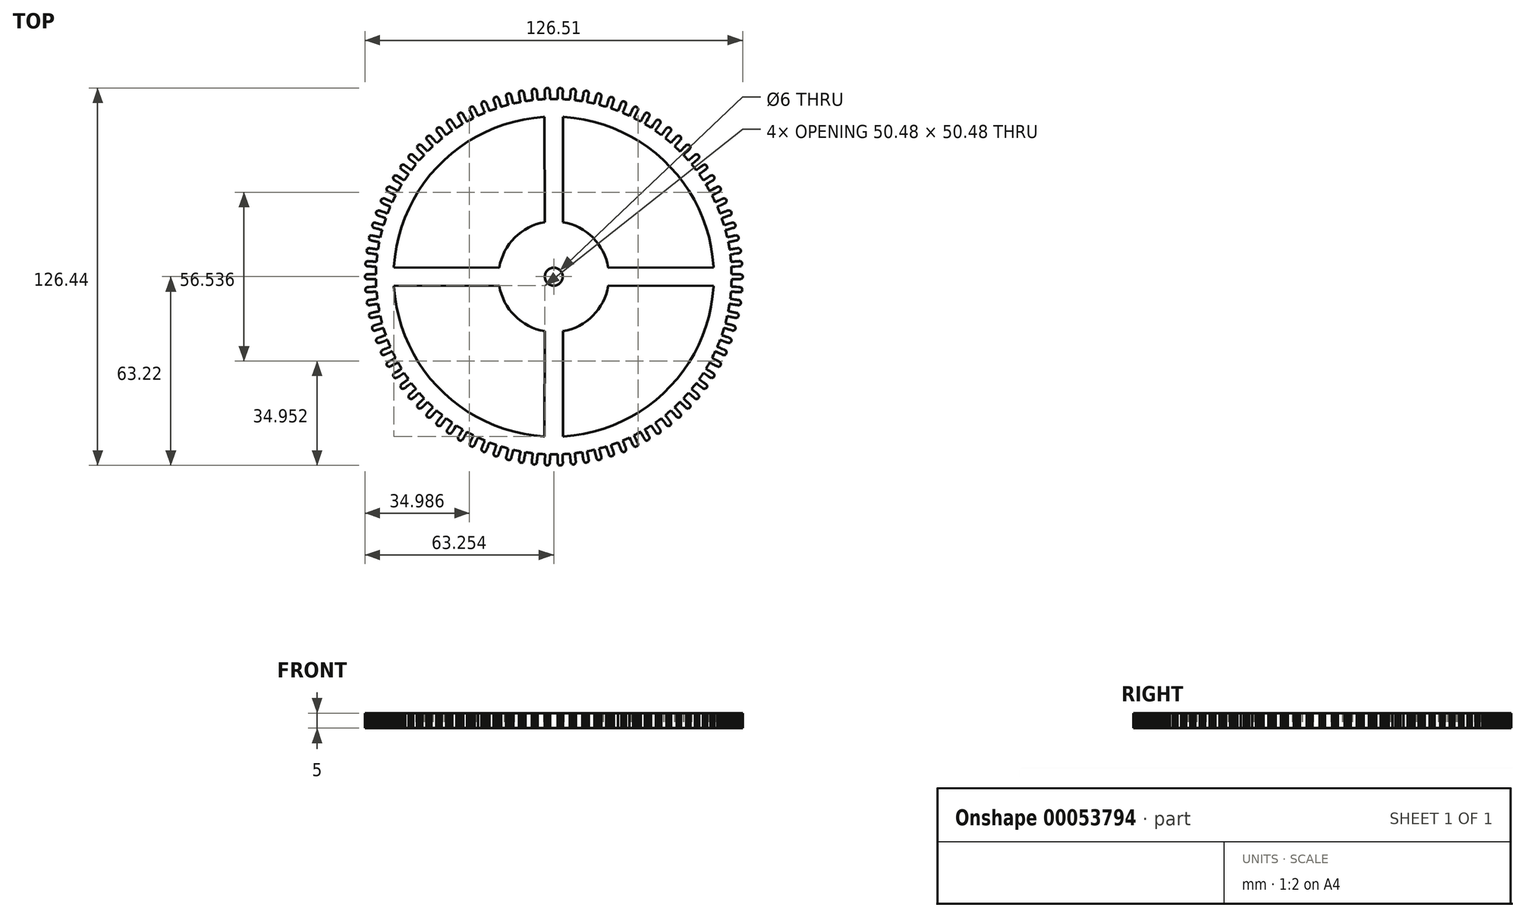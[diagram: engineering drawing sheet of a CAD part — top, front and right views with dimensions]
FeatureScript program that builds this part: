
annotation { "Feature Type Name" : "Feature", "Feature Type Description" : "" }
export const myFeature = defineFeature(function(context is Context, id is Id, definition is map)
    precondition{}
    {
        {
            var Q0;
            Q0=qCreatedBy(makeId("Top.planeOp"),FACE);
            var sketch = newSketch(context, id + "F0", { "sketchPlane" : qUnion([Q0])});
            skLineSegment(sketch, "E0", {"start": v(58.52, -0.83) * mm, "end": v(58.71, -0.83) * mm});
            skLineSegment(sketch, "E1", {"start": v(58.71, -0.83) * mm, "end": v(58.93, -0.83) * mm});
            skLineSegment(sketch, "E2", {"start": v(58.93, -0.83) * mm, "end": v(59.15, -0.84) * mm});
            skLineSegment(sketch, "E3", {"start": v(59.15, -0.84) * mm, "end": v(59.37, -0.84) * mm});
            skLineSegment(sketch, "E4", {"start": v(59.37, -0.84) * mm, "end": v(59.59, -0.84) * mm});
            skLineSegment(sketch, "E5", {"start": v(59.59, -0.84) * mm, "end": v(59.8, -0.85) * mm});
            skLineSegment(sketch, "E6", {"start": v(59.8, -0.85) * mm, "end": v(60.03, -0.85) * mm});
            skLineSegment(sketch, "E7", {"start": v(60.03, -0.85) * mm, "end": v(60.25, -0.85) * mm});
            skLineSegment(sketch, "E8", {"start": v(60.25, -0.85) * mm, "end": v(60.47, -0.85) * mm});
            skLineSegment(sketch, "E9", {"start": v(60.47, -0.85) * mm, "end": v(60.7, -0.86) * mm});
            skLineSegment(sketch, "E10", {"start": v(60.7, -0.86) * mm, "end": v(60.9, -0.86) * mm});
            skLineSegment(sketch, "E11", {"start": v(60.9, -0.86) * mm, "end": v(61.13, -0.86) * mm});
            skLineSegment(sketch, "E12", {"start": v(61.13, -0.86) * mm, "end": v(61.35, -0.87) * mm});
            skLineSegment(sketch, "E13", {"start": v(61.35, -0.87) * mm, "end": v(61.58, -0.84) * mm});
            skLineSegment(sketch, "E14", {"start": v(61.58, -0.84) * mm, "end": v(61.79, -0.75) * mm});
            skLineSegment(sketch, "E15", {"start": v(61.79, -0.75) * mm, "end": v(61.97, -0.62) * mm});
            skLineSegment(sketch, "E16", {"start": v(61.97, -0.62) * mm, "end": v(62.1, -0.44) * mm});
            skLineSegment(sketch, "E17", {"start": v(62.1, -0.44) * mm, "end": v(62.2, -0.23) * mm});
            skLineSegment(sketch, "E18", {"start": v(62.2, -0.23) * mm, "end": v(62.22, 0) * mm});
            skLineSegment(sketch, "E19", {"start": v(62.22, 0) * mm, "end": v(62.2, 0.23) * mm});
            skLineSegment(sketch, "E20", {"start": v(62.2, 0.23) * mm, "end": v(62.1, 0.44) * mm});
            skLineSegment(sketch, "E21", {"start": v(62.1, 0.44) * mm, "end": v(61.97, 0.62) * mm});
            skLineSegment(sketch, "E22", {"start": v(61.97, 0.62) * mm, "end": v(61.79, 0.75) * mm});
            skLineSegment(sketch, "E23", {"start": v(61.79, 0.75) * mm, "end": v(61.58, 0.84) * mm});
            skLineSegment(sketch, "E24", {"start": v(61.58, 0.84) * mm, "end": v(61.35, 0.87) * mm});
            skLineSegment(sketch, "E25", {"start": v(61.35, 0.87) * mm, "end": v(61.13, 0.86) * mm});
            skLineSegment(sketch, "E26", {"start": v(61.13, 0.86) * mm, "end": v(60.91, 0.86) * mm});
            skLineSegment(sketch, "E27", {"start": v(60.91, 0.86) * mm, "end": v(60.7, 0.86) * mm});
            skLineSegment(sketch, "E28", {"start": v(60.7, 0.86) * mm, "end": v(60.47, 0.85) * mm});
            skLineSegment(sketch, "E29", {"start": v(60.47, 0.85) * mm, "end": v(60.25, 0.85) * mm});
            skLineSegment(sketch, "E30", {"start": v(60.25, 0.85) * mm, "end": v(60.03, 0.85) * mm});
            skLineSegment(sketch, "E31", {"start": v(60.03, 0.85) * mm, "end": v(59.81, 0.85) * mm});
            skLineSegment(sketch, "E32", {"start": v(59.81, 0.85) * mm, "end": v(59.6, 0.84) * mm});
            skLineSegment(sketch, "E33", {"start": v(59.6, 0.84) * mm, "end": v(59.37, 0.84) * mm});
            skLineSegment(sketch, "E34", {"start": v(59.37, 0.84) * mm, "end": v(59.15, 0.84) * mm});
            skLineSegment(sketch, "E35", {"start": v(59.15, 0.84) * mm, "end": v(58.94, 0.83) * mm});
            skLineSegment(sketch, "E36", {"start": v(58.94, 0.83) * mm, "end": v(58.71, 0.83) * mm});
            skLineSegment(sketch, "E37", {"start": v(58.71, 0.83) * mm, "end": v(58.52, 0.83) * mm});
            skLineSegment(sketch, "E38", {"start": v(58.52, 0.83) * mm, "end": v(58.52, 1.05) * mm});
            skLineSegment(sketch, "E39", {"start": v(58.52, 1.05) * mm, "end": v(58.5, 1.26) * mm});
            skLineSegment(sketch, "E40", {"start": v(58.5, 1.26) * mm, "end": v(58.5, 1.48) * mm});
            skLineSegment(sketch, "E41", {"start": v(58.5, 1.48) * mm, "end": v(58.5, 1.7) * mm});
            skLineSegment(sketch, "E42", {"start": v(58.5, 1.7) * mm, "end": v(58.48, 1.92) * mm});
            skLineSegment(sketch, "E43", {"start": v(58.48, 1.92) * mm, "end": v(58.48, 2.13) * mm});
            skLineSegment(sketch, "E44", {"start": v(58.48, 2.13) * mm, "end": v(58.47, 2.35) * mm});
            skLineSegment(sketch, "E45", {"start": v(58.47, 2.35) * mm, "end": v(58.46, 2.57) * mm});
            skLineSegment(sketch, "E46", {"start": v(58.46, 2.57) * mm, "end": v(58.45, 2.79) * mm});
            skLineSegment(sketch, "E47", {"start": v(58.45, 2.79) * mm, "end": v(58.45, 3) * mm});
            skLineSegment(sketch, "E48", {"start": v(58.45, 3) * mm, "end": v(58.44, 3.22) * mm});
            skLineSegment(sketch, "E49", {"start": v(58.44, 3.22) * mm, "end": v(58.44, 3.33) * mm});
            skLineSegment(sketch, "E50", {"start": v(58.44, 3.33) * mm, "end": v(58.65, 3.34) * mm});
            skLineSegment(sketch, "E51", {"start": v(58.65, 3.34) * mm, "end": v(58.87, 3.35) * mm});
            skLineSegment(sketch, "E52", {"start": v(58.87, 3.35) * mm, "end": v(59.1, 3.37) * mm});
            skLineSegment(sketch, "E53", {"start": v(59.1, 3.37) * mm, "end": v(59.31, 3.38) * mm});
            skLineSegment(sketch, "E54", {"start": v(59.31, 3.38) * mm, "end": v(59.53, 3.4) * mm});
            skLineSegment(sketch, "E55", {"start": v(59.53, 3.4) * mm, "end": v(59.75, 3.4) * mm});
            skLineSegment(sketch, "E56", {"start": v(59.75, 3.4) * mm, "end": v(59.97, 3.41) * mm});
            skLineSegment(sketch, "E57", {"start": v(59.97, 3.41) * mm, "end": v(60.19, 3.43) * mm});
            skLineSegment(sketch, "E58", {"start": v(60.19, 3.43) * mm, "end": v(60.41, 3.44) * mm});
            skLineSegment(sketch, "E59", {"start": v(60.41, 3.44) * mm, "end": v(60.63, 3.45) * mm});
            skLineSegment(sketch, "E60", {"start": v(60.63, 3.45) * mm, "end": v(60.85, 3.46) * mm});
            skLineSegment(sketch, "E61", {"start": v(60.85, 3.46) * mm, "end": v(61.07, 3.48) * mm});
            skLineSegment(sketch, "E62", {"start": v(61.07, 3.48) * mm, "end": v(61.3, 3.5) * mm});
            skLineSegment(sketch, "E63", {"start": v(61.3, 3.5) * mm, "end": v(61.52, 3.55) * mm});
            skLineSegment(sketch, "E64", {"start": v(61.52, 3.55) * mm, "end": v(61.72, 3.66) * mm});
            skLineSegment(sketch, "E65", {"start": v(61.72, 3.66) * mm, "end": v(61.89, 3.82) * mm});
            skLineSegment(sketch, "E66", {"start": v(61.89, 3.82) * mm, "end": v(62, 4.01) * mm});
            skLineSegment(sketch, "E67", {"start": v(62, 4.01) * mm, "end": v(62.06, 4.23) * mm});
            skLineSegment(sketch, "E68", {"start": v(62.06, 4.23) * mm, "end": v(62.06, 4.46) * mm});
            skLineSegment(sketch, "E69", {"start": v(62.06, 4.46) * mm, "end": v(62, 4.68) * mm});
            skLineSegment(sketch, "E70", {"start": v(62, 4.68) * mm, "end": v(61.9, 4.88) * mm});
            skLineSegment(sketch, "E71", {"start": v(61.9, 4.88) * mm, "end": v(61.74, 5.04) * mm});
            skLineSegment(sketch, "E72", {"start": v(61.74, 5.04) * mm, "end": v(61.54, 5.15) * mm});
            skLineSegment(sketch, "E73", {"start": v(61.54, 5.15) * mm, "end": v(61.32, 5.21) * mm});
            skLineSegment(sketch, "E74", {"start": v(61.32, 5.21) * mm, "end": v(61.18, 5.22) * mm});
            skLineSegment(sketch, "E75", {"start": v(61.18, 5.22) * mm, "end": v(60.95, 5.2) * mm});
            skLineSegment(sketch, "E76", {"start": v(60.95, 5.2) * mm, "end": v(60.73, 5.18) * mm});
            skLineSegment(sketch, "E77", {"start": v(60.73, 5.18) * mm, "end": v(60.52, 5.16) * mm});
            skLineSegment(sketch, "E78", {"start": v(60.52, 5.16) * mm, "end": v(60.3, 5.15) * mm});
            skLineSegment(sketch, "E79", {"start": v(60.3, 5.15) * mm, "end": v(60.08, 5.13) * mm});
            skLineSegment(sketch, "E80", {"start": v(60.08, 5.13) * mm, "end": v(59.86, 5.1) * mm});
            skLineSegment(sketch, "E81", {"start": v(59.86, 5.1) * mm, "end": v(59.63, 5.1) * mm});
            skLineSegment(sketch, "E82", {"start": v(59.63, 5.1) * mm, "end": v(59.42, 5.07) * mm});
            skLineSegment(sketch, "E83", {"start": v(59.42, 5.07) * mm, "end": v(59.2, 5.05) * mm});
            skLineSegment(sketch, "E84", {"start": v(59.2, 5.05) * mm, "end": v(58.98, 5.04) * mm});
            skLineSegment(sketch, "E85", {"start": v(58.98, 5.04) * mm, "end": v(58.76, 5.02) * mm});
            skLineSegment(sketch, "E86", {"start": v(58.76, 5.02) * mm, "end": v(58.54, 5) * mm});
            skLineSegment(sketch, "E87", {"start": v(58.54, 5) * mm, "end": v(58.32, 4.98) * mm});
            skLineSegment(sketch, "E88", {"start": v(58.32, 4.98) * mm, "end": v(58.3, 5.2) * mm});
            skLineSegment(sketch, "E89", {"start": v(58.3, 5.2) * mm, "end": v(58.27, 5.41) * mm});
            skLineSegment(sketch, "E90", {"start": v(58.27, 5.41) * mm, "end": v(58.25, 5.63) * mm});
            skLineSegment(sketch, "E91", {"start": v(58.25, 5.63) * mm, "end": v(58.23, 5.85) * mm});
            skLineSegment(sketch, "E92", {"start": v(58.23, 5.85) * mm, "end": v(58.2, 6.06) * mm});
            skLineSegment(sketch, "E93", {"start": v(58.2, 6.06) * mm, "end": v(58.18, 6.28) * mm});
            skLineSegment(sketch, "E94", {"start": v(58.18, 6.28) * mm, "end": v(58.16, 6.5) * mm});
            skLineSegment(sketch, "E95", {"start": v(58.16, 6.5) * mm, "end": v(58.14, 6.71) * mm});
            skLineSegment(sketch, "E96", {"start": v(58.14, 6.71) * mm, "end": v(58.11, 6.93) * mm});
            skLineSegment(sketch, "E97", {"start": v(58.11, 6.93) * mm, "end": v(58.1, 7.15) * mm});
            skLineSegment(sketch, "E98", {"start": v(58.1, 7.15) * mm, "end": v(58.07, 7.36) * mm});
            skLineSegment(sketch, "E99", {"start": v(58.07, 7.36) * mm, "end": v(58.06, 7.47) * mm});
            skLineSegment(sketch, "E100", {"start": v(58.06, 7.47) * mm, "end": v(58.27, 7.5) * mm});
            skLineSegment(sketch, "E101", {"start": v(58.27, 7.5) * mm, "end": v(58.5, 7.52) * mm});
            skLineSegment(sketch, "E102", {"start": v(58.5, 7.52) * mm, "end": v(58.71, 7.55) * mm});
            skLineSegment(sketch, "E103", {"start": v(58.71, 7.55) * mm, "end": v(58.93, 7.58) * mm});
            skLineSegment(sketch, "E104", {"start": v(58.93, 7.58) * mm, "end": v(59.15, 7.6) * mm});
            skLineSegment(sketch, "E105", {"start": v(59.15, 7.6) * mm, "end": v(59.37, 7.63) * mm});
            skLineSegment(sketch, "E106", {"start": v(59.37, 7.63) * mm, "end": v(59.58, 7.66) * mm});
            skLineSegment(sketch, "E107", {"start": v(59.58, 7.66) * mm, "end": v(59.8, 7.69) * mm});
            skLineSegment(sketch, "E108", {"start": v(59.8, 7.69) * mm, "end": v(60.02, 7.72) * mm});
            skLineSegment(sketch, "E109", {"start": v(60.02, 7.72) * mm, "end": v(60.24, 7.74) * mm});
            skLineSegment(sketch, "E110", {"start": v(60.24, 7.74) * mm, "end": v(60.45, 7.77) * mm});
            skLineSegment(sketch, "E111", {"start": v(60.45, 7.77) * mm, "end": v(60.68, 7.8) * mm});
            skLineSegment(sketch, "E112", {"start": v(60.68, 7.8) * mm, "end": v(60.9, 7.83) * mm});
            skLineSegment(sketch, "E113", {"start": v(60.9, 7.83) * mm, "end": v(61.12, 7.9) * mm});
            skLineSegment(sketch, "E114", {"start": v(61.12, 7.9) * mm, "end": v(61.31, 8.03) * mm});
            skLineSegment(sketch, "E115", {"start": v(61.31, 8.03) * mm, "end": v(61.47, 8.2) * mm});
            skLineSegment(sketch, "E116", {"start": v(61.47, 8.2) * mm, "end": v(61.57, 8.4) * mm});
            skLineSegment(sketch, "E117", {"start": v(61.57, 8.4) * mm, "end": v(61.61, 8.62) * mm});
            skLineSegment(sketch, "E118", {"start": v(61.61, 8.62) * mm, "end": v(61.6, 8.85) * mm});
            skLineSegment(sketch, "E119", {"start": v(61.6, 8.85) * mm, "end": v(61.53, 9.06) * mm});
            skLineSegment(sketch, "E120", {"start": v(61.53, 9.06) * mm, "end": v(61.4, 9.25) * mm});
            skLineSegment(sketch, "E121", {"start": v(61.4, 9.25) * mm, "end": v(61.23, 9.4) * mm});
            skLineSegment(sketch, "E122", {"start": v(61.23, 9.4) * mm, "end": v(61.03, 9.5) * mm});
            skLineSegment(sketch, "E123", {"start": v(61.03, 9.5) * mm, "end": v(60.8, 9.55) * mm});
            skLineSegment(sketch, "E124", {"start": v(60.8, 9.55) * mm, "end": v(60.76, 9.55) * mm});
            skLineSegment(sketch, "E125", {"start": v(60.76, 9.55) * mm, "end": v(60.53, 9.53) * mm});
            skLineSegment(sketch, "E126", {"start": v(60.53, 9.53) * mm, "end": v(60.31, 9.5) * mm});
            skLineSegment(sketch, "E127", {"start": v(60.31, 9.5) * mm, "end": v(60.1, 9.46) * mm});
            skLineSegment(sketch, "E128", {"start": v(60.1, 9.46) * mm, "end": v(59.88, 9.43) * mm});
            skLineSegment(sketch, "E129", {"start": v(59.88, 9.43) * mm, "end": v(59.66, 9.4) * mm});
            skLineSegment(sketch, "E130", {"start": v(59.66, 9.4) * mm, "end": v(59.45, 9.36) * mm});
            skLineSegment(sketch, "E131", {"start": v(59.45, 9.36) * mm, "end": v(59.23, 9.32) * mm});
            skLineSegment(sketch, "E132", {"start": v(59.23, 9.32) * mm, "end": v(59, 9.3) * mm});
            skLineSegment(sketch, "E133", {"start": v(59, 9.3) * mm, "end": v(58.8, 9.26) * mm});
            skLineSegment(sketch, "E134", {"start": v(58.8, 9.26) * mm, "end": v(58.57, 9.22) * mm});
            skLineSegment(sketch, "E135", {"start": v(58.57, 9.22) * mm, "end": v(58.36, 9.2) * mm});
            skLineSegment(sketch, "E136", {"start": v(58.36, 9.2) * mm, "end": v(58.14, 9.16) * mm});
            skLineSegment(sketch, "E137", {"start": v(58.14, 9.16) * mm, "end": v(57.92, 9.12) * mm});
            skLineSegment(sketch, "E138", {"start": v(57.92, 9.12) * mm, "end": v(57.83, 9.1) * mm});
            skLineSegment(sketch, "E139", {"start": v(57.83, 9.1) * mm, "end": v(57.8, 9.32) * mm});
            skLineSegment(sketch, "E140", {"start": v(57.8, 9.32) * mm, "end": v(57.75, 9.54) * mm});
            skLineSegment(sketch, "E141", {"start": v(57.75, 9.54) * mm, "end": v(57.71, 9.75) * mm});
            skLineSegment(sketch, "E142", {"start": v(57.71, 9.75) * mm, "end": v(57.68, 9.97) * mm});
            skLineSegment(sketch, "E143", {"start": v(57.68, 9.97) * mm, "end": v(57.64, 10.18) * mm});
            skLineSegment(sketch, "E144", {"start": v(57.64, 10.18) * mm, "end": v(57.6, 10.4) * mm});
            skLineSegment(sketch, "E145", {"start": v(57.6, 10.4) * mm, "end": v(57.56, 10.61) * mm});
            skLineSegment(sketch, "E146", {"start": v(57.56, 10.61) * mm, "end": v(57.53, 10.82) * mm});
            skLineSegment(sketch, "E147", {"start": v(57.53, 10.82) * mm, "end": v(57.49, 11.04) * mm});
            skLineSegment(sketch, "E148", {"start": v(57.49, 11.04) * mm, "end": v(57.45, 11.25) * mm});
            skLineSegment(sketch, "E149", {"start": v(57.45, 11.25) * mm, "end": v(57.41, 11.47) * mm});
            skLineSegment(sketch, "E150", {"start": v(57.41, 11.47) * mm, "end": v(57.4, 11.57) * mm});
            skLineSegment(sketch, "E151", {"start": v(57.4, 11.57) * mm, "end": v(57.6, 11.62) * mm});
            skLineSegment(sketch, "E152", {"start": v(57.6, 11.62) * mm, "end": v(57.82, 11.66) * mm});
            skLineSegment(sketch, "E153", {"start": v(57.82, 11.66) * mm, "end": v(58.04, 11.7) * mm});
            skLineSegment(sketch, "E154", {"start": v(58.04, 11.7) * mm, "end": v(58.25, 11.74) * mm});
            skLineSegment(sketch, "E155", {"start": v(58.25, 11.74) * mm, "end": v(58.47, 11.79) * mm});
            skLineSegment(sketch, "E156", {"start": v(58.47, 11.79) * mm, "end": v(58.69, 11.83) * mm});
            skLineSegment(sketch, "E157", {"start": v(58.69, 11.83) * mm, "end": v(58.9, 11.87) * mm});
            skLineSegment(sketch, "E158", {"start": v(58.9, 11.87) * mm, "end": v(59.12, 11.91) * mm});
            skLineSegment(sketch, "E159", {"start": v(59.12, 11.91) * mm, "end": v(59.33, 11.96) * mm});
            skLineSegment(sketch, "E160", {"start": v(59.33, 11.96) * mm, "end": v(59.55, 12) * mm});
            skLineSegment(sketch, "E161", {"start": v(59.55, 12) * mm, "end": v(59.76, 12.04) * mm});
            skLineSegment(sketch, "E162", {"start": v(59.76, 12.04) * mm, "end": v(59.98, 12.09) * mm});
            skLineSegment(sketch, "E163", {"start": v(59.98, 12.09) * mm, "end": v(60.21, 12.13) * mm});
            skLineSegment(sketch, "E164", {"start": v(60.21, 12.13) * mm, "end": v(60.42, 12.22) * mm});
            skLineSegment(sketch, "E165", {"start": v(60.42, 12.22) * mm, "end": v(60.6, 12.36) * mm});
            skLineSegment(sketch, "E166", {"start": v(60.6, 12.36) * mm, "end": v(60.74, 12.54) * mm});
            skLineSegment(sketch, "E167", {"start": v(60.74, 12.54) * mm, "end": v(60.83, 12.75) * mm});
            skLineSegment(sketch, "E168", {"start": v(60.83, 12.75) * mm, "end": v(60.86, 12.97) * mm});
            skLineSegment(sketch, "E169", {"start": v(60.86, 12.97) * mm, "end": v(60.83, 13.2) * mm});
            skLineSegment(sketch, "E170", {"start": v(60.83, 13.2) * mm, "end": v(60.74, 13.4) * mm});
            skLineSegment(sketch, "E171", {"start": v(60.74, 13.4) * mm, "end": v(60.6, 13.59) * mm});
            skLineSegment(sketch, "E172", {"start": v(60.6, 13.59) * mm, "end": v(60.42, 13.72) * mm});
            skLineSegment(sketch, "E173", {"start": v(60.42, 13.72) * mm, "end": v(60.21, 13.81) * mm});
            skLineSegment(sketch, "E174", {"start": v(60.21, 13.81) * mm, "end": v(59.99, 13.84) * mm});
            skLineSegment(sketch, "E175", {"start": v(59.99, 13.84) * mm, "end": v(59.77, 13.8) * mm});
            skLineSegment(sketch, "E176", {"start": v(59.77, 13.8) * mm, "end": v(59.56, 13.76) * mm});
            skLineSegment(sketch, "E177", {"start": v(59.56, 13.76) * mm, "end": v(59.35, 13.71) * mm});
            skLineSegment(sketch, "E178", {"start": v(59.35, 13.71) * mm, "end": v(59.13, 13.67) * mm});
            skLineSegment(sketch, "E179", {"start": v(59.13, 13.67) * mm, "end": v(58.92, 13.62) * mm});
            skLineSegment(sketch, "E180", {"start": v(58.92, 13.62) * mm, "end": v(58.7, 13.57) * mm});
            skLineSegment(sketch, "E181", {"start": v(58.7, 13.57) * mm, "end": v(58.5, 13.52) * mm});
            skLineSegment(sketch, "E182", {"start": v(58.5, 13.52) * mm, "end": v(58.28, 13.47) * mm});
            skLineSegment(sketch, "E183", {"start": v(58.28, 13.47) * mm, "end": v(58.06, 13.42) * mm});
            skLineSegment(sketch, "E184", {"start": v(58.06, 13.42) * mm, "end": v(57.85, 13.37) * mm});
            skLineSegment(sketch, "E185", {"start": v(57.85, 13.37) * mm, "end": v(57.64, 13.33) * mm});
            skLineSegment(sketch, "E186", {"start": v(57.64, 13.33) * mm, "end": v(57.42, 13.28) * mm});
            skLineSegment(sketch, "E187", {"start": v(57.42, 13.28) * mm, "end": v(57.2, 13.23) * mm});
            skLineSegment(sketch, "E188", {"start": v(57.2, 13.23) * mm, "end": v(57.05, 13.2) * mm});
            skLineSegment(sketch, "E189", {"start": v(57.05, 13.2) * mm, "end": v(57, 13.4) * mm});
            skLineSegment(sketch, "E190", {"start": v(57, 13.4) * mm, "end": v(56.94, 13.62) * mm});
            skLineSegment(sketch, "E191", {"start": v(56.94, 13.62) * mm, "end": v(56.9, 13.83) * mm});
            skLineSegment(sketch, "E192", {"start": v(56.9, 13.83) * mm, "end": v(56.84, 14.04) * mm});
            skLineSegment(sketch, "E193", {"start": v(56.84, 14.04) * mm, "end": v(56.79, 14.25) * mm});
            skLineSegment(sketch, "E194", {"start": v(56.79, 14.25) * mm, "end": v(56.73, 14.46) * mm});
            skLineSegment(sketch, "E195", {"start": v(56.73, 14.46) * mm, "end": v(56.68, 14.67) * mm});
            skLineSegment(sketch, "E196", {"start": v(56.68, 14.67) * mm, "end": v(56.63, 14.88) * mm});
            skLineSegment(sketch, "E197", {"start": v(56.63, 14.88) * mm, "end": v(56.57, 15.1) * mm});
            skLineSegment(sketch, "E198", {"start": v(56.57, 15.1) * mm, "end": v(56.52, 15.3) * mm});
            skLineSegment(sketch, "E199", {"start": v(56.52, 15.3) * mm, "end": v(56.47, 15.52) * mm});
            skLineSegment(sketch, "E200", {"start": v(56.47, 15.52) * mm, "end": v(56.44, 15.62) * mm});
            skLineSegment(sketch, "E201", {"start": v(56.44, 15.62) * mm, "end": v(56.65, 15.68) * mm});
            skLineSegment(sketch, "E202", {"start": v(56.65, 15.68) * mm, "end": v(56.86, 15.74) * mm});
            skLineSegment(sketch, "E203", {"start": v(56.86, 15.74) * mm, "end": v(57.08, 15.8) * mm});
            skLineSegment(sketch, "E204", {"start": v(57.08, 15.8) * mm, "end": v(57.3, 15.85) * mm});
            skLineSegment(sketch, "E205", {"start": v(57.3, 15.85) * mm, "end": v(57.5, 15.9) * mm});
            skLineSegment(sketch, "E206", {"start": v(57.5, 15.9) * mm, "end": v(57.72, 15.97) * mm});
            skLineSegment(sketch, "E207", {"start": v(57.72, 15.97) * mm, "end": v(57.93, 16.02) * mm});
            skLineSegment(sketch, "E208", {"start": v(57.93, 16.02) * mm, "end": v(58.14, 16.08) * mm});
            skLineSegment(sketch, "E209", {"start": v(58.14, 16.08) * mm, "end": v(58.35, 16.14) * mm});
            skLineSegment(sketch, "E210", {"start": v(58.35, 16.14) * mm, "end": v(58.56, 16.2) * mm});
            skLineSegment(sketch, "E211", {"start": v(58.56, 16.2) * mm, "end": v(58.77, 16.25) * mm});
            skLineSegment(sketch, "E212", {"start": v(58.77, 16.25) * mm, "end": v(59, 16.31) * mm});
            skLineSegment(sketch, "E213", {"start": v(59, 16.31) * mm, "end": v(59.22, 16.38) * mm});
            skLineSegment(sketch, "E214", {"start": v(59.22, 16.38) * mm, "end": v(59.42, 16.48) * mm});
            skLineSegment(sketch, "E215", {"start": v(59.42, 16.48) * mm, "end": v(59.6, 16.63) * mm});
            skLineSegment(sketch, "E216", {"start": v(59.6, 16.63) * mm, "end": v(59.72, 16.81) * mm});
            skLineSegment(sketch, "E217", {"start": v(59.72, 16.81) * mm, "end": v(59.79, 17.03) * mm});
            skLineSegment(sketch, "E218", {"start": v(59.79, 17.03) * mm, "end": v(59.8, 17.26) * mm});
            skLineSegment(sketch, "E219", {"start": v(59.8, 17.26) * mm, "end": v(59.76, 17.48) * mm});
            skLineSegment(sketch, "E220", {"start": v(59.76, 17.48) * mm, "end": v(59.66, 17.68) * mm});
            skLineSegment(sketch, "E221", {"start": v(59.66, 17.68) * mm, "end": v(59.5, 17.85) * mm});
            skLineSegment(sketch, "E222", {"start": v(59.5, 17.85) * mm, "end": v(59.32, 17.98) * mm});
            skLineSegment(sketch, "E223", {"start": v(59.32, 17.98) * mm, "end": v(59.1, 18.05) * mm});
            skLineSegment(sketch, "E224", {"start": v(59.1, 18.05) * mm, "end": v(58.92, 18.06) * mm});
            skLineSegment(sketch, "E225", {"start": v(58.92, 18.06) * mm, "end": v(58.7, 18.03) * mm});
            skLineSegment(sketch, "E226", {"start": v(58.7, 18.03) * mm, "end": v(58.49, 17.97) * mm});
            skLineSegment(sketch, "E227", {"start": v(58.49, 17.97) * mm, "end": v(58.28, 17.9) * mm});
            skLineSegment(sketch, "E228", {"start": v(58.28, 17.9) * mm, "end": v(58.06, 17.84) * mm});
            skLineSegment(sketch, "E229", {"start": v(58.06, 17.84) * mm, "end": v(57.85, 17.78) * mm});
            skLineSegment(sketch, "E230", {"start": v(57.85, 17.78) * mm, "end": v(57.65, 17.71) * mm});
            skLineSegment(sketch, "E231", {"start": v(57.65, 17.71) * mm, "end": v(57.43, 17.65) * mm});
            skLineSegment(sketch, "E232", {"start": v(57.43, 17.65) * mm, "end": v(57.22, 17.58) * mm});
            skLineSegment(sketch, "E233", {"start": v(57.22, 17.58) * mm, "end": v(57.01, 17.52) * mm});
            skLineSegment(sketch, "E234", {"start": v(57.01, 17.52) * mm, "end": v(56.8, 17.46) * mm});
            skLineSegment(sketch, "E235", {"start": v(56.8, 17.46) * mm, "end": v(56.6, 17.4) * mm});
            skLineSegment(sketch, "E236", {"start": v(56.6, 17.4) * mm, "end": v(56.38, 17.33) * mm});
            skLineSegment(sketch, "E237", {"start": v(56.38, 17.33) * mm, "end": v(56.17, 17.27) * mm});
            skLineSegment(sketch, "E238", {"start": v(56.17, 17.27) * mm, "end": v(55.99, 17.21) * mm});
            skLineSegment(sketch, "E239", {"start": v(55.99, 17.21) * mm, "end": v(55.92, 17.42) * mm});
            skLineSegment(sketch, "E240", {"start": v(55.92, 17.42) * mm, "end": v(55.85, 17.63) * mm});
            skLineSegment(sketch, "E241", {"start": v(55.85, 17.63) * mm, "end": v(55.79, 17.83) * mm});
            skLineSegment(sketch, "E242", {"start": v(55.79, 17.83) * mm, "end": v(55.72, 18.04) * mm});
            skLineSegment(sketch, "E243", {"start": v(55.72, 18.04) * mm, "end": v(55.65, 18.25) * mm});
            skLineSegment(sketch, "E244", {"start": v(55.65, 18.25) * mm, "end": v(55.58, 18.46) * mm});
            skLineSegment(sketch, "E245", {"start": v(55.58, 18.46) * mm, "end": v(55.52, 18.66) * mm});
            skLineSegment(sketch, "E246", {"start": v(55.52, 18.66) * mm, "end": v(55.45, 18.87) * mm});
            skLineSegment(sketch, "E247", {"start": v(55.45, 18.87) * mm, "end": v(55.38, 19.08) * mm});
            skLineSegment(sketch, "E248", {"start": v(55.38, 19.08) * mm, "end": v(55.31, 19.28) * mm});
            skLineSegment(sketch, "E249", {"start": v(55.31, 19.28) * mm, "end": v(55.25, 19.5) * mm});
            skLineSegment(sketch, "E250", {"start": v(55.25, 19.5) * mm, "end": v(55.21, 19.6) * mm});
            skLineSegment(sketch, "E251", {"start": v(55.21, 19.6) * mm, "end": v(55.42, 19.66) * mm});
            skLineSegment(sketch, "E252", {"start": v(55.42, 19.66) * mm, "end": v(55.63, 19.74) * mm});
            skLineSegment(sketch, "E253", {"start": v(55.63, 19.74) * mm, "end": v(55.84, 19.8) * mm});
            skLineSegment(sketch, "E254", {"start": v(55.84, 19.8) * mm, "end": v(56.04, 19.88) * mm});
            skLineSegment(sketch, "E255", {"start": v(56.04, 19.88) * mm, "end": v(56.25, 19.95) * mm});
            skLineSegment(sketch, "E256", {"start": v(56.25, 19.95) * mm, "end": v(56.46, 20.03) * mm});
            skLineSegment(sketch, "E257", {"start": v(56.46, 20.03) * mm, "end": v(56.67, 20.1) * mm});
            skLineSegment(sketch, "E258", {"start": v(56.67, 20.1) * mm, "end": v(56.87, 20.17) * mm});
            skLineSegment(sketch, "E259", {"start": v(56.87, 20.17) * mm, "end": v(57.08, 20.24) * mm});
            skLineSegment(sketch, "E260", {"start": v(57.08, 20.24) * mm, "end": v(57.29, 20.32) * mm});
            skLineSegment(sketch, "E261", {"start": v(57.29, 20.32) * mm, "end": v(57.5, 20.39) * mm});
            skLineSegment(sketch, "E262", {"start": v(57.5, 20.39) * mm, "end": v(57.7, 20.46) * mm});
            skLineSegment(sketch, "E263", {"start": v(57.7, 20.46) * mm, "end": v(57.93, 20.54) * mm});
            skLineSegment(sketch, "E264", {"start": v(57.93, 20.54) * mm, "end": v(58.12, 20.65) * mm});
            skLineSegment(sketch, "E265", {"start": v(58.12, 20.65) * mm, "end": v(58.28, 20.81) * mm});
            skLineSegment(sketch, "E266", {"start": v(58.28, 20.81) * mm, "end": v(58.4, 21.01) * mm});
            skLineSegment(sketch, "E267", {"start": v(58.4, 21.01) * mm, "end": v(58.45, 21.23) * mm});
            skLineSegment(sketch, "E268", {"start": v(58.45, 21.23) * mm, "end": v(58.45, 21.46) * mm});
            skLineSegment(sketch, "E269", {"start": v(58.45, 21.46) * mm, "end": v(58.4, 21.68) * mm});
            skLineSegment(sketch, "E270", {"start": v(58.4, 21.68) * mm, "end": v(58.28, 21.87) * mm});
            skLineSegment(sketch, "E271", {"start": v(58.28, 21.87) * mm, "end": v(58.11, 22.03) * mm});
            skLineSegment(sketch, "E272", {"start": v(58.11, 22.03) * mm, "end": v(57.92, 22.14) * mm});
            skLineSegment(sketch, "E273", {"start": v(57.92, 22.14) * mm, "end": v(57.7, 22.2) * mm});
            skLineSegment(sketch, "E274", {"start": v(57.7, 22.2) * mm, "end": v(57.6, 22.2) * mm});
            skLineSegment(sketch, "E275", {"start": v(57.6, 22.2) * mm, "end": v(57.38, 22.18) * mm});
            skLineSegment(sketch, "E276", {"start": v(57.38, 22.18) * mm, "end": v(57.17, 22.1) * mm});
            skLineSegment(sketch, "E277", {"start": v(57.17, 22.1) * mm, "end": v(56.97, 22.03) * mm});
            skLineSegment(sketch, "E278", {"start": v(56.97, 22.03) * mm, "end": v(56.76, 21.95) * mm});
            skLineSegment(sketch, "E279", {"start": v(56.76, 21.95) * mm, "end": v(56.56, 21.87) * mm});
            skLineSegment(sketch, "E280", {"start": v(56.56, 21.87) * mm, "end": v(56.36, 21.8) * mm});
            skLineSegment(sketch, "E281", {"start": v(56.36, 21.8) * mm, "end": v(56.15, 21.72) * mm});
            skLineSegment(sketch, "E282", {"start": v(56.15, 21.72) * mm, "end": v(55.94, 21.64) * mm});
            skLineSegment(sketch, "E283", {"start": v(55.94, 21.64) * mm, "end": v(55.74, 21.56) * mm});
            skLineSegment(sketch, "E284", {"start": v(55.74, 21.56) * mm, "end": v(55.53, 21.48) * mm});
            skLineSegment(sketch, "E285", {"start": v(55.53, 21.48) * mm, "end": v(55.33, 21.4) * mm});
            skLineSegment(sketch, "E286", {"start": v(55.33, 21.4) * mm, "end": v(55.12, 21.33) * mm});
            skLineSegment(sketch, "E287", {"start": v(55.12, 21.33) * mm, "end": v(54.91, 21.25) * mm});
            skLineSegment(sketch, "E288", {"start": v(54.91, 21.25) * mm, "end": v(54.7, 21.17) * mm});
            skLineSegment(sketch, "E289", {"start": v(54.7, 21.17) * mm, "end": v(54.65, 21.15) * mm});
            skLineSegment(sketch, "E290", {"start": v(54.65, 21.15) * mm, "end": v(54.57, 21.35) * mm});
            skLineSegment(sketch, "E291", {"start": v(54.57, 21.35) * mm, "end": v(54.48, 21.55) * mm});
            skLineSegment(sketch, "E292", {"start": v(54.48, 21.55) * mm, "end": v(54.4, 21.75) * mm});
            skLineSegment(sketch, "E293", {"start": v(54.4, 21.75) * mm, "end": v(54.32, 21.96) * mm});
            skLineSegment(sketch, "E294", {"start": v(54.32, 21.96) * mm, "end": v(54.24, 22.16) * mm});
            skLineSegment(sketch, "E295", {"start": v(54.24, 22.16) * mm, "end": v(54.16, 22.36) * mm});
            skLineSegment(sketch, "E296", {"start": v(54.16, 22.36) * mm, "end": v(54.08, 22.56) * mm});
            skLineSegment(sketch, "E297", {"start": v(54.08, 22.56) * mm, "end": v(54, 22.76) * mm});
            skLineSegment(sketch, "E298", {"start": v(54, 22.76) * mm, "end": v(53.91, 22.97) * mm});
            skLineSegment(sketch, "E299", {"start": v(53.91, 22.97) * mm, "end": v(53.83, 23.17) * mm});
            skLineSegment(sketch, "E300", {"start": v(53.83, 23.17) * mm, "end": v(53.75, 23.37) * mm});
            skLineSegment(sketch, "E301", {"start": v(53.75, 23.37) * mm, "end": v(53.71, 23.47) * mm});
            skLineSegment(sketch, "E302", {"start": v(53.71, 23.47) * mm, "end": v(53.91, 23.55) * mm});
            skLineSegment(sketch, "E303", {"start": v(53.91, 23.55) * mm, "end": v(54.11, 23.64) * mm});
            skLineSegment(sketch, "E304", {"start": v(54.11, 23.64) * mm, "end": v(54.32, 23.73) * mm});
            skLineSegment(sketch, "E305", {"start": v(54.32, 23.73) * mm, "end": v(54.52, 23.81) * mm});
            skLineSegment(sketch, "E306", {"start": v(54.52, 23.81) * mm, "end": v(54.72, 23.9) * mm});
            skLineSegment(sketch, "E307", {"start": v(54.72, 23.9) * mm, "end": v(54.92, 23.99) * mm});
            skLineSegment(sketch, "E308", {"start": v(54.92, 23.99) * mm, "end": v(55.12, 24.07) * mm});
            skLineSegment(sketch, "E309", {"start": v(55.12, 24.07) * mm, "end": v(55.32, 24.16) * mm});
            skLineSegment(sketch, "E310", {"start": v(55.32, 24.16) * mm, "end": v(55.53, 24.25) * mm});
            skLineSegment(sketch, "E311", {"start": v(55.53, 24.25) * mm, "end": v(55.73, 24.33) * mm});
            skLineSegment(sketch, "E312", {"start": v(55.73, 24.33) * mm, "end": v(55.93, 24.42) * mm});
            skLineSegment(sketch, "E313", {"start": v(55.93, 24.42) * mm, "end": v(56.14, 24.5) * mm});
            skLineSegment(sketch, "E314", {"start": v(56.14, 24.5) * mm, "end": v(56.35, 24.6) * mm});
            skLineSegment(sketch, "E315", {"start": v(56.35, 24.6) * mm, "end": v(56.54, 24.73) * mm});
            skLineSegment(sketch, "E316", {"start": v(56.54, 24.73) * mm, "end": v(56.69, 24.9) * mm});
            skLineSegment(sketch, "E317", {"start": v(56.69, 24.9) * mm, "end": v(56.79, 25.1) * mm});
            skLineSegment(sketch, "E318", {"start": v(56.79, 25.1) * mm, "end": v(56.83, 25.33) * mm});
            skLineSegment(sketch, "E319", {"start": v(56.83, 25.33) * mm, "end": v(56.81, 25.56) * mm});
            skLineSegment(sketch, "E320", {"start": v(56.81, 25.56) * mm, "end": v(56.73, 25.77) * mm});
            skLineSegment(sketch, "E321", {"start": v(56.73, 25.77) * mm, "end": v(56.6, 25.96) * mm});
            skLineSegment(sketch, "E322", {"start": v(56.6, 25.96) * mm, "end": v(56.43, 26.1) * mm});
            skLineSegment(sketch, "E323", {"start": v(56.43, 26.1) * mm, "end": v(56.23, 26.2) * mm});
            skLineSegment(sketch, "E324", {"start": v(56.23, 26.2) * mm, "end": v(56, 26.24) * mm});
            skLineSegment(sketch, "E325", {"start": v(56, 26.24) * mm, "end": v(55.96, 26.24) * mm});
            skLineSegment(sketch, "E326", {"start": v(55.96, 26.24) * mm, "end": v(55.73, 26.21) * mm});
            skLineSegment(sketch, "E327", {"start": v(55.73, 26.21) * mm, "end": v(55.52, 26.13) * mm});
            skLineSegment(sketch, "E328", {"start": v(55.52, 26.13) * mm, "end": v(55.32, 26.04) * mm});
            skLineSegment(sketch, "E329", {"start": v(55.32, 26.04) * mm, "end": v(55.12, 25.94) * mm});
            skLineSegment(sketch, "E330", {"start": v(55.12, 25.94) * mm, "end": v(54.92, 25.85) * mm});
            skLineSegment(sketch, "E331", {"start": v(54.92, 25.85) * mm, "end": v(54.72, 25.76) * mm});
            skLineSegment(sketch, "E332", {"start": v(54.72, 25.76) * mm, "end": v(54.52, 25.67) * mm});
            skLineSegment(sketch, "E333", {"start": v(54.52, 25.67) * mm, "end": v(54.32, 25.57) * mm});
            skLineSegment(sketch, "E334", {"start": v(54.32, 25.57) * mm, "end": v(54.12, 25.48) * mm});
            skLineSegment(sketch, "E335", {"start": v(54.12, 25.48) * mm, "end": v(53.92, 25.4) * mm});
            skLineSegment(sketch, "E336", {"start": v(53.92, 25.4) * mm, "end": v(53.72, 25.3) * mm});
            skLineSegment(sketch, "E337", {"start": v(53.72, 25.3) * mm, "end": v(53.52, 25.2) * mm});
            skLineSegment(sketch, "E338", {"start": v(53.52, 25.2) * mm, "end": v(53.33, 25.11) * mm});
            skLineSegment(sketch, "E339", {"start": v(53.33, 25.11) * mm, "end": v(53.12, 25.02) * mm});
            skLineSegment(sketch, "E340", {"start": v(53.12, 25.02) * mm, "end": v(53.04, 24.98) * mm});
            skLineSegment(sketch, "E341", {"start": v(53.04, 24.98) * mm, "end": v(52.94, 25.18) * mm});
            skLineSegment(sketch, "E342", {"start": v(52.94, 25.18) * mm, "end": v(52.85, 25.37) * mm});
            skLineSegment(sketch, "E343", {"start": v(52.85, 25.37) * mm, "end": v(52.75, 25.57) * mm});
            skLineSegment(sketch, "E344", {"start": v(52.75, 25.57) * mm, "end": v(52.65, 25.76) * mm});
            skLineSegment(sketch, "E345", {"start": v(52.65, 25.76) * mm, "end": v(52.56, 25.96) * mm});
            skLineSegment(sketch, "E346", {"start": v(52.56, 25.96) * mm, "end": v(52.46, 26.16) * mm});
            skLineSegment(sketch, "E347", {"start": v(52.46, 26.16) * mm, "end": v(52.37, 26.35) * mm});
            skLineSegment(sketch, "E348", {"start": v(52.37, 26.35) * mm, "end": v(52.27, 26.55) * mm});
            skLineSegment(sketch, "E349", {"start": v(52.27, 26.55) * mm, "end": v(52.18, 26.74) * mm});
            skLineSegment(sketch, "E350", {"start": v(52.18, 26.74) * mm, "end": v(52.08, 26.94) * mm});
            skLineSegment(sketch, "E351", {"start": v(52.08, 26.94) * mm, "end": v(51.99, 27.13) * mm});
            skLineSegment(sketch, "E352", {"start": v(51.99, 27.13) * mm, "end": v(51.94, 27.23) * mm});
            skLineSegment(sketch, "E353", {"start": v(51.94, 27.23) * mm, "end": v(52.13, 27.33) * mm});
            skLineSegment(sketch, "E354", {"start": v(52.13, 27.33) * mm, "end": v(52.33, 27.43) * mm});
            skLineSegment(sketch, "E355", {"start": v(52.33, 27.43) * mm, "end": v(52.53, 27.53) * mm});
            skLineSegment(sketch, "E356", {"start": v(52.53, 27.53) * mm, "end": v(52.72, 27.63) * mm});
            skLineSegment(sketch, "E357", {"start": v(52.72, 27.63) * mm, "end": v(52.91, 27.73) * mm});
            skLineSegment(sketch, "E358", {"start": v(52.91, 27.73) * mm, "end": v(53.11, 27.83) * mm});
            skLineSegment(sketch, "E359", {"start": v(53.11, 27.83) * mm, "end": v(53.3, 27.93) * mm});
            skLineSegment(sketch, "E360", {"start": v(53.3, 27.93) * mm, "end": v(53.5, 28.03) * mm});
            skLineSegment(sketch, "E361", {"start": v(53.5, 28.03) * mm, "end": v(53.7, 28.14) * mm});
            skLineSegment(sketch, "E362", {"start": v(53.7, 28.14) * mm, "end": v(53.9, 28.23) * mm});
            skLineSegment(sketch, "E363", {"start": v(53.9, 28.23) * mm, "end": v(54.09, 28.33) * mm});
            skLineSegment(sketch, "E364", {"start": v(54.09, 28.33) * mm, "end": v(54.29, 28.44) * mm});
            skLineSegment(sketch, "E365", {"start": v(54.29, 28.44) * mm, "end": v(54.5, 28.55) * mm});
            skLineSegment(sketch, "E366", {"start": v(54.5, 28.55) * mm, "end": v(54.67, 28.69) * mm});
            skLineSegment(sketch, "E367", {"start": v(54.67, 28.69) * mm, "end": v(54.8, 28.87) * mm});
            skLineSegment(sketch, "E368", {"start": v(54.8, 28.87) * mm, "end": v(54.9, 29.08) * mm});
            skLineSegment(sketch, "E369", {"start": v(54.9, 29.08) * mm, "end": v(54.92, 29.3) * mm});
            skLineSegment(sketch, "E370", {"start": v(54.92, 29.3) * mm, "end": v(54.89, 29.53) * mm});
            skLineSegment(sketch, "E371", {"start": v(54.89, 29.53) * mm, "end": v(54.8, 29.74) * mm});
            skLineSegment(sketch, "E372", {"start": v(54.8, 29.74) * mm, "end": v(54.65, 29.92) * mm});
            skLineSegment(sketch, "E373", {"start": v(54.65, 29.92) * mm, "end": v(54.47, 30.05) * mm});
            skLineSegment(sketch, "E374", {"start": v(54.47, 30.05) * mm, "end": v(54.26, 30.13) * mm});
            skLineSegment(sketch, "E375", {"start": v(54.26, 30.13) * mm, "end": v(54.03, 30.16) * mm});
            skLineSegment(sketch, "E376", {"start": v(54.03, 30.16) * mm, "end": v(53.8, 30.12) * mm});
            skLineSegment(sketch, "E377", {"start": v(53.8, 30.12) * mm, "end": v(53.61, 30.03) * mm});
            skLineSegment(sketch, "E378", {"start": v(53.61, 30.03) * mm, "end": v(53.42, 29.93) * mm});
            skLineSegment(sketch, "E379", {"start": v(53.42, 29.93) * mm, "end": v(53.23, 29.83) * mm});
            skLineSegment(sketch, "E380", {"start": v(53.23, 29.83) * mm, "end": v(53.04, 29.72) * mm});
            skLineSegment(sketch, "E381", {"start": v(53.04, 29.72) * mm, "end": v(52.85, 29.62) * mm});
            skLineSegment(sketch, "E382", {"start": v(52.85, 29.62) * mm, "end": v(52.65, 29.5) * mm});
            skLineSegment(sketch, "E383", {"start": v(52.65, 29.5) * mm, "end": v(52.46, 29.4) * mm});
            skLineSegment(sketch, "E384", {"start": v(52.46, 29.4) * mm, "end": v(52.27, 29.3) * mm});
            skLineSegment(sketch, "E385", {"start": v(52.27, 29.3) * mm, "end": v(52.07, 29.2) * mm});
            skLineSegment(sketch, "E386", {"start": v(52.07, 29.2) * mm, "end": v(51.88, 29.09) * mm});
            skLineSegment(sketch, "E387", {"start": v(51.88, 29.09) * mm, "end": v(51.69, 28.98) * mm});
            skLineSegment(sketch, "E388", {"start": v(51.69, 28.98) * mm, "end": v(51.5, 28.87) * mm});
            skLineSegment(sketch, "E389", {"start": v(51.5, 28.87) * mm, "end": v(51.3, 28.77) * mm});
            skLineSegment(sketch, "E390", {"start": v(51.3, 28.77) * mm, "end": v(51.16, 28.7) * mm});
            skLineSegment(sketch, "E391", {"start": v(51.16, 28.7) * mm, "end": v(51.05, 28.88) * mm});
            skLineSegment(sketch, "E392", {"start": v(51.05, 28.88) * mm, "end": v(50.94, 29.07) * mm});
            skLineSegment(sketch, "E393", {"start": v(50.94, 29.07) * mm, "end": v(50.84, 29.26) * mm});
            skLineSegment(sketch, "E394", {"start": v(50.84, 29.26) * mm, "end": v(50.73, 29.45) * mm});
            skLineSegment(sketch, "E395", {"start": v(50.73, 29.45) * mm, "end": v(50.62, 29.64) * mm});
            skLineSegment(sketch, "E396", {"start": v(50.62, 29.64) * mm, "end": v(50.5, 29.82) * mm});
            skLineSegment(sketch, "E397", {"start": v(50.5, 29.82) * mm, "end": v(50.4, 30.01) * mm});
            skLineSegment(sketch, "E398", {"start": v(50.4, 30.01) * mm, "end": v(50.3, 30.2) * mm});
            skLineSegment(sketch, "E399", {"start": v(50.3, 30.2) * mm, "end": v(50.18, 30.39) * mm});
            skLineSegment(sketch, "E400", {"start": v(50.18, 30.39) * mm, "end": v(50.07, 30.58) * mm});
            skLineSegment(sketch, "E401", {"start": v(50.07, 30.58) * mm, "end": v(49.96, 30.77) * mm});
            skLineSegment(sketch, "E402", {"start": v(49.96, 30.77) * mm, "end": v(49.91, 30.86) * mm});
            skLineSegment(sketch, "E403", {"start": v(49.91, 30.86) * mm, "end": v(50.1, 30.97) * mm});
            skLineSegment(sketch, "E404", {"start": v(50.1, 30.97) * mm, "end": v(50.28, 31.08) * mm});
            skLineSegment(sketch, "E405", {"start": v(50.28, 31.08) * mm, "end": v(50.48, 31.2) * mm});
            skLineSegment(sketch, "E406", {"start": v(50.48, 31.2) * mm, "end": v(50.66, 31.31) * mm});
            skLineSegment(sketch, "E407", {"start": v(50.66, 31.31) * mm, "end": v(50.85, 31.43) * mm});
            skLineSegment(sketch, "E408", {"start": v(50.85, 31.43) * mm, "end": v(51.04, 31.54) * mm});
            skLineSegment(sketch, "E409", {"start": v(51.04, 31.54) * mm, "end": v(51.23, 31.66) * mm});
            skLineSegment(sketch, "E410", {"start": v(51.23, 31.66) * mm, "end": v(51.41, 31.77) * mm});
            skLineSegment(sketch, "E411", {"start": v(51.41, 31.77) * mm, "end": v(51.6, 31.88) * mm});
            skLineSegment(sketch, "E412", {"start": v(51.6, 31.88) * mm, "end": v(51.8, 32) * mm});
            skLineSegment(sketch, "E413", {"start": v(51.8, 32) * mm, "end": v(51.98, 32.11) * mm});
            skLineSegment(sketch, "E414", {"start": v(51.98, 32.11) * mm, "end": v(52.17, 32.23) * mm});
            skLineSegment(sketch, "E415", {"start": v(52.17, 32.23) * mm, "end": v(52.37, 32.35) * mm});
            skLineSegment(sketch, "E416", {"start": v(52.37, 32.35) * mm, "end": v(52.54, 32.5) * mm});
            skLineSegment(sketch, "E417", {"start": v(52.54, 32.5) * mm, "end": v(52.66, 32.7) * mm});
            skLineSegment(sketch, "E418", {"start": v(52.66, 32.7) * mm, "end": v(52.73, 32.9) * mm});
            skLineSegment(sketch, "E419", {"start": v(52.73, 32.9) * mm, "end": v(52.74, 33.14) * mm});
            skLineSegment(sketch, "E420", {"start": v(52.74, 33.14) * mm, "end": v(52.7, 33.36) * mm});
            skLineSegment(sketch, "E421", {"start": v(52.7, 33.36) * mm, "end": v(52.59, 33.56) * mm});
            skLineSegment(sketch, "E422", {"start": v(52.59, 33.56) * mm, "end": v(52.43, 33.73) * mm});
            skLineSegment(sketch, "E423", {"start": v(52.43, 33.73) * mm, "end": v(52.24, 33.85) * mm});
            skLineSegment(sketch, "E424", {"start": v(52.24, 33.85) * mm, "end": v(52.02, 33.92) * mm});
            skLineSegment(sketch, "E425", {"start": v(52.02, 33.92) * mm, "end": v(51.89, 33.93) * mm});
            skLineSegment(sketch, "E426", {"start": v(51.89, 33.93) * mm, "end": v(51.66, 33.9) * mm});
            skLineSegment(sketch, "E427", {"start": v(51.66, 33.9) * mm, "end": v(51.45, 33.82) * mm});
            skLineSegment(sketch, "E428", {"start": v(51.45, 33.82) * mm, "end": v(51.25, 33.7) * mm});
            skLineSegment(sketch, "E429", {"start": v(51.25, 33.7) * mm, "end": v(51.07, 33.57) * mm});
            skLineSegment(sketch, "E430", {"start": v(51.07, 33.57) * mm, "end": v(50.89, 33.46) * mm});
            skLineSegment(sketch, "E431", {"start": v(50.89, 33.46) * mm, "end": v(50.7, 33.34) * mm});
            skLineSegment(sketch, "E432", {"start": v(50.7, 33.34) * mm, "end": v(50.51, 33.22) * mm});
            skLineSegment(sketch, "E433", {"start": v(50.51, 33.22) * mm, "end": v(50.33, 33.1) * mm});
            skLineSegment(sketch, "E434", {"start": v(50.33, 33.1) * mm, "end": v(50.14, 32.98) * mm});
            skLineSegment(sketch, "E435", {"start": v(50.14, 32.98) * mm, "end": v(49.96, 32.86) * mm});
            skLineSegment(sketch, "E436", {"start": v(49.96, 32.86) * mm, "end": v(49.78, 32.74) * mm});
            skLineSegment(sketch, "E437", {"start": v(49.78, 32.74) * mm, "end": v(49.59, 32.62) * mm});
            skLineSegment(sketch, "E438", {"start": v(49.59, 32.62) * mm, "end": v(49.4, 32.5) * mm});
            skLineSegment(sketch, "E439", {"start": v(49.4, 32.5) * mm, "end": v(49.22, 32.38) * mm});
            skLineSegment(sketch, "E440", {"start": v(49.22, 32.38) * mm, "end": v(49.03, 32.26) * mm});
            skLineSegment(sketch, "E441", {"start": v(49.03, 32.26) * mm, "end": v(48.91, 32.44) * mm});
            skLineSegment(sketch, "E442", {"start": v(48.91, 32.44) * mm, "end": v(48.8, 32.62) * mm});
            skLineSegment(sketch, "E443", {"start": v(48.8, 32.62) * mm, "end": v(48.67, 32.8) * mm});
            skLineSegment(sketch, "E444", {"start": v(48.67, 32.8) * mm, "end": v(48.55, 32.99) * mm});
            skLineSegment(sketch, "E445", {"start": v(48.55, 32.99) * mm, "end": v(48.43, 33.17) * mm});
            skLineSegment(sketch, "E446", {"start": v(48.43, 33.17) * mm, "end": v(48.3, 33.35) * mm});
            skLineSegment(sketch, "E447", {"start": v(48.3, 33.35) * mm, "end": v(48.18, 33.53) * mm});
            skLineSegment(sketch, "E448", {"start": v(48.18, 33.53) * mm, "end": v(48.06, 33.7) * mm});
            skLineSegment(sketch, "E449", {"start": v(48.06, 33.7) * mm, "end": v(47.94, 33.89) * mm});
            skLineSegment(sketch, "E450", {"start": v(47.94, 33.89) * mm, "end": v(47.82, 34.07) * mm});
            skLineSegment(sketch, "E451", {"start": v(47.82, 34.07) * mm, "end": v(47.7, 34.25) * mm});
            skLineSegment(sketch, "E452", {"start": v(47.7, 34.25) * mm, "end": v(47.63, 34.34) * mm});
            skLineSegment(sketch, "E453", {"start": v(47.63, 34.34) * mm, "end": v(47.81, 34.46) * mm});
            skLineSegment(sketch, "E454", {"start": v(47.81, 34.46) * mm, "end": v(48, 34.59) * mm});
            skLineSegment(sketch, "E455", {"start": v(48, 34.59) * mm, "end": v(48.17, 34.72) * mm});
            skLineSegment(sketch, "E456", {"start": v(48.17, 34.72) * mm, "end": v(48.35, 34.84) * mm});
            skLineSegment(sketch, "E457", {"start": v(48.35, 34.84) * mm, "end": v(48.53, 34.97) * mm});
            skLineSegment(sketch, "E458", {"start": v(48.53, 34.97) * mm, "end": v(48.71, 35.1) * mm});
            skLineSegment(sketch, "E459", {"start": v(48.71, 35.1) * mm, "end": v(48.9, 35.22) * mm});
            skLineSegment(sketch, "E460", {"start": v(48.9, 35.22) * mm, "end": v(49.07, 35.35) * mm});
            skLineSegment(sketch, "E461", {"start": v(49.07, 35.35) * mm, "end": v(49.25, 35.48) * mm});
            skLineSegment(sketch, "E462", {"start": v(49.25, 35.48) * mm, "end": v(49.43, 35.6) * mm});
            skLineSegment(sketch, "E463", {"start": v(49.43, 35.6) * mm, "end": v(49.6, 35.73) * mm});
            skLineSegment(sketch, "E464", {"start": v(49.6, 35.73) * mm, "end": v(49.8, 35.86) * mm});
            skLineSegment(sketch, "E465", {"start": v(49.8, 35.86) * mm, "end": v(49.98, 36) * mm});
            skLineSegment(sketch, "E466", {"start": v(49.98, 36) * mm, "end": v(50.14, 36.16) * mm});
            skLineSegment(sketch, "E467", {"start": v(50.14, 36.16) * mm, "end": v(50.25, 36.36) * mm});
            skLineSegment(sketch, "E468", {"start": v(50.25, 36.36) * mm, "end": v(50.3, 36.58) * mm});
            skLineSegment(sketch, "E469", {"start": v(50.3, 36.58) * mm, "end": v(50.3, 36.8) * mm});
            skLineSegment(sketch, "E470", {"start": v(50.3, 36.8) * mm, "end": v(50.23, 37.02) * mm});
            skLineSegment(sketch, "E471", {"start": v(50.23, 37.02) * mm, "end": v(50.11, 37.22) * mm});
            skLineSegment(sketch, "E472", {"start": v(50.11, 37.22) * mm, "end": v(49.95, 37.37) * mm});
            skLineSegment(sketch, "E473", {"start": v(49.95, 37.37) * mm, "end": v(49.75, 37.48) * mm});
            skLineSegment(sketch, "E474", {"start": v(49.75, 37.48) * mm, "end": v(49.53, 37.54) * mm});
            skLineSegment(sketch, "E475", {"start": v(49.53, 37.54) * mm, "end": v(49.44, 37.54) * mm});
            skLineSegment(sketch, "E476", {"start": v(49.44, 37.54) * mm, "end": v(49.21, 37.5) * mm});
            skLineSegment(sketch, "E477", {"start": v(49.21, 37.5) * mm, "end": v(49, 37.42) * mm});
            skLineSegment(sketch, "E478", {"start": v(49, 37.42) * mm, "end": v(48.83, 37.3) * mm});
            skLineSegment(sketch, "E479", {"start": v(48.83, 37.3) * mm, "end": v(48.65, 37.16) * mm});
            skLineSegment(sketch, "E480", {"start": v(48.65, 37.16) * mm, "end": v(48.47, 37.03) * mm});
            skLineSegment(sketch, "E481", {"start": v(48.47, 37.03) * mm, "end": v(48.3, 36.9) * mm});
            skLineSegment(sketch, "E482", {"start": v(48.3, 36.9) * mm, "end": v(48.12, 36.77) * mm});
            skLineSegment(sketch, "E483", {"start": v(48.12, 36.77) * mm, "end": v(47.94, 36.64) * mm});
            skLineSegment(sketch, "E484", {"start": v(47.94, 36.64) * mm, "end": v(47.77, 36.5) * mm});
            skLineSegment(sketch, "E485", {"start": v(47.77, 36.5) * mm, "end": v(47.6, 36.38) * mm});
            skLineSegment(sketch, "E486", {"start": v(47.6, 36.38) * mm, "end": v(47.42, 36.24) * mm});
            skLineSegment(sketch, "E487", {"start": v(47.42, 36.24) * mm, "end": v(47.24, 36.11) * mm});
            skLineSegment(sketch, "E488", {"start": v(47.24, 36.11) * mm, "end": v(47.07, 35.98) * mm});
            skLineSegment(sketch, "E489", {"start": v(47.07, 35.98) * mm, "end": v(46.89, 35.85) * mm});
            skLineSegment(sketch, "E490", {"start": v(46.89, 35.85) * mm, "end": v(46.71, 35.72) * mm});
            skLineSegment(sketch, "E491", {"start": v(46.71, 35.72) * mm, "end": v(46.66, 35.68) * mm});
            skLineSegment(sketch, "E492", {"start": v(46.66, 35.68) * mm, "end": v(46.53, 35.85) * mm});
            skLineSegment(sketch, "E493", {"start": v(46.53, 35.85) * mm, "end": v(46.4, 36.02) * mm});
            skLineSegment(sketch, "E494", {"start": v(46.4, 36.02) * mm, "end": v(46.26, 36.2) * mm});
            skLineSegment(sketch, "E495", {"start": v(46.26, 36.2) * mm, "end": v(46.13, 36.36) * mm});
            skLineSegment(sketch, "E496", {"start": v(46.13, 36.36) * mm, "end": v(46, 36.54) * mm});
            skLineSegment(sketch, "E497", {"start": v(46, 36.54) * mm, "end": v(45.86, 36.7) * mm});
            skLineSegment(sketch, "E498", {"start": v(45.86, 36.7) * mm, "end": v(45.72, 36.88) * mm});
            skLineSegment(sketch, "E499", {"start": v(45.72, 36.88) * mm, "end": v(45.59, 37.05) * mm});
            skLineSegment(sketch, "E500", {"start": v(45.59, 37.05) * mm, "end": v(45.45, 37.22) * mm});
            skLineSegment(sketch, "E501", {"start": v(45.45, 37.22) * mm, "end": v(45.32, 37.4) * mm});
            skLineSegment(sketch, "E502", {"start": v(45.32, 37.4) * mm, "end": v(45.19, 37.57) * mm});
            skLineSegment(sketch, "E503", {"start": v(45.19, 37.57) * mm, "end": v(45.12, 37.65) * mm});
            skLineSegment(sketch, "E504", {"start": v(45.12, 37.65) * mm, "end": v(45.29, 37.79) * mm});
            skLineSegment(sketch, "E505", {"start": v(45.29, 37.79) * mm, "end": v(45.46, 37.92) * mm});
            skLineSegment(sketch, "E506", {"start": v(45.46, 37.92) * mm, "end": v(45.63, 38.07) * mm});
            skLineSegment(sketch, "E507", {"start": v(45.63, 38.07) * mm, "end": v(45.8, 38.2) * mm});
            skLineSegment(sketch, "E508", {"start": v(45.8, 38.2) * mm, "end": v(45.97, 38.34) * mm});
            skLineSegment(sketch, "E509", {"start": v(45.97, 38.34) * mm, "end": v(46.14, 38.48) * mm});
            skLineSegment(sketch, "E510", {"start": v(46.14, 38.48) * mm, "end": v(46.31, 38.62) * mm});
            skLineSegment(sketch, "E511", {"start": v(46.31, 38.62) * mm, "end": v(46.48, 38.76) * mm});
            skLineSegment(sketch, "E512", {"start": v(46.48, 38.76) * mm, "end": v(46.65, 38.9) * mm});
            skLineSegment(sketch, "E513", {"start": v(46.65, 38.9) * mm, "end": v(46.82, 39.04) * mm});
            skLineSegment(sketch, "E514", {"start": v(46.82, 39.04) * mm, "end": v(47, 39.18) * mm});
            skLineSegment(sketch, "E515", {"start": v(47, 39.18) * mm, "end": v(47.17, 39.32) * mm});
            skLineSegment(sketch, "E516", {"start": v(47.17, 39.32) * mm, "end": v(47.35, 39.47) * mm});
            skLineSegment(sketch, "E517", {"start": v(47.35, 39.47) * mm, "end": v(47.5, 39.64) * mm});
            skLineSegment(sketch, "E518", {"start": v(47.5, 39.64) * mm, "end": v(47.59, 39.85) * mm});
            skLineSegment(sketch, "E519", {"start": v(47.59, 39.85) * mm, "end": v(47.63, 40.07) * mm});
            skLineSegment(sketch, "E520", {"start": v(47.63, 40.07) * mm, "end": v(47.6, 40.3) * mm});
            skLineSegment(sketch, "E521", {"start": v(47.6, 40.3) * mm, "end": v(47.52, 40.51) * mm});
            skLineSegment(sketch, "E522", {"start": v(47.52, 40.51) * mm, "end": v(47.4, 40.7) * mm});
            skLineSegment(sketch, "E523", {"start": v(47.4, 40.7) * mm, "end": v(47.22, 40.84) * mm});
            skLineSegment(sketch, "E524", {"start": v(47.22, 40.84) * mm, "end": v(47.01, 40.93) * mm});
            skLineSegment(sketch, "E525", {"start": v(47.01, 40.93) * mm, "end": v(46.79, 40.97) * mm});
            skLineSegment(sketch, "E526", {"start": v(46.79, 40.97) * mm, "end": v(46.74, 40.97) * mm});
            skLineSegment(sketch, "E527", {"start": v(46.74, 40.97) * mm, "end": v(46.52, 40.94) * mm});
            skLineSegment(sketch, "E528", {"start": v(46.52, 40.94) * mm, "end": v(46.3, 40.84) * mm});
            skLineSegment(sketch, "E529", {"start": v(46.3, 40.84) * mm, "end": v(46.13, 40.7) * mm});
            skLineSegment(sketch, "E530", {"start": v(46.13, 40.7) * mm, "end": v(45.96, 40.56) * mm});
            skLineSegment(sketch, "E531", {"start": v(45.96, 40.56) * mm, "end": v(45.8, 40.42) * mm});
            skLineSegment(sketch, "E532", {"start": v(45.8, 40.42) * mm, "end": v(45.63, 40.27) * mm});
            skLineSegment(sketch, "E533", {"start": v(45.63, 40.27) * mm, "end": v(45.46, 40.13) * mm});
            skLineSegment(sketch, "E534", {"start": v(45.46, 40.13) * mm, "end": v(45.3, 39.99) * mm});
            skLineSegment(sketch, "E535", {"start": v(45.3, 39.99) * mm, "end": v(45.13, 39.84) * mm});
            skLineSegment(sketch, "E536", {"start": v(45.13, 39.84) * mm, "end": v(44.96, 39.7) * mm});
            skLineSegment(sketch, "E537", {"start": v(44.96, 39.7) * mm, "end": v(44.8, 39.56) * mm});
            skLineSegment(sketch, "E538", {"start": v(44.8, 39.56) * mm, "end": v(44.63, 39.41) * mm});
            skLineSegment(sketch, "E539", {"start": v(44.63, 39.41) * mm, "end": v(44.46, 39.27) * mm});
            skLineSegment(sketch, "E540", {"start": v(44.46, 39.27) * mm, "end": v(44.3, 39.13) * mm});
            skLineSegment(sketch, "E541", {"start": v(44.3, 39.13) * mm, "end": v(44.13, 38.98) * mm});
            skLineSegment(sketch, "E542", {"start": v(44.13, 38.98) * mm, "end": v(44.06, 38.92) * mm});
            skLineSegment(sketch, "E543", {"start": v(44.06, 38.92) * mm, "end": v(43.91, 39.08) * mm});
            skLineSegment(sketch, "E544", {"start": v(43.91, 39.08) * mm, "end": v(43.77, 39.24) * mm});
            skLineSegment(sketch, "E545", {"start": v(43.77, 39.24) * mm, "end": v(43.62, 39.4) * mm});
            skLineSegment(sketch, "E546", {"start": v(43.62, 39.4) * mm, "end": v(43.47, 39.57) * mm});
            skLineSegment(sketch, "E547", {"start": v(43.47, 39.57) * mm, "end": v(43.33, 39.73) * mm});
            skLineSegment(sketch, "E548", {"start": v(43.33, 39.73) * mm, "end": v(43.18, 39.89) * mm});
            skLineSegment(sketch, "E549", {"start": v(43.18, 39.89) * mm, "end": v(43.04, 40.05) * mm});
            skLineSegment(sketch, "E550", {"start": v(43.04, 40.05) * mm, "end": v(42.9, 40.21) * mm});
            skLineSegment(sketch, "E551", {"start": v(42.9, 40.21) * mm, "end": v(42.74, 40.37) * mm});
            skLineSegment(sketch, "E552", {"start": v(42.74, 40.37) * mm, "end": v(42.6, 40.54) * mm});
            skLineSegment(sketch, "E553", {"start": v(42.6, 40.54) * mm, "end": v(42.45, 40.7) * mm});
            skLineSegment(sketch, "E554", {"start": v(42.45, 40.7) * mm, "end": v(42.38, 40.78) * mm});
            skLineSegment(sketch, "E555", {"start": v(42.38, 40.78) * mm, "end": v(42.54, 40.93) * mm});
            skLineSegment(sketch, "E556", {"start": v(42.54, 40.93) * mm, "end": v(42.7, 41.08) * mm});
            skLineSegment(sketch, "E557", {"start": v(42.7, 41.08) * mm, "end": v(42.86, 41.23) * mm});
            skLineSegment(sketch, "E558", {"start": v(42.86, 41.23) * mm, "end": v(43.02, 41.38) * mm});
            skLineSegment(sketch, "E559", {"start": v(43.02, 41.38) * mm, "end": v(43.18, 41.53) * mm});
            skLineSegment(sketch, "E560", {"start": v(43.18, 41.53) * mm, "end": v(43.34, 41.68) * mm});
            skLineSegment(sketch, "E561", {"start": v(43.34, 41.68) * mm, "end": v(43.5, 41.83) * mm});
            skLineSegment(sketch, "E562", {"start": v(43.5, 41.83) * mm, "end": v(43.66, 41.98) * mm});
            skLineSegment(sketch, "E563", {"start": v(43.66, 41.98) * mm, "end": v(43.82, 42.13) * mm});
            skLineSegment(sketch, "E564", {"start": v(43.82, 42.13) * mm, "end": v(43.98, 42.28) * mm});
            skLineSegment(sketch, "E565", {"start": v(43.98, 42.28) * mm, "end": v(44.14, 42.43) * mm});
            skLineSegment(sketch, "E566", {"start": v(44.14, 42.43) * mm, "end": v(44.3, 42.58) * mm});
            skLineSegment(sketch, "E567", {"start": v(44.3, 42.58) * mm, "end": v(44.48, 42.75) * mm});
            skLineSegment(sketch, "E568", {"start": v(44.48, 42.75) * mm, "end": v(44.6, 42.93) * mm});
            skLineSegment(sketch, "E569", {"start": v(44.6, 42.93) * mm, "end": v(44.69, 43.14) * mm});
            skLineSegment(sketch, "E570", {"start": v(44.69, 43.14) * mm, "end": v(44.71, 43.37) * mm});
            skLineSegment(sketch, "E571", {"start": v(44.71, 43.37) * mm, "end": v(44.67, 43.6) * mm});
            skLineSegment(sketch, "E572", {"start": v(44.67, 43.6) * mm, "end": v(44.58, 43.8) * mm});
            skLineSegment(sketch, "E573", {"start": v(44.58, 43.8) * mm, "end": v(44.44, 43.97) * mm});
            skLineSegment(sketch, "E574", {"start": v(44.44, 43.97) * mm, "end": v(44.25, 44.1) * mm});
            skLineSegment(sketch, "E575", {"start": v(44.25, 44.1) * mm, "end": v(44.04, 44.19) * mm});
            skLineSegment(sketch, "E576", {"start": v(44.04, 44.19) * mm, "end": v(43.86, 44.2) * mm});
            skLineSegment(sketch, "E577", {"start": v(43.86, 44.2) * mm, "end": v(43.63, 44.18) * mm});
            skLineSegment(sketch, "E578", {"start": v(43.63, 44.18) * mm, "end": v(43.42, 44.1) * mm});
            skLineSegment(sketch, "E579", {"start": v(43.42, 44.1) * mm, "end": v(43.24, 43.96) * mm});
            skLineSegment(sketch, "E580", {"start": v(43.24, 43.96) * mm, "end": v(43.08, 43.8) * mm});
            skLineSegment(sketch, "E581", {"start": v(43.08, 43.8) * mm, "end": v(42.93, 43.65) * mm});
            skLineSegment(sketch, "E582", {"start": v(42.93, 43.65) * mm, "end": v(42.77, 43.5) * mm});
            skLineSegment(sketch, "E583", {"start": v(42.77, 43.5) * mm, "end": v(42.62, 43.34) * mm});
            skLineSegment(sketch, "E584", {"start": v(42.62, 43.34) * mm, "end": v(42.46, 43.19) * mm});
            skLineSegment(sketch, "E585", {"start": v(42.46, 43.19) * mm, "end": v(42.3, 43.03) * mm});
            skLineSegment(sketch, "E586", {"start": v(42.3, 43.03) * mm, "end": v(42.15, 42.88) * mm});
            skLineSegment(sketch, "E587", {"start": v(42.15, 42.88) * mm, "end": v(42, 42.72) * mm});
            skLineSegment(sketch, "E588", {"start": v(42, 42.72) * mm, "end": v(41.83, 42.57) * mm});
            skLineSegment(sketch, "E589", {"start": v(41.83, 42.57) * mm, "end": v(41.68, 42.41) * mm});
            skLineSegment(sketch, "E590", {"start": v(41.68, 42.41) * mm, "end": v(41.52, 42.26) * mm});
            skLineSegment(sketch, "E591", {"start": v(41.52, 42.26) * mm, "end": v(41.37, 42.1) * mm});
            skLineSegment(sketch, "E592", {"start": v(41.37, 42.1) * mm, "end": v(41.23, 41.97) * mm});
            skLineSegment(sketch, "E593", {"start": v(41.23, 41.97) * mm, "end": v(41.08, 42.12) * mm});
            skLineSegment(sketch, "E594", {"start": v(41.08, 42.12) * mm, "end": v(40.92, 42.27) * mm});
            skLineSegment(sketch, "E595", {"start": v(40.92, 42.27) * mm, "end": v(40.76, 42.42) * mm});
            skLineSegment(sketch, "E596", {"start": v(40.76, 42.42) * mm, "end": v(40.6, 42.57) * mm});
            skLineSegment(sketch, "E597", {"start": v(40.6, 42.57) * mm, "end": v(40.45, 42.72) * mm});
            skLineSegment(sketch, "E598", {"start": v(40.45, 42.72) * mm, "end": v(40.3, 42.88) * mm});
            skLineSegment(sketch, "E599", {"start": v(40.3, 42.88) * mm, "end": v(40.14, 43.03) * mm});
            skLineSegment(sketch, "E600", {"start": v(40.14, 43.03) * mm, "end": v(39.98, 43.18) * mm});
            skLineSegment(sketch, "E601", {"start": v(39.98, 43.18) * mm, "end": v(39.82, 43.33) * mm});
            skLineSegment(sketch, "E602", {"start": v(39.82, 43.33) * mm, "end": v(39.66, 43.48) * mm});
            skLineSegment(sketch, "E603", {"start": v(39.66, 43.48) * mm, "end": v(39.5, 43.63) * mm});
            skLineSegment(sketch, "E604", {"start": v(39.5, 43.63) * mm, "end": v(39.43, 43.7) * mm});
            skLineSegment(sketch, "E605", {"start": v(39.43, 43.7) * mm, "end": v(39.58, 43.87) * mm});
            skLineSegment(sketch, "E606", {"start": v(39.58, 43.87) * mm, "end": v(39.73, 44.03) * mm});
            skLineSegment(sketch, "E607", {"start": v(39.73, 44.03) * mm, "end": v(39.88, 44.2) * mm});
            skLineSegment(sketch, "E608", {"start": v(39.88, 44.2) * mm, "end": v(40.03, 44.35) * mm});
            skLineSegment(sketch, "E609", {"start": v(40.03, 44.35) * mm, "end": v(40.18, 44.51) * mm});
            skLineSegment(sketch, "E610", {"start": v(40.18, 44.51) * mm, "end": v(40.33, 44.67) * mm});
            skLineSegment(sketch, "E611", {"start": v(40.33, 44.67) * mm, "end": v(40.48, 44.83) * mm});
            skLineSegment(sketch, "E612", {"start": v(40.48, 44.83) * mm, "end": v(40.62, 45) * mm});
            skLineSegment(sketch, "E613", {"start": v(40.62, 45) * mm, "end": v(40.78, 45.16) * mm});
            skLineSegment(sketch, "E614", {"start": v(40.78, 45.16) * mm, "end": v(40.92, 45.32) * mm});
            skLineSegment(sketch, "E615", {"start": v(40.92, 45.32) * mm, "end": v(41.07, 45.48) * mm});
            skLineSegment(sketch, "E616", {"start": v(41.07, 45.48) * mm, "end": v(41.22, 45.64) * mm});
            skLineSegment(sketch, "E617", {"start": v(41.22, 45.64) * mm, "end": v(41.38, 45.82) * mm});
            skLineSegment(sketch, "E618", {"start": v(41.38, 45.82) * mm, "end": v(41.5, 46) * mm});
            skLineSegment(sketch, "E619", {"start": v(41.5, 46) * mm, "end": v(41.57, 46.23) * mm});
            skLineSegment(sketch, "E620", {"start": v(41.57, 46.23) * mm, "end": v(41.58, 46.45) * mm});
            skLineSegment(sketch, "E621", {"start": v(41.58, 46.45) * mm, "end": v(41.52, 46.67) * mm});
            skLineSegment(sketch, "E622", {"start": v(41.52, 46.67) * mm, "end": v(41.41, 46.87) * mm});
            skLineSegment(sketch, "E623", {"start": v(41.41, 46.87) * mm, "end": v(41.26, 47.04) * mm});
            skLineSegment(sketch, "E624", {"start": v(41.26, 47.04) * mm, "end": v(41.06, 47.16) * mm});
            skLineSegment(sketch, "E625", {"start": v(41.06, 47.16) * mm, "end": v(40.85, 47.22) * mm});
            skLineSegment(sketch, "E626", {"start": v(40.85, 47.22) * mm, "end": v(40.7, 47.23) * mm});
            skLineSegment(sketch, "E627", {"start": v(40.7, 47.23) * mm, "end": v(40.48, 47.2) * mm});
            skLineSegment(sketch, "E628", {"start": v(40.48, 47.2) * mm, "end": v(40.27, 47.11) * mm});
            skLineSegment(sketch, "E629", {"start": v(40.27, 47.11) * mm, "end": v(40.1, 46.98) * mm});
            skLineSegment(sketch, "E630", {"start": v(40.1, 46.98) * mm, "end": v(39.94, 46.8) * mm});
            skLineSegment(sketch, "E631", {"start": v(39.94, 46.8) * mm, "end": v(39.8, 46.64) * mm});
            skLineSegment(sketch, "E632", {"start": v(39.8, 46.64) * mm, "end": v(39.65, 46.47) * mm});
            skLineSegment(sketch, "E633", {"start": v(39.65, 46.47) * mm, "end": v(39.5, 46.3) * mm});
            skLineSegment(sketch, "E634", {"start": v(39.5, 46.3) * mm, "end": v(39.36, 46.14) * mm});
            skLineSegment(sketch, "E635", {"start": v(39.36, 46.14) * mm, "end": v(39.22, 45.98) * mm});
            skLineSegment(sketch, "E636", {"start": v(39.22, 45.98) * mm, "end": v(39.07, 45.8) * mm});
            skLineSegment(sketch, "E637", {"start": v(39.07, 45.8) * mm, "end": v(38.93, 45.64) * mm});
            skLineSegment(sketch, "E638", {"start": v(38.93, 45.64) * mm, "end": v(38.78, 45.48) * mm});
            skLineSegment(sketch, "E639", {"start": v(38.78, 45.48) * mm, "end": v(38.64, 45.31) * mm});
            skLineSegment(sketch, "E640", {"start": v(38.64, 45.31) * mm, "end": v(38.5, 45.15) * mm});
            skLineSegment(sketch, "E641", {"start": v(38.5, 45.15) * mm, "end": v(38.35, 44.98) * mm});
            skLineSegment(sketch, "E642", {"start": v(38.35, 44.98) * mm, "end": v(38.2, 44.81) * mm});
            skLineSegment(sketch, "E643", {"start": v(38.2, 44.81) * mm, "end": v(38.03, 44.95) * mm});
            skLineSegment(sketch, "E644", {"start": v(38.03, 44.95) * mm, "end": v(37.87, 45.1) * mm});
            skLineSegment(sketch, "E645", {"start": v(37.87, 45.1) * mm, "end": v(37.7, 45.23) * mm});
            skLineSegment(sketch, "E646", {"start": v(37.7, 45.23) * mm, "end": v(37.53, 45.37) * mm});
            skLineSegment(sketch, "E647", {"start": v(37.53, 45.37) * mm, "end": v(37.37, 45.51) * mm});
            skLineSegment(sketch, "E648", {"start": v(37.37, 45.51) * mm, "end": v(37.2, 45.65) * mm});
            skLineSegment(sketch, "E649", {"start": v(37.2, 45.65) * mm, "end": v(37.03, 45.8) * mm});
            skLineSegment(sketch, "E650", {"start": v(37.03, 45.8) * mm, "end": v(36.87, 45.93) * mm});
            skLineSegment(sketch, "E651", {"start": v(36.87, 45.93) * mm, "end": v(36.7, 46.07) * mm});
            skLineSegment(sketch, "E652", {"start": v(36.7, 46.07) * mm, "end": v(36.53, 46.21) * mm});
            skLineSegment(sketch, "E653", {"start": v(36.53, 46.21) * mm, "end": v(36.37, 46.35) * mm});
            skLineSegment(sketch, "E654", {"start": v(36.37, 46.35) * mm, "end": v(36.28, 46.42) * mm});
            skLineSegment(sketch, "E655", {"start": v(36.28, 46.42) * mm, "end": v(36.42, 46.6) * mm});
            skLineSegment(sketch, "E656", {"start": v(36.42, 46.6) * mm, "end": v(36.56, 46.76) * mm});
            skLineSegment(sketch, "E657", {"start": v(36.56, 46.76) * mm, "end": v(36.7, 46.94) * mm});
            skLineSegment(sketch, "E658", {"start": v(36.7, 46.94) * mm, "end": v(36.83, 47.1) * mm});
            skLineSegment(sketch, "E659", {"start": v(36.83, 47.1) * mm, "end": v(36.97, 47.28) * mm});
            skLineSegment(sketch, "E660", {"start": v(36.97, 47.28) * mm, "end": v(37.11, 47.45) * mm});
            skLineSegment(sketch, "E661", {"start": v(37.11, 47.45) * mm, "end": v(37.25, 47.62) * mm});
            skLineSegment(sketch, "E662", {"start": v(37.25, 47.62) * mm, "end": v(37.38, 47.8) * mm});
            skLineSegment(sketch, "E663", {"start": v(37.38, 47.8) * mm, "end": v(37.52, 47.97) * mm});
            skLineSegment(sketch, "E664", {"start": v(37.52, 47.97) * mm, "end": v(37.66, 48.14) * mm});
            skLineSegment(sketch, "E665", {"start": v(37.66, 48.14) * mm, "end": v(37.8, 48.3) * mm});
            skLineSegment(sketch, "E666", {"start": v(37.8, 48.3) * mm, "end": v(37.94, 48.48) * mm});
            skLineSegment(sketch, "E667", {"start": v(37.94, 48.48) * mm, "end": v(38.08, 48.66) * mm});
            skLineSegment(sketch, "E668", {"start": v(38.08, 48.66) * mm, "end": v(38.19, 48.86) * mm});
            skLineSegment(sketch, "E669", {"start": v(38.19, 48.86) * mm, "end": v(38.24, 49.09) * mm});
            skLineSegment(sketch, "E670", {"start": v(38.24, 49.09) * mm, "end": v(38.23, 49.31) * mm});
            skLineSegment(sketch, "E671", {"start": v(38.23, 49.31) * mm, "end": v(38.16, 49.53) * mm});
            skLineSegment(sketch, "E672", {"start": v(38.16, 49.53) * mm, "end": v(38.04, 49.72) * mm});
            skLineSegment(sketch, "E673", {"start": v(38.04, 49.72) * mm, "end": v(37.87, 49.88) * mm});
            skLineSegment(sketch, "E674", {"start": v(37.87, 49.88) * mm, "end": v(37.67, 49.98) * mm});
            skLineSegment(sketch, "E675", {"start": v(37.67, 49.98) * mm, "end": v(37.45, 50.03) * mm});
            skLineSegment(sketch, "E676", {"start": v(37.45, 50.03) * mm, "end": v(37.36, 50.03) * mm});
            skLineSegment(sketch, "E677", {"start": v(37.36, 50.03) * mm, "end": v(37.13, 50) * mm});
            skLineSegment(sketch, "E678", {"start": v(37.13, 50) * mm, "end": v(36.93, 49.9) * mm});
            skLineSegment(sketch, "E679", {"start": v(36.93, 49.9) * mm, "end": v(36.75, 49.76) * mm});
            skLineSegment(sketch, "E680", {"start": v(36.75, 49.76) * mm, "end": v(36.61, 49.6) * mm});
            skLineSegment(sketch, "E681", {"start": v(36.61, 49.6) * mm, "end": v(36.48, 49.42) * mm});
            skLineSegment(sketch, "E682", {"start": v(36.48, 49.42) * mm, "end": v(36.35, 49.24) * mm});
            skLineSegment(sketch, "E683", {"start": v(36.35, 49.24) * mm, "end": v(36.22, 49.07) * mm});
            skLineSegment(sketch, "E684", {"start": v(36.22, 49.07) * mm, "end": v(36.08, 48.9) * mm});
            skLineSegment(sketch, "E685", {"start": v(36.08, 48.9) * mm, "end": v(35.95, 48.72) * mm});
            skLineSegment(sketch, "E686", {"start": v(35.95, 48.72) * mm, "end": v(35.82, 48.54) * mm});
            skLineSegment(sketch, "E687", {"start": v(35.82, 48.54) * mm, "end": v(35.69, 48.37) * mm});
            skLineSegment(sketch, "E688", {"start": v(35.69, 48.37) * mm, "end": v(35.55, 48.2) * mm});
            skLineSegment(sketch, "E689", {"start": v(35.55, 48.2) * mm, "end": v(35.42, 48.02) * mm});
            skLineSegment(sketch, "E690", {"start": v(35.42, 48.02) * mm, "end": v(35.29, 47.85) * mm});
            skLineSegment(sketch, "E691", {"start": v(35.29, 47.85) * mm, "end": v(35.15, 47.67) * mm});
            skLineSegment(sketch, "E692", {"start": v(35.15, 47.67) * mm, "end": v(35.02, 47.5) * mm});
            skLineSegment(sketch, "E693", {"start": v(35.02, 47.5) * mm, "end": v(34.98, 47.44) * mm});
            skLineSegment(sketch, "E694", {"start": v(34.98, 47.44) * mm, "end": v(34.8, 47.57) * mm});
            skLineSegment(sketch, "E695", {"start": v(34.8, 47.57) * mm, "end": v(34.63, 47.7) * mm});
            skLineSegment(sketch, "E696", {"start": v(34.63, 47.7) * mm, "end": v(34.45, 47.83) * mm});
            skLineSegment(sketch, "E697", {"start": v(34.45, 47.83) * mm, "end": v(34.27, 47.95) * mm});
            skLineSegment(sketch, "E698", {"start": v(34.27, 47.95) * mm, "end": v(34.1, 48.08) * mm});
            skLineSegment(sketch, "E699", {"start": v(34.1, 48.08) * mm, "end": v(33.92, 48.21) * mm});
            skLineSegment(sketch, "E700", {"start": v(33.92, 48.21) * mm, "end": v(33.75, 48.34) * mm});
            skLineSegment(sketch, "E701", {"start": v(33.75, 48.34) * mm, "end": v(33.57, 48.47) * mm});
            skLineSegment(sketch, "E702", {"start": v(33.57, 48.47) * mm, "end": v(33.4, 48.6) * mm});
            skLineSegment(sketch, "E703", {"start": v(33.4, 48.6) * mm, "end": v(33.22, 48.72) * mm});
            skLineSegment(sketch, "E704", {"start": v(33.22, 48.72) * mm, "end": v(33.04, 48.85) * mm});
            skLineSegment(sketch, "E705", {"start": v(33.04, 48.85) * mm, "end": v(32.96, 48.91) * mm});
            skLineSegment(sketch, "E706", {"start": v(32.96, 48.91) * mm, "end": v(33.08, 49.1) * mm});
            skLineSegment(sketch, "E707", {"start": v(33.08, 49.1) * mm, "end": v(33.2, 49.27) * mm});
            skLineSegment(sketch, "E708", {"start": v(33.2, 49.27) * mm, "end": v(33.33, 49.46) * mm});
            skLineSegment(sketch, "E709", {"start": v(33.33, 49.46) * mm, "end": v(33.46, 49.63) * mm});
            skLineSegment(sketch, "E710", {"start": v(33.46, 49.63) * mm, "end": v(33.58, 49.81) * mm});
            skLineSegment(sketch, "E711", {"start": v(33.58, 49.81) * mm, "end": v(33.7, 50) * mm});
            skLineSegment(sketch, "E712", {"start": v(33.7, 50) * mm, "end": v(33.83, 50.18) * mm});
            skLineSegment(sketch, "E713", {"start": v(33.83, 50.18) * mm, "end": v(33.96, 50.35) * mm});
            skLineSegment(sketch, "E714", {"start": v(33.96, 50.35) * mm, "end": v(34.08, 50.54) * mm});
            skLineSegment(sketch, "E715", {"start": v(34.08, 50.54) * mm, "end": v(34.2, 50.72) * mm});
            skLineSegment(sketch, "E716", {"start": v(34.2, 50.72) * mm, "end": v(34.33, 50.9) * mm});
            skLineSegment(sketch, "E717", {"start": v(34.33, 50.9) * mm, "end": v(34.46, 51.08) * mm});
            skLineSegment(sketch, "E718", {"start": v(34.46, 51.08) * mm, "end": v(34.6, 51.27) * mm});
            skLineSegment(sketch, "E719", {"start": v(34.6, 51.27) * mm, "end": v(34.69, 51.48) * mm});
            skLineSegment(sketch, "E720", {"start": v(34.69, 51.48) * mm, "end": v(34.72, 51.7) * mm});
            skLineSegment(sketch, "E721", {"start": v(34.72, 51.7) * mm, "end": v(34.7, 51.93) * mm});
            skLineSegment(sketch, "E722", {"start": v(34.7, 51.93) * mm, "end": v(34.61, 52.14) * mm});
            skLineSegment(sketch, "E723", {"start": v(34.61, 52.14) * mm, "end": v(34.48, 52.33) * mm});
            skLineSegment(sketch, "E724", {"start": v(34.48, 52.33) * mm, "end": v(34.3, 52.47) * mm});
            skLineSegment(sketch, "E725", {"start": v(34.3, 52.47) * mm, "end": v(34.1, 52.56) * mm});
            skLineSegment(sketch, "E726", {"start": v(34.1, 52.56) * mm, "end": v(33.87, 52.6) * mm});
            skLineSegment(sketch, "E727", {"start": v(33.87, 52.6) * mm, "end": v(33.64, 52.57) * mm});
            skLineSegment(sketch, "E728", {"start": v(33.64, 52.57) * mm, "end": v(33.43, 52.48) * mm});
            skLineSegment(sketch, "E729", {"start": v(33.43, 52.48) * mm, "end": v(33.25, 52.35) * mm});
            skLineSegment(sketch, "E730", {"start": v(33.25, 52.35) * mm, "end": v(33.11, 52.17) * mm});
            skLineSegment(sketch, "E731", {"start": v(33.11, 52.17) * mm, "end": v(33, 52) * mm});
            skLineSegment(sketch, "E732", {"start": v(33, 52) * mm, "end": v(32.87, 51.81) * mm});
            skLineSegment(sketch, "E733", {"start": v(32.87, 51.81) * mm, "end": v(32.75, 51.63) * mm});
            skLineSegment(sketch, "E734", {"start": v(32.75, 51.63) * mm, "end": v(32.63, 51.45) * mm});
            skLineSegment(sketch, "E735", {"start": v(32.63, 51.45) * mm, "end": v(32.51, 51.26) * mm});
            skLineSegment(sketch, "E736", {"start": v(32.51, 51.26) * mm, "end": v(32.4, 51.08) * mm});
            skLineSegment(sketch, "E737", {"start": v(32.4, 51.08) * mm, "end": v(32.27, 50.9) * mm});
            skLineSegment(sketch, "E738", {"start": v(32.27, 50.9) * mm, "end": v(32.15, 50.7) * mm});
            skLineSegment(sketch, "E739", {"start": v(32.15, 50.7) * mm, "end": v(32.03, 50.52) * mm});
            skLineSegment(sketch, "E740", {"start": v(32.03, 50.52) * mm, "end": v(31.91, 50.34) * mm});
            skLineSegment(sketch, "E741", {"start": v(31.91, 50.34) * mm, "end": v(31.79, 50.15) * mm});
            skLineSegment(sketch, "E742", {"start": v(31.79, 50.15) * mm, "end": v(31.67, 49.97) * mm});
            skLineSegment(sketch, "E743", {"start": v(31.67, 49.97) * mm, "end": v(31.58, 49.84) * mm});
            skLineSegment(sketch, "E744", {"start": v(31.58, 49.84) * mm, "end": v(31.4, 49.95) * mm});
            skLineSegment(sketch, "E745", {"start": v(31.4, 49.95) * mm, "end": v(31.21, 50.07) * mm});
            skLineSegment(sketch, "E746", {"start": v(31.21, 50.07) * mm, "end": v(31.03, 50.19) * mm});
            skLineSegment(sketch, "E747", {"start": v(31.03, 50.19) * mm, "end": v(30.84, 50.3) * mm});
            skLineSegment(sketch, "E748", {"start": v(30.84, 50.3) * mm, "end": v(30.66, 50.42) * mm});
            skLineSegment(sketch, "E749", {"start": v(30.66, 50.42) * mm, "end": v(30.47, 50.53) * mm});
            skLineSegment(sketch, "E750", {"start": v(30.47, 50.53) * mm, "end": v(30.29, 50.65) * mm});
            skLineSegment(sketch, "E751", {"start": v(30.29, 50.65) * mm, "end": v(30.1, 50.76) * mm});
            skLineSegment(sketch, "E752", {"start": v(30.1, 50.76) * mm, "end": v(29.92, 50.88) * mm});
            skLineSegment(sketch, "E753", {"start": v(29.92, 50.88) * mm, "end": v(29.74, 51) * mm});
            skLineSegment(sketch, "E754", {"start": v(29.74, 51) * mm, "end": v(29.55, 51.1) * mm});
            skLineSegment(sketch, "E755", {"start": v(29.55, 51.1) * mm, "end": v(29.46, 51.17) * mm});
            skLineSegment(sketch, "E756", {"start": v(29.46, 51.17) * mm, "end": v(29.57, 51.35) * mm});
            skLineSegment(sketch, "E757", {"start": v(29.57, 51.35) * mm, "end": v(29.68, 51.54) * mm});
            skLineSegment(sketch, "E758", {"start": v(29.68, 51.54) * mm, "end": v(29.8, 51.73) * mm});
            skLineSegment(sketch, "E759", {"start": v(29.8, 51.73) * mm, "end": v(29.9, 51.92) * mm});
            skLineSegment(sketch, "E760", {"start": v(29.9, 51.92) * mm, "end": v(30.02, 52.1) * mm});
            skLineSegment(sketch, "E761", {"start": v(30.02, 52.1) * mm, "end": v(30.14, 52.3) * mm});
            skLineSegment(sketch, "E762", {"start": v(30.14, 52.3) * mm, "end": v(30.25, 52.49) * mm});
            skLineSegment(sketch, "E763", {"start": v(30.25, 52.49) * mm, "end": v(30.36, 52.67) * mm});
            skLineSegment(sketch, "E764", {"start": v(30.36, 52.67) * mm, "end": v(30.47, 52.87) * mm});
            skLineSegment(sketch, "E765", {"start": v(30.47, 52.87) * mm, "end": v(30.59, 53.05) * mm});
            skLineSegment(sketch, "E766", {"start": v(30.59, 53.05) * mm, "end": v(30.7, 53.24) * mm});
            skLineSegment(sketch, "E767", {"start": v(30.7, 53.24) * mm, "end": v(30.81, 53.43) * mm});
            skLineSegment(sketch, "E768", {"start": v(30.81, 53.43) * mm, "end": v(30.93, 53.63) * mm});
            skLineSegment(sketch, "E769", {"start": v(30.93, 53.63) * mm, "end": v(31, 53.85) * mm});
            skLineSegment(sketch, "E770", {"start": v(31, 53.85) * mm, "end": v(31.03, 54.07) * mm});
            skLineSegment(sketch, "E771", {"start": v(31.03, 54.07) * mm, "end": v(30.99, 54.3) * mm});
            skLineSegment(sketch, "E772", {"start": v(30.99, 54.3) * mm, "end": v(30.89, 54.5) * mm});
            skLineSegment(sketch, "E773", {"start": v(30.89, 54.5) * mm, "end": v(30.74, 54.68) * mm});
            skLineSegment(sketch, "E774", {"start": v(30.74, 54.68) * mm, "end": v(30.55, 54.8) * mm});
            skLineSegment(sketch, "E775", {"start": v(30.55, 54.8) * mm, "end": v(30.34, 54.88) * mm});
            skLineSegment(sketch, "E776", {"start": v(30.34, 54.88) * mm, "end": v(30.16, 54.9) * mm});
            skLineSegment(sketch, "E777", {"start": v(30.16, 54.9) * mm, "end": v(29.93, 54.87) * mm});
            skLineSegment(sketch, "E778", {"start": v(29.93, 54.87) * mm, "end": v(29.72, 54.78) * mm});
            skLineSegment(sketch, "E779", {"start": v(29.72, 54.78) * mm, "end": v(29.54, 54.64) * mm});
            skLineSegment(sketch, "E780", {"start": v(29.54, 54.64) * mm, "end": v(29.4, 54.46) * mm});
            skLineSegment(sketch, "E781", {"start": v(29.4, 54.46) * mm, "end": v(29.3, 54.27) * mm});
            skLineSegment(sketch, "E782", {"start": v(29.3, 54.27) * mm, "end": v(29.2, 54.08) * mm});
            skLineSegment(sketch, "E783", {"start": v(29.2, 54.08) * mm, "end": v(29.08, 53.89) * mm});
            skLineSegment(sketch, "E784", {"start": v(29.08, 53.89) * mm, "end": v(28.98, 53.7) * mm});
            skLineSegment(sketch, "E785", {"start": v(28.98, 53.7) * mm, "end": v(28.87, 53.5) * mm});
            skLineSegment(sketch, "E786", {"start": v(28.87, 53.5) * mm, "end": v(28.76, 53.3) * mm});
            skLineSegment(sketch, "E787", {"start": v(28.76, 53.3) * mm, "end": v(28.66, 53.12) * mm});
            skLineSegment(sketch, "E788", {"start": v(28.66, 53.12) * mm, "end": v(28.55, 52.93) * mm});
            skLineSegment(sketch, "E789", {"start": v(28.55, 52.93) * mm, "end": v(28.44, 52.73) * mm});
            skLineSegment(sketch, "E790", {"start": v(28.44, 52.73) * mm, "end": v(28.33, 52.54) * mm});
            skLineSegment(sketch, "E791", {"start": v(28.33, 52.54) * mm, "end": v(28.23, 52.35) * mm});
            skLineSegment(sketch, "E792", {"start": v(28.23, 52.35) * mm, "end": v(28.12, 52.16) * mm});
            skLineSegment(sketch, "E793", {"start": v(28.12, 52.16) * mm, "end": v(28.03, 52) * mm});
            skLineSegment(sketch, "E794", {"start": v(28.03, 52) * mm, "end": v(27.83, 52.1) * mm});
            skLineSegment(sketch, "E795", {"start": v(27.83, 52.1) * mm, "end": v(27.64, 52.2) * mm});
            skLineSegment(sketch, "E796", {"start": v(27.64, 52.2) * mm, "end": v(27.45, 52.3) * mm});
            skLineSegment(sketch, "E797", {"start": v(27.45, 52.3) * mm, "end": v(27.26, 52.4) * mm});
            skLineSegment(sketch, "E798", {"start": v(27.26, 52.4) * mm, "end": v(27.06, 52.5) * mm});
            skLineSegment(sketch, "E799", {"start": v(27.06, 52.5) * mm, "end": v(26.87, 52.6) * mm});
            skLineSegment(sketch, "E800", {"start": v(26.87, 52.6) * mm, "end": v(26.68, 52.7) * mm});
            skLineSegment(sketch, "E801", {"start": v(26.68, 52.7) * mm, "end": v(26.49, 52.81) * mm});
            skLineSegment(sketch, "E802", {"start": v(26.49, 52.81) * mm, "end": v(26.3, 52.91) * mm});
            skLineSegment(sketch, "E803", {"start": v(26.3, 52.91) * mm, "end": v(26.1, 53.02) * mm});
            skLineSegment(sketch, "E804", {"start": v(26.1, 53.02) * mm, "end": v(25.91, 53.12) * mm});
            skLineSegment(sketch, "E805", {"start": v(25.91, 53.12) * mm, "end": v(25.82, 53.17) * mm});
            skLineSegment(sketch, "E806", {"start": v(25.82, 53.17) * mm, "end": v(25.92, 53.36) * mm});
            skLineSegment(sketch, "E807", {"start": v(25.92, 53.36) * mm, "end": v(26.01, 53.56) * mm});
            skLineSegment(sketch, "E808", {"start": v(26.01, 53.56) * mm, "end": v(26.11, 53.76) * mm});
            skLineSegment(sketch, "E809", {"start": v(26.11, 53.76) * mm, "end": v(26.21, 53.95) * mm});
            skLineSegment(sketch, "E810", {"start": v(26.21, 53.95) * mm, "end": v(26.31, 54.15) * mm});
            skLineSegment(sketch, "E811", {"start": v(26.31, 54.15) * mm, "end": v(26.41, 54.35) * mm});
            skLineSegment(sketch, "E812", {"start": v(26.41, 54.35) * mm, "end": v(26.51, 54.54) * mm});
            skLineSegment(sketch, "E813", {"start": v(26.51, 54.54) * mm, "end": v(26.6, 54.73) * mm});
            skLineSegment(sketch, "E814", {"start": v(26.6, 54.73) * mm, "end": v(26.7, 54.93) * mm});
            skLineSegment(sketch, "E815", {"start": v(26.7, 54.93) * mm, "end": v(26.8, 55.13) * mm});
            skLineSegment(sketch, "E816", {"start": v(26.8, 55.13) * mm, "end": v(26.9, 55.32) * mm});
            skLineSegment(sketch, "E817", {"start": v(26.9, 55.32) * mm, "end": v(27, 55.52) * mm});
            skLineSegment(sketch, "E818", {"start": v(27, 55.52) * mm, "end": v(27.11, 55.73) * mm});
            skLineSegment(sketch, "E819", {"start": v(27.11, 55.73) * mm, "end": v(27.17, 55.95) * mm});
            skLineSegment(sketch, "E820", {"start": v(27.17, 55.95) * mm, "end": v(27.18, 56.18) * mm});
            skLineSegment(sketch, "E821", {"start": v(27.18, 56.18) * mm, "end": v(27.12, 56.4) * mm});
            skLineSegment(sketch, "E822", {"start": v(27.12, 56.4) * mm, "end": v(27, 56.6) * mm});
            skLineSegment(sketch, "E823", {"start": v(27, 56.6) * mm, "end": v(26.85, 56.76) * mm});
            skLineSegment(sketch, "E824", {"start": v(26.85, 56.76) * mm, "end": v(26.65, 56.88) * mm});
            skLineSegment(sketch, "E825", {"start": v(26.65, 56.88) * mm, "end": v(26.43, 56.94) * mm});
            skLineSegment(sketch, "E826", {"start": v(26.43, 56.94) * mm, "end": v(26.3, 56.94) * mm});
            skLineSegment(sketch, "E827", {"start": v(26.3, 56.94) * mm, "end": v(26.07, 56.9) * mm});
            skLineSegment(sketch, "E828", {"start": v(26.07, 56.9) * mm, "end": v(25.87, 56.82) * mm});
            skLineSegment(sketch, "E829", {"start": v(25.87, 56.82) * mm, "end": v(25.69, 56.68) * mm});
            skLineSegment(sketch, "E830", {"start": v(25.69, 56.68) * mm, "end": v(25.55, 56.5) * mm});
            skLineSegment(sketch, "E831", {"start": v(25.55, 56.5) * mm, "end": v(25.45, 56.28) * mm});
            skLineSegment(sketch, "E832", {"start": v(25.45, 56.28) * mm, "end": v(25.36, 56.08) * mm});
            skLineSegment(sketch, "E833", {"start": v(25.36, 56.08) * mm, "end": v(25.27, 55.89) * mm});
            skLineSegment(sketch, "E834", {"start": v(25.27, 55.89) * mm, "end": v(25.17, 55.68) * mm});
            skLineSegment(sketch, "E835", {"start": v(25.17, 55.68) * mm, "end": v(25.08, 55.49) * mm});
            skLineSegment(sketch, "E836", {"start": v(25.08, 55.49) * mm, "end": v(24.99, 55.3) * mm});
            skLineSegment(sketch, "E837", {"start": v(24.99, 55.3) * mm, "end": v(24.9, 55.09) * mm});
            skLineSegment(sketch, "E838", {"start": v(24.9, 55.09) * mm, "end": v(24.8, 54.9) * mm});
            skLineSegment(sketch, "E839", {"start": v(24.8, 54.9) * mm, "end": v(24.7, 54.7) * mm});
            skLineSegment(sketch, "E840", {"start": v(24.7, 54.7) * mm, "end": v(24.61, 54.5) * mm});
            skLineSegment(sketch, "E841", {"start": v(24.61, 54.5) * mm, "end": v(24.52, 54.3) * mm});
            skLineSegment(sketch, "E842", {"start": v(24.52, 54.3) * mm, "end": v(24.42, 54.1) * mm});
            skLineSegment(sketch, "E843", {"start": v(24.42, 54.1) * mm, "end": v(24.33, 53.9) * mm});
            skLineSegment(sketch, "E844", {"start": v(24.33, 53.9) * mm, "end": v(24.13, 53.98) * mm});
            skLineSegment(sketch, "E845", {"start": v(24.13, 53.98) * mm, "end": v(23.93, 54.07) * mm});
            skLineSegment(sketch, "E846", {"start": v(23.93, 54.07) * mm, "end": v(23.73, 54.16) * mm});
            skLineSegment(sketch, "E847", {"start": v(23.73, 54.16) * mm, "end": v(23.53, 54.25) * mm});
            skLineSegment(sketch, "E848", {"start": v(23.53, 54.25) * mm, "end": v(23.33, 54.34) * mm});
            skLineSegment(sketch, "E849", {"start": v(23.33, 54.34) * mm, "end": v(23.13, 54.43) * mm});
            skLineSegment(sketch, "E850", {"start": v(23.13, 54.43) * mm, "end": v(22.94, 54.51) * mm});
            skLineSegment(sketch, "E851", {"start": v(22.94, 54.51) * mm, "end": v(22.74, 54.6) * mm});
            skLineSegment(sketch, "E852", {"start": v(22.74, 54.6) * mm, "end": v(22.54, 54.7) * mm});
            skLineSegment(sketch, "E853", {"start": v(22.54, 54.7) * mm, "end": v(22.34, 54.78) * mm});
            skLineSegment(sketch, "E854", {"start": v(22.34, 54.78) * mm, "end": v(22.14, 54.87) * mm});
            skLineSegment(sketch, "E855", {"start": v(22.14, 54.87) * mm, "end": v(22.04, 54.91) * mm});
            skLineSegment(sketch, "E856", {"start": v(22.04, 54.91) * mm, "end": v(22.13, 55.11) * mm});
            skLineSegment(sketch, "E857", {"start": v(22.13, 55.11) * mm, "end": v(22.21, 55.31) * mm});
            skLineSegment(sketch, "E858", {"start": v(22.21, 55.31) * mm, "end": v(22.3, 55.52) * mm});
            skLineSegment(sketch, "E859", {"start": v(22.3, 55.52) * mm, "end": v(22.38, 55.72) * mm});
            skLineSegment(sketch, "E860", {"start": v(22.38, 55.72) * mm, "end": v(22.47, 55.92) * mm});
            skLineSegment(sketch, "E861", {"start": v(22.47, 55.92) * mm, "end": v(22.55, 56.13) * mm});
            skLineSegment(sketch, "E862", {"start": v(22.55, 56.13) * mm, "end": v(22.64, 56.33) * mm});
            skLineSegment(sketch, "E863", {"start": v(22.64, 56.33) * mm, "end": v(22.72, 56.53) * mm});
            skLineSegment(sketch, "E864", {"start": v(22.72, 56.53) * mm, "end": v(22.8, 56.74) * mm});
            skLineSegment(sketch, "E865", {"start": v(22.8, 56.74) * mm, "end": v(22.9, 56.94) * mm});
            skLineSegment(sketch, "E866", {"start": v(22.9, 56.94) * mm, "end": v(22.98, 57.14) * mm});
            skLineSegment(sketch, "E867", {"start": v(22.98, 57.14) * mm, "end": v(23.07, 57.34) * mm});
            skLineSegment(sketch, "E868", {"start": v(23.07, 57.34) * mm, "end": v(23.15, 57.56) * mm});
            skLineSegment(sketch, "E869", {"start": v(23.15, 57.56) * mm, "end": v(23.2, 57.78) * mm});
            skLineSegment(sketch, "E870", {"start": v(23.2, 57.78) * mm, "end": v(23.19, 58.01) * mm});
            skLineSegment(sketch, "E871", {"start": v(23.19, 58.01) * mm, "end": v(23.12, 58.23) * mm});
            skLineSegment(sketch, "E872", {"start": v(23.12, 58.23) * mm, "end": v(23, 58.42) * mm});
            skLineSegment(sketch, "E873", {"start": v(23, 58.42) * mm, "end": v(22.82, 58.57) * mm});
            skLineSegment(sketch, "E874", {"start": v(22.82, 58.57) * mm, "end": v(22.62, 58.67) * mm});
            skLineSegment(sketch, "E875", {"start": v(22.62, 58.67) * mm, "end": v(22.4, 58.71) * mm});
            skLineSegment(sketch, "E876", {"start": v(22.4, 58.71) * mm, "end": v(22.35, 58.72) * mm});
            skLineSegment(sketch, "E877", {"start": v(22.35, 58.72) * mm, "end": v(22.12, 58.69) * mm});
            skLineSegment(sketch, "E878", {"start": v(22.12, 58.69) * mm, "end": v(21.91, 58.6) * mm});
            skLineSegment(sketch, "E879", {"start": v(21.91, 58.6) * mm, "end": v(21.73, 58.47) * mm});
            skLineSegment(sketch, "E880", {"start": v(21.73, 58.47) * mm, "end": v(21.6, 58.3) * mm});
            skLineSegment(sketch, "E881", {"start": v(21.6, 58.3) * mm, "end": v(21.5, 58.08) * mm});
            skLineSegment(sketch, "E882", {"start": v(21.5, 58.08) * mm, "end": v(21.42, 57.88) * mm});
            skLineSegment(sketch, "E883", {"start": v(21.42, 57.88) * mm, "end": v(21.34, 57.67) * mm});
            skLineSegment(sketch, "E884", {"start": v(21.34, 57.67) * mm, "end": v(21.26, 57.46) * mm});
            skLineSegment(sketch, "E885", {"start": v(21.26, 57.46) * mm, "end": v(21.18, 57.26) * mm});
            skLineSegment(sketch, "E886", {"start": v(21.18, 57.26) * mm, "end": v(21.1, 57.06) * mm});
            skLineSegment(sketch, "E887", {"start": v(21.1, 57.06) * mm, "end": v(21.02, 56.85) * mm});
            skLineSegment(sketch, "E888", {"start": v(21.02, 56.85) * mm, "end": v(20.94, 56.65) * mm});
            skLineSegment(sketch, "E889", {"start": v(20.94, 56.65) * mm, "end": v(20.86, 56.44) * mm});
            skLineSegment(sketch, "E890", {"start": v(20.86, 56.44) * mm, "end": v(20.78, 56.23) * mm});
            skLineSegment(sketch, "E891", {"start": v(20.78, 56.23) * mm, "end": v(20.7, 56.03) * mm});
            skLineSegment(sketch, "E892", {"start": v(20.7, 56.03) * mm, "end": v(20.62, 55.83) * mm});
            skLineSegment(sketch, "E893", {"start": v(20.62, 55.83) * mm, "end": v(20.54, 55.62) * mm});
            skLineSegment(sketch, "E894", {"start": v(20.54, 55.62) * mm, "end": v(20.5, 55.53) * mm});
            skLineSegment(sketch, "E895", {"start": v(20.5, 55.53) * mm, "end": v(20.3, 55.6) * mm});
            skLineSegment(sketch, "E896", {"start": v(20.3, 55.6) * mm, "end": v(20.1, 55.68) * mm});
            skLineSegment(sketch, "E897", {"start": v(20.1, 55.68) * mm, "end": v(19.9, 55.76) * mm});
            skLineSegment(sketch, "E898", {"start": v(19.9, 55.76) * mm, "end": v(19.69, 55.83) * mm});
            skLineSegment(sketch, "E899", {"start": v(19.69, 55.83) * mm, "end": v(19.48, 55.9) * mm});
            skLineSegment(sketch, "E900", {"start": v(19.48, 55.9) * mm, "end": v(19.28, 55.98) * mm});
            skLineSegment(sketch, "E901", {"start": v(19.28, 55.98) * mm, "end": v(19.07, 56.05) * mm});
            skLineSegment(sketch, "E902", {"start": v(19.07, 56.05) * mm, "end": v(18.87, 56.13) * mm});
            skLineSegment(sketch, "E903", {"start": v(18.87, 56.13) * mm, "end": v(18.67, 56.2) * mm});
            skLineSegment(sketch, "E904", {"start": v(18.67, 56.2) * mm, "end": v(18.46, 56.28) * mm});
            skLineSegment(sketch, "E905", {"start": v(18.46, 56.28) * mm, "end": v(18.26, 56.35) * mm});
            skLineSegment(sketch, "E906", {"start": v(18.26, 56.35) * mm, "end": v(18.16, 56.39) * mm});
            skLineSegment(sketch, "E907", {"start": v(18.16, 56.39) * mm, "end": v(18.23, 56.6) * mm});
            skLineSegment(sketch, "E908", {"start": v(18.23, 56.6) * mm, "end": v(18.3, 56.8) * mm});
            skLineSegment(sketch, "E909", {"start": v(18.3, 56.8) * mm, "end": v(18.37, 57.01) * mm});
            skLineSegment(sketch, "E910", {"start": v(18.37, 57.01) * mm, "end": v(18.44, 57.22) * mm});
            skLineSegment(sketch, "E911", {"start": v(18.44, 57.22) * mm, "end": v(18.5, 57.42) * mm});
            skLineSegment(sketch, "E912", {"start": v(18.5, 57.42) * mm, "end": v(18.58, 57.64) * mm});
            skLineSegment(sketch, "E913", {"start": v(18.58, 57.64) * mm, "end": v(18.65, 57.84) * mm});
            skLineSegment(sketch, "E914", {"start": v(18.65, 57.84) * mm, "end": v(18.72, 58.05) * mm});
            skLineSegment(sketch, "E915", {"start": v(18.72, 58.05) * mm, "end": v(18.8, 58.26) * mm});
            skLineSegment(sketch, "E916", {"start": v(18.8, 58.26) * mm, "end": v(18.86, 58.47) * mm});
            skLineSegment(sketch, "E917", {"start": v(18.86, 58.47) * mm, "end": v(18.93, 58.67) * mm});
            skLineSegment(sketch, "E918", {"start": v(18.93, 58.67) * mm, "end": v(19, 58.89) * mm});
            skLineSegment(sketch, "E919", {"start": v(19, 58.89) * mm, "end": v(19.08, 59.1) * mm});
            skLineSegment(sketch, "E920", {"start": v(19.08, 59.1) * mm, "end": v(19.11, 59.33) * mm});
            skLineSegment(sketch, "E921", {"start": v(19.11, 59.33) * mm, "end": v(19.08, 59.56) * mm});
            skLineSegment(sketch, "E922", {"start": v(19.08, 59.56) * mm, "end": v(19, 59.77) * mm});
            skLineSegment(sketch, "E923", {"start": v(19, 59.77) * mm, "end": v(18.86, 59.95) * mm});
            skLineSegment(sketch, "E924", {"start": v(18.86, 59.95) * mm, "end": v(18.68, 60.09) * mm});
            skLineSegment(sketch, "E925", {"start": v(18.68, 60.09) * mm, "end": v(18.47, 60.18) * mm});
            skLineSegment(sketch, "E926", {"start": v(18.47, 60.18) * mm, "end": v(18.24, 60.2) * mm});
            skLineSegment(sketch, "E927", {"start": v(18.24, 60.2) * mm, "end": v(18.02, 60.17) * mm});
            skLineSegment(sketch, "E928", {"start": v(18.02, 60.17) * mm, "end": v(17.8, 60.09) * mm});
            skLineSegment(sketch, "E929", {"start": v(17.8, 60.09) * mm, "end": v(17.63, 59.95) * mm});
            skLineSegment(sketch, "E930", {"start": v(17.63, 59.95) * mm, "end": v(17.5, 59.77) * mm});
            skLineSegment(sketch, "E931", {"start": v(17.5, 59.77) * mm, "end": v(17.41, 59.56) * mm});
            skLineSegment(sketch, "E932", {"start": v(17.41, 59.56) * mm, "end": v(17.34, 59.36) * mm});
            skLineSegment(sketch, "E933", {"start": v(17.34, 59.36) * mm, "end": v(17.28, 59.15) * mm});
            skLineSegment(sketch, "E934", {"start": v(17.28, 59.15) * mm, "end": v(17.21, 58.94) * mm});
            skLineSegment(sketch, "E935", {"start": v(17.21, 58.94) * mm, "end": v(17.15, 58.73) * mm});
            skLineSegment(sketch, "E936", {"start": v(17.15, 58.73) * mm, "end": v(17.08, 58.52) * mm});
            skLineSegment(sketch, "E937", {"start": v(17.08, 58.52) * mm, "end": v(17.02, 58.31) * mm});
            skLineSegment(sketch, "E938", {"start": v(17.02, 58.31) * mm, "end": v(16.95, 58.1) * mm});
            skLineSegment(sketch, "E939", {"start": v(16.95, 58.1) * mm, "end": v(16.89, 57.89) * mm});
            skLineSegment(sketch, "E940", {"start": v(16.89, 57.89) * mm, "end": v(16.82, 57.68) * mm});
            skLineSegment(sketch, "E941", {"start": v(16.82, 57.68) * mm, "end": v(16.76, 57.47) * mm});
            skLineSegment(sketch, "E942", {"start": v(16.76, 57.47) * mm, "end": v(16.7, 57.26) * mm});
            skLineSegment(sketch, "E943", {"start": v(16.7, 57.26) * mm, "end": v(16.63, 57.05) * mm});
            skLineSegment(sketch, "E944", {"start": v(16.63, 57.05) * mm, "end": v(16.58, 56.9) * mm});
            skLineSegment(sketch, "E945", {"start": v(16.58, 56.9) * mm, "end": v(16.37, 56.96) * mm});
            skLineSegment(sketch, "E946", {"start": v(16.37, 56.96) * mm, "end": v(16.16, 57.02) * mm});
            skLineSegment(sketch, "E947", {"start": v(16.16, 57.02) * mm, "end": v(15.95, 57.08) * mm});
            skLineSegment(sketch, "E948", {"start": v(15.95, 57.08) * mm, "end": v(15.74, 57.14) * mm});
            skLineSegment(sketch, "E949", {"start": v(15.74, 57.14) * mm, "end": v(15.53, 57.2) * mm});
            skLineSegment(sketch, "E950", {"start": v(15.53, 57.2) * mm, "end": v(15.33, 57.26) * mm});
            skLineSegment(sketch, "E951", {"start": v(15.33, 57.26) * mm, "end": v(15.12, 57.32) * mm});
            skLineSegment(sketch, "E952", {"start": v(15.12, 57.32) * mm, "end": v(14.9, 57.38) * mm});
            skLineSegment(sketch, "E953", {"start": v(14.9, 57.38) * mm, "end": v(14.7, 57.44) * mm});
            skLineSegment(sketch, "E954", {"start": v(14.7, 57.44) * mm, "end": v(14.49, 57.5) * mm});
            skLineSegment(sketch, "E955", {"start": v(14.49, 57.5) * mm, "end": v(14.28, 57.56) * mm});
            skLineSegment(sketch, "E956", {"start": v(14.28, 57.56) * mm, "end": v(14.18, 57.59) * mm});
            skLineSegment(sketch, "E957", {"start": v(14.18, 57.59) * mm, "end": v(14.23, 57.8) * mm});
            skLineSegment(sketch, "E958", {"start": v(14.23, 57.8) * mm, "end": v(14.29, 58.01) * mm});
            skLineSegment(sketch, "E959", {"start": v(14.29, 58.01) * mm, "end": v(14.34, 58.23) * mm});
            skLineSegment(sketch, "E960", {"start": v(14.34, 58.23) * mm, "end": v(14.4, 58.44) * mm});
            skLineSegment(sketch, "E961", {"start": v(14.4, 58.44) * mm, "end": v(14.46, 58.65) * mm});
            skLineSegment(sketch, "E962", {"start": v(14.46, 58.65) * mm, "end": v(14.51, 58.86) * mm});
            skLineSegment(sketch, "E963", {"start": v(14.51, 58.86) * mm, "end": v(14.57, 59.08) * mm});
            skLineSegment(sketch, "E964", {"start": v(14.57, 59.08) * mm, "end": v(14.62, 59.29) * mm});
            skLineSegment(sketch, "E965", {"start": v(14.62, 59.29) * mm, "end": v(14.68, 59.5) * mm});
            skLineSegment(sketch, "E966", {"start": v(14.68, 59.5) * mm, "end": v(14.74, 59.71) * mm});
            skLineSegment(sketch, "E967", {"start": v(14.74, 59.71) * mm, "end": v(14.8, 59.92) * mm});
            skLineSegment(sketch, "E968", {"start": v(14.8, 59.92) * mm, "end": v(14.85, 60.14) * mm});
            skLineSegment(sketch, "E969", {"start": v(14.85, 60.14) * mm, "end": v(14.9, 60.37) * mm});
            skLineSegment(sketch, "E970", {"start": v(14.9, 60.37) * mm, "end": v(14.92, 60.6) * mm});
            skLineSegment(sketch, "E971", {"start": v(14.92, 60.6) * mm, "end": v(14.88, 60.82) * mm});
            skLineSegment(sketch, "E972", {"start": v(14.88, 60.82) * mm, "end": v(14.78, 61.02) * mm});
            skLineSegment(sketch, "E973", {"start": v(14.78, 61.02) * mm, "end": v(14.63, 61.2) * mm});
            skLineSegment(sketch, "E974", {"start": v(14.63, 61.2) * mm, "end": v(14.44, 61.32) * mm});
            skLineSegment(sketch, "E975", {"start": v(14.44, 61.32) * mm, "end": v(14.22, 61.39) * mm});
            skLineSegment(sketch, "E976", {"start": v(14.22, 61.39) * mm, "end": v(14.04, 61.4) * mm});
            skLineSegment(sketch, "E977", {"start": v(14.04, 61.4) * mm, "end": v(13.82, 61.37) * mm});
            skLineSegment(sketch, "E978", {"start": v(13.82, 61.37) * mm, "end": v(13.6, 61.28) * mm});
            skLineSegment(sketch, "E979", {"start": v(13.6, 61.28) * mm, "end": v(13.43, 61.14) * mm});
            skLineSegment(sketch, "E980", {"start": v(13.43, 61.14) * mm, "end": v(13.3, 60.95) * mm});
            skLineSegment(sketch, "E981", {"start": v(13.3, 60.95) * mm, "end": v(13.22, 60.74) * mm});
            skLineSegment(sketch, "E982", {"start": v(13.22, 60.74) * mm, "end": v(13.17, 60.53) * mm});
            skLineSegment(sketch, "E983", {"start": v(13.17, 60.53) * mm, "end": v(13.12, 60.32) * mm});
            skLineSegment(sketch, "E984", {"start": v(13.12, 60.32) * mm, "end": v(13.06, 60.1) * mm});
            skLineSegment(sketch, "E985", {"start": v(13.06, 60.1) * mm, "end": v(13.02, 59.89) * mm});
            skLineSegment(sketch, "E986", {"start": v(13.02, 59.89) * mm, "end": v(12.97, 59.68) * mm});
            skLineSegment(sketch, "E987", {"start": v(12.97, 59.68) * mm, "end": v(12.91, 59.46) * mm});
            skLineSegment(sketch, "E988", {"start": v(12.91, 59.46) * mm, "end": v(12.86, 59.25) * mm});
            skLineSegment(sketch, "E989", {"start": v(12.86, 59.25) * mm, "end": v(12.81, 59.03) * mm});
            skLineSegment(sketch, "E990", {"start": v(12.81, 59.03) * mm, "end": v(12.76, 58.82) * mm});
            skLineSegment(sketch, "E991", {"start": v(12.76, 58.82) * mm, "end": v(12.71, 58.6) * mm});
            skLineSegment(sketch, "E992", {"start": v(12.71, 58.6) * mm, "end": v(12.66, 58.4) * mm});
            skLineSegment(sketch, "E993", {"start": v(12.66, 58.4) * mm, "end": v(12.61, 58.17) * mm});
            skLineSegment(sketch, "E994", {"start": v(12.61, 58.17) * mm, "end": v(12.57, 57.99) * mm});
            skLineSegment(sketch, "E995", {"start": v(12.57, 57.99) * mm, "end": v(12.36, 58.03) * mm});
            skLineSegment(sketch, "E996", {"start": v(12.36, 58.03) * mm, "end": v(12.14, 58.08) * mm});
            skLineSegment(sketch, "E997", {"start": v(12.14, 58.08) * mm, "end": v(11.93, 58.13) * mm});
            skLineSegment(sketch, "E998", {"start": v(11.93, 58.13) * mm, "end": v(11.72, 58.17) * mm});
            skLineSegment(sketch, "E999", {"start": v(11.72, 58.17) * mm, "end": v(11.5, 58.22) * mm});
            skLineSegment(sketch, "E1000", {"start": v(11.5, 58.22) * mm, "end": v(11.3, 58.26) * mm});
            skLineSegment(sketch, "E1001", {"start": v(11.3, 58.26) * mm, "end": v(11.08, 58.3) * mm});
            skLineSegment(sketch, "E1002", {"start": v(11.08, 58.3) * mm, "end": v(10.86, 58.35) * mm});
            skLineSegment(sketch, "E1003", {"start": v(10.86, 58.35) * mm, "end": v(10.65, 58.4) * mm});
            skLineSegment(sketch, "E1004", {"start": v(10.65, 58.4) * mm, "end": v(10.44, 58.44) * mm});
            skLineSegment(sketch, "E1005", {"start": v(10.44, 58.44) * mm, "end": v(10.23, 58.49) * mm});
            skLineSegment(sketch, "E1006", {"start": v(10.23, 58.49) * mm, "end": v(10.12, 58.5) * mm});
            skLineSegment(sketch, "E1007", {"start": v(10.12, 58.5) * mm, "end": v(10.16, 58.72) * mm});
            skLineSegment(sketch, "E1008", {"start": v(10.16, 58.72) * mm, "end": v(10.2, 58.94) * mm});
            skLineSegment(sketch, "E1009", {"start": v(10.2, 58.94) * mm, "end": v(10.25, 59.16) * mm});
            skLineSegment(sketch, "E1010", {"start": v(10.25, 59.16) * mm, "end": v(10.29, 59.37) * mm});
            skLineSegment(sketch, "E1011", {"start": v(10.29, 59.37) * mm, "end": v(10.33, 59.59) * mm});
            skLineSegment(sketch, "E1012", {"start": v(10.33, 59.59) * mm, "end": v(10.37, 59.8) * mm});
            skLineSegment(sketch, "E1013", {"start": v(10.37, 59.8) * mm, "end": v(10.4, 60.02) * mm});
            skLineSegment(sketch, "E1014", {"start": v(10.4, 60.02) * mm, "end": v(10.45, 60.23) * mm});
            skLineSegment(sketch, "E1015", {"start": v(10.45, 60.23) * mm, "end": v(10.5, 60.45) * mm});
            skLineSegment(sketch, "E1016", {"start": v(10.5, 60.45) * mm, "end": v(10.53, 60.67) * mm});
            skLineSegment(sketch, "E1017", {"start": v(10.53, 60.67) * mm, "end": v(10.57, 60.88) * mm});
            skLineSegment(sketch, "E1018", {"start": v(10.57, 60.88) * mm, "end": v(10.62, 61.1) * mm});
            skLineSegment(sketch, "E1019", {"start": v(10.62, 61.1) * mm, "end": v(10.66, 61.33) * mm});
            skLineSegment(sketch, "E1020", {"start": v(10.66, 61.33) * mm, "end": v(10.66, 61.56) * mm});
            skLineSegment(sketch, "E1021", {"start": v(10.66, 61.56) * mm, "end": v(10.6, 61.78) * mm});
            skLineSegment(sketch, "E1022", {"start": v(10.6, 61.78) * mm, "end": v(10.48, 61.98) * mm});
            skLineSegment(sketch, "E1023", {"start": v(10.48, 61.98) * mm, "end": v(10.32, 62.13) * mm});
            skLineSegment(sketch, "E1024", {"start": v(10.32, 62.13) * mm, "end": v(10.12, 62.25) * mm});
            skLineSegment(sketch, "E1025", {"start": v(10.12, 62.25) * mm, "end": v(9.9, 62.3) * mm});
            skLineSegment(sketch, "E1026", {"start": v(9.9, 62.3) * mm, "end": v(9.81, 62.31) * mm});
            skLineSegment(sketch, "E1027", {"start": v(9.81, 62.31) * mm, "end": v(9.59, 62.28) * mm});
            skLineSegment(sketch, "E1028", {"start": v(9.59, 62.28) * mm, "end": v(9.38, 62.2) * mm});
            skLineSegment(sketch, "E1029", {"start": v(9.38, 62.2) * mm, "end": v(9.2, 62.06) * mm});
            skLineSegment(sketch, "E1030", {"start": v(9.2, 62.06) * mm, "end": v(9.05, 61.89) * mm});
            skLineSegment(sketch, "E1031", {"start": v(9.05, 61.89) * mm, "end": v(8.96, 61.68) * mm});
            skLineSegment(sketch, "E1032", {"start": v(8.96, 61.68) * mm, "end": v(8.92, 61.46) * mm});
            skLineSegment(sketch, "E1033", {"start": v(8.92, 61.46) * mm, "end": v(8.89, 61.25) * mm});
            skLineSegment(sketch, "E1034", {"start": v(8.89, 61.25) * mm, "end": v(8.85, 61.03) * mm});
            skLineSegment(sketch, "E1035", {"start": v(8.85, 61.03) * mm, "end": v(8.82, 60.82) * mm});
            skLineSegment(sketch, "E1036", {"start": v(8.82, 60.82) * mm, "end": v(8.78, 60.6) * mm});
            skLineSegment(sketch, "E1037", {"start": v(8.78, 60.6) * mm, "end": v(8.75, 60.38) * mm});
            skLineSegment(sketch, "E1038", {"start": v(8.75, 60.38) * mm, "end": v(8.71, 60.16) * mm});
            skLineSegment(sketch, "E1039", {"start": v(8.71, 60.16) * mm, "end": v(8.68, 59.95) * mm});
            skLineSegment(sketch, "E1040", {"start": v(8.68, 59.95) * mm, "end": v(8.64, 59.73) * mm});
            skLineSegment(sketch, "E1041", {"start": v(8.64, 59.73) * mm, "end": v(8.6, 59.51) * mm});
            skLineSegment(sketch, "E1042", {"start": v(8.6, 59.51) * mm, "end": v(8.57, 59.3) * mm});
            skLineSegment(sketch, "E1043", {"start": v(8.57, 59.3) * mm, "end": v(8.54, 59.08) * mm});
            skLineSegment(sketch, "E1044", {"start": v(8.54, 59.08) * mm, "end": v(8.5, 58.86) * mm});
            skLineSegment(sketch, "E1045", {"start": v(8.5, 58.86) * mm, "end": v(8.5, 58.8) * mm});
            skLineSegment(sketch, "E1046", {"start": v(8.5, 58.8) * mm, "end": v(8.28, 58.83) * mm});
            skLineSegment(sketch, "E1047", {"start": v(8.28, 58.83) * mm, "end": v(8.06, 58.86) * mm});
            skLineSegment(sketch, "E1048", {"start": v(8.06, 58.86) * mm, "end": v(7.84, 58.89) * mm});
            skLineSegment(sketch, "E1049", {"start": v(7.84, 58.89) * mm, "end": v(7.63, 58.92) * mm});
            skLineSegment(sketch, "E1050", {"start": v(7.63, 58.92) * mm, "end": v(7.41, 58.95) * mm});
            skLineSegment(sketch, "E1051", {"start": v(7.41, 58.95) * mm, "end": v(7.2, 58.98) * mm});
            skLineSegment(sketch, "E1052", {"start": v(7.2, 58.98) * mm, "end": v(6.98, 59) * mm});
            skLineSegment(sketch, "E1053", {"start": v(6.98, 59) * mm, "end": v(6.77, 59.04) * mm});
            skLineSegment(sketch, "E1054", {"start": v(6.77, 59.04) * mm, "end": v(6.55, 59.07) * mm});
            skLineSegment(sketch, "E1055", {"start": v(6.55, 59.07) * mm, "end": v(6.33, 59.1) * mm});
            skLineSegment(sketch, "E1056", {"start": v(6.33, 59.1) * mm, "end": v(6.12, 59.13) * mm});
            skLineSegment(sketch, "E1057", {"start": v(6.12, 59.13) * mm, "end": v(6.01, 59.15) * mm});
            skLineSegment(sketch, "E1058", {"start": v(6.01, 59.15) * mm, "end": v(6.04, 59.36) * mm});
            skLineSegment(sketch, "E1059", {"start": v(6.04, 59.36) * mm, "end": v(6.06, 59.58) * mm});
            skLineSegment(sketch, "E1060", {"start": v(6.06, 59.58) * mm, "end": v(6.1, 59.8) * mm});
            skLineSegment(sketch, "E1061", {"start": v(6.1, 59.8) * mm, "end": v(6.12, 60.02) * mm});
            skLineSegment(sketch, "E1062", {"start": v(6.12, 60.02) * mm, "end": v(6.14, 60.23) * mm});
            skLineSegment(sketch, "E1063", {"start": v(6.14, 60.23) * mm, "end": v(6.17, 60.46) * mm});
            skLineSegment(sketch, "E1064", {"start": v(6.17, 60.46) * mm, "end": v(6.2, 60.67) * mm});
            skLineSegment(sketch, "E1065", {"start": v(6.2, 60.67) * mm, "end": v(6.22, 60.89) * mm});
            skLineSegment(sketch, "E1066", {"start": v(6.22, 60.89) * mm, "end": v(6.25, 61.11) * mm});
            skLineSegment(sketch, "E1067", {"start": v(6.25, 61.11) * mm, "end": v(6.27, 61.33) * mm});
            skLineSegment(sketch, "E1068", {"start": v(6.27, 61.33) * mm, "end": v(6.3, 61.54) * mm});
            skLineSegment(sketch, "E1069", {"start": v(6.3, 61.54) * mm, "end": v(6.33, 61.77) * mm});
            skLineSegment(sketch, "E1070", {"start": v(6.33, 61.77) * mm, "end": v(6.35, 62) * mm});
            skLineSegment(sketch, "E1071", {"start": v(6.35, 62) * mm, "end": v(6.34, 62.23) * mm});
            skLineSegment(sketch, "E1072", {"start": v(6.34, 62.23) * mm, "end": v(6.26, 62.44) * mm});
            skLineSegment(sketch, "E1073", {"start": v(6.26, 62.44) * mm, "end": v(6.13, 62.63) * mm});
            skLineSegment(sketch, "E1074", {"start": v(6.13, 62.63) * mm, "end": v(5.96, 62.78) * mm});
            skLineSegment(sketch, "E1075", {"start": v(5.96, 62.78) * mm, "end": v(5.75, 62.87) * mm});
            skLineSegment(sketch, "E1076", {"start": v(5.75, 62.87) * mm, "end": v(5.53, 62.92) * mm});
            skLineSegment(sketch, "E1077", {"start": v(5.53, 62.92) * mm, "end": v(5.49, 62.92) * mm});
            skLineSegment(sketch, "E1078", {"start": v(5.49, 62.92) * mm, "end": v(5.26, 62.89) * mm});
            skLineSegment(sketch, "E1079", {"start": v(5.26, 62.89) * mm, "end": v(5.05, 62.8) * mm});
            skLineSegment(sketch, "E1080", {"start": v(5.05, 62.8) * mm, "end": v(4.87, 62.66) * mm});
            skLineSegment(sketch, "E1081", {"start": v(4.87, 62.66) * mm, "end": v(4.73, 62.48) * mm});
            skLineSegment(sketch, "E1082", {"start": v(4.73, 62.48) * mm, "end": v(4.65, 62.27) * mm});
            skLineSegment(sketch, "E1083", {"start": v(4.65, 62.27) * mm, "end": v(4.61, 62.04) * mm});
            skLineSegment(sketch, "E1084", {"start": v(4.61, 62.04) * mm, "end": v(4.6, 61.82) * mm});
            skLineSegment(sketch, "E1085", {"start": v(4.6, 61.82) * mm, "end": v(4.58, 61.6) * mm});
            skLineSegment(sketch, "E1086", {"start": v(4.58, 61.6) * mm, "end": v(4.55, 61.38) * mm});
            skLineSegment(sketch, "E1087", {"start": v(4.55, 61.38) * mm, "end": v(4.54, 61.17) * mm});
            skLineSegment(sketch, "E1088", {"start": v(4.54, 61.17) * mm, "end": v(4.52, 60.95) * mm});
            skLineSegment(sketch, "E1089", {"start": v(4.52, 60.95) * mm, "end": v(4.5, 60.73) * mm});
            skLineSegment(sketch, "E1090", {"start": v(4.5, 60.73) * mm, "end": v(4.48, 60.5) * mm});
            skLineSegment(sketch, "E1091", {"start": v(4.48, 60.5) * mm, "end": v(4.46, 60.3) * mm});
            skLineSegment(sketch, "E1092", {"start": v(4.46, 60.3) * mm, "end": v(4.44, 60.07) * mm});
            skLineSegment(sketch, "E1093", {"start": v(4.44, 60.07) * mm, "end": v(4.42, 59.85) * mm});
            skLineSegment(sketch, "E1094", {"start": v(4.42, 59.85) * mm, "end": v(4.4, 59.64) * mm});
            skLineSegment(sketch, "E1095", {"start": v(4.4, 59.64) * mm, "end": v(4.38, 59.41) * mm});
            skLineSegment(sketch, "E1096", {"start": v(4.38, 59.41) * mm, "end": v(4.37, 59.32) * mm});
            skLineSegment(sketch, "E1097", {"start": v(4.37, 59.32) * mm, "end": v(4.15, 59.33) * mm});
            skLineSegment(sketch, "E1098", {"start": v(4.15, 59.33) * mm, "end": v(3.93, 59.35) * mm});
            skLineSegment(sketch, "E1099", {"start": v(3.93, 59.35) * mm, "end": v(3.71, 59.36) * mm});
            skLineSegment(sketch, "E1100", {"start": v(3.71, 59.36) * mm, "end": v(3.5, 59.38) * mm});
            skLineSegment(sketch, "E1101", {"start": v(3.5, 59.38) * mm, "end": v(3.28, 59.4) * mm});
            skLineSegment(sketch, "E1102", {"start": v(3.28, 59.4) * mm, "end": v(3.06, 59.4) * mm});
            skLineSegment(sketch, "E1103", {"start": v(3.06, 59.4) * mm, "end": v(2.85, 59.42) * mm});
            skLineSegment(sketch, "E1104", {"start": v(2.85, 59.42) * mm, "end": v(2.63, 59.44) * mm});
            skLineSegment(sketch, "E1105", {"start": v(2.63, 59.44) * mm, "end": v(2.41, 59.46) * mm});
            skLineSegment(sketch, "E1106", {"start": v(2.41, 59.46) * mm, "end": v(2.2, 59.47) * mm});
            skLineSegment(sketch, "E1107", {"start": v(2.2, 59.47) * mm, "end": v(1.98, 59.49) * mm});
            skLineSegment(sketch, "E1108", {"start": v(1.98, 59.49) * mm, "end": v(1.87, 59.5) * mm});
            skLineSegment(sketch, "E1109", {"start": v(1.87, 59.5) * mm, "end": v(1.88, 59.71) * mm});
            skLineSegment(sketch, "E1110", {"start": v(1.88, 59.71) * mm, "end": v(1.9, 59.93) * mm});
            skLineSegment(sketch, "E1111", {"start": v(1.9, 59.93) * mm, "end": v(1.9, 60.15) * mm});
            skLineSegment(sketch, "E1112", {"start": v(1.9, 60.15) * mm, "end": v(1.91, 60.37) * mm});
            skLineSegment(sketch, "E1113", {"start": v(1.91, 60.37) * mm, "end": v(1.92, 60.59) * mm});
            skLineSegment(sketch, "E1114", {"start": v(1.92, 60.59) * mm, "end": v(1.93, 60.81) * mm});
            skLineSegment(sketch, "E1115", {"start": v(1.93, 60.81) * mm, "end": v(1.95, 61.03) * mm});
            skLineSegment(sketch, "E1116", {"start": v(1.95, 61.03) * mm, "end": v(1.96, 61.25) * mm});
            skLineSegment(sketch, "E1117", {"start": v(1.96, 61.25) * mm, "end": v(1.97, 61.47) * mm});
            skLineSegment(sketch, "E1118", {"start": v(1.97, 61.47) * mm, "end": v(1.98, 61.69) * mm});
            skLineSegment(sketch, "E1119", {"start": v(1.98, 61.69) * mm, "end": v(1.99, 61.9) * mm});
            skLineSegment(sketch, "E1120", {"start": v(1.99, 61.9) * mm, "end": v(2, 62.13) * mm});
            skLineSegment(sketch, "E1121", {"start": v(2, 62.13) * mm, "end": v(2, 62.36) * mm});
            skLineSegment(sketch, "E1122", {"start": v(2, 62.36) * mm, "end": v(1.98, 62.59) * mm});
            skLineSegment(sketch, "E1123", {"start": v(1.98, 62.59) * mm, "end": v(1.89, 62.8) * mm});
            skLineSegment(sketch, "E1124", {"start": v(1.89, 62.8) * mm, "end": v(1.75, 62.98) * mm});
            skLineSegment(sketch, "E1125", {"start": v(1.75, 62.98) * mm, "end": v(1.56, 63.11) * mm});
            skLineSegment(sketch, "E1126", {"start": v(1.56, 63.11) * mm, "end": v(1.35, 63.2) * mm});
            skLineSegment(sketch, "E1127", {"start": v(1.35, 63.2) * mm, "end": v(1.13, 63.22) * mm});
            skLineSegment(sketch, "E1128", {"start": v(1.13, 63.22) * mm, "end": v(0.9, 63.19) * mm});
            skLineSegment(sketch, "E1129", {"start": v(0.9, 63.19) * mm, "end": v(0.7, 63.1) * mm});
            skLineSegment(sketch, "E1130", {"start": v(0.7, 63.1) * mm, "end": v(0.52, 62.95) * mm});
            skLineSegment(sketch, "E1131", {"start": v(0.52, 62.95) * mm, "end": v(0.38, 62.77) * mm});
            skLineSegment(sketch, "E1132", {"start": v(0.38, 62.77) * mm, "end": v(0.3, 62.56) * mm});
            skLineSegment(sketch, "E1133", {"start": v(0.3, 62.56) * mm, "end": v(0.28, 62.34) * mm});
            skLineSegment(sketch, "E1134", {"start": v(0.28, 62.34) * mm, "end": v(0.27, 62.12) * mm});
            skLineSegment(sketch, "E1135", {"start": v(0.27, 62.12) * mm, "end": v(0.27, 61.9) * mm});
            skLineSegment(sketch, "E1136", {"start": v(0.27, 61.9) * mm, "end": v(0.26, 61.69) * mm});
            skLineSegment(sketch, "E1137", {"start": v(0.26, 61.69) * mm, "end": v(0.26, 61.47) * mm});
            skLineSegment(sketch, "E1138", {"start": v(0.26, 61.47) * mm, "end": v(0.25, 61.25) * mm});
            skLineSegment(sketch, "E1139", {"start": v(0.25, 61.25) * mm, "end": v(0.25, 61.03) * mm});
            skLineSegment(sketch, "E1140", {"start": v(0.25, 61.03) * mm, "end": v(0.24, 60.81) * mm});
            skLineSegment(sketch, "E1141", {"start": v(0.24, 60.81) * mm, "end": v(0.24, 60.59) * mm});
            skLineSegment(sketch, "E1142", {"start": v(0.24, 60.59) * mm, "end": v(0.23, 60.37) * mm});
            skLineSegment(sketch, "E1143", {"start": v(0.23, 60.37) * mm, "end": v(0.23, 60.15) * mm});
            skLineSegment(sketch, "E1144", {"start": v(0.23, 60.15) * mm, "end": v(0.22, 59.93) * mm});
            skLineSegment(sketch, "E1145", {"start": v(0.22, 59.93) * mm, "end": v(0.22, 59.71) * mm});
            skLineSegment(sketch, "E1146", {"start": v(0.22, 59.71) * mm, "end": v(0.22, 59.55) * mm});
            skLineSegment(sketch, "E1147", {"start": v(0.22, 59.55) * mm, "end": v(0, 59.55) * mm});
            skLineSegment(sketch, "E1148", {"start": v(0, 59.55) * mm, "end": v(-0.22, 59.55) * mm});
            skLineSegment(sketch, "E1149", {"start": v(-0.22, 59.55) * mm, "end": v(-0.44, 59.55) * mm});
            skLineSegment(sketch, "E1150", {"start": v(-0.44, 59.55) * mm, "end": v(-0.66, 59.55) * mm});
            skLineSegment(sketch, "E1151", {"start": v(-0.66, 59.55) * mm, "end": v(-0.87, 59.55) * mm});
            skLineSegment(sketch, "E1152", {"start": v(-0.87, 59.55) * mm, "end": v(-1.1, 59.55) * mm});
            skLineSegment(sketch, "E1153", {"start": v(-1.1, 59.55) * mm, "end": v(-1.3, 59.55) * mm});
            skLineSegment(sketch, "E1154", {"start": v(-1.3, 59.55) * mm, "end": v(-1.53, 59.55) * mm});
            skLineSegment(sketch, "E1155", {"start": v(-1.53, 59.55) * mm, "end": v(-1.74, 59.55) * mm});
            skLineSegment(sketch, "E1156", {"start": v(-1.74, 59.55) * mm, "end": v(-1.96, 59.55) * mm});
            skLineSegment(sketch, "E1157", {"start": v(-1.96, 59.55) * mm, "end": v(-2.18, 59.55) * mm});
            skLineSegment(sketch, "E1158", {"start": v(-2.18, 59.55) * mm, "end": v(-2.29, 59.55) * mm});
            skLineSegment(sketch, "E1159", {"start": v(-2.29, 59.55) * mm, "end": v(-2.3, 59.77) * mm});
            skLineSegment(sketch, "E1160", {"start": v(-2.3, 59.77) * mm, "end": v(-2.3, 59.99) * mm});
            skLineSegment(sketch, "E1161", {"start": v(-2.3, 59.99) * mm, "end": v(-2.3, 60.21) * mm});
            skLineSegment(sketch, "E1162", {"start": v(-2.3, 60.21) * mm, "end": v(-2.3, 60.43) * mm});
            skLineSegment(sketch, "E1163", {"start": v(-2.3, 60.43) * mm, "end": v(-2.31, 60.65) * mm});
            skLineSegment(sketch, "E1164", {"start": v(-2.31, 60.65) * mm, "end": v(-2.31, 60.87) * mm});
            skLineSegment(sketch, "E1165", {"start": v(-2.31, 60.87) * mm, "end": v(-2.32, 61.09) * mm});
            skLineSegment(sketch, "E1166", {"start": v(-2.32, 61.09) * mm, "end": v(-2.32, 61.3) * mm});
            skLineSegment(sketch, "E1167", {"start": v(-2.32, 61.3) * mm, "end": v(-2.33, 61.53) * mm});
            skLineSegment(sketch, "E1168", {"start": v(-2.33, 61.53) * mm, "end": v(-2.33, 61.75) * mm});
            skLineSegment(sketch, "E1169", {"start": v(-2.33, 61.75) * mm, "end": v(-2.34, 61.97) * mm});
            skLineSegment(sketch, "E1170", {"start": v(-2.34, 61.97) * mm, "end": v(-2.34, 62.19) * mm});
            skLineSegment(sketch, "E1171", {"start": v(-2.34, 62.19) * mm, "end": v(-2.35, 62.42) * mm});
            skLineSegment(sketch, "E1172", {"start": v(-2.35, 62.42) * mm, "end": v(-2.4, 62.65) * mm});
            skLineSegment(sketch, "E1173", {"start": v(-2.4, 62.65) * mm, "end": v(-2.5, 62.85) * mm});
            skLineSegment(sketch, "E1174", {"start": v(-2.5, 62.85) * mm, "end": v(-2.65, 63.02) * mm});
            skLineSegment(sketch, "E1175", {"start": v(-2.65, 63.02) * mm, "end": v(-2.85, 63.14) * mm});
            skLineSegment(sketch, "E1176", {"start": v(-2.85, 63.14) * mm, "end": v(-3.06, 63.2) * mm});
            skLineSegment(sketch, "E1177", {"start": v(-3.06, 63.2) * mm, "end": v(-3.2, 63.22) * mm});
            skLineSegment(sketch, "E1178", {"start": v(-3.2, 63.22) * mm, "end": v(-3.42, 63.2) * mm});
            skLineSegment(sketch, "E1179", {"start": v(-3.42, 63.2) * mm, "end": v(-3.63, 63.11) * mm});
            skLineSegment(sketch, "E1180", {"start": v(-3.63, 63.11) * mm, "end": v(-3.82, 62.98) * mm});
            skLineSegment(sketch, "E1181", {"start": v(-3.82, 62.98) * mm, "end": v(-3.96, 62.8) * mm});
            skLineSegment(sketch, "E1182", {"start": v(-3.96, 62.8) * mm, "end": v(-4.05, 62.59) * mm});
            skLineSegment(sketch, "E1183", {"start": v(-4.05, 62.59) * mm, "end": v(-4.08, 62.36) * mm});
            skLineSegment(sketch, "E1184", {"start": v(-4.08, 62.36) * mm, "end": v(-4.07, 62.13) * mm});
            skLineSegment(sketch, "E1185", {"start": v(-4.07, 62.13) * mm, "end": v(-4.06, 61.91) * mm});
            skLineSegment(sketch, "E1186", {"start": v(-4.06, 61.91) * mm, "end": v(-4.05, 61.7) * mm});
            skLineSegment(sketch, "E1187", {"start": v(-4.05, 61.7) * mm, "end": v(-4.04, 61.47) * mm});
            skLineSegment(sketch, "E1188", {"start": v(-4.04, 61.47) * mm, "end": v(-4.03, 61.25) * mm});
            skLineSegment(sketch, "E1189", {"start": v(-4.03, 61.25) * mm, "end": v(-4.02, 61.03) * mm});
            skLineSegment(sketch, "E1190", {"start": v(-4.02, 61.03) * mm, "end": v(-4, 60.81) * mm});
            skLineSegment(sketch, "E1191", {"start": v(-4, 60.81) * mm, "end": v(-4, 60.6) * mm});
            skLineSegment(sketch, "E1192", {"start": v(-4, 60.6) * mm, "end": v(-3.98, 60.38) * mm});
            skLineSegment(sketch, "E1193", {"start": v(-3.98, 60.38) * mm, "end": v(-3.97, 60.15) * mm});
            skLineSegment(sketch, "E1194", {"start": v(-3.97, 60.15) * mm, "end": v(-3.96, 59.93) * mm});
            skLineSegment(sketch, "E1195", {"start": v(-3.96, 59.93) * mm, "end": v(-3.95, 59.72) * mm});
            skLineSegment(sketch, "E1196", {"start": v(-3.95, 59.72) * mm, "end": v(-3.94, 59.5) * mm});
            skLineSegment(sketch, "E1197", {"start": v(-3.94, 59.5) * mm, "end": v(-4.16, 59.48) * mm});
            skLineSegment(sketch, "E1198", {"start": v(-4.16, 59.48) * mm, "end": v(-4.38, 59.46) * mm});
            skLineSegment(sketch, "E1199", {"start": v(-4.38, 59.46) * mm, "end": v(-4.6, 59.45) * mm});
            skLineSegment(sketch, "E1200", {"start": v(-4.6, 59.45) * mm, "end": v(-4.81, 59.43) * mm});
            skLineSegment(sketch, "E1201", {"start": v(-4.81, 59.43) * mm, "end": v(-5.03, 59.42) * mm});
            skLineSegment(sketch, "E1202", {"start": v(-5.03, 59.42) * mm, "end": v(-5.25, 59.4) * mm});
            skLineSegment(sketch, "E1203", {"start": v(-5.25, 59.4) * mm, "end": v(-5.46, 59.39) * mm});
            skLineSegment(sketch, "E1204", {"start": v(-5.46, 59.39) * mm, "end": v(-5.68, 59.37) * mm});
            skLineSegment(sketch, "E1205", {"start": v(-5.68, 59.37) * mm, "end": v(-5.9, 59.36) * mm});
            skLineSegment(sketch, "E1206", {"start": v(-5.9, 59.36) * mm, "end": v(-6.11, 59.34) * mm});
            skLineSegment(sketch, "E1207", {"start": v(-6.11, 59.34) * mm, "end": v(-6.33, 59.33) * mm});
            skLineSegment(sketch, "E1208", {"start": v(-6.33, 59.33) * mm, "end": v(-6.44, 59.32) * mm});
            skLineSegment(sketch, "E1209", {"start": v(-6.44, 59.32) * mm, "end": v(-6.46, 59.54) * mm});
            skLineSegment(sketch, "E1210", {"start": v(-6.46, 59.54) * mm, "end": v(-6.48, 59.75) * mm});
            skLineSegment(sketch, "E1211", {"start": v(-6.48, 59.75) * mm, "end": v(-6.5, 59.98) * mm});
            skLineSegment(sketch, "E1212", {"start": v(-6.5, 59.98) * mm, "end": v(-6.52, 60.2) * mm});
            skLineSegment(sketch, "E1213", {"start": v(-6.52, 60.2) * mm, "end": v(-6.54, 60.4) * mm});
            skLineSegment(sketch, "E1214", {"start": v(-6.54, 60.4) * mm, "end": v(-6.56, 60.63) * mm});
            skLineSegment(sketch, "E1215", {"start": v(-6.56, 60.63) * mm, "end": v(-6.58, 60.85) * mm});
            skLineSegment(sketch, "E1216", {"start": v(-6.58, 60.85) * mm, "end": v(-6.6, 61.07) * mm});
            skLineSegment(sketch, "E1217", {"start": v(-6.6, 61.07) * mm, "end": v(-6.62, 61.29) * mm});
            skLineSegment(sketch, "E1218", {"start": v(-6.62, 61.29) * mm, "end": v(-6.64, 61.5) * mm});
            skLineSegment(sketch, "E1219", {"start": v(-6.64, 61.5) * mm, "end": v(-6.66, 61.72) * mm});
            skLineSegment(sketch, "E1220", {"start": v(-6.66, 61.72) * mm, "end": v(-6.68, 61.95) * mm});
            skLineSegment(sketch, "E1221", {"start": v(-6.68, 61.95) * mm, "end": v(-6.7, 62.18) * mm});
            skLineSegment(sketch, "E1222", {"start": v(-6.7, 62.18) * mm, "end": v(-6.76, 62.4) * mm});
            skLineSegment(sketch, "E1223", {"start": v(-6.76, 62.4) * mm, "end": v(-6.88, 62.6) * mm});
            skLineSegment(sketch, "E1224", {"start": v(-6.88, 62.6) * mm, "end": v(-7.05, 62.75) * mm});
            skLineSegment(sketch, "E1225", {"start": v(-7.05, 62.75) * mm, "end": v(-7.24, 62.86) * mm});
            skLineSegment(sketch, "E1226", {"start": v(-7.24, 62.86) * mm, "end": v(-7.47, 62.91) * mm});
            skLineSegment(sketch, "E1227", {"start": v(-7.47, 62.91) * mm, "end": v(-7.56, 62.92) * mm});
            skLineSegment(sketch, "E1228", {"start": v(-7.56, 62.92) * mm, "end": v(-7.78, 62.89) * mm});
            skLineSegment(sketch, "E1229", {"start": v(-7.78, 62.89) * mm, "end": v(-8, 62.8) * mm});
            skLineSegment(sketch, "E1230", {"start": v(-8, 62.8) * mm, "end": v(-8.17, 62.66) * mm});
            skLineSegment(sketch, "E1231", {"start": v(-8.17, 62.66) * mm, "end": v(-8.3, 62.48) * mm});
            skLineSegment(sketch, "E1232", {"start": v(-8.3, 62.48) * mm, "end": v(-8.4, 62.27) * mm});
            skLineSegment(sketch, "E1233", {"start": v(-8.4, 62.27) * mm, "end": v(-8.42, 62.04) * mm});
            skLineSegment(sketch, "E1234", {"start": v(-8.42, 62.04) * mm, "end": v(-8.4, 61.83) * mm});
            skLineSegment(sketch, "E1235", {"start": v(-8.4, 61.83) * mm, "end": v(-8.38, 61.61) * mm});
            skLineSegment(sketch, "E1236", {"start": v(-8.38, 61.61) * mm, "end": v(-8.35, 61.4) * mm});
            skLineSegment(sketch, "E1237", {"start": v(-8.35, 61.4) * mm, "end": v(-8.33, 61.18) * mm});
            skLineSegment(sketch, "E1238", {"start": v(-8.33, 61.18) * mm, "end": v(-8.3, 60.96) * mm});
            skLineSegment(sketch, "E1239", {"start": v(-8.3, 60.96) * mm, "end": v(-8.27, 60.74) * mm});
            skLineSegment(sketch, "E1240", {"start": v(-8.27, 60.74) * mm, "end": v(-8.25, 60.52) * mm});
            skLineSegment(sketch, "E1241", {"start": v(-8.25, 60.52) * mm, "end": v(-8.22, 60.3) * mm});
            skLineSegment(sketch, "E1242", {"start": v(-8.22, 60.3) * mm, "end": v(-8.2, 60.08) * mm});
            skLineSegment(sketch, "E1243", {"start": v(-8.2, 60.08) * mm, "end": v(-8.17, 59.87) * mm});
            skLineSegment(sketch, "E1244", {"start": v(-8.17, 59.87) * mm, "end": v(-8.14, 59.65) * mm});
            skLineSegment(sketch, "E1245", {"start": v(-8.14, 59.65) * mm, "end": v(-8.12, 59.43) * mm});
            skLineSegment(sketch, "E1246", {"start": v(-8.12, 59.43) * mm, "end": v(-8.1, 59.21) * mm});
            skLineSegment(sketch, "E1247", {"start": v(-8.1, 59.21) * mm, "end": v(-8.08, 59.15) * mm});
            skLineSegment(sketch, "E1248", {"start": v(-8.08, 59.15) * mm, "end": v(-8.3, 59.12) * mm});
            skLineSegment(sketch, "E1249", {"start": v(-8.3, 59.12) * mm, "end": v(-8.52, 59.08) * mm});
            skLineSegment(sketch, "E1250", {"start": v(-8.52, 59.08) * mm, "end": v(-8.73, 59.05) * mm});
            skLineSegment(sketch, "E1251", {"start": v(-8.73, 59.05) * mm, "end": v(-8.95, 59.02) * mm});
            skLineSegment(sketch, "E1252", {"start": v(-8.95, 59.02) * mm, "end": v(-9.16, 59) * mm});
            skLineSegment(sketch, "E1253", {"start": v(-9.16, 59) * mm, "end": v(-9.38, 58.96) * mm});
            skLineSegment(sketch, "E1254", {"start": v(-9.38, 58.96) * mm, "end": v(-9.6, 58.93) * mm});
            skLineSegment(sketch, "E1255", {"start": v(-9.6, 58.93) * mm, "end": v(-9.81, 58.9) * mm});
            skLineSegment(sketch, "E1256", {"start": v(-9.81, 58.9) * mm, "end": v(-10.03, 58.87) * mm});
            skLineSegment(sketch, "E1257", {"start": v(-10.03, 58.87) * mm, "end": v(-10.24, 58.84) * mm});
            skLineSegment(sketch, "E1258", {"start": v(-10.24, 58.84) * mm, "end": v(-10.46, 58.81) * mm});
            skLineSegment(sketch, "E1259", {"start": v(-10.46, 58.81) * mm, "end": v(-10.56, 58.8) * mm});
            skLineSegment(sketch, "E1260", {"start": v(-10.56, 58.8) * mm, "end": v(-10.6, 59.01) * mm});
            skLineSegment(sketch, "E1261", {"start": v(-10.6, 59.01) * mm, "end": v(-10.63, 59.23) * mm});
            skLineSegment(sketch, "E1262", {"start": v(-10.63, 59.23) * mm, "end": v(-10.67, 59.45) * mm});
            skLineSegment(sketch, "E1263", {"start": v(-10.67, 59.45) * mm, "end": v(-10.7, 59.66) * mm});
            skLineSegment(sketch, "E1264", {"start": v(-10.7, 59.66) * mm, "end": v(-10.74, 59.88) * mm});
            skLineSegment(sketch, "E1265", {"start": v(-10.74, 59.88) * mm, "end": v(-10.77, 60.1) * mm});
            skLineSegment(sketch, "E1266", {"start": v(-10.77, 60.1) * mm, "end": v(-10.8, 60.31) * mm});
            skLineSegment(sketch, "E1267", {"start": v(-10.8, 60.31) * mm, "end": v(-10.84, 60.53) * mm});
            skLineSegment(sketch, "E1268", {"start": v(-10.84, 60.53) * mm, "end": v(-10.88, 60.75) * mm});
            skLineSegment(sketch, "E1269", {"start": v(-10.88, 60.75) * mm, "end": v(-10.91, 60.97) * mm});
            skLineSegment(sketch, "E1270", {"start": v(-10.91, 60.97) * mm, "end": v(-10.95, 61.18) * mm});
            skLineSegment(sketch, "E1271", {"start": v(-10.95, 61.18) * mm, "end": v(-10.98, 61.4) * mm});
            skLineSegment(sketch, "E1272", {"start": v(-10.98, 61.4) * mm, "end": v(-11.02, 61.63) * mm});
            skLineSegment(sketch, "E1273", {"start": v(-11.02, 61.63) * mm, "end": v(-11.1, 61.85) * mm});
            skLineSegment(sketch, "E1274", {"start": v(-11.1, 61.85) * mm, "end": v(-11.23, 62.03) * mm});
            skLineSegment(sketch, "E1275", {"start": v(-11.23, 62.03) * mm, "end": v(-11.4, 62.18) * mm});
            skLineSegment(sketch, "E1276", {"start": v(-11.4, 62.18) * mm, "end": v(-11.61, 62.27) * mm});
            skLineSegment(sketch, "E1277", {"start": v(-11.61, 62.27) * mm, "end": v(-11.84, 62.3) * mm});
            skLineSegment(sketch, "E1278", {"start": v(-11.84, 62.3) * mm, "end": v(-11.88, 62.31) * mm});
            skLineSegment(sketch, "E1279", {"start": v(-11.88, 62.31) * mm, "end": v(-12.1, 62.28) * mm});
            skLineSegment(sketch, "E1280", {"start": v(-12.1, 62.28) * mm, "end": v(-12.32, 62.19) * mm});
            skLineSegment(sketch, "E1281", {"start": v(-12.32, 62.19) * mm, "end": v(-12.5, 62.04) * mm});
            skLineSegment(sketch, "E1282", {"start": v(-12.5, 62.04) * mm, "end": v(-12.63, 61.86) * mm});
            skLineSegment(sketch, "E1283", {"start": v(-12.63, 61.86) * mm, "end": v(-12.71, 61.65) * mm});
            skLineSegment(sketch, "E1284", {"start": v(-12.71, 61.65) * mm, "end": v(-12.74, 61.42) * mm});
            skLineSegment(sketch, "E1285", {"start": v(-12.74, 61.42) * mm, "end": v(-12.7, 61.2) * mm});
            skLineSegment(sketch, "E1286", {"start": v(-12.7, 61.2) * mm, "end": v(-12.66, 60.98) * mm});
            skLineSegment(sketch, "E1287", {"start": v(-12.66, 60.98) * mm, "end": v(-12.62, 60.77) * mm});
            skLineSegment(sketch, "E1288", {"start": v(-12.62, 60.77) * mm, "end": v(-12.58, 60.55) * mm});
            skLineSegment(sketch, "E1289", {"start": v(-12.58, 60.55) * mm, "end": v(-12.54, 60.33) * mm});
            skLineSegment(sketch, "E1290", {"start": v(-12.54, 60.33) * mm, "end": v(-12.5, 60.12) * mm});
            skLineSegment(sketch, "E1291", {"start": v(-12.5, 60.12) * mm, "end": v(-12.46, 59.9) * mm});
            skLineSegment(sketch, "E1292", {"start": v(-12.46, 59.9) * mm, "end": v(-12.42, 59.68) * mm});
            skLineSegment(sketch, "E1293", {"start": v(-12.42, 59.68) * mm, "end": v(-12.38, 59.47) * mm});
            skLineSegment(sketch, "E1294", {"start": v(-12.38, 59.47) * mm, "end": v(-12.33, 59.25) * mm});
            skLineSegment(sketch, "E1295", {"start": v(-12.33, 59.25) * mm, "end": v(-12.3, 59.04) * mm});
            skLineSegment(sketch, "E1296", {"start": v(-12.3, 59.04) * mm, "end": v(-12.25, 58.82) * mm});
            skLineSegment(sketch, "E1297", {"start": v(-12.25, 58.82) * mm, "end": v(-12.21, 58.6) * mm});
            skLineSegment(sketch, "E1298", {"start": v(-12.21, 58.6) * mm, "end": v(-12.2, 58.5) * mm});
            skLineSegment(sketch, "E1299", {"start": v(-12.2, 58.5) * mm, "end": v(-12.4, 58.46) * mm});
            skLineSegment(sketch, "E1300", {"start": v(-12.4, 58.46) * mm, "end": v(-12.62, 58.42) * mm});
            skLineSegment(sketch, "E1301", {"start": v(-12.62, 58.42) * mm, "end": v(-12.83, 58.37) * mm});
            skLineSegment(sketch, "E1302", {"start": v(-12.83, 58.37) * mm, "end": v(-13.05, 58.33) * mm});
            skLineSegment(sketch, "E1303", {"start": v(-13.05, 58.33) * mm, "end": v(-13.26, 58.28) * mm});
            skLineSegment(sketch, "E1304", {"start": v(-13.26, 58.28) * mm, "end": v(-13.47, 58.24) * mm});
            skLineSegment(sketch, "E1305", {"start": v(-13.47, 58.24) * mm, "end": v(-13.68, 58.2) * mm});
            skLineSegment(sketch, "E1306", {"start": v(-13.68, 58.2) * mm, "end": v(-13.9, 58.15) * mm});
            skLineSegment(sketch, "E1307", {"start": v(-13.9, 58.15) * mm, "end": v(-14.11, 58.1) * mm});
            skLineSegment(sketch, "E1308", {"start": v(-14.11, 58.1) * mm, "end": v(-14.32, 58.06) * mm});
            skLineSegment(sketch, "E1309", {"start": v(-14.32, 58.06) * mm, "end": v(-14.54, 58.01) * mm});
            skLineSegment(sketch, "E1310", {"start": v(-14.54, 58.01) * mm, "end": v(-14.64, 57.99) * mm});
            skLineSegment(sketch, "E1311", {"start": v(-14.64, 57.99) * mm, "end": v(-14.7, 58.2) * mm});
            skLineSegment(sketch, "E1312", {"start": v(-14.7, 58.2) * mm, "end": v(-14.74, 58.41) * mm});
            skLineSegment(sketch, "E1313", {"start": v(-14.74, 58.41) * mm, "end": v(-14.8, 58.63) * mm});
            skLineSegment(sketch, "E1314", {"start": v(-14.8, 58.63) * mm, "end": v(-14.84, 58.84) * mm});
            skLineSegment(sketch, "E1315", {"start": v(-14.84, 58.84) * mm, "end": v(-14.9, 59.06) * mm});
            skLineSegment(sketch, "E1316", {"start": v(-14.9, 59.06) * mm, "end": v(-14.94, 59.27) * mm});
            skLineSegment(sketch, "E1317", {"start": v(-14.94, 59.27) * mm, "end": v(-15, 59.49) * mm});
            skLineSegment(sketch, "E1318", {"start": v(-15, 59.49) * mm, "end": v(-15.04, 59.7) * mm});
            skLineSegment(sketch, "E1319", {"start": v(-15.04, 59.7) * mm, "end": v(-15.1, 59.92) * mm});
            skLineSegment(sketch, "E1320", {"start": v(-15.1, 59.92) * mm, "end": v(-15.14, 60.13) * mm});
            skLineSegment(sketch, "E1321", {"start": v(-15.14, 60.13) * mm, "end": v(-15.2, 60.34) * mm});
            skLineSegment(sketch, "E1322", {"start": v(-15.2, 60.34) * mm, "end": v(-15.24, 60.56) * mm});
            skLineSegment(sketch, "E1323", {"start": v(-15.24, 60.56) * mm, "end": v(-15.3, 60.79) * mm});
            skLineSegment(sketch, "E1324", {"start": v(-15.3, 60.79) * mm, "end": v(-15.4, 61) * mm});
            skLineSegment(sketch, "E1325", {"start": v(-15.4, 61) * mm, "end": v(-15.54, 61.17) * mm});
            skLineSegment(sketch, "E1326", {"start": v(-15.54, 61.17) * mm, "end": v(-15.72, 61.3) * mm});
            skLineSegment(sketch, "E1327", {"start": v(-15.72, 61.3) * mm, "end": v(-15.93, 61.38) * mm});
            skLineSegment(sketch, "E1328", {"start": v(-15.93, 61.38) * mm, "end": v(-16.11, 61.4) * mm});
            skLineSegment(sketch, "E1329", {"start": v(-16.11, 61.4) * mm, "end": v(-16.34, 61.38) * mm});
            skLineSegment(sketch, "E1330", {"start": v(-16.34, 61.38) * mm, "end": v(-16.55, 61.3) * mm});
            skLineSegment(sketch, "E1331", {"start": v(-16.55, 61.3) * mm, "end": v(-16.73, 61.16) * mm});
            skLineSegment(sketch, "E1332", {"start": v(-16.73, 61.16) * mm, "end": v(-16.87, 60.98) * mm});
            skLineSegment(sketch, "E1333", {"start": v(-16.87, 60.98) * mm, "end": v(-16.96, 60.77) * mm});
            skLineSegment(sketch, "E1334", {"start": v(-16.96, 60.77) * mm, "end": v(-17, 60.55) * mm});
            skLineSegment(sketch, "E1335", {"start": v(-17, 60.55) * mm, "end": v(-16.97, 60.32) * mm});
            skLineSegment(sketch, "E1336", {"start": v(-16.97, 60.32) * mm, "end": v(-16.91, 60.11) * mm});
            skLineSegment(sketch, "E1337", {"start": v(-16.91, 60.11) * mm, "end": v(-16.86, 59.9) * mm});
            skLineSegment(sketch, "E1338", {"start": v(-16.86, 59.9) * mm, "end": v(-16.8, 59.68) * mm});
            skLineSegment(sketch, "E1339", {"start": v(-16.8, 59.68) * mm, "end": v(-16.75, 59.47) * mm});
            skLineSegment(sketch, "E1340", {"start": v(-16.75, 59.47) * mm, "end": v(-16.69, 59.26) * mm});
            skLineSegment(sketch, "E1341", {"start": v(-16.69, 59.26) * mm, "end": v(-16.63, 59.05) * mm});
            skLineSegment(sketch, "E1342", {"start": v(-16.63, 59.05) * mm, "end": v(-16.58, 58.84) * mm});
            skLineSegment(sketch, "E1343", {"start": v(-16.58, 58.84) * mm, "end": v(-16.52, 58.63) * mm});
            skLineSegment(sketch, "E1344", {"start": v(-16.52, 58.63) * mm, "end": v(-16.46, 58.4) * mm});
            skLineSegment(sketch, "E1345", {"start": v(-16.46, 58.4) * mm, "end": v(-16.4, 58.2) * mm});
            skLineSegment(sketch, "E1346", {"start": v(-16.4, 58.2) * mm, "end": v(-16.35, 57.99) * mm});
            skLineSegment(sketch, "E1347", {"start": v(-16.35, 57.99) * mm, "end": v(-16.3, 57.77) * mm});
            skLineSegment(sketch, "E1348", {"start": v(-16.3, 57.77) * mm, "end": v(-16.25, 57.59) * mm});
            skLineSegment(sketch, "E1349", {"start": v(-16.25, 57.59) * mm, "end": v(-16.46, 57.53) * mm});
            skLineSegment(sketch, "E1350", {"start": v(-16.46, 57.53) * mm, "end": v(-16.67, 57.47) * mm});
            skLineSegment(sketch, "E1351", {"start": v(-16.67, 57.47) * mm, "end": v(-16.88, 57.4) * mm});
            skLineSegment(sketch, "E1352", {"start": v(-16.88, 57.4) * mm, "end": v(-17.08, 57.35) * mm});
            skLineSegment(sketch, "E1353", {"start": v(-17.08, 57.35) * mm, "end": v(-17.3, 57.29) * mm});
            skLineSegment(sketch, "E1354", {"start": v(-17.3, 57.29) * mm, "end": v(-17.5, 57.23) * mm});
            skLineSegment(sketch, "E1355", {"start": v(-17.5, 57.23) * mm, "end": v(-17.71, 57.17) * mm});
            skLineSegment(sketch, "E1356", {"start": v(-17.71, 57.17) * mm, "end": v(-17.92, 57.1) * mm});
            skLineSegment(sketch, "E1357", {"start": v(-17.92, 57.1) * mm, "end": v(-18.13, 57.05) * mm});
            skLineSegment(sketch, "E1358", {"start": v(-18.13, 57.05) * mm, "end": v(-18.34, 56.99) * mm});
            skLineSegment(sketch, "E1359", {"start": v(-18.34, 56.99) * mm, "end": v(-18.55, 56.93) * mm});
            skLineSegment(sketch, "E1360", {"start": v(-18.55, 56.93) * mm, "end": v(-18.65, 56.9) * mm});
            skLineSegment(sketch, "E1361", {"start": v(-18.65, 56.9) * mm, "end": v(-18.72, 57.1) * mm});
            skLineSegment(sketch, "E1362", {"start": v(-18.72, 57.1) * mm, "end": v(-18.78, 57.32) * mm});
            skLineSegment(sketch, "E1363", {"start": v(-18.78, 57.32) * mm, "end": v(-18.85, 57.53) * mm});
            skLineSegment(sketch, "E1364", {"start": v(-18.85, 57.53) * mm, "end": v(-18.91, 57.74) * mm});
            skLineSegment(sketch, "E1365", {"start": v(-18.91, 57.74) * mm, "end": v(-18.98, 57.95) * mm});
            skLineSegment(sketch, "E1366", {"start": v(-18.98, 57.95) * mm, "end": v(-19.04, 58.16) * mm});
            skLineSegment(sketch, "E1367", {"start": v(-19.04, 58.16) * mm, "end": v(-19.1, 58.37) * mm});
            skLineSegment(sketch, "E1368", {"start": v(-19.1, 58.37) * mm, "end": v(-19.17, 58.58) * mm});
            skLineSegment(sketch, "E1369", {"start": v(-19.17, 58.58) * mm, "end": v(-19.24, 58.79) * mm});
            skLineSegment(sketch, "E1370", {"start": v(-19.24, 58.79) * mm, "end": v(-19.3, 59) * mm});
            skLineSegment(sketch, "E1371", {"start": v(-19.3, 59) * mm, "end": v(-19.37, 59.2) * mm});
            skLineSegment(sketch, "E1372", {"start": v(-19.37, 59.2) * mm, "end": v(-19.43, 59.42) * mm});
            skLineSegment(sketch, "E1373", {"start": v(-19.43, 59.42) * mm, "end": v(-19.5, 59.64) * mm});
            skLineSegment(sketch, "E1374", {"start": v(-19.5, 59.64) * mm, "end": v(-19.61, 59.84) * mm});
            skLineSegment(sketch, "E1375", {"start": v(-19.61, 59.84) * mm, "end": v(-19.77, 60) * mm});
            skLineSegment(sketch, "E1376", {"start": v(-19.77, 60) * mm, "end": v(-19.96, 60.13) * mm});
            skLineSegment(sketch, "E1377", {"start": v(-19.96, 60.13) * mm, "end": v(-20.18, 60.2) * mm});
            skLineSegment(sketch, "E1378", {"start": v(-20.18, 60.2) * mm, "end": v(-20.31, 60.2) * mm});
            skLineSegment(sketch, "E1379", {"start": v(-20.31, 60.2) * mm, "end": v(-20.54, 60.18) * mm});
            skLineSegment(sketch, "E1380", {"start": v(-20.54, 60.18) * mm, "end": v(-20.75, 60.09) * mm});
            skLineSegment(sketch, "E1381", {"start": v(-20.75, 60.09) * mm, "end": v(-20.93, 59.95) * mm});
            skLineSegment(sketch, "E1382", {"start": v(-20.93, 59.95) * mm, "end": v(-21.07, 59.77) * mm});
            skLineSegment(sketch, "E1383", {"start": v(-21.07, 59.77) * mm, "end": v(-21.15, 59.56) * mm});
            skLineSegment(sketch, "E1384", {"start": v(-21.15, 59.56) * mm, "end": v(-21.18, 59.33) * mm});
            skLineSegment(sketch, "E1385", {"start": v(-21.18, 59.33) * mm, "end": v(-21.15, 59.1) * mm});
            skLineSegment(sketch, "E1386", {"start": v(-21.15, 59.1) * mm, "end": v(-21.08, 58.89) * mm});
            skLineSegment(sketch, "E1387", {"start": v(-21.08, 58.89) * mm, "end": v(-21, 58.68) * mm});
            skLineSegment(sketch, "E1388", {"start": v(-21, 58.68) * mm, "end": v(-20.94, 58.47) * mm});
            skLineSegment(sketch, "E1389", {"start": v(-20.94, 58.47) * mm, "end": v(-20.87, 58.26) * mm});
            skLineSegment(sketch, "E1390", {"start": v(-20.87, 58.26) * mm, "end": v(-20.8, 58.06) * mm});
            skLineSegment(sketch, "E1391", {"start": v(-20.8, 58.06) * mm, "end": v(-20.72, 57.85) * mm});
            skLineSegment(sketch, "E1392", {"start": v(-20.72, 57.85) * mm, "end": v(-20.65, 57.64) * mm});
            skLineSegment(sketch, "E1393", {"start": v(-20.65, 57.64) * mm, "end": v(-20.58, 57.43) * mm});
            skLineSegment(sketch, "E1394", {"start": v(-20.58, 57.43) * mm, "end": v(-20.51, 57.22) * mm});
            skLineSegment(sketch, "E1395", {"start": v(-20.51, 57.22) * mm, "end": v(-20.44, 57.01) * mm});
            skLineSegment(sketch, "E1396", {"start": v(-20.44, 57.01) * mm, "end": v(-20.37, 56.8) * mm});
            skLineSegment(sketch, "E1397", {"start": v(-20.37, 56.8) * mm, "end": v(-20.3, 56.6) * mm});
            skLineSegment(sketch, "E1398", {"start": v(-20.3, 56.6) * mm, "end": v(-20.23, 56.39) * mm});
            skLineSegment(sketch, "E1399", {"start": v(-20.23, 56.39) * mm, "end": v(-20.43, 56.31) * mm});
            skLineSegment(sketch, "E1400", {"start": v(-20.43, 56.31) * mm, "end": v(-20.64, 56.24) * mm});
            skLineSegment(sketch, "E1401", {"start": v(-20.64, 56.24) * mm, "end": v(-20.84, 56.16) * mm});
            skLineSegment(sketch, "E1402", {"start": v(-20.84, 56.16) * mm, "end": v(-21.05, 56.09) * mm});
            skLineSegment(sketch, "E1403", {"start": v(-21.05, 56.09) * mm, "end": v(-21.25, 56.02) * mm});
            skLineSegment(sketch, "E1404", {"start": v(-21.25, 56.02) * mm, "end": v(-21.46, 55.94) * mm});
            skLineSegment(sketch, "E1405", {"start": v(-21.46, 55.94) * mm, "end": v(-21.66, 55.87) * mm});
            skLineSegment(sketch, "E1406", {"start": v(-21.66, 55.87) * mm, "end": v(-21.87, 55.8) * mm});
            skLineSegment(sketch, "E1407", {"start": v(-21.87, 55.8) * mm, "end": v(-22.07, 55.72) * mm});
            skLineSegment(sketch, "E1408", {"start": v(-22.07, 55.72) * mm, "end": v(-22.27, 55.64) * mm});
            skLineSegment(sketch, "E1409", {"start": v(-22.27, 55.64) * mm, "end": v(-22.48, 55.57) * mm});
            skLineSegment(sketch, "E1410", {"start": v(-22.48, 55.57) * mm, "end": v(-22.58, 55.53) * mm});
            skLineSegment(sketch, "E1411", {"start": v(-22.58, 55.53) * mm, "end": v(-22.66, 55.73) * mm});
            skLineSegment(sketch, "E1412", {"start": v(-22.66, 55.73) * mm, "end": v(-22.74, 55.94) * mm});
            skLineSegment(sketch, "E1413", {"start": v(-22.74, 55.94) * mm, "end": v(-22.82, 56.15) * mm});
            skLineSegment(sketch, "E1414", {"start": v(-22.82, 56.15) * mm, "end": v(-22.9, 56.35) * mm});
            skLineSegment(sketch, "E1415", {"start": v(-22.9, 56.35) * mm, "end": v(-22.98, 56.55) * mm});
            skLineSegment(sketch, "E1416", {"start": v(-22.98, 56.55) * mm, "end": v(-23.06, 56.76) * mm});
            skLineSegment(sketch, "E1417", {"start": v(-23.06, 56.76) * mm, "end": v(-23.14, 56.96) * mm});
            skLineSegment(sketch, "E1418", {"start": v(-23.14, 56.96) * mm, "end": v(-23.21, 57.17) * mm});
            skLineSegment(sketch, "E1419", {"start": v(-23.21, 57.17) * mm, "end": v(-23.3, 57.38) * mm});
            skLineSegment(sketch, "E1420", {"start": v(-23.3, 57.38) * mm, "end": v(-23.37, 57.58) * mm});
            skLineSegment(sketch, "E1421", {"start": v(-23.37, 57.58) * mm, "end": v(-23.45, 57.78) * mm});
            skLineSegment(sketch, "E1422", {"start": v(-23.45, 57.78) * mm, "end": v(-23.53, 58) * mm});
            skLineSegment(sketch, "E1423", {"start": v(-23.53, 58) * mm, "end": v(-23.62, 58.2) * mm});
            skLineSegment(sketch, "E1424", {"start": v(-23.62, 58.2) * mm, "end": v(-23.74, 58.4) * mm});
            skLineSegment(sketch, "E1425", {"start": v(-23.74, 58.4) * mm, "end": v(-23.9, 58.56) * mm});
            skLineSegment(sketch, "E1426", {"start": v(-23.9, 58.56) * mm, "end": v(-24.1, 58.66) * mm});
            skLineSegment(sketch, "E1427", {"start": v(-24.1, 58.66) * mm, "end": v(-24.33, 58.71) * mm});
            skLineSegment(sketch, "E1428", {"start": v(-24.33, 58.71) * mm, "end": v(-24.42, 58.72) * mm});
            skLineSegment(sketch, "E1429", {"start": v(-24.42, 58.72) * mm, "end": v(-24.65, 58.68) * mm});
            skLineSegment(sketch, "E1430", {"start": v(-24.65, 58.68) * mm, "end": v(-24.85, 58.6) * mm});
            skLineSegment(sketch, "E1431", {"start": v(-24.85, 58.6) * mm, "end": v(-25.03, 58.45) * mm});
            skLineSegment(sketch, "E1432", {"start": v(-25.03, 58.45) * mm, "end": v(-25.17, 58.27) * mm});
            skLineSegment(sketch, "E1433", {"start": v(-25.17, 58.27) * mm, "end": v(-25.25, 58.05) * mm});
            skLineSegment(sketch, "E1434", {"start": v(-25.25, 58.05) * mm, "end": v(-25.27, 57.83) * mm});
            skLineSegment(sketch, "E1435", {"start": v(-25.27, 57.83) * mm, "end": v(-25.24, 57.6) * mm});
            skLineSegment(sketch, "E1436", {"start": v(-25.24, 57.6) * mm, "end": v(-25.16, 57.4) * mm});
            skLineSegment(sketch, "E1437", {"start": v(-25.16, 57.4) * mm, "end": v(-25.08, 57.2) * mm});
            skLineSegment(sketch, "E1438", {"start": v(-25.08, 57.2) * mm, "end": v(-25, 57) * mm});
            skLineSegment(sketch, "E1439", {"start": v(-25, 57) * mm, "end": v(-24.9, 56.8) * mm});
            skLineSegment(sketch, "E1440", {"start": v(-24.9, 56.8) * mm, "end": v(-24.82, 56.6) * mm});
            skLineSegment(sketch, "E1441", {"start": v(-24.82, 56.6) * mm, "end": v(-24.73, 56.39) * mm});
            skLineSegment(sketch, "E1442", {"start": v(-24.73, 56.39) * mm, "end": v(-24.65, 56.19) * mm});
            skLineSegment(sketch, "E1443", {"start": v(-24.65, 56.19) * mm, "end": v(-24.57, 55.99) * mm});
            skLineSegment(sketch, "E1444", {"start": v(-24.57, 55.99) * mm, "end": v(-24.48, 55.78) * mm});
            skLineSegment(sketch, "E1445", {"start": v(-24.48, 55.78) * mm, "end": v(-24.4, 55.58) * mm});
            skLineSegment(sketch, "E1446", {"start": v(-24.4, 55.58) * mm, "end": v(-24.31, 55.38) * mm});
            skLineSegment(sketch, "E1447", {"start": v(-24.31, 55.38) * mm, "end": v(-24.22, 55.17) * mm});
            skLineSegment(sketch, "E1448", {"start": v(-24.22, 55.17) * mm, "end": v(-24.14, 54.97) * mm});
            skLineSegment(sketch, "E1449", {"start": v(-24.14, 54.97) * mm, "end": v(-24.11, 54.91) * mm});
            skLineSegment(sketch, "E1450", {"start": v(-24.11, 54.91) * mm, "end": v(-24.31, 54.82) * mm});
            skLineSegment(sketch, "E1451", {"start": v(-24.31, 54.82) * mm, "end": v(-24.51, 54.73) * mm});
            skLineSegment(sketch, "E1452", {"start": v(-24.51, 54.73) * mm, "end": v(-24.71, 54.65) * mm});
            skLineSegment(sketch, "E1453", {"start": v(-24.71, 54.65) * mm, "end": v(-24.91, 54.56) * mm});
            skLineSegment(sketch, "E1454", {"start": v(-24.91, 54.56) * mm, "end": v(-25.1, 54.47) * mm});
            skLineSegment(sketch, "E1455", {"start": v(-25.1, 54.47) * mm, "end": v(-25.3, 54.38) * mm});
            skLineSegment(sketch, "E1456", {"start": v(-25.3, 54.38) * mm, "end": v(-25.5, 54.3) * mm});
            skLineSegment(sketch, "E1457", {"start": v(-25.5, 54.3) * mm, "end": v(-25.7, 54.2) * mm});
            skLineSegment(sketch, "E1458", {"start": v(-25.7, 54.2) * mm, "end": v(-25.9, 54.11) * mm});
            skLineSegment(sketch, "E1459", {"start": v(-25.9, 54.11) * mm, "end": v(-26.1, 54.03) * mm});
            skLineSegment(sketch, "E1460", {"start": v(-26.1, 54.03) * mm, "end": v(-26.3, 53.94) * mm});
            skLineSegment(sketch, "E1461", {"start": v(-26.3, 53.94) * mm, "end": v(-26.4, 53.9) * mm});
            skLineSegment(sketch, "E1462", {"start": v(-26.4, 53.9) * mm, "end": v(-26.5, 54.1) * mm});
            skLineSegment(sketch, "E1463", {"start": v(-26.5, 54.1) * mm, "end": v(-26.59, 54.29) * mm});
            skLineSegment(sketch, "E1464", {"start": v(-26.59, 54.29) * mm, "end": v(-26.68, 54.5) * mm});
            skLineSegment(sketch, "E1465", {"start": v(-26.68, 54.5) * mm, "end": v(-26.77, 54.69) * mm});
            skLineSegment(sketch, "E1466", {"start": v(-26.77, 54.69) * mm, "end": v(-26.87, 54.88) * mm});
            skLineSegment(sketch, "E1467", {"start": v(-26.87, 54.88) * mm, "end": v(-26.96, 55.09) * mm});
            skLineSegment(sketch, "E1468", {"start": v(-26.96, 55.09) * mm, "end": v(-27.06, 55.28) * mm});
            skLineSegment(sketch, "E1469", {"start": v(-27.06, 55.28) * mm, "end": v(-27.15, 55.48) * mm});
            skLineSegment(sketch, "E1470", {"start": v(-27.15, 55.48) * mm, "end": v(-27.24, 55.68) * mm});
            skLineSegment(sketch, "E1471", {"start": v(-27.24, 55.68) * mm, "end": v(-27.34, 55.88) * mm});
            skLineSegment(sketch, "E1472", {"start": v(-27.34, 55.88) * mm, "end": v(-27.43, 56.08) * mm});
            skLineSegment(sketch, "E1473", {"start": v(-27.43, 56.08) * mm, "end": v(-27.52, 56.28) * mm});
            skLineSegment(sketch, "E1474", {"start": v(-27.52, 56.28) * mm, "end": v(-27.63, 56.5) * mm});
            skLineSegment(sketch, "E1475", {"start": v(-27.63, 56.5) * mm, "end": v(-27.76, 56.68) * mm});
            skLineSegment(sketch, "E1476", {"start": v(-27.76, 56.68) * mm, "end": v(-27.94, 56.82) * mm});
            skLineSegment(sketch, "E1477", {"start": v(-27.94, 56.82) * mm, "end": v(-28.14, 56.9) * mm});
            skLineSegment(sketch, "E1478", {"start": v(-28.14, 56.9) * mm, "end": v(-28.37, 56.94) * mm});
            skLineSegment(sketch, "E1479", {"start": v(-28.37, 56.94) * mm, "end": v(-28.6, 56.92) * mm});
            skLineSegment(sketch, "E1480", {"start": v(-28.6, 56.92) * mm, "end": v(-28.8, 56.84) * mm});
            skLineSegment(sketch, "E1481", {"start": v(-28.8, 56.84) * mm, "end": v(-28.99, 56.7) * mm});
            skLineSegment(sketch, "E1482", {"start": v(-28.99, 56.7) * mm, "end": v(-29.13, 56.52) * mm});
            skLineSegment(sketch, "E1483", {"start": v(-29.13, 56.52) * mm, "end": v(-29.22, 56.31) * mm});
            skLineSegment(sketch, "E1484", {"start": v(-29.22, 56.31) * mm, "end": v(-29.25, 56.09) * mm});
            skLineSegment(sketch, "E1485", {"start": v(-29.25, 56.09) * mm, "end": v(-29.23, 55.86) * mm});
            skLineSegment(sketch, "E1486", {"start": v(-29.23, 55.86) * mm, "end": v(-29.14, 55.66) * mm});
            skLineSegment(sketch, "E1487", {"start": v(-29.14, 55.66) * mm, "end": v(-29.05, 55.47) * mm});
            skLineSegment(sketch, "E1488", {"start": v(-29.05, 55.47) * mm, "end": v(-28.95, 55.27) * mm});
            skLineSegment(sketch, "E1489", {"start": v(-28.95, 55.27) * mm, "end": v(-28.85, 55.08) * mm});
            skLineSegment(sketch, "E1490", {"start": v(-28.85, 55.08) * mm, "end": v(-28.75, 54.88) * mm});
            skLineSegment(sketch, "E1491", {"start": v(-28.75, 54.88) * mm, "end": v(-28.65, 54.68) * mm});
            skLineSegment(sketch, "E1492", {"start": v(-28.65, 54.68) * mm, "end": v(-28.55, 54.49) * mm});
            skLineSegment(sketch, "E1493", {"start": v(-28.55, 54.49) * mm, "end": v(-28.46, 54.3) * mm});
            skLineSegment(sketch, "E1494", {"start": v(-28.46, 54.3) * mm, "end": v(-28.36, 54.1) * mm});
            skLineSegment(sketch, "E1495", {"start": v(-28.36, 54.1) * mm, "end": v(-28.26, 53.9) * mm});
            skLineSegment(sketch, "E1496", {"start": v(-28.26, 53.9) * mm, "end": v(-28.16, 53.7) * mm});
            skLineSegment(sketch, "E1497", {"start": v(-28.16, 53.7) * mm, "end": v(-28.06, 53.5) * mm});
            skLineSegment(sketch, "E1498", {"start": v(-28.06, 53.5) * mm, "end": v(-27.96, 53.3) * mm});
            skLineSegment(sketch, "E1499", {"start": v(-27.96, 53.3) * mm, "end": v(-27.89, 53.17) * mm});
            skLineSegment(sketch, "E1500", {"start": v(-27.89, 53.17) * mm, "end": v(-28.08, 53.07) * mm});
            skLineSegment(sketch, "E1501", {"start": v(-28.08, 53.07) * mm, "end": v(-28.27, 52.96) * mm});
            skLineSegment(sketch, "E1502", {"start": v(-28.27, 52.96) * mm, "end": v(-28.47, 52.86) * mm});
            skLineSegment(sketch, "E1503", {"start": v(-28.47, 52.86) * mm, "end": v(-28.66, 52.76) * mm});
            skLineSegment(sketch, "E1504", {"start": v(-28.66, 52.76) * mm, "end": v(-28.85, 52.66) * mm});
            skLineSegment(sketch, "E1505", {"start": v(-28.85, 52.66) * mm, "end": v(-29.04, 52.55) * mm});
            skLineSegment(sketch, "E1506", {"start": v(-29.04, 52.55) * mm, "end": v(-29.23, 52.45) * mm});
            skLineSegment(sketch, "E1507", {"start": v(-29.23, 52.45) * mm, "end": v(-29.43, 52.35) * mm});
            skLineSegment(sketch, "E1508", {"start": v(-29.43, 52.35) * mm, "end": v(-29.62, 52.25) * mm});
            skLineSegment(sketch, "E1509", {"start": v(-29.62, 52.25) * mm, "end": v(-29.81, 52.15) * mm});
            skLineSegment(sketch, "E1510", {"start": v(-29.81, 52.15) * mm, "end": v(-30, 52.04) * mm});
            skLineSegment(sketch, "E1511", {"start": v(-30, 52.04) * mm, "end": v(-30.1, 52) * mm});
            skLineSegment(sketch, "E1512", {"start": v(-30.1, 52) * mm, "end": v(-30.2, 52.18) * mm});
            skLineSegment(sketch, "E1513", {"start": v(-30.2, 52.18) * mm, "end": v(-30.31, 52.37) * mm});
            skLineSegment(sketch, "E1514", {"start": v(-30.31, 52.37) * mm, "end": v(-30.42, 52.57) * mm});
            skLineSegment(sketch, "E1515", {"start": v(-30.42, 52.57) * mm, "end": v(-30.53, 52.76) * mm});
            skLineSegment(sketch, "E1516", {"start": v(-30.53, 52.76) * mm, "end": v(-30.63, 52.95) * mm});
            skLineSegment(sketch, "E1517", {"start": v(-30.63, 52.95) * mm, "end": v(-30.74, 53.14) * mm});
            skLineSegment(sketch, "E1518", {"start": v(-30.74, 53.14) * mm, "end": v(-30.85, 53.33) * mm});
            skLineSegment(sketch, "E1519", {"start": v(-30.85, 53.33) * mm, "end": v(-30.95, 53.53) * mm});
            skLineSegment(sketch, "E1520", {"start": v(-30.95, 53.53) * mm, "end": v(-31.06, 53.72) * mm});
            skLineSegment(sketch, "E1521", {"start": v(-31.06, 53.72) * mm, "end": v(-31.17, 53.91) * mm});
            skLineSegment(sketch, "E1522", {"start": v(-31.17, 53.91) * mm, "end": v(-31.28, 54.1) * mm});
            skLineSegment(sketch, "E1523", {"start": v(-31.28, 54.1) * mm, "end": v(-31.39, 54.3) * mm});
            skLineSegment(sketch, "E1524", {"start": v(-31.39, 54.3) * mm, "end": v(-31.5, 54.5) * mm});
            skLineSegment(sketch, "E1525", {"start": v(-31.5, 54.5) * mm, "end": v(-31.65, 54.67) * mm});
            skLineSegment(sketch, "E1526", {"start": v(-31.65, 54.67) * mm, "end": v(-31.83, 54.8) * mm});
            skLineSegment(sketch, "E1527", {"start": v(-31.83, 54.8) * mm, "end": v(-32.05, 54.88) * mm});
            skLineSegment(sketch, "E1528", {"start": v(-32.05, 54.88) * mm, "end": v(-32.23, 54.9) * mm});
            skLineSegment(sketch, "E1529", {"start": v(-32.23, 54.9) * mm, "end": v(-32.45, 54.87) * mm});
            skLineSegment(sketch, "E1530", {"start": v(-32.45, 54.87) * mm, "end": v(-32.66, 54.78) * mm});
            skLineSegment(sketch, "E1531", {"start": v(-32.66, 54.78) * mm, "end": v(-32.85, 54.64) * mm});
            skLineSegment(sketch, "E1532", {"start": v(-32.85, 54.64) * mm, "end": v(-32.98, 54.46) * mm});
            skLineSegment(sketch, "E1533", {"start": v(-32.98, 54.46) * mm, "end": v(-33.07, 54.25) * mm});
            skLineSegment(sketch, "E1534", {"start": v(-33.07, 54.25) * mm, "end": v(-33.1, 54.03) * mm});
            skLineSegment(sketch, "E1535", {"start": v(-33.1, 54.03) * mm, "end": v(-33.07, 53.8) * mm});
            skLineSegment(sketch, "E1536", {"start": v(-33.07, 53.8) * mm, "end": v(-32.98, 53.6) * mm});
            skLineSegment(sketch, "E1537", {"start": v(-32.98, 53.6) * mm, "end": v(-32.87, 53.4) * mm});
            skLineSegment(sketch, "E1538", {"start": v(-32.87, 53.4) * mm, "end": v(-32.76, 53.22) * mm});
            skLineSegment(sketch, "E1539", {"start": v(-32.76, 53.22) * mm, "end": v(-32.64, 53.03) * mm});
            skLineSegment(sketch, "E1540", {"start": v(-32.64, 53.03) * mm, "end": v(-32.53, 52.84) * mm});
            skLineSegment(sketch, "E1541", {"start": v(-32.53, 52.84) * mm, "end": v(-32.42, 52.65) * mm});
            skLineSegment(sketch, "E1542", {"start": v(-32.42, 52.65) * mm, "end": v(-32.3, 52.46) * mm});
            skLineSegment(sketch, "E1543", {"start": v(-32.3, 52.46) * mm, "end": v(-32.2, 52.27) * mm});
            skLineSegment(sketch, "E1544", {"start": v(-32.2, 52.27) * mm, "end": v(-32.08, 52.09) * mm});
            skLineSegment(sketch, "E1545", {"start": v(-32.08, 52.09) * mm, "end": v(-31.97, 51.9) * mm});
            skLineSegment(sketch, "E1546", {"start": v(-31.97, 51.9) * mm, "end": v(-31.85, 51.7) * mm});
            skLineSegment(sketch, "E1547", {"start": v(-31.85, 51.7) * mm, "end": v(-31.74, 51.52) * mm});
            skLineSegment(sketch, "E1548", {"start": v(-31.74, 51.52) * mm, "end": v(-31.63, 51.33) * mm});
            skLineSegment(sketch, "E1549", {"start": v(-31.63, 51.33) * mm, "end": v(-31.53, 51.17) * mm});
            skLineSegment(sketch, "E1550", {"start": v(-31.53, 51.17) * mm, "end": v(-31.72, 51.05) * mm});
            skLineSegment(sketch, "E1551", {"start": v(-31.72, 51.05) * mm, "end": v(-31.9, 50.93) * mm});
            skLineSegment(sketch, "E1552", {"start": v(-31.9, 50.93) * mm, "end": v(-32.09, 50.82) * mm});
            skLineSegment(sketch, "E1553", {"start": v(-32.09, 50.82) * mm, "end": v(-32.27, 50.7) * mm});
            skLineSegment(sketch, "E1554", {"start": v(-32.27, 50.7) * mm, "end": v(-32.46, 50.59) * mm});
            skLineSegment(sketch, "E1555", {"start": v(-32.46, 50.59) * mm, "end": v(-32.64, 50.47) * mm});
            skLineSegment(sketch, "E1556", {"start": v(-32.64, 50.47) * mm, "end": v(-32.82, 50.36) * mm});
            skLineSegment(sketch, "E1557", {"start": v(-32.82, 50.36) * mm, "end": v(-33, 50.24) * mm});
            skLineSegment(sketch, "E1558", {"start": v(-33, 50.24) * mm, "end": v(-33.2, 50.13) * mm});
            skLineSegment(sketch, "E1559", {"start": v(-33.2, 50.13) * mm, "end": v(-33.38, 50.01) * mm});
            skLineSegment(sketch, "E1560", {"start": v(-33.38, 50.01) * mm, "end": v(-33.56, 49.9) * mm});
            skLineSegment(sketch, "E1561", {"start": v(-33.56, 49.9) * mm, "end": v(-33.65, 49.84) * mm});
            skLineSegment(sketch, "E1562", {"start": v(-33.65, 49.84) * mm, "end": v(-33.77, 50.02) * mm});
            skLineSegment(sketch, "E1563", {"start": v(-33.77, 50.02) * mm, "end": v(-33.9, 50.2) * mm});
            skLineSegment(sketch, "E1564", {"start": v(-33.9, 50.2) * mm, "end": v(-34.02, 50.4) * mm});
            skLineSegment(sketch, "E1565", {"start": v(-34.02, 50.4) * mm, "end": v(-34.13, 50.57) * mm});
            skLineSegment(sketch, "E1566", {"start": v(-34.13, 50.57) * mm, "end": v(-34.25, 50.76) * mm});
            skLineSegment(sketch, "E1567", {"start": v(-34.25, 50.76) * mm, "end": v(-34.38, 50.94) * mm});
            skLineSegment(sketch, "E1568", {"start": v(-34.38, 50.94) * mm, "end": v(-34.5, 51.13) * mm});
            skLineSegment(sketch, "E1569", {"start": v(-34.5, 51.13) * mm, "end": v(-34.62, 51.3) * mm});
            skLineSegment(sketch, "E1570", {"start": v(-34.62, 51.3) * mm, "end": v(-34.74, 51.5) * mm});
            skLineSegment(sketch, "E1571", {"start": v(-34.74, 51.5) * mm, "end": v(-34.86, 51.68) * mm});
            skLineSegment(sketch, "E1572", {"start": v(-34.86, 51.68) * mm, "end": v(-34.98, 51.86) * mm});
            skLineSegment(sketch, "E1573", {"start": v(-34.98, 51.86) * mm, "end": v(-35.1, 52.05) * mm});
            skLineSegment(sketch, "E1574", {"start": v(-35.1, 52.05) * mm, "end": v(-35.23, 52.24) * mm});
            skLineSegment(sketch, "E1575", {"start": v(-35.23, 52.24) * mm, "end": v(-35.39, 52.4) * mm});
            skLineSegment(sketch, "E1576", {"start": v(-35.39, 52.4) * mm, "end": v(-35.58, 52.52) * mm});
            skLineSegment(sketch, "E1577", {"start": v(-35.58, 52.52) * mm, "end": v(-35.8, 52.58) * mm});
            skLineSegment(sketch, "E1578", {"start": v(-35.8, 52.58) * mm, "end": v(-35.94, 52.6) * mm});
            skLineSegment(sketch, "E1579", {"start": v(-35.94, 52.6) * mm, "end": v(-36.16, 52.56) * mm});
            skLineSegment(sketch, "E1580", {"start": v(-36.16, 52.56) * mm, "end": v(-36.37, 52.47) * mm});
            skLineSegment(sketch, "E1581", {"start": v(-36.37, 52.47) * mm, "end": v(-36.55, 52.33) * mm});
            skLineSegment(sketch, "E1582", {"start": v(-36.55, 52.33) * mm, "end": v(-36.68, 52.14) * mm});
            skLineSegment(sketch, "E1583", {"start": v(-36.68, 52.14) * mm, "end": v(-36.77, 51.93) * mm});
            skLineSegment(sketch, "E1584", {"start": v(-36.77, 51.93) * mm, "end": v(-36.8, 51.7) * mm});
            skLineSegment(sketch, "E1585", {"start": v(-36.8, 51.7) * mm, "end": v(-36.76, 51.48) * mm});
            skLineSegment(sketch, "E1586", {"start": v(-36.76, 51.48) * mm, "end": v(-36.66, 51.27) * mm});
            skLineSegment(sketch, "E1587", {"start": v(-36.66, 51.27) * mm, "end": v(-36.53, 51.08) * mm});
            skLineSegment(sketch, "E1588", {"start": v(-36.53, 51.08) * mm, "end": v(-36.4, 50.9) * mm});
            skLineSegment(sketch, "E1589", {"start": v(-36.4, 50.9) * mm, "end": v(-36.28, 50.72) * mm});
            skLineSegment(sketch, "E1590", {"start": v(-36.28, 50.72) * mm, "end": v(-36.16, 50.54) * mm});
            skLineSegment(sketch, "E1591", {"start": v(-36.16, 50.54) * mm, "end": v(-36.03, 50.36) * mm});
            skLineSegment(sketch, "E1592", {"start": v(-36.03, 50.36) * mm, "end": v(-35.9, 50.18) * mm});
            skLineSegment(sketch, "E1593", {"start": v(-35.9, 50.18) * mm, "end": v(-35.78, 50) * mm});
            skLineSegment(sketch, "E1594", {"start": v(-35.78, 50) * mm, "end": v(-35.66, 49.82) * mm});
            skLineSegment(sketch, "E1595", {"start": v(-35.66, 49.82) * mm, "end": v(-35.53, 49.64) * mm});
            skLineSegment(sketch, "E1596", {"start": v(-35.53, 49.64) * mm, "end": v(-35.4, 49.46) * mm});
            skLineSegment(sketch, "E1597", {"start": v(-35.4, 49.46) * mm, "end": v(-35.28, 49.28) * mm});
            skLineSegment(sketch, "E1598", {"start": v(-35.28, 49.28) * mm, "end": v(-35.15, 49.1) * mm});
            skLineSegment(sketch, "E1599", {"start": v(-35.15, 49.1) * mm, "end": v(-35.03, 48.91) * mm});
            skLineSegment(sketch, "E1600", {"start": v(-35.03, 48.91) * mm, "end": v(-35.2, 48.79) * mm});
            skLineSegment(sketch, "E1601", {"start": v(-35.2, 48.79) * mm, "end": v(-35.38, 48.66) * mm});
            skLineSegment(sketch, "E1602", {"start": v(-35.38, 48.66) * mm, "end": v(-35.56, 48.53) * mm});
            skLineSegment(sketch, "E1603", {"start": v(-35.56, 48.53) * mm, "end": v(-35.73, 48.4) * mm});
            skLineSegment(sketch, "E1604", {"start": v(-35.73, 48.4) * mm, "end": v(-35.9, 48.27) * mm});
            skLineSegment(sketch, "E1605", {"start": v(-35.9, 48.27) * mm, "end": v(-36.08, 48.14) * mm});
            skLineSegment(sketch, "E1606", {"start": v(-36.08, 48.14) * mm, "end": v(-36.26, 48.02) * mm});
            skLineSegment(sketch, "E1607", {"start": v(-36.26, 48.02) * mm, "end": v(-36.44, 47.89) * mm});
            skLineSegment(sketch, "E1608", {"start": v(-36.44, 47.89) * mm, "end": v(-36.61, 47.76) * mm});
            skLineSegment(sketch, "E1609", {"start": v(-36.61, 47.76) * mm, "end": v(-36.79, 47.63) * mm});
            skLineSegment(sketch, "E1610", {"start": v(-36.79, 47.63) * mm, "end": v(-36.97, 47.5) * mm});
            skLineSegment(sketch, "E1611", {"start": v(-36.97, 47.5) * mm, "end": v(-37.05, 47.44) * mm});
            skLineSegment(sketch, "E1612", {"start": v(-37.05, 47.44) * mm, "end": v(-37.18, 47.62) * mm});
            skLineSegment(sketch, "E1613", {"start": v(-37.18, 47.62) * mm, "end": v(-37.31, 47.79) * mm});
            skLineSegment(sketch, "E1614", {"start": v(-37.31, 47.79) * mm, "end": v(-37.45, 47.97) * mm});
            skLineSegment(sketch, "E1615", {"start": v(-37.45, 47.97) * mm, "end": v(-37.58, 48.14) * mm});
            skLineSegment(sketch, "E1616", {"start": v(-37.58, 48.14) * mm, "end": v(-37.71, 48.31) * mm});
            skLineSegment(sketch, "E1617", {"start": v(-37.71, 48.31) * mm, "end": v(-37.85, 48.5) * mm});
            skLineSegment(sketch, "E1618", {"start": v(-37.85, 48.5) * mm, "end": v(-37.98, 48.67) * mm});
            skLineSegment(sketch, "E1619", {"start": v(-37.98, 48.67) * mm, "end": v(-38.11, 48.84) * mm});
            skLineSegment(sketch, "E1620", {"start": v(-38.11, 48.84) * mm, "end": v(-38.25, 49.02) * mm});
            skLineSegment(sketch, "E1621", {"start": v(-38.25, 49.02) * mm, "end": v(-38.38, 49.2) * mm});
            skLineSegment(sketch, "E1622", {"start": v(-38.38, 49.2) * mm, "end": v(-38.51, 49.37) * mm});
            skLineSegment(sketch, "E1623", {"start": v(-38.51, 49.37) * mm, "end": v(-38.65, 49.54) * mm});
            skLineSegment(sketch, "E1624", {"start": v(-38.65, 49.54) * mm, "end": v(-38.79, 49.73) * mm});
            skLineSegment(sketch, "E1625", {"start": v(-38.79, 49.73) * mm, "end": v(-38.96, 49.88) * mm});
            skLineSegment(sketch, "E1626", {"start": v(-38.96, 49.88) * mm, "end": v(-39.16, 49.98) * mm});
            skLineSegment(sketch, "E1627", {"start": v(-39.16, 49.98) * mm, "end": v(-39.38, 50.03) * mm});
            skLineSegment(sketch, "E1628", {"start": v(-39.38, 50.03) * mm, "end": v(-39.43, 50.03) * mm});
            skLineSegment(sketch, "E1629", {"start": v(-39.43, 50.03) * mm, "end": v(-39.66, 50) * mm});
            skLineSegment(sketch, "E1630", {"start": v(-39.66, 50) * mm, "end": v(-39.87, 49.92) * mm});
            skLineSegment(sketch, "E1631", {"start": v(-39.87, 49.92) * mm, "end": v(-40.05, 49.79) * mm});
            skLineSegment(sketch, "E1632", {"start": v(-40.05, 49.79) * mm, "end": v(-40.2, 49.61) * mm});
            skLineSegment(sketch, "E1633", {"start": v(-40.2, 49.61) * mm, "end": v(-40.28, 49.4) * mm});
            skLineSegment(sketch, "E1634", {"start": v(-40.28, 49.4) * mm, "end": v(-40.31, 49.18) * mm});
            skLineSegment(sketch, "E1635", {"start": v(-40.31, 49.18) * mm, "end": v(-40.29, 48.95) * mm});
            skLineSegment(sketch, "E1636", {"start": v(-40.29, 48.95) * mm, "end": v(-40.2, 48.74) * mm});
            skLineSegment(sketch, "E1637", {"start": v(-40.2, 48.74) * mm, "end": v(-40.07, 48.55) * mm});
            skLineSegment(sketch, "E1638", {"start": v(-40.07, 48.55) * mm, "end": v(-39.93, 48.38) * mm});
            skLineSegment(sketch, "E1639", {"start": v(-39.93, 48.38) * mm, "end": v(-39.8, 48.21) * mm});
            skLineSegment(sketch, "E1640", {"start": v(-39.8, 48.21) * mm, "end": v(-39.65, 48.04) * mm});
            skLineSegment(sketch, "E1641", {"start": v(-39.65, 48.04) * mm, "end": v(-39.52, 47.87) * mm});
            skLineSegment(sketch, "E1642", {"start": v(-39.52, 47.87) * mm, "end": v(-39.38, 47.7) * mm});
            skLineSegment(sketch, "E1643", {"start": v(-39.38, 47.7) * mm, "end": v(-39.24, 47.52) * mm});
            skLineSegment(sketch, "E1644", {"start": v(-39.24, 47.52) * mm, "end": v(-39.1, 47.36) * mm});
            skLineSegment(sketch, "E1645", {"start": v(-39.1, 47.36) * mm, "end": v(-38.97, 47.19) * mm});
            skLineSegment(sketch, "E1646", {"start": v(-38.97, 47.19) * mm, "end": v(-38.83, 47.01) * mm});
            skLineSegment(sketch, "E1647", {"start": v(-38.83, 47.01) * mm, "end": v(-38.7, 46.84) * mm});
            skLineSegment(sketch, "E1648", {"start": v(-38.7, 46.84) * mm, "end": v(-38.56, 46.67) * mm});
            skLineSegment(sketch, "E1649", {"start": v(-38.56, 46.67) * mm, "end": v(-38.41, 46.5) * mm});
            skLineSegment(sketch, "E1650", {"start": v(-38.41, 46.5) * mm, "end": v(-38.36, 46.42) * mm});
            skLineSegment(sketch, "E1651", {"start": v(-38.36, 46.42) * mm, "end": v(-38.52, 46.28) * mm});
            skLineSegment(sketch, "E1652", {"start": v(-38.52, 46.28) * mm, "end": v(-38.69, 46.14) * mm});
            skLineSegment(sketch, "E1653", {"start": v(-38.69, 46.14) * mm, "end": v(-38.86, 46) * mm});
            skLineSegment(sketch, "E1654", {"start": v(-38.86, 46) * mm, "end": v(-39.02, 45.86) * mm});
            skLineSegment(sketch, "E1655", {"start": v(-39.02, 45.86) * mm, "end": v(-39.2, 45.72) * mm});
            skLineSegment(sketch, "E1656", {"start": v(-39.2, 45.72) * mm, "end": v(-39.36, 45.58) * mm});
            skLineSegment(sketch, "E1657", {"start": v(-39.36, 45.58) * mm, "end": v(-39.52, 45.44) * mm});
            skLineSegment(sketch, "E1658", {"start": v(-39.52, 45.44) * mm, "end": v(-39.7, 45.3) * mm});
            skLineSegment(sketch, "E1659", {"start": v(-39.7, 45.3) * mm, "end": v(-39.86, 45.16) * mm});
            skLineSegment(sketch, "E1660", {"start": v(-39.86, 45.16) * mm, "end": v(-40.02, 45.02) * mm});
            skLineSegment(sketch, "E1661", {"start": v(-40.02, 45.02) * mm, "end": v(-40.2, 44.88) * mm});
            skLineSegment(sketch, "E1662", {"start": v(-40.2, 44.88) * mm, "end": v(-40.27, 44.81) * mm});
            skLineSegment(sketch, "E1663", {"start": v(-40.27, 44.81) * mm, "end": v(-40.42, 44.98) * mm});
            skLineSegment(sketch, "E1664", {"start": v(-40.42, 44.98) * mm, "end": v(-40.56, 45.14) * mm});
            skLineSegment(sketch, "E1665", {"start": v(-40.56, 45.14) * mm, "end": v(-40.7, 45.31) * mm});
            skLineSegment(sketch, "E1666", {"start": v(-40.7, 45.31) * mm, "end": v(-40.85, 45.47) * mm});
            skLineSegment(sketch, "E1667", {"start": v(-40.85, 45.47) * mm, "end": v(-41, 45.64) * mm});
            skLineSegment(sketch, "E1668", {"start": v(-41, 45.64) * mm, "end": v(-41.14, 45.8) * mm});
            skLineSegment(sketch, "E1669", {"start": v(-41.14, 45.8) * mm, "end": v(-41.29, 45.97) * mm});
            skLineSegment(sketch, "E1670", {"start": v(-41.29, 45.97) * mm, "end": v(-41.43, 46.13) * mm});
            skLineSegment(sketch, "E1671", {"start": v(-41.43, 46.13) * mm, "end": v(-41.58, 46.3) * mm});
            skLineSegment(sketch, "E1672", {"start": v(-41.58, 46.3) * mm, "end": v(-41.72, 46.47) * mm});
            skLineSegment(sketch, "E1673", {"start": v(-41.72, 46.47) * mm, "end": v(-41.86, 46.63) * mm});
            skLineSegment(sketch, "E1674", {"start": v(-41.86, 46.63) * mm, "end": v(-42.01, 46.8) * mm});
            skLineSegment(sketch, "E1675", {"start": v(-42.01, 46.8) * mm, "end": v(-42.17, 46.98) * mm});
            skLineSegment(sketch, "E1676", {"start": v(-42.17, 46.98) * mm, "end": v(-42.35, 47.11) * mm});
            skLineSegment(sketch, "E1677", {"start": v(-42.35, 47.11) * mm, "end": v(-42.56, 47.2) * mm});
            skLineSegment(sketch, "E1678", {"start": v(-42.56, 47.2) * mm, "end": v(-42.78, 47.23) * mm});
            skLineSegment(sketch, "E1679", {"start": v(-42.78, 47.23) * mm, "end": v(-43, 47.2) * mm});
            skLineSegment(sketch, "E1680", {"start": v(-43, 47.2) * mm, "end": v(-43.22, 47.12) * mm});
            skLineSegment(sketch, "E1681", {"start": v(-43.22, 47.12) * mm, "end": v(-43.4, 46.98) * mm});
            skLineSegment(sketch, "E1682", {"start": v(-43.4, 46.98) * mm, "end": v(-43.54, 46.8) * mm});
            skLineSegment(sketch, "E1683", {"start": v(-43.54, 46.8) * mm, "end": v(-43.62, 46.59) * mm});
            skLineSegment(sketch, "E1684", {"start": v(-43.62, 46.59) * mm, "end": v(-43.65, 46.36) * mm});
            skLineSegment(sketch, "E1685", {"start": v(-43.65, 46.36) * mm, "end": v(-43.62, 46.14) * mm});
            skLineSegment(sketch, "E1686", {"start": v(-43.62, 46.14) * mm, "end": v(-43.53, 45.93) * mm});
            skLineSegment(sketch, "E1687", {"start": v(-43.53, 45.93) * mm, "end": v(-43.4, 45.76) * mm});
            skLineSegment(sketch, "E1688", {"start": v(-43.4, 45.76) * mm, "end": v(-43.25, 45.6) * mm});
            skLineSegment(sketch, "E1689", {"start": v(-43.25, 45.6) * mm, "end": v(-43.1, 45.44) * mm});
            skLineSegment(sketch, "E1690", {"start": v(-43.1, 45.44) * mm, "end": v(-42.96, 45.28) * mm});
            skLineSegment(sketch, "E1691", {"start": v(-42.96, 45.28) * mm, "end": v(-42.8, 45.12) * mm});
            skLineSegment(sketch, "E1692", {"start": v(-42.8, 45.12) * mm, "end": v(-42.66, 44.95) * mm});
            skLineSegment(sketch, "E1693", {"start": v(-42.66, 44.95) * mm, "end": v(-42.5, 44.8) * mm});
            skLineSegment(sketch, "E1694", {"start": v(-42.5, 44.8) * mm, "end": v(-42.36, 44.63) * mm});
            skLineSegment(sketch, "E1695", {"start": v(-42.36, 44.63) * mm, "end": v(-42.2, 44.47) * mm});
            skLineSegment(sketch, "E1696", {"start": v(-42.2, 44.47) * mm, "end": v(-42.06, 44.3) * mm});
            skLineSegment(sketch, "E1697", {"start": v(-42.06, 44.3) * mm, "end": v(-41.91, 44.15) * mm});
            skLineSegment(sketch, "E1698", {"start": v(-41.91, 44.15) * mm, "end": v(-41.76, 43.98) * mm});
            skLineSegment(sketch, "E1699", {"start": v(-41.76, 43.98) * mm, "end": v(-41.61, 43.82) * mm});
            skLineSegment(sketch, "E1700", {"start": v(-41.61, 43.82) * mm, "end": v(-41.5, 43.7) * mm});
            skLineSegment(sketch, "E1701", {"start": v(-41.5, 43.7) * mm, "end": v(-41.66, 43.56) * mm});
            skLineSegment(sketch, "E1702", {"start": v(-41.66, 43.56) * mm, "end": v(-41.82, 43.4) * mm});
            skLineSegment(sketch, "E1703", {"start": v(-41.82, 43.4) * mm, "end": v(-41.97, 43.25) * mm});
            skLineSegment(sketch, "E1704", {"start": v(-41.97, 43.25) * mm, "end": v(-42.13, 43.1) * mm});
            skLineSegment(sketch, "E1705", {"start": v(-42.13, 43.1) * mm, "end": v(-42.29, 42.95) * mm});
            skLineSegment(sketch, "E1706", {"start": v(-42.29, 42.95) * mm, "end": v(-42.44, 42.8) * mm});
            skLineSegment(sketch, "E1707", {"start": v(-42.44, 42.8) * mm, "end": v(-42.6, 42.65) * mm});
            skLineSegment(sketch, "E1708", {"start": v(-42.6, 42.65) * mm, "end": v(-42.76, 42.5) * mm});
            skLineSegment(sketch, "E1709", {"start": v(-42.76, 42.5) * mm, "end": v(-42.91, 42.34) * mm});
            skLineSegment(sketch, "E1710", {"start": v(-42.91, 42.34) * mm, "end": v(-43.07, 42.2) * mm});
            skLineSegment(sketch, "E1711", {"start": v(-43.07, 42.2) * mm, "end": v(-43.23, 42.04) * mm});
            skLineSegment(sketch, "E1712", {"start": v(-43.23, 42.04) * mm, "end": v(-43.3, 41.97) * mm});
            skLineSegment(sketch, "E1713", {"start": v(-43.3, 41.97) * mm, "end": v(-43.46, 42.12) * mm});
            skLineSegment(sketch, "E1714", {"start": v(-43.46, 42.12) * mm, "end": v(-43.61, 42.28) * mm});
            skLineSegment(sketch, "E1715", {"start": v(-43.61, 42.28) * mm, "end": v(-43.77, 42.43) * mm});
            skLineSegment(sketch, "E1716", {"start": v(-43.77, 42.43) * mm, "end": v(-43.93, 42.59) * mm});
            skLineSegment(sketch, "E1717", {"start": v(-43.93, 42.59) * mm, "end": v(-44.08, 42.74) * mm});
            skLineSegment(sketch, "E1718", {"start": v(-44.08, 42.74) * mm, "end": v(-44.24, 42.9) * mm});
            skLineSegment(sketch, "E1719", {"start": v(-44.24, 42.9) * mm, "end": v(-44.4, 43.05) * mm});
            skLineSegment(sketch, "E1720", {"start": v(-44.4, 43.05) * mm, "end": v(-44.55, 43.2) * mm});
            skLineSegment(sketch, "E1721", {"start": v(-44.55, 43.2) * mm, "end": v(-44.7, 43.36) * mm});
            skLineSegment(sketch, "E1722", {"start": v(-44.7, 43.36) * mm, "end": v(-44.86, 43.52) * mm});
            skLineSegment(sketch, "E1723", {"start": v(-44.86, 43.52) * mm, "end": v(-45.02, 43.67) * mm});
            skLineSegment(sketch, "E1724", {"start": v(-45.02, 43.67) * mm, "end": v(-45.18, 43.83) * mm});
            skLineSegment(sketch, "E1725", {"start": v(-45.18, 43.83) * mm, "end": v(-45.34, 44) * mm});
            skLineSegment(sketch, "E1726", {"start": v(-45.34, 44) * mm, "end": v(-45.53, 44.12) * mm});
            skLineSegment(sketch, "E1727", {"start": v(-45.53, 44.12) * mm, "end": v(-45.75, 44.2) * mm});
            skLineSegment(sketch, "E1728", {"start": v(-45.75, 44.2) * mm, "end": v(-45.93, 44.2) * mm});
            skLineSegment(sketch, "E1729", {"start": v(-45.93, 44.2) * mm, "end": v(-46.15, 44.17) * mm});
            skLineSegment(sketch, "E1730", {"start": v(-46.15, 44.17) * mm, "end": v(-46.36, 44.08) * mm});
            skLineSegment(sketch, "E1731", {"start": v(-46.36, 44.08) * mm, "end": v(-46.54, 43.94) * mm});
            skLineSegment(sketch, "E1732", {"start": v(-46.54, 43.94) * mm, "end": v(-46.67, 43.76) * mm});
            skLineSegment(sketch, "E1733", {"start": v(-46.67, 43.76) * mm, "end": v(-46.76, 43.55) * mm});
            skLineSegment(sketch, "E1734", {"start": v(-46.76, 43.55) * mm, "end": v(-46.78, 43.32) * mm});
            skLineSegment(sketch, "E1735", {"start": v(-46.78, 43.32) * mm, "end": v(-46.75, 43.1) * mm});
            skLineSegment(sketch, "E1736", {"start": v(-46.75, 43.1) * mm, "end": v(-46.66, 42.9) * mm});
            skLineSegment(sketch, "E1737", {"start": v(-46.66, 42.9) * mm, "end": v(-46.51, 42.71) * mm});
            skLineSegment(sketch, "E1738", {"start": v(-46.51, 42.71) * mm, "end": v(-46.36, 42.56) * mm});
            skLineSegment(sketch, "E1739", {"start": v(-46.36, 42.56) * mm, "end": v(-46.2, 42.41) * mm});
            skLineSegment(sketch, "E1740", {"start": v(-46.2, 42.41) * mm, "end": v(-46.03, 42.26) * mm});
            skLineSegment(sketch, "E1741", {"start": v(-46.03, 42.26) * mm, "end": v(-45.87, 42.11) * mm});
            skLineSegment(sketch, "E1742", {"start": v(-45.87, 42.11) * mm, "end": v(-45.72, 41.96) * mm});
            skLineSegment(sketch, "E1743", {"start": v(-45.72, 41.96) * mm, "end": v(-45.55, 41.8) * mm});
            skLineSegment(sketch, "E1744", {"start": v(-45.55, 41.8) * mm, "end": v(-45.4, 41.66) * mm});
            skLineSegment(sketch, "E1745", {"start": v(-45.4, 41.66) * mm, "end": v(-45.23, 41.51) * mm});
            skLineSegment(sketch, "E1746", {"start": v(-45.23, 41.51) * mm, "end": v(-45.07, 41.36) * mm});
            skLineSegment(sketch, "E1747", {"start": v(-45.07, 41.36) * mm, "end": v(-44.91, 41.2) * mm});
            skLineSegment(sketch, "E1748", {"start": v(-44.91, 41.2) * mm, "end": v(-44.75, 41.06) * mm});
            skLineSegment(sketch, "E1749", {"start": v(-44.75, 41.06) * mm, "end": v(-44.6, 40.9) * mm});
            skLineSegment(sketch, "E1750", {"start": v(-44.6, 40.9) * mm, "end": v(-44.45, 40.78) * mm});
            skLineSegment(sketch, "E1751", {"start": v(-44.45, 40.78) * mm, "end": v(-44.6, 40.62) * mm});
            skLineSegment(sketch, "E1752", {"start": v(-44.6, 40.62) * mm, "end": v(-44.74, 40.45) * mm});
            skLineSegment(sketch, "E1753", {"start": v(-44.74, 40.45) * mm, "end": v(-44.9, 40.3) * mm});
            skLineSegment(sketch, "E1754", {"start": v(-44.9, 40.3) * mm, "end": v(-45.04, 40.13) * mm});
            skLineSegment(sketch, "E1755", {"start": v(-45.04, 40.13) * mm, "end": v(-45.18, 39.97) * mm});
            skLineSegment(sketch, "E1756", {"start": v(-45.18, 39.97) * mm, "end": v(-45.33, 39.8) * mm});
            skLineSegment(sketch, "E1757", {"start": v(-45.33, 39.8) * mm, "end": v(-45.47, 39.64) * mm});
            skLineSegment(sketch, "E1758", {"start": v(-45.47, 39.64) * mm, "end": v(-45.62, 39.48) * mm});
            skLineSegment(sketch, "E1759", {"start": v(-45.62, 39.48) * mm, "end": v(-45.77, 39.32) * mm});
            skLineSegment(sketch, "E1760", {"start": v(-45.77, 39.32) * mm, "end": v(-45.91, 39.16) * mm});
            skLineSegment(sketch, "E1761", {"start": v(-45.91, 39.16) * mm, "end": v(-46.06, 39) * mm});
            skLineSegment(sketch, "E1762", {"start": v(-46.06, 39) * mm, "end": v(-46.13, 38.92) * mm});
            skLineSegment(sketch, "E1763", {"start": v(-46.13, 38.92) * mm, "end": v(-46.3, 39.06) * mm});
            skLineSegment(sketch, "E1764", {"start": v(-46.3, 39.06) * mm, "end": v(-46.46, 39.2) * mm});
            skLineSegment(sketch, "E1765", {"start": v(-46.46, 39.2) * mm, "end": v(-46.63, 39.35) * mm});
            skLineSegment(sketch, "E1766", {"start": v(-46.63, 39.35) * mm, "end": v(-46.8, 39.5) * mm});
            skLineSegment(sketch, "E1767", {"start": v(-46.8, 39.5) * mm, "end": v(-46.96, 39.63) * mm});
            skLineSegment(sketch, "E1768", {"start": v(-46.96, 39.63) * mm, "end": v(-47.13, 39.78) * mm});
            skLineSegment(sketch, "E1769", {"start": v(-47.13, 39.78) * mm, "end": v(-47.3, 39.92) * mm});
            skLineSegment(sketch, "E1770", {"start": v(-47.3, 39.92) * mm, "end": v(-47.46, 40.06) * mm});
            skLineSegment(sketch, "E1771", {"start": v(-47.46, 40.06) * mm, "end": v(-47.63, 40.21) * mm});
            skLineSegment(sketch, "E1772", {"start": v(-47.63, 40.21) * mm, "end": v(-47.8, 40.35) * mm});
            skLineSegment(sketch, "E1773", {"start": v(-47.8, 40.35) * mm, "end": v(-47.96, 40.5) * mm});
            skLineSegment(sketch, "E1774", {"start": v(-47.96, 40.5) * mm, "end": v(-48.13, 40.64) * mm});
            skLineSegment(sketch, "E1775", {"start": v(-48.13, 40.64) * mm, "end": v(-48.3, 40.8) * mm});
            skLineSegment(sketch, "E1776", {"start": v(-48.3, 40.8) * mm, "end": v(-48.5, 40.9) * mm});
            skLineSegment(sketch, "E1777", {"start": v(-48.5, 40.9) * mm, "end": v(-48.72, 40.96) * mm});
            skLineSegment(sketch, "E1778", {"start": v(-48.72, 40.96) * mm, "end": v(-48.81, 40.97) * mm});
            skLineSegment(sketch, "E1779", {"start": v(-48.81, 40.97) * mm, "end": v(-49.04, 40.95) * mm});
            skLineSegment(sketch, "E1780", {"start": v(-49.04, 40.95) * mm, "end": v(-49.25, 40.86) * mm});
            skLineSegment(sketch, "E1781", {"start": v(-49.25, 40.86) * mm, "end": v(-49.43, 40.73) * mm});
            skLineSegment(sketch, "E1782", {"start": v(-49.43, 40.73) * mm, "end": v(-49.57, 40.55) * mm});
            skLineSegment(sketch, "E1783", {"start": v(-49.57, 40.55) * mm, "end": v(-49.66, 40.34) * mm});
            skLineSegment(sketch, "E1784", {"start": v(-49.66, 40.34) * mm, "end": v(-49.7, 40.12) * mm});
            skLineSegment(sketch, "E1785", {"start": v(-49.7, 40.12) * mm, "end": v(-49.67, 39.9) * mm});
            skLineSegment(sketch, "E1786", {"start": v(-49.67, 39.9) * mm, "end": v(-49.59, 39.68) * mm});
            skLineSegment(sketch, "E1787", {"start": v(-49.59, 39.68) * mm, "end": v(-49.45, 39.5) * mm});
            skLineSegment(sketch, "E1788", {"start": v(-49.45, 39.5) * mm, "end": v(-49.28, 39.36) * mm});
            skLineSegment(sketch, "E1789", {"start": v(-49.28, 39.36) * mm, "end": v(-49.12, 39.22) * mm});
            skLineSegment(sketch, "E1790", {"start": v(-49.12, 39.22) * mm, "end": v(-48.94, 39.08) * mm});
            skLineSegment(sketch, "E1791", {"start": v(-48.94, 39.08) * mm, "end": v(-48.78, 38.94) * mm});
            skLineSegment(sketch, "E1792", {"start": v(-48.78, 38.94) * mm, "end": v(-48.6, 38.8) * mm});
            skLineSegment(sketch, "E1793", {"start": v(-48.6, 38.8) * mm, "end": v(-48.43, 38.66) * mm});
            skLineSegment(sketch, "E1794", {"start": v(-48.43, 38.66) * mm, "end": v(-48.26, 38.52) * mm});
            skLineSegment(sketch, "E1795", {"start": v(-48.26, 38.52) * mm, "end": v(-48.1, 38.39) * mm});
            skLineSegment(sketch, "E1796", {"start": v(-48.1, 38.39) * mm, "end": v(-47.92, 38.25) * mm});
            skLineSegment(sketch, "E1797", {"start": v(-47.92, 38.25) * mm, "end": v(-47.75, 38.1) * mm});
            skLineSegment(sketch, "E1798", {"start": v(-47.75, 38.1) * mm, "end": v(-47.58, 37.97) * mm});
            skLineSegment(sketch, "E1799", {"start": v(-47.58, 37.97) * mm, "end": v(-47.41, 37.83) * mm});
            skLineSegment(sketch, "E1800", {"start": v(-47.41, 37.83) * mm, "end": v(-47.24, 37.7) * mm});
            skLineSegment(sketch, "E1801", {"start": v(-47.24, 37.7) * mm, "end": v(-47.2, 37.65) * mm});
            skLineSegment(sketch, "E1802", {"start": v(-47.2, 37.65) * mm, "end": v(-47.33, 37.48) * mm});
            skLineSegment(sketch, "E1803", {"start": v(-47.33, 37.48) * mm, "end": v(-47.46, 37.3) * mm});
            skLineSegment(sketch, "E1804", {"start": v(-47.46, 37.3) * mm, "end": v(-47.6, 37.13) * mm});
            skLineSegment(sketch, "E1805", {"start": v(-47.6, 37.13) * mm, "end": v(-47.73, 36.96) * mm});
            skLineSegment(sketch, "E1806", {"start": v(-47.73, 36.96) * mm, "end": v(-47.86, 36.8) * mm});
            skLineSegment(sketch, "E1807", {"start": v(-47.86, 36.8) * mm, "end": v(-48, 36.62) * mm});
            skLineSegment(sketch, "E1808", {"start": v(-48, 36.62) * mm, "end": v(-48.13, 36.45) * mm});
            skLineSegment(sketch, "E1809", {"start": v(-48.13, 36.45) * mm, "end": v(-48.26, 36.28) * mm});
            skLineSegment(sketch, "E1810", {"start": v(-48.26, 36.28) * mm, "end": v(-48.4, 36.1) * mm});
            skLineSegment(sketch, "E1811", {"start": v(-48.4, 36.1) * mm, "end": v(-48.53, 35.93) * mm});
            skLineSegment(sketch, "E1812", {"start": v(-48.53, 35.93) * mm, "end": v(-48.67, 35.76) * mm});
            skLineSegment(sketch, "E1813", {"start": v(-48.67, 35.76) * mm, "end": v(-48.73, 35.68) * mm});
            skLineSegment(sketch, "E1814", {"start": v(-48.73, 35.68) * mm, "end": v(-48.9, 35.8) * mm});
            skLineSegment(sketch, "E1815", {"start": v(-48.9, 35.8) * mm, "end": v(-49.08, 35.94) * mm});
            skLineSegment(sketch, "E1816", {"start": v(-49.08, 35.94) * mm, "end": v(-49.26, 36.07) * mm});
            skLineSegment(sketch, "E1817", {"start": v(-49.26, 36.07) * mm, "end": v(-49.44, 36.2) * mm});
            skLineSegment(sketch, "E1818", {"start": v(-49.44, 36.2) * mm, "end": v(-49.61, 36.33) * mm});
            skLineSegment(sketch, "E1819", {"start": v(-49.61, 36.33) * mm, "end": v(-49.79, 36.47) * mm});
            skLineSegment(sketch, "E1820", {"start": v(-49.79, 36.47) * mm, "end": v(-49.96, 36.6) * mm});
            skLineSegment(sketch, "E1821", {"start": v(-49.96, 36.6) * mm, "end": v(-50.14, 36.73) * mm});
            skLineSegment(sketch, "E1822", {"start": v(-50.14, 36.73) * mm, "end": v(-50.32, 36.86) * mm});
            skLineSegment(sketch, "E1823", {"start": v(-50.32, 36.86) * mm, "end": v(-50.5, 37) * mm});
            skLineSegment(sketch, "E1824", {"start": v(-50.5, 37) * mm, "end": v(-50.67, 37.12) * mm});
            skLineSegment(sketch, "E1825", {"start": v(-50.67, 37.12) * mm, "end": v(-50.85, 37.26) * mm});
            skLineSegment(sketch, "E1826", {"start": v(-50.85, 37.26) * mm, "end": v(-51.03, 37.4) * mm});
            skLineSegment(sketch, "E1827", {"start": v(-51.03, 37.4) * mm, "end": v(-51.24, 37.5) * mm});
            skLineSegment(sketch, "E1828", {"start": v(-51.24, 37.5) * mm, "end": v(-51.46, 37.54) * mm});
            skLineSegment(sketch, "E1829", {"start": v(-51.46, 37.54) * mm, "end": v(-51.5, 37.54) * mm});
            skLineSegment(sketch, "E1830", {"start": v(-51.5, 37.54) * mm, "end": v(-51.73, 37.51) * mm});
            skLineSegment(sketch, "E1831", {"start": v(-51.73, 37.51) * mm, "end": v(-51.94, 37.42) * mm});
            skLineSegment(sketch, "E1832", {"start": v(-51.94, 37.42) * mm, "end": v(-52.12, 37.29) * mm});
            skLineSegment(sketch, "E1833", {"start": v(-52.12, 37.29) * mm, "end": v(-52.26, 37.1) * mm});
            skLineSegment(sketch, "E1834", {"start": v(-52.26, 37.1) * mm, "end": v(-52.35, 36.9) * mm});
            skLineSegment(sketch, "E1835", {"start": v(-52.35, 36.9) * mm, "end": v(-52.38, 36.67) * mm});
            skLineSegment(sketch, "E1836", {"start": v(-52.38, 36.67) * mm, "end": v(-52.35, 36.45) * mm});
            skLineSegment(sketch, "E1837", {"start": v(-52.35, 36.45) * mm, "end": v(-52.26, 36.24) * mm});
            skLineSegment(sketch, "E1838", {"start": v(-52.26, 36.24) * mm, "end": v(-52.12, 36.06) * mm});
            skLineSegment(sketch, "E1839", {"start": v(-52.12, 36.06) * mm, "end": v(-51.94, 35.91) * mm});
            skLineSegment(sketch, "E1840", {"start": v(-51.94, 35.91) * mm, "end": v(-51.76, 35.79) * mm});
            skLineSegment(sketch, "E1841", {"start": v(-51.76, 35.79) * mm, "end": v(-51.58, 35.66) * mm});
            skLineSegment(sketch, "E1842", {"start": v(-51.58, 35.66) * mm, "end": v(-51.4, 35.53) * mm});
            skLineSegment(sketch, "E1843", {"start": v(-51.4, 35.53) * mm, "end": v(-51.22, 35.4) * mm});
            skLineSegment(sketch, "E1844", {"start": v(-51.22, 35.4) * mm, "end": v(-51.04, 35.28) * mm});
            skLineSegment(sketch, "E1845", {"start": v(-51.04, 35.28) * mm, "end": v(-50.86, 35.15) * mm});
            skLineSegment(sketch, "E1846", {"start": v(-50.86, 35.15) * mm, "end": v(-50.68, 35.03) * mm});
            skLineSegment(sketch, "E1847", {"start": v(-50.68, 35.03) * mm, "end": v(-50.5, 34.9) * mm});
            skLineSegment(sketch, "E1848", {"start": v(-50.5, 34.9) * mm, "end": v(-50.32, 34.77) * mm});
            skLineSegment(sketch, "E1849", {"start": v(-50.32, 34.77) * mm, "end": v(-50.14, 34.65) * mm});
            skLineSegment(sketch, "E1850", {"start": v(-50.14, 34.65) * mm, "end": v(-49.97, 34.52) * mm});
            skLineSegment(sketch, "E1851", {"start": v(-49.97, 34.52) * mm, "end": v(-49.78, 34.4) * mm});
            skLineSegment(sketch, "E1852", {"start": v(-49.78, 34.4) * mm, "end": v(-49.7, 34.34) * mm});
            skLineSegment(sketch, "E1853", {"start": v(-49.7, 34.34) * mm, "end": v(-49.83, 34.16) * mm});
            skLineSegment(sketch, "E1854", {"start": v(-49.83, 34.16) * mm, "end": v(-49.95, 33.98) * mm});
            skLineSegment(sketch, "E1855", {"start": v(-49.95, 33.98) * mm, "end": v(-50.07, 33.8) * mm});
            skLineSegment(sketch, "E1856", {"start": v(-50.07, 33.8) * mm, "end": v(-50.2, 33.62) * mm});
            skLineSegment(sketch, "E1857", {"start": v(-50.2, 33.62) * mm, "end": v(-50.31, 33.43) * mm});
            skLineSegment(sketch, "E1858", {"start": v(-50.31, 33.43) * mm, "end": v(-50.44, 33.25) * mm});
            skLineSegment(sketch, "E1859", {"start": v(-50.44, 33.25) * mm, "end": v(-50.56, 33.07) * mm});
            skLineSegment(sketch, "E1860", {"start": v(-50.56, 33.07) * mm, "end": v(-50.68, 32.9) * mm});
            skLineSegment(sketch, "E1861", {"start": v(-50.68, 32.9) * mm, "end": v(-50.8, 32.71) * mm});
            skLineSegment(sketch, "E1862", {"start": v(-50.8, 32.71) * mm, "end": v(-50.92, 32.53) * mm});
            skLineSegment(sketch, "E1863", {"start": v(-50.92, 32.53) * mm, "end": v(-51.05, 32.35) * mm});
            skLineSegment(sketch, "E1864", {"start": v(-51.05, 32.35) * mm, "end": v(-51.1, 32.26) * mm});
            skLineSegment(sketch, "E1865", {"start": v(-51.1, 32.26) * mm, "end": v(-51.29, 32.38) * mm});
            skLineSegment(sketch, "E1866", {"start": v(-51.29, 32.38) * mm, "end": v(-51.47, 32.5) * mm});
            skLineSegment(sketch, "E1867", {"start": v(-51.47, 32.5) * mm, "end": v(-51.66, 32.62) * mm});
            skLineSegment(sketch, "E1868", {"start": v(-51.66, 32.62) * mm, "end": v(-51.84, 32.74) * mm});
            skLineSegment(sketch, "E1869", {"start": v(-51.84, 32.74) * mm, "end": v(-52.03, 32.86) * mm});
            skLineSegment(sketch, "E1870", {"start": v(-52.03, 32.86) * mm, "end": v(-52.21, 32.98) * mm});
            skLineSegment(sketch, "E1871", {"start": v(-52.21, 32.98) * mm, "end": v(-52.4, 33.1) * mm});
            skLineSegment(sketch, "E1872", {"start": v(-52.4, 33.1) * mm, "end": v(-52.58, 33.21) * mm});
            skLineSegment(sketch, "E1873", {"start": v(-52.58, 33.21) * mm, "end": v(-52.77, 33.34) * mm});
            skLineSegment(sketch, "E1874", {"start": v(-52.77, 33.34) * mm, "end": v(-52.95, 33.45) * mm});
            skLineSegment(sketch, "E1875", {"start": v(-52.95, 33.45) * mm, "end": v(-53.14, 33.57) * mm});
            skLineSegment(sketch, "E1876", {"start": v(-53.14, 33.57) * mm, "end": v(-53.32, 33.7) * mm});
            skLineSegment(sketch, "E1877", {"start": v(-53.32, 33.7) * mm, "end": v(-53.52, 33.82) * mm});
            skLineSegment(sketch, "E1878", {"start": v(-53.52, 33.82) * mm, "end": v(-53.73, 33.9) * mm});
            skLineSegment(sketch, "E1879", {"start": v(-53.73, 33.9) * mm, "end": v(-53.96, 33.93) * mm});
            skLineSegment(sketch, "E1880", {"start": v(-53.96, 33.93) * mm, "end": v(-54.18, 33.9) * mm});
            skLineSegment(sketch, "E1881", {"start": v(-54.18, 33.9) * mm, "end": v(-54.4, 33.8) * mm});
            skLineSegment(sketch, "E1882", {"start": v(-54.4, 33.8) * mm, "end": v(-54.57, 33.67) * mm});
            skLineSegment(sketch, "E1883", {"start": v(-54.57, 33.67) * mm, "end": v(-54.7, 33.48) * mm});
            skLineSegment(sketch, "E1884", {"start": v(-54.7, 33.48) * mm, "end": v(-54.79, 33.27) * mm});
            skLineSegment(sketch, "E1885", {"start": v(-54.79, 33.27) * mm, "end": v(-54.81, 33.05) * mm});
            skLineSegment(sketch, "E1886", {"start": v(-54.81, 33.05) * mm, "end": v(-54.78, 32.82) * mm});
            skLineSegment(sketch, "E1887", {"start": v(-54.78, 32.82) * mm, "end": v(-54.69, 32.61) * mm});
            skLineSegment(sketch, "E1888", {"start": v(-54.69, 32.61) * mm, "end": v(-54.55, 32.44) * mm});
            skLineSegment(sketch, "E1889", {"start": v(-54.55, 32.44) * mm, "end": v(-54.37, 32.3) * mm});
            skLineSegment(sketch, "E1890", {"start": v(-54.37, 32.3) * mm, "end": v(-54.18, 32.2) * mm});
            skLineSegment(sketch, "E1891", {"start": v(-54.18, 32.2) * mm, "end": v(-54, 32.08) * mm});
            skLineSegment(sketch, "E1892", {"start": v(-54, 32.08) * mm, "end": v(-53.81, 31.97) * mm});
            skLineSegment(sketch, "E1893", {"start": v(-53.81, 31.97) * mm, "end": v(-53.63, 31.85) * mm});
            skLineSegment(sketch, "E1894", {"start": v(-53.63, 31.85) * mm, "end": v(-53.43, 31.74) * mm});
            skLineSegment(sketch, "E1895", {"start": v(-53.43, 31.74) * mm, "end": v(-53.25, 31.63) * mm});
            skLineSegment(sketch, "E1896", {"start": v(-53.25, 31.63) * mm, "end": v(-53.06, 31.51) * mm});
            skLineSegment(sketch, "E1897", {"start": v(-53.06, 31.51) * mm, "end": v(-52.87, 31.4) * mm});
            skLineSegment(sketch, "E1898", {"start": v(-52.87, 31.4) * mm, "end": v(-52.68, 31.28) * mm});
            skLineSegment(sketch, "E1899", {"start": v(-52.68, 31.28) * mm, "end": v(-52.5, 31.17) * mm});
            skLineSegment(sketch, "E1900", {"start": v(-52.5, 31.17) * mm, "end": v(-52.3, 31.05) * mm});
            skLineSegment(sketch, "E1901", {"start": v(-52.3, 31.05) * mm, "end": v(-52.12, 30.94) * mm});
            skLineSegment(sketch, "E1902", {"start": v(-52.12, 30.94) * mm, "end": v(-51.98, 30.86) * mm});
            skLineSegment(sketch, "E1903", {"start": v(-51.98, 30.86) * mm, "end": v(-52.1, 30.67) * mm});
            skLineSegment(sketch, "E1904", {"start": v(-52.1, 30.67) * mm, "end": v(-52.2, 30.48) * mm});
            skLineSegment(sketch, "E1905", {"start": v(-52.2, 30.48) * mm, "end": v(-52.3, 30.3) * mm});
            skLineSegment(sketch, "E1906", {"start": v(-52.3, 30.3) * mm, "end": v(-52.42, 30.1) * mm});
            skLineSegment(sketch, "E1907", {"start": v(-52.42, 30.1) * mm, "end": v(-52.53, 29.92) * mm});
            skLineSegment(sketch, "E1908", {"start": v(-52.53, 29.92) * mm, "end": v(-52.64, 29.73) * mm});
            skLineSegment(sketch, "E1909", {"start": v(-52.64, 29.73) * mm, "end": v(-52.75, 29.54) * mm});
            skLineSegment(sketch, "E1910", {"start": v(-52.75, 29.54) * mm, "end": v(-52.85, 29.35) * mm});
            skLineSegment(sketch, "E1911", {"start": v(-52.85, 29.35) * mm, "end": v(-52.96, 29.16) * mm});
            skLineSegment(sketch, "E1912", {"start": v(-52.96, 29.16) * mm, "end": v(-53.07, 28.97) * mm});
            skLineSegment(sketch, "E1913", {"start": v(-53.07, 28.97) * mm, "end": v(-53.18, 28.78) * mm});
            skLineSegment(sketch, "E1914", {"start": v(-53.18, 28.78) * mm, "end": v(-53.23, 28.7) * mm});
            skLineSegment(sketch, "E1915", {"start": v(-53.23, 28.7) * mm, "end": v(-53.42, 28.8) * mm});
            skLineSegment(sketch, "E1916", {"start": v(-53.42, 28.8) * mm, "end": v(-53.62, 28.9) * mm});
            skLineSegment(sketch, "E1917", {"start": v(-53.62, 28.9) * mm, "end": v(-53.81, 29) * mm});
            skLineSegment(sketch, "E1918", {"start": v(-53.81, 29) * mm, "end": v(-54, 29.11) * mm});
            skLineSegment(sketch, "E1919", {"start": v(-54, 29.11) * mm, "end": v(-54.2, 29.22) * mm});
            skLineSegment(sketch, "E1920", {"start": v(-54.2, 29.22) * mm, "end": v(-54.4, 29.33) * mm});
            skLineSegment(sketch, "E1921", {"start": v(-54.4, 29.33) * mm, "end": v(-54.58, 29.43) * mm});
            skLineSegment(sketch, "E1922", {"start": v(-54.58, 29.43) * mm, "end": v(-54.77, 29.54) * mm});
            skLineSegment(sketch, "E1923", {"start": v(-54.77, 29.54) * mm, "end": v(-54.97, 29.65) * mm});
            skLineSegment(sketch, "E1924", {"start": v(-54.97, 29.65) * mm, "end": v(-55.16, 29.75) * mm});
            skLineSegment(sketch, "E1925", {"start": v(-55.16, 29.75) * mm, "end": v(-55.35, 29.86) * mm});
            skLineSegment(sketch, "E1926", {"start": v(-55.35, 29.86) * mm, "end": v(-55.55, 29.96) * mm});
            skLineSegment(sketch, "E1927", {"start": v(-55.55, 29.96) * mm, "end": v(-55.75, 30.07) * mm});
            skLineSegment(sketch, "E1928", {"start": v(-55.75, 30.07) * mm, "end": v(-55.97, 30.14) * mm});
            skLineSegment(sketch, "E1929", {"start": v(-55.97, 30.14) * mm, "end": v(-56.1, 30.16) * mm});
            skLineSegment(sketch, "E1930", {"start": v(-56.1, 30.16) * mm, "end": v(-56.33, 30.13) * mm});
            skLineSegment(sketch, "E1931", {"start": v(-56.33, 30.13) * mm, "end": v(-56.54, 30.05) * mm});
            skLineSegment(sketch, "E1932", {"start": v(-56.54, 30.05) * mm, "end": v(-56.73, 29.92) * mm});
            skLineSegment(sketch, "E1933", {"start": v(-56.73, 29.92) * mm, "end": v(-56.87, 29.74) * mm});
            skLineSegment(sketch, "E1934", {"start": v(-56.87, 29.74) * mm, "end": v(-56.96, 29.53) * mm});
            skLineSegment(sketch, "E1935", {"start": v(-56.96, 29.53) * mm, "end": v(-57, 29.3) * mm});
            skLineSegment(sketch, "E1936", {"start": v(-57, 29.3) * mm, "end": v(-56.96, 29.08) * mm});
            skLineSegment(sketch, "E1937", {"start": v(-56.96, 29.08) * mm, "end": v(-56.88, 28.87) * mm});
            skLineSegment(sketch, "E1938", {"start": v(-56.88, 28.87) * mm, "end": v(-56.74, 28.69) * mm});
            skLineSegment(sketch, "E1939", {"start": v(-56.74, 28.69) * mm, "end": v(-56.57, 28.55) * mm});
            skLineSegment(sketch, "E1940", {"start": v(-56.57, 28.55) * mm, "end": v(-56.36, 28.44) * mm});
            skLineSegment(sketch, "E1941", {"start": v(-56.36, 28.44) * mm, "end": v(-56.16, 28.34) * mm});
            skLineSegment(sketch, "E1942", {"start": v(-56.16, 28.34) * mm, "end": v(-55.97, 28.24) * mm});
            skLineSegment(sketch, "E1943", {"start": v(-55.97, 28.24) * mm, "end": v(-55.77, 28.14) * mm});
            skLineSegment(sketch, "E1944", {"start": v(-55.77, 28.14) * mm, "end": v(-55.58, 28.04) * mm});
            skLineSegment(sketch, "E1945", {"start": v(-55.58, 28.04) * mm, "end": v(-55.38, 27.94) * mm});
            skLineSegment(sketch, "E1946", {"start": v(-55.38, 27.94) * mm, "end": v(-55.18, 27.83) * mm});
            skLineSegment(sketch, "E1947", {"start": v(-55.18, 27.83) * mm, "end": v(-55, 27.73) * mm});
            skLineSegment(sketch, "E1948", {"start": v(-55, 27.73) * mm, "end": v(-54.8, 27.63) * mm});
            skLineSegment(sketch, "E1949", {"start": v(-54.8, 27.63) * mm, "end": v(-54.6, 27.53) * mm});
            skLineSegment(sketch, "E1950", {"start": v(-54.6, 27.53) * mm, "end": v(-54.4, 27.43) * mm});
            skLineSegment(sketch, "E1951", {"start": v(-54.4, 27.43) * mm, "end": v(-54.21, 27.33) * mm});
            skLineSegment(sketch, "E1952", {"start": v(-54.21, 27.33) * mm, "end": v(-54.01, 27.23) * mm});
            skLineSegment(sketch, "E1953", {"start": v(-54.01, 27.23) * mm, "end": v(-54.1, 27.03) * mm});
            skLineSegment(sketch, "E1954", {"start": v(-54.1, 27.03) * mm, "end": v(-54.2, 26.84) * mm});
            skLineSegment(sketch, "E1955", {"start": v(-54.2, 26.84) * mm, "end": v(-54.3, 26.64) * mm});
            skLineSegment(sketch, "E1956", {"start": v(-54.3, 26.64) * mm, "end": v(-54.4, 26.45) * mm});
            skLineSegment(sketch, "E1957", {"start": v(-54.4, 26.45) * mm, "end": v(-54.49, 26.25) * mm});
            skLineSegment(sketch, "E1958", {"start": v(-54.49, 26.25) * mm, "end": v(-54.58, 26.06) * mm});
            skLineSegment(sketch, "E1959", {"start": v(-54.58, 26.06) * mm, "end": v(-54.68, 25.86) * mm});
            skLineSegment(sketch, "E1960", {"start": v(-54.68, 25.86) * mm, "end": v(-54.78, 25.66) * mm});
            skLineSegment(sketch, "E1961", {"start": v(-54.78, 25.66) * mm, "end": v(-54.87, 25.47) * mm});
            skLineSegment(sketch, "E1962", {"start": v(-54.87, 25.47) * mm, "end": v(-54.97, 25.27) * mm});
            skLineSegment(sketch, "E1963", {"start": v(-54.97, 25.27) * mm, "end": v(-55.06, 25.08) * mm});
            skLineSegment(sketch, "E1964", {"start": v(-55.06, 25.08) * mm, "end": v(-55.1, 24.98) * mm});
            skLineSegment(sketch, "E1965", {"start": v(-55.1, 24.98) * mm, "end": v(-55.3, 25.07) * mm});
            skLineSegment(sketch, "E1966", {"start": v(-55.3, 25.07) * mm, "end": v(-55.5, 25.16) * mm});
            skLineSegment(sketch, "E1967", {"start": v(-55.5, 25.16) * mm, "end": v(-55.7, 25.26) * mm});
            skLineSegment(sketch, "E1968", {"start": v(-55.7, 25.26) * mm, "end": v(-55.9, 25.35) * mm});
            skLineSegment(sketch, "E1969", {"start": v(-55.9, 25.35) * mm, "end": v(-56.1, 25.44) * mm});
            skLineSegment(sketch, "E1970", {"start": v(-56.1, 25.44) * mm, "end": v(-56.3, 25.53) * mm});
            skLineSegment(sketch, "E1971", {"start": v(-56.3, 25.53) * mm, "end": v(-56.5, 25.63) * mm});
            skLineSegment(sketch, "E1972", {"start": v(-56.5, 25.63) * mm, "end": v(-56.7, 25.72) * mm});
            skLineSegment(sketch, "E1973", {"start": v(-56.7, 25.72) * mm, "end": v(-56.9, 25.81) * mm});
            skLineSegment(sketch, "E1974", {"start": v(-56.9, 25.81) * mm, "end": v(-57.1, 25.9) * mm});
            skLineSegment(sketch, "E1975", {"start": v(-57.1, 25.9) * mm, "end": v(-57.3, 26) * mm});
            skLineSegment(sketch, "E1976", {"start": v(-57.3, 26) * mm, "end": v(-57.5, 26.09) * mm});
            skLineSegment(sketch, "E1977", {"start": v(-57.5, 26.09) * mm, "end": v(-57.72, 26.18) * mm});
            skLineSegment(sketch, "E1978", {"start": v(-57.72, 26.18) * mm, "end": v(-57.94, 26.24) * mm});
            skLineSegment(sketch, "E1979", {"start": v(-57.94, 26.24) * mm, "end": v(-58.03, 26.24) * mm});
            skLineSegment(sketch, "E1980", {"start": v(-58.03, 26.24) * mm, "end": v(-58.25, 26.22) * mm});
            skLineSegment(sketch, "E1981", {"start": v(-58.25, 26.22) * mm, "end": v(-58.46, 26.13) * mm});
            skLineSegment(sketch, "E1982", {"start": v(-58.46, 26.13) * mm, "end": v(-58.65, 26) * mm});
            skLineSegment(sketch, "E1983", {"start": v(-58.65, 26) * mm, "end": v(-58.78, 25.81) * mm});
            skLineSegment(sketch, "E1984", {"start": v(-58.78, 25.81) * mm, "end": v(-58.87, 25.6) * mm});
            skLineSegment(sketch, "E1985", {"start": v(-58.87, 25.6) * mm, "end": v(-58.9, 25.38) * mm});
            skLineSegment(sketch, "E1986", {"start": v(-58.9, 25.38) * mm, "end": v(-58.87, 25.15) * mm});
            skLineSegment(sketch, "E1987", {"start": v(-58.87, 25.15) * mm, "end": v(-58.78, 24.94) * mm});
            skLineSegment(sketch, "E1988", {"start": v(-58.78, 24.94) * mm, "end": v(-58.64, 24.76) * mm});
            skLineSegment(sketch, "E1989", {"start": v(-58.64, 24.76) * mm, "end": v(-58.46, 24.62) * mm});
            skLineSegment(sketch, "E1990", {"start": v(-58.46, 24.62) * mm, "end": v(-58.26, 24.53) * mm});
            skLineSegment(sketch, "E1991", {"start": v(-58.26, 24.53) * mm, "end": v(-58.06, 24.45) * mm});
            skLineSegment(sketch, "E1992", {"start": v(-58.06, 24.45) * mm, "end": v(-57.86, 24.36) * mm});
            skLineSegment(sketch, "E1993", {"start": v(-57.86, 24.36) * mm, "end": v(-57.66, 24.27) * mm});
            skLineSegment(sketch, "E1994", {"start": v(-57.66, 24.27) * mm, "end": v(-57.46, 24.19) * mm});
            skLineSegment(sketch, "E1995", {"start": v(-57.46, 24.19) * mm, "end": v(-57.25, 24.1) * mm});
            skLineSegment(sketch, "E1996", {"start": v(-57.25, 24.1) * mm, "end": v(-57.05, 24.01) * mm});
            skLineSegment(sketch, "E1997", {"start": v(-57.05, 24.01) * mm, "end": v(-56.85, 23.93) * mm});
            skLineSegment(sketch, "E1998", {"start": v(-56.85, 23.93) * mm, "end": v(-56.65, 23.84) * mm});
            skLineSegment(sketch, "E1999", {"start": v(-56.65, 23.84) * mm, "end": v(-56.45, 23.75) * mm});
            skLineSegment(sketch, "E2000", {"start": v(-56.45, 23.75) * mm, "end": v(-56.25, 23.67) * mm});
            skLineSegment(sketch, "E2001", {"start": v(-56.25, 23.67) * mm, "end": v(-56.04, 23.58) * mm});
            skLineSegment(sketch, "E2002", {"start": v(-56.04, 23.58) * mm, "end": v(-55.84, 23.5) * mm});
            skLineSegment(sketch, "E2003", {"start": v(-55.84, 23.5) * mm, "end": v(-55.78, 23.47) * mm});
            skLineSegment(sketch, "E2004", {"start": v(-55.78, 23.47) * mm, "end": v(-55.86, 23.27) * mm});
            skLineSegment(sketch, "E2005", {"start": v(-55.86, 23.27) * mm, "end": v(-55.94, 23.06) * mm});
            skLineSegment(sketch, "E2006", {"start": v(-55.94, 23.06) * mm, "end": v(-56.03, 22.86) * mm});
            skLineSegment(sketch, "E2007", {"start": v(-56.03, 22.86) * mm, "end": v(-56.1, 22.66) * mm});
            skLineSegment(sketch, "E2008", {"start": v(-56.1, 22.66) * mm, "end": v(-56.19, 22.46) * mm});
            skLineSegment(sketch, "E2009", {"start": v(-56.19, 22.46) * mm, "end": v(-56.27, 22.26) * mm});
            skLineSegment(sketch, "E2010", {"start": v(-56.27, 22.26) * mm, "end": v(-56.35, 22.05) * mm});
            skLineSegment(sketch, "E2011", {"start": v(-56.35, 22.05) * mm, "end": v(-56.43, 21.85) * mm});
            skLineSegment(sketch, "E2012", {"start": v(-56.43, 21.85) * mm, "end": v(-56.52, 21.65) * mm});
            skLineSegment(sketch, "E2013", {"start": v(-56.52, 21.65) * mm, "end": v(-56.6, 21.45) * mm});
            skLineSegment(sketch, "E2014", {"start": v(-56.6, 21.45) * mm, "end": v(-56.68, 21.25) * mm});
            skLineSegment(sketch, "E2015", {"start": v(-56.68, 21.25) * mm, "end": v(-56.72, 21.15) * mm});
            skLineSegment(sketch, "E2016", {"start": v(-56.72, 21.15) * mm, "end": v(-56.92, 21.23) * mm});
            skLineSegment(sketch, "E2017", {"start": v(-56.92, 21.23) * mm, "end": v(-57.13, 21.3) * mm});
            skLineSegment(sketch, "E2018", {"start": v(-57.13, 21.3) * mm, "end": v(-57.34, 21.38) * mm});
            skLineSegment(sketch, "E2019", {"start": v(-57.34, 21.38) * mm, "end": v(-57.54, 21.46) * mm});
            skLineSegment(sketch, "E2020", {"start": v(-57.54, 21.46) * mm, "end": v(-57.74, 21.54) * mm});
            skLineSegment(sketch, "E2021", {"start": v(-57.74, 21.54) * mm, "end": v(-57.95, 21.62) * mm});
            skLineSegment(sketch, "E2022", {"start": v(-57.95, 21.62) * mm, "end": v(-58.16, 21.7) * mm});
            skLineSegment(sketch, "E2023", {"start": v(-58.16, 21.7) * mm, "end": v(-58.36, 21.77) * mm});
            skLineSegment(sketch, "E2024", {"start": v(-58.36, 21.77) * mm, "end": v(-58.57, 21.85) * mm});
            skLineSegment(sketch, "E2025", {"start": v(-58.57, 21.85) * mm, "end": v(-58.77, 21.93) * mm});
            skLineSegment(sketch, "E2026", {"start": v(-58.77, 21.93) * mm, "end": v(-58.98, 22) * mm});
            skLineSegment(sketch, "E2027", {"start": v(-58.98, 22) * mm, "end": v(-59.19, 22.08) * mm});
            skLineSegment(sketch, "E2028", {"start": v(-59.19, 22.08) * mm, "end": v(-59.4, 22.17) * mm});
            skLineSegment(sketch, "E2029", {"start": v(-59.4, 22.17) * mm, "end": v(-59.63, 22.2) * mm});
            skLineSegment(sketch, "E2030", {"start": v(-59.63, 22.2) * mm, "end": v(-59.68, 22.2) * mm});
            skLineSegment(sketch, "E2031", {"start": v(-59.68, 22.2) * mm, "end": v(-59.9, 22.17) * mm});
            skLineSegment(sketch, "E2032", {"start": v(-59.9, 22.17) * mm, "end": v(-60.1, 22.08) * mm});
            skLineSegment(sketch, "E2033", {"start": v(-60.1, 22.08) * mm, "end": v(-60.29, 21.94) * mm});
            skLineSegment(sketch, "E2034", {"start": v(-60.29, 21.94) * mm, "end": v(-60.42, 21.76) * mm});
            skLineSegment(sketch, "E2035", {"start": v(-60.42, 21.76) * mm, "end": v(-60.5, 21.55) * mm});
            skLineSegment(sketch, "E2036", {"start": v(-60.5, 21.55) * mm, "end": v(-60.53, 21.32) * mm});
            skLineSegment(sketch, "E2037", {"start": v(-60.53, 21.32) * mm, "end": v(-60.5, 21.1) * mm});
            skLineSegment(sketch, "E2038", {"start": v(-60.5, 21.1) * mm, "end": v(-60.4, 20.89) * mm});
            skLineSegment(sketch, "E2039", {"start": v(-60.4, 20.89) * mm, "end": v(-60.26, 20.71) * mm});
            skLineSegment(sketch, "E2040", {"start": v(-60.26, 20.71) * mm, "end": v(-60.08, 20.58) * mm});
            skLineSegment(sketch, "E2041", {"start": v(-60.08, 20.58) * mm, "end": v(-59.87, 20.5) * mm});
            skLineSegment(sketch, "E2042", {"start": v(-59.87, 20.5) * mm, "end": v(-59.66, 20.42) * mm});
            skLineSegment(sketch, "E2043", {"start": v(-59.66, 20.42) * mm, "end": v(-59.46, 20.35) * mm});
            skLineSegment(sketch, "E2044", {"start": v(-59.46, 20.35) * mm, "end": v(-59.24, 20.27) * mm});
            skLineSegment(sketch, "E2045", {"start": v(-59.24, 20.27) * mm, "end": v(-59.04, 20.2) * mm});
            skLineSegment(sketch, "E2046", {"start": v(-59.04, 20.2) * mm, "end": v(-58.83, 20.13) * mm});
            skLineSegment(sketch, "E2047", {"start": v(-58.83, 20.13) * mm, "end": v(-58.62, 20.06) * mm});
            skLineSegment(sketch, "E2048", {"start": v(-58.62, 20.06) * mm, "end": v(-58.41, 19.99) * mm});
            skLineSegment(sketch, "E2049", {"start": v(-58.41, 19.99) * mm, "end": v(-58.2, 19.91) * mm});
            skLineSegment(sketch, "E2050", {"start": v(-58.2, 19.91) * mm, "end": v(-58, 19.84) * mm});
            skLineSegment(sketch, "E2051", {"start": v(-58, 19.84) * mm, "end": v(-57.8, 19.77) * mm});
            skLineSegment(sketch, "E2052", {"start": v(-57.8, 19.77) * mm, "end": v(-57.59, 19.7) * mm});
            skLineSegment(sketch, "E2053", {"start": v(-57.59, 19.7) * mm, "end": v(-57.37, 19.62) * mm});
            skLineSegment(sketch, "E2054", {"start": v(-57.37, 19.62) * mm, "end": v(-57.29, 19.6) * mm});
            skLineSegment(sketch, "E2055", {"start": v(-57.29, 19.6) * mm, "end": v(-57.35, 19.39) * mm});
            skLineSegment(sketch, "E2056", {"start": v(-57.35, 19.39) * mm, "end": v(-57.42, 19.18) * mm});
            skLineSegment(sketch, "E2057", {"start": v(-57.42, 19.18) * mm, "end": v(-57.49, 18.97) * mm});
            skLineSegment(sketch, "E2058", {"start": v(-57.49, 18.97) * mm, "end": v(-57.55, 18.76) * mm});
            skLineSegment(sketch, "E2059", {"start": v(-57.55, 18.76) * mm, "end": v(-57.62, 18.56) * mm});
            skLineSegment(sketch, "E2060", {"start": v(-57.62, 18.56) * mm, "end": v(-57.69, 18.35) * mm});
            skLineSegment(sketch, "E2061", {"start": v(-57.69, 18.35) * mm, "end": v(-57.76, 18.14) * mm});
            skLineSegment(sketch, "E2062", {"start": v(-57.76, 18.14) * mm, "end": v(-57.82, 17.93) * mm});
            skLineSegment(sketch, "E2063", {"start": v(-57.82, 17.93) * mm, "end": v(-57.9, 17.73) * mm});
            skLineSegment(sketch, "E2064", {"start": v(-57.9, 17.73) * mm, "end": v(-57.96, 17.52) * mm});
            skLineSegment(sketch, "E2065", {"start": v(-57.96, 17.52) * mm, "end": v(-58.03, 17.31) * mm});
            skLineSegment(sketch, "E2066", {"start": v(-58.03, 17.31) * mm, "end": v(-58.06, 17.21) * mm});
            skLineSegment(sketch, "E2067", {"start": v(-58.06, 17.21) * mm, "end": v(-58.27, 17.28) * mm});
            skLineSegment(sketch, "E2068", {"start": v(-58.27, 17.28) * mm, "end": v(-58.48, 17.34) * mm});
            skLineSegment(sketch, "E2069", {"start": v(-58.48, 17.34) * mm, "end": v(-58.7, 17.4) * mm});
            skLineSegment(sketch, "E2070", {"start": v(-58.7, 17.4) * mm, "end": v(-58.9, 17.47) * mm});
            skLineSegment(sketch, "E2071", {"start": v(-58.9, 17.47) * mm, "end": v(-59.1, 17.53) * mm});
            skLineSegment(sketch, "E2072", {"start": v(-59.1, 17.53) * mm, "end": v(-59.32, 17.6) * mm});
            skLineSegment(sketch, "E2073", {"start": v(-59.32, 17.6) * mm, "end": v(-59.53, 17.66) * mm});
            skLineSegment(sketch, "E2074", {"start": v(-59.53, 17.66) * mm, "end": v(-59.74, 17.72) * mm});
            skLineSegment(sketch, "E2075", {"start": v(-59.74, 17.72) * mm, "end": v(-59.95, 17.78) * mm});
            skLineSegment(sketch, "E2076", {"start": v(-59.95, 17.78) * mm, "end": v(-60.16, 17.85) * mm});
            skLineSegment(sketch, "E2077", {"start": v(-60.16, 17.85) * mm, "end": v(-60.37, 17.91) * mm});
            skLineSegment(sketch, "E2078", {"start": v(-60.37, 17.91) * mm, "end": v(-60.59, 17.97) * mm});
            skLineSegment(sketch, "E2079", {"start": v(-60.59, 17.97) * mm, "end": v(-60.8, 18.04) * mm});
            skLineSegment(sketch, "E2080", {"start": v(-60.8, 18.04) * mm, "end": v(-61, 18.06) * mm});
            skLineSegment(sketch, "E2081", {"start": v(-61, 18.06) * mm, "end": v(-61.22, 18.04) * mm});
            skLineSegment(sketch, "E2082", {"start": v(-61.22, 18.04) * mm, "end": v(-61.43, 17.96) * mm});
            skLineSegment(sketch, "E2083", {"start": v(-61.43, 17.96) * mm, "end": v(-61.61, 17.82) * mm});
            skLineSegment(sketch, "E2084", {"start": v(-61.61, 17.82) * mm, "end": v(-61.75, 17.64) * mm});
            skLineSegment(sketch, "E2085", {"start": v(-61.75, 17.64) * mm, "end": v(-61.84, 17.44) * mm});
            skLineSegment(sketch, "E2086", {"start": v(-61.84, 17.44) * mm, "end": v(-61.88, 17.21) * mm});
            skLineSegment(sketch, "E2087", {"start": v(-61.88, 17.21) * mm, "end": v(-61.85, 16.99) * mm});
            skLineSegment(sketch, "E2088", {"start": v(-61.85, 16.99) * mm, "end": v(-61.77, 16.77) * mm});
            skLineSegment(sketch, "E2089", {"start": v(-61.77, 16.77) * mm, "end": v(-61.63, 16.6) * mm});
            skLineSegment(sketch, "E2090", {"start": v(-61.63, 16.6) * mm, "end": v(-61.45, 16.45) * mm});
            skLineSegment(sketch, "E2091", {"start": v(-61.45, 16.45) * mm, "end": v(-61.24, 16.36) * mm});
            skLineSegment(sketch, "E2092", {"start": v(-61.24, 16.36) * mm, "end": v(-61.03, 16.3) * mm});
            skLineSegment(sketch, "E2093", {"start": v(-61.03, 16.3) * mm, "end": v(-60.82, 16.25) * mm});
            skLineSegment(sketch, "E2094", {"start": v(-60.82, 16.25) * mm, "end": v(-60.6, 16.19) * mm});
            skLineSegment(sketch, "E2095", {"start": v(-60.6, 16.19) * mm, "end": v(-60.4, 16.13) * mm});
            skLineSegment(sketch, "E2096", {"start": v(-60.4, 16.13) * mm, "end": v(-60.19, 16.08) * mm});
            skLineSegment(sketch, "E2097", {"start": v(-60.19, 16.08) * mm, "end": v(-59.97, 16.02) * mm});
            skLineSegment(sketch, "E2098", {"start": v(-59.97, 16.02) * mm, "end": v(-59.76, 15.96) * mm});
            skLineSegment(sketch, "E2099", {"start": v(-59.76, 15.96) * mm, "end": v(-59.55, 15.9) * mm});
            skLineSegment(sketch, "E2100", {"start": v(-59.55, 15.9) * mm, "end": v(-59.33, 15.84) * mm});
            skLineSegment(sketch, "E2101", {"start": v(-59.33, 15.84) * mm, "end": v(-59.12, 15.79) * mm});
            skLineSegment(sketch, "E2102", {"start": v(-59.12, 15.79) * mm, "end": v(-58.91, 15.73) * mm});
            skLineSegment(sketch, "E2103", {"start": v(-58.91, 15.73) * mm, "end": v(-58.7, 15.67) * mm});
            skLineSegment(sketch, "E2104", {"start": v(-58.7, 15.67) * mm, "end": v(-58.51, 15.62) * mm});
            skLineSegment(sketch, "E2105", {"start": v(-58.51, 15.62) * mm, "end": v(-58.57, 15.4) * mm});
            skLineSegment(sketch, "E2106", {"start": v(-58.57, 15.4) * mm, "end": v(-58.62, 15.2) * mm});
            skLineSegment(sketch, "E2107", {"start": v(-58.62, 15.2) * mm, "end": v(-58.67, 14.99) * mm});
            skLineSegment(sketch, "E2108", {"start": v(-58.67, 14.99) * mm, "end": v(-58.73, 14.78) * mm});
            skLineSegment(sketch, "E2109", {"start": v(-58.73, 14.78) * mm, "end": v(-58.78, 14.56) * mm});
            skLineSegment(sketch, "E2110", {"start": v(-58.78, 14.56) * mm, "end": v(-58.83, 14.35) * mm});
            skLineSegment(sketch, "E2111", {"start": v(-58.83, 14.35) * mm, "end": v(-58.88, 14.14) * mm});
            skLineSegment(sketch, "E2112", {"start": v(-58.88, 14.14) * mm, "end": v(-58.94, 13.93) * mm});
            skLineSegment(sketch, "E2113", {"start": v(-58.94, 13.93) * mm, "end": v(-58.99, 13.72) * mm});
            skLineSegment(sketch, "E2114", {"start": v(-58.99, 13.72) * mm, "end": v(-59.04, 13.5) * mm});
            skLineSegment(sketch, "E2115", {"start": v(-59.04, 13.5) * mm, "end": v(-59.1, 13.3) * mm});
            skLineSegment(sketch, "E2116", {"start": v(-59.1, 13.3) * mm, "end": v(-59.12, 13.2) * mm});
            skLineSegment(sketch, "E2117", {"start": v(-59.12, 13.2) * mm, "end": v(-59.33, 13.24) * mm});
            skLineSegment(sketch, "E2118", {"start": v(-59.33, 13.24) * mm, "end": v(-59.55, 13.29) * mm});
            skLineSegment(sketch, "E2119", {"start": v(-59.55, 13.29) * mm, "end": v(-59.76, 13.34) * mm});
            skLineSegment(sketch, "E2120", {"start": v(-59.76, 13.34) * mm, "end": v(-59.98, 13.39) * mm});
            skLineSegment(sketch, "E2121", {"start": v(-59.98, 13.39) * mm, "end": v(-60.19, 13.44) * mm});
            skLineSegment(sketch, "E2122", {"start": v(-60.19, 13.44) * mm, "end": v(-60.4, 13.48) * mm});
            skLineSegment(sketch, "E2123", {"start": v(-60.4, 13.48) * mm, "end": v(-60.62, 13.53) * mm});
            skLineSegment(sketch, "E2124", {"start": v(-60.62, 13.53) * mm, "end": v(-60.83, 13.58) * mm});
            skLineSegment(sketch, "E2125", {"start": v(-60.83, 13.58) * mm, "end": v(-61.05, 13.63) * mm});
            skLineSegment(sketch, "E2126", {"start": v(-61.05, 13.63) * mm, "end": v(-61.26, 13.68) * mm});
            skLineSegment(sketch, "E2127", {"start": v(-61.26, 13.68) * mm, "end": v(-61.48, 13.73) * mm});
            skLineSegment(sketch, "E2128", {"start": v(-61.48, 13.73) * mm, "end": v(-61.7, 13.78) * mm});
            skLineSegment(sketch, "E2129", {"start": v(-61.7, 13.78) * mm, "end": v(-61.92, 13.83) * mm});
            skLineSegment(sketch, "E2130", {"start": v(-61.92, 13.83) * mm, "end": v(-62.06, 13.84) * mm});
            skLineSegment(sketch, "E2131", {"start": v(-62.06, 13.84) * mm, "end": v(-62.28, 13.81) * mm});
            skLineSegment(sketch, "E2132", {"start": v(-62.28, 13.81) * mm, "end": v(-62.5, 13.72) * mm});
            skLineSegment(sketch, "E2133", {"start": v(-62.5, 13.72) * mm, "end": v(-62.68, 13.59) * mm});
            skLineSegment(sketch, "E2134", {"start": v(-62.68, 13.59) * mm, "end": v(-62.81, 13.4) * mm});
            skLineSegment(sketch, "E2135", {"start": v(-62.81, 13.4) * mm, "end": v(-62.9, 13.2) * mm});
            skLineSegment(sketch, "E2136", {"start": v(-62.9, 13.2) * mm, "end": v(-62.93, 12.97) * mm});
            skLineSegment(sketch, "E2137", {"start": v(-62.93, 12.97) * mm, "end": v(-62.9, 12.75) * mm});
            skLineSegment(sketch, "E2138", {"start": v(-62.9, 12.75) * mm, "end": v(-62.81, 12.54) * mm});
            skLineSegment(sketch, "E2139", {"start": v(-62.81, 12.54) * mm, "end": v(-62.67, 12.36) * mm});
            skLineSegment(sketch, "E2140", {"start": v(-62.67, 12.36) * mm, "end": v(-62.5, 12.22) * mm});
            skLineSegment(sketch, "E2141", {"start": v(-62.5, 12.22) * mm, "end": v(-62.28, 12.13) * mm});
            skLineSegment(sketch, "E2142", {"start": v(-62.28, 12.13) * mm, "end": v(-62.05, 12.09) * mm});
            skLineSegment(sketch, "E2143", {"start": v(-62.05, 12.09) * mm, "end": v(-61.84, 12.04) * mm});
            skLineSegment(sketch, "E2144", {"start": v(-61.84, 12.04) * mm, "end": v(-61.63, 12) * mm});
            skLineSegment(sketch, "E2145", {"start": v(-61.63, 12) * mm, "end": v(-61.4, 11.96) * mm});
            skLineSegment(sketch, "E2146", {"start": v(-61.4, 11.96) * mm, "end": v(-61.2, 11.92) * mm});
            skLineSegment(sketch, "E2147", {"start": v(-61.2, 11.92) * mm, "end": v(-60.98, 11.87) * mm});
            skLineSegment(sketch, "E2148", {"start": v(-60.98, 11.87) * mm, "end": v(-60.76, 11.83) * mm});
            skLineSegment(sketch, "E2149", {"start": v(-60.76, 11.83) * mm, "end": v(-60.55, 11.79) * mm});
            skLineSegment(sketch, "E2150", {"start": v(-60.55, 11.79) * mm, "end": v(-60.33, 11.75) * mm});
            skLineSegment(sketch, "E2151", {"start": v(-60.33, 11.75) * mm, "end": v(-60.11, 11.7) * mm});
            skLineSegment(sketch, "E2152", {"start": v(-60.11, 11.7) * mm, "end": v(-59.9, 11.66) * mm});
            skLineSegment(sketch, "E2153", {"start": v(-59.9, 11.66) * mm, "end": v(-59.68, 11.62) * mm});
            skLineSegment(sketch, "E2154", {"start": v(-59.68, 11.62) * mm, "end": v(-59.46, 11.57) * mm});
            skLineSegment(sketch, "E2155", {"start": v(-59.46, 11.57) * mm, "end": v(-59.5, 11.36) * mm});
            skLineSegment(sketch, "E2156", {"start": v(-59.5, 11.36) * mm, "end": v(-59.54, 11.14) * mm});
            skLineSegment(sketch, "E2157", {"start": v(-59.54, 11.14) * mm, "end": v(-59.58, 10.93) * mm});
            skLineSegment(sketch, "E2158", {"start": v(-59.58, 10.93) * mm, "end": v(-59.62, 10.72) * mm});
            skLineSegment(sketch, "E2159", {"start": v(-59.62, 10.72) * mm, "end": v(-59.65, 10.5) * mm});
            skLineSegment(sketch, "E2160", {"start": v(-59.65, 10.5) * mm, "end": v(-59.7, 10.29) * mm});
            skLineSegment(sketch, "E2161", {"start": v(-59.7, 10.29) * mm, "end": v(-59.73, 10.07) * mm});
            skLineSegment(sketch, "E2162", {"start": v(-59.73, 10.07) * mm, "end": v(-59.77, 9.86) * mm});
            skLineSegment(sketch, "E2163", {"start": v(-59.77, 9.86) * mm, "end": v(-59.8, 9.64) * mm});
            skLineSegment(sketch, "E2164", {"start": v(-59.8, 9.64) * mm, "end": v(-59.84, 9.43) * mm});
            skLineSegment(sketch, "E2165", {"start": v(-59.84, 9.43) * mm, "end": v(-59.88, 9.21) * mm});
            skLineSegment(sketch, "E2166", {"start": v(-59.88, 9.21) * mm, "end": v(-59.9, 9.1) * mm});
            skLineSegment(sketch, "E2167", {"start": v(-59.9, 9.1) * mm, "end": v(-60.11, 9.14) * mm});
            skLineSegment(sketch, "E2168", {"start": v(-60.11, 9.14) * mm, "end": v(-60.33, 9.18) * mm});
            skLineSegment(sketch, "E2169", {"start": v(-60.33, 9.18) * mm, "end": v(-60.55, 9.2) * mm});
            skLineSegment(sketch, "E2170", {"start": v(-60.55, 9.2) * mm, "end": v(-60.77, 9.24) * mm});
            skLineSegment(sketch, "E2171", {"start": v(-60.77, 9.24) * mm, "end": v(-60.98, 9.28) * mm});
            skLineSegment(sketch, "E2172", {"start": v(-60.98, 9.28) * mm, "end": v(-61.2, 9.31) * mm});
            skLineSegment(sketch, "E2173", {"start": v(-61.2, 9.31) * mm, "end": v(-61.42, 9.34) * mm});
            skLineSegment(sketch, "E2174", {"start": v(-61.42, 9.34) * mm, "end": v(-61.63, 9.38) * mm});
            skLineSegment(sketch, "E2175", {"start": v(-61.63, 9.38) * mm, "end": v(-61.86, 9.41) * mm});
            skLineSegment(sketch, "E2176", {"start": v(-61.86, 9.41) * mm, "end": v(-62.07, 9.44) * mm});
            skLineSegment(sketch, "E2177", {"start": v(-62.07, 9.44) * mm, "end": v(-62.29, 9.48) * mm});
            skLineSegment(sketch, "E2178", {"start": v(-62.29, 9.48) * mm, "end": v(-62.5, 9.51) * mm});
            skLineSegment(sketch, "E2179", {"start": v(-62.5, 9.51) * mm, "end": v(-62.74, 9.55) * mm});
            skLineSegment(sketch, "E2180", {"start": v(-62.74, 9.55) * mm, "end": v(-62.83, 9.55) * mm});
            skLineSegment(sketch, "E2181", {"start": v(-62.83, 9.55) * mm, "end": v(-63.05, 9.52) * mm});
            skLineSegment(sketch, "E2182", {"start": v(-63.05, 9.52) * mm, "end": v(-63.26, 9.43) * mm});
            skLineSegment(sketch, "E2183", {"start": v(-63.26, 9.43) * mm, "end": v(-63.44, 9.29) * mm});
            skLineSegment(sketch, "E2184", {"start": v(-63.44, 9.29) * mm, "end": v(-63.58, 9.1) * mm});
            skLineSegment(sketch, "E2185", {"start": v(-63.58, 9.1) * mm, "end": v(-63.66, 8.9) * mm});
            skLineSegment(sketch, "E2186", {"start": v(-63.66, 8.9) * mm, "end": v(-63.69, 8.67) * mm});
            skLineSegment(sketch, "E2187", {"start": v(-63.69, 8.67) * mm, "end": v(-63.65, 8.44) * mm});
            skLineSegment(sketch, "E2188", {"start": v(-63.65, 8.44) * mm, "end": v(-63.56, 8.23) * mm});
            skLineSegment(sketch, "E2189", {"start": v(-63.56, 8.23) * mm, "end": v(-63.42, 8.06) * mm});
            skLineSegment(sketch, "E2190", {"start": v(-63.42, 8.06) * mm, "end": v(-63.24, 7.92) * mm});
            skLineSegment(sketch, "E2191", {"start": v(-63.24, 7.92) * mm, "end": v(-63.02, 7.84) * mm});
            skLineSegment(sketch, "E2192", {"start": v(-63.02, 7.84) * mm, "end": v(-62.8, 7.8) * mm});
            skLineSegment(sketch, "E2193", {"start": v(-62.8, 7.8) * mm, "end": v(-62.6, 7.78) * mm});
            skLineSegment(sketch, "E2194", {"start": v(-62.6, 7.78) * mm, "end": v(-62.37, 7.75) * mm});
            skLineSegment(sketch, "E2195", {"start": v(-62.37, 7.75) * mm, "end": v(-62.16, 7.73) * mm});
            skLineSegment(sketch, "E2196", {"start": v(-62.16, 7.73) * mm, "end": v(-61.94, 7.7) * mm});
            skLineSegment(sketch, "E2197", {"start": v(-61.94, 7.7) * mm, "end": v(-61.72, 7.67) * mm});
            skLineSegment(sketch, "E2198", {"start": v(-61.72, 7.67) * mm, "end": v(-61.5, 7.64) * mm});
            skLineSegment(sketch, "E2199", {"start": v(-61.5, 7.64) * mm, "end": v(-61.29, 7.62) * mm});
            skLineSegment(sketch, "E2200", {"start": v(-61.29, 7.62) * mm, "end": v(-61.06, 7.59) * mm});
            skLineSegment(sketch, "E2201", {"start": v(-61.06, 7.59) * mm, "end": v(-60.85, 7.56) * mm});
            skLineSegment(sketch, "E2202", {"start": v(-60.85, 7.56) * mm, "end": v(-60.63, 7.53) * mm});
            skLineSegment(sketch, "E2203", {"start": v(-60.63, 7.53) * mm, "end": v(-60.41, 7.5) * mm});
            skLineSegment(sketch, "E2204", {"start": v(-60.41, 7.5) * mm, "end": v(-60.2, 7.48) * mm});
            skLineSegment(sketch, "E2205", {"start": v(-60.2, 7.48) * mm, "end": v(-60.13, 7.47) * mm});
            skLineSegment(sketch, "E2206", {"start": v(-60.13, 7.47) * mm, "end": v(-60.15, 7.25) * mm});
            skLineSegment(sketch, "E2207", {"start": v(-60.15, 7.25) * mm, "end": v(-60.18, 7.04) * mm});
            skLineSegment(sketch, "E2208", {"start": v(-60.18, 7.04) * mm, "end": v(-60.2, 6.82) * mm});
            skLineSegment(sketch, "E2209", {"start": v(-60.2, 6.82) * mm, "end": v(-60.22, 6.6) * mm});
            skLineSegment(sketch, "E2210", {"start": v(-60.22, 6.6) * mm, "end": v(-60.24, 6.39) * mm});
            skLineSegment(sketch, "E2211", {"start": v(-60.24, 6.39) * mm, "end": v(-60.27, 6.17) * mm});
            skLineSegment(sketch, "E2212", {"start": v(-60.27, 6.17) * mm, "end": v(-60.29, 5.95) * mm});
            skLineSegment(sketch, "E2213", {"start": v(-60.29, 5.95) * mm, "end": v(-60.31, 5.74) * mm});
            skLineSegment(sketch, "E2214", {"start": v(-60.31, 5.74) * mm, "end": v(-60.33, 5.52) * mm});
            skLineSegment(sketch, "E2215", {"start": v(-60.33, 5.52) * mm, "end": v(-60.36, 5.3) * mm});
            skLineSegment(sketch, "E2216", {"start": v(-60.36, 5.3) * mm, "end": v(-60.38, 5.09) * mm});
            skLineSegment(sketch, "E2217", {"start": v(-60.38, 5.09) * mm, "end": v(-60.4, 4.98) * mm});
            skLineSegment(sketch, "E2218", {"start": v(-60.4, 4.98) * mm, "end": v(-60.6, 5) * mm});
            skLineSegment(sketch, "E2219", {"start": v(-60.6, 5) * mm, "end": v(-60.83, 5.02) * mm});
            skLineSegment(sketch, "E2220", {"start": v(-60.83, 5.02) * mm, "end": v(-61.05, 5.04) * mm});
            skLineSegment(sketch, "E2221", {"start": v(-61.05, 5.04) * mm, "end": v(-61.27, 5.05) * mm});
            skLineSegment(sketch, "E2222", {"start": v(-61.27, 5.05) * mm, "end": v(-61.48, 5.07) * mm});
            skLineSegment(sketch, "E2223", {"start": v(-61.48, 5.07) * mm, "end": v(-61.7, 5.1) * mm});
            skLineSegment(sketch, "E2224", {"start": v(-61.7, 5.1) * mm, "end": v(-61.92, 5.1) * mm});
            skLineSegment(sketch, "E2225", {"start": v(-61.92, 5.1) * mm, "end": v(-62.14, 5.13) * mm});
            skLineSegment(sketch, "E2226", {"start": v(-62.14, 5.13) * mm, "end": v(-62.36, 5.15) * mm});
            skLineSegment(sketch, "E2227", {"start": v(-62.36, 5.15) * mm, "end": v(-62.58, 5.16) * mm});
            skLineSegment(sketch, "E2228", {"start": v(-62.58, 5.16) * mm, "end": v(-62.8, 5.18) * mm});
            skLineSegment(sketch, "E2229", {"start": v(-62.8, 5.18) * mm, "end": v(-63.02, 5.2) * mm});
            skLineSegment(sketch, "E2230", {"start": v(-63.02, 5.2) * mm, "end": v(-63.25, 5.22) * mm});
            skLineSegment(sketch, "E2231", {"start": v(-63.25, 5.22) * mm, "end": v(-63.48, 5.2) * mm});
            skLineSegment(sketch, "E2232", {"start": v(-63.48, 5.2) * mm, "end": v(-63.7, 5.11) * mm});
            skLineSegment(sketch, "E2233", {"start": v(-63.7, 5.11) * mm, "end": v(-63.88, 4.98) * mm});
            skLineSegment(sketch, "E2234", {"start": v(-63.88, 4.98) * mm, "end": v(-64.02, 4.8) * mm});
            skLineSegment(sketch, "E2235", {"start": v(-64.02, 4.8) * mm, "end": v(-64.1, 4.6) * mm});
            skLineSegment(sketch, "E2236", {"start": v(-64.1, 4.6) * mm, "end": v(-64.14, 4.37) * mm});
            skLineSegment(sketch, "E2237", {"start": v(-64.14, 4.37) * mm, "end": v(-64.12, 4.14) * mm});
            skLineSegment(sketch, "E2238", {"start": v(-64.12, 4.14) * mm, "end": v(-64.03, 3.93) * mm});
            skLineSegment(sketch, "E2239", {"start": v(-64.03, 3.93) * mm, "end": v(-63.9, 3.75) * mm});
            skLineSegment(sketch, "E2240", {"start": v(-63.9, 3.75) * mm, "end": v(-63.72, 3.6) * mm});
            skLineSegment(sketch, "E2241", {"start": v(-63.72, 3.6) * mm, "end": v(-63.5, 3.52) * mm});
            skLineSegment(sketch, "E2242", {"start": v(-63.5, 3.52) * mm, "end": v(-63.3, 3.49) * mm});
            skLineSegment(sketch, "E2243", {"start": v(-63.3, 3.49) * mm, "end": v(-63.08, 3.47) * mm});
            skLineSegment(sketch, "E2244", {"start": v(-63.08, 3.47) * mm, "end": v(-62.86, 3.46) * mm});
            skLineSegment(sketch, "E2245", {"start": v(-62.86, 3.46) * mm, "end": v(-62.64, 3.45) * mm});
            skLineSegment(sketch, "E2246", {"start": v(-62.64, 3.45) * mm, "end": v(-62.42, 3.44) * mm});
            skLineSegment(sketch, "E2247", {"start": v(-62.42, 3.44) * mm, "end": v(-62.2, 3.42) * mm});
            skLineSegment(sketch, "E2248", {"start": v(-62.2, 3.42) * mm, "end": v(-61.98, 3.41) * mm});
            skLineSegment(sketch, "E2249", {"start": v(-61.98, 3.41) * mm, "end": v(-61.77, 3.4) * mm});
            skLineSegment(sketch, "E2250", {"start": v(-61.77, 3.4) * mm, "end": v(-61.54, 3.39) * mm});
            skLineSegment(sketch, "E2251", {"start": v(-61.54, 3.39) * mm, "end": v(-61.32, 3.37) * mm});
            skLineSegment(sketch, "E2252", {"start": v(-61.32, 3.37) * mm, "end": v(-61.1, 3.36) * mm});
            skLineSegment(sketch, "E2253", {"start": v(-61.1, 3.36) * mm, "end": v(-60.88, 3.35) * mm});
            skLineSegment(sketch, "E2254", {"start": v(-60.88, 3.35) * mm, "end": v(-60.67, 3.34) * mm});
            skLineSegment(sketch, "E2255", {"start": v(-60.67, 3.34) * mm, "end": v(-60.5, 3.33) * mm});
            skLineSegment(sketch, "E2256", {"start": v(-60.5, 3.33) * mm, "end": v(-60.51, 3.11) * mm});
            skLineSegment(sketch, "E2257", {"start": v(-60.51, 3.11) * mm, "end": v(-60.52, 2.9) * mm});
            skLineSegment(sketch, "E2258", {"start": v(-60.52, 2.9) * mm, "end": v(-60.53, 2.68) * mm});
            skLineSegment(sketch, "E2259", {"start": v(-60.53, 2.68) * mm, "end": v(-60.54, 2.46) * mm});
            skLineSegment(sketch, "E2260", {"start": v(-60.54, 2.46) * mm, "end": v(-60.54, 2.24) * mm});
            skLineSegment(sketch, "E2261", {"start": v(-60.54, 2.24) * mm, "end": v(-60.55, 2.02) * mm});
            skLineSegment(sketch, "E2262", {"start": v(-60.55, 2.02) * mm, "end": v(-60.56, 1.8) * mm});
            skLineSegment(sketch, "E2263", {"start": v(-60.56, 1.8) * mm, "end": v(-60.57, 1.59) * mm});
            skLineSegment(sketch, "E2264", {"start": v(-60.57, 1.59) * mm, "end": v(-60.58, 1.37) * mm});
            skLineSegment(sketch, "E2265", {"start": v(-60.58, 1.37) * mm, "end": v(-60.58, 1.15) * mm});
            skLineSegment(sketch, "E2266", {"start": v(-60.58, 1.15) * mm, "end": v(-60.6, 0.93) * mm});
            skLineSegment(sketch, "E2267", {"start": v(-60.6, 0.93) * mm, "end": v(-60.6, 0.83) * mm});
            skLineSegment(sketch, "E2268", {"start": v(-60.6, 0.83) * mm, "end": v(-60.81, 0.83) * mm});
            skLineSegment(sketch, "E2269", {"start": v(-60.81, 0.83) * mm, "end": v(-61.03, 0.83) * mm});
            skLineSegment(sketch, "E2270", {"start": v(-61.03, 0.83) * mm, "end": v(-61.25, 0.84) * mm});
            skLineSegment(sketch, "E2271", {"start": v(-61.25, 0.84) * mm, "end": v(-61.47, 0.84) * mm});
            skLineSegment(sketch, "E2272", {"start": v(-61.47, 0.84) * mm, "end": v(-61.69, 0.84) * mm});
            skLineSegment(sketch, "E2273", {"start": v(-61.69, 0.84) * mm, "end": v(-61.91, 0.85) * mm});
            skLineSegment(sketch, "E2274", {"start": v(-61.91, 0.85) * mm, "end": v(-62.13, 0.85) * mm});
            skLineSegment(sketch, "E2275", {"start": v(-62.13, 0.85) * mm, "end": v(-62.35, 0.85) * mm});
            skLineSegment(sketch, "E2276", {"start": v(-62.35, 0.85) * mm, "end": v(-62.57, 0.86) * mm});
            skLineSegment(sketch, "E2277", {"start": v(-62.57, 0.86) * mm, "end": v(-62.8, 0.86) * mm});
            skLineSegment(sketch, "E2278", {"start": v(-62.8, 0.86) * mm, "end": v(-63, 0.86) * mm});
            skLineSegment(sketch, "E2279", {"start": v(-63, 0.86) * mm, "end": v(-63.23, 0.86) * mm});
            skLineSegment(sketch, "E2280", {"start": v(-63.23, 0.86) * mm, "end": v(-63.42, 0.87) * mm});
            skLineSegment(sketch, "E2281", {"start": v(-63.42, 0.87) * mm, "end": v(-63.65, 0.84) * mm});
            skLineSegment(sketch, "E2282", {"start": v(-63.65, 0.84) * mm, "end": v(-63.86, 0.75) * mm});
            skLineSegment(sketch, "E2283", {"start": v(-63.86, 0.75) * mm, "end": v(-64.04, 0.62) * mm});
            skLineSegment(sketch, "E2284", {"start": v(-64.04, 0.62) * mm, "end": v(-64.18, 0.44) * mm});
            skLineSegment(sketch, "E2285", {"start": v(-64.18, 0.44) * mm, "end": v(-64.26, 0.23) * mm});
            skLineSegment(sketch, "E2286", {"start": v(-64.26, 0.23) * mm, "end": v(-64.3, 0) * mm});
            skLineSegment(sketch, "E2287", {"start": v(-64.3, 0) * mm, "end": v(-64.26, -0.23) * mm});
            skLineSegment(sketch, "E2288", {"start": v(-64.26, -0.23) * mm, "end": v(-64.18, -0.44) * mm});
            skLineSegment(sketch, "E2289", {"start": v(-64.18, -0.44) * mm, "end": v(-64.04, -0.62) * mm});
            skLineSegment(sketch, "E2290", {"start": v(-64.04, -0.62) * mm, "end": v(-63.86, -0.75) * mm});
            skLineSegment(sketch, "E2291", {"start": v(-63.86, -0.75) * mm, "end": v(-63.65, -0.84) * mm});
            skLineSegment(sketch, "E2292", {"start": v(-63.65, -0.84) * mm, "end": v(-63.42, -0.87) * mm});
            skLineSegment(sketch, "E2293", {"start": v(-63.42, -0.87) * mm, "end": v(-63.2, -0.86) * mm});
            skLineSegment(sketch, "E2294", {"start": v(-63.2, -0.86) * mm, "end": v(-62.99, -0.86) * mm});
            skLineSegment(sketch, "E2295", {"start": v(-62.99, -0.86) * mm, "end": v(-62.76, -0.86) * mm});
            skLineSegment(sketch, "E2296", {"start": v(-62.76, -0.86) * mm, "end": v(-62.54, -0.85) * mm});
            skLineSegment(sketch, "E2297", {"start": v(-62.54, -0.85) * mm, "end": v(-62.33, -0.85) * mm});
            skLineSegment(sketch, "E2298", {"start": v(-62.33, -0.85) * mm, "end": v(-62.1, -0.85) * mm});
            skLineSegment(sketch, "E2299", {"start": v(-62.1, -0.85) * mm, "end": v(-61.88, -0.85) * mm});
            skLineSegment(sketch, "E2300", {"start": v(-61.88, -0.85) * mm, "end": v(-61.67, -0.84) * mm});
            skLineSegment(sketch, "E2301", {"start": v(-61.67, -0.84) * mm, "end": v(-61.44, -0.84) * mm});
            skLineSegment(sketch, "E2302", {"start": v(-61.44, -0.84) * mm, "end": v(-61.22, -0.84) * mm});
            skLineSegment(sketch, "E2303", {"start": v(-61.22, -0.84) * mm, "end": v(-61, -0.83) * mm});
            skLineSegment(sketch, "E2304", {"start": v(-61, -0.83) * mm, "end": v(-60.78, -0.83) * mm});
            skLineSegment(sketch, "E2305", {"start": v(-60.78, -0.83) * mm, "end": v(-60.6, -0.83) * mm});
            skLineSegment(sketch, "E2306", {"start": v(-60.6, -0.83) * mm, "end": v(-60.59, -1.05) * mm});
            skLineSegment(sketch, "E2307", {"start": v(-60.59, -1.05) * mm, "end": v(-60.58, -1.26) * mm});
            skLineSegment(sketch, "E2308", {"start": v(-60.58, -1.26) * mm, "end": v(-60.57, -1.48) * mm});
            skLineSegment(sketch, "E2309", {"start": v(-60.57, -1.48) * mm, "end": v(-60.56, -1.7) * mm});
            skLineSegment(sketch, "E2310", {"start": v(-60.56, -1.7) * mm, "end": v(-60.56, -1.92) * mm});
            skLineSegment(sketch, "E2311", {"start": v(-60.56, -1.92) * mm, "end": v(-60.55, -2.13) * mm});
            skLineSegment(sketch, "E2312", {"start": v(-60.55, -2.13) * mm, "end": v(-60.54, -2.35) * mm});
            skLineSegment(sketch, "E2313", {"start": v(-60.54, -2.35) * mm, "end": v(-60.53, -2.57) * mm});
            skLineSegment(sketch, "E2314", {"start": v(-60.53, -2.57) * mm, "end": v(-60.53, -2.79) * mm});
            skLineSegment(sketch, "E2315", {"start": v(-60.53, -2.79) * mm, "end": v(-60.52, -3) * mm});
            skLineSegment(sketch, "E2316", {"start": v(-60.52, -3) * mm, "end": v(-60.51, -3.22) * mm});
            skLineSegment(sketch, "E2317", {"start": v(-60.51, -3.22) * mm, "end": v(-60.5, -3.33) * mm});
            skLineSegment(sketch, "E2318", {"start": v(-60.5, -3.33) * mm, "end": v(-60.72, -3.34) * mm});
            skLineSegment(sketch, "E2319", {"start": v(-60.72, -3.34) * mm, "end": v(-60.94, -3.35) * mm});
            skLineSegment(sketch, "E2320", {"start": v(-60.94, -3.35) * mm, "end": v(-61.17, -3.37) * mm});
            skLineSegment(sketch, "E2321", {"start": v(-61.17, -3.37) * mm, "end": v(-61.38, -3.38) * mm});
            skLineSegment(sketch, "E2322", {"start": v(-61.38, -3.38) * mm, "end": v(-61.6, -3.4) * mm});
            skLineSegment(sketch, "E2323", {"start": v(-61.6, -3.4) * mm, "end": v(-61.82, -3.4) * mm});
            skLineSegment(sketch, "E2324", {"start": v(-61.82, -3.4) * mm, "end": v(-62.04, -3.41) * mm});
            skLineSegment(sketch, "E2325", {"start": v(-62.04, -3.41) * mm, "end": v(-62.26, -3.43) * mm});
            skLineSegment(sketch, "E2326", {"start": v(-62.26, -3.43) * mm, "end": v(-62.48, -3.44) * mm});
            skLineSegment(sketch, "E2327", {"start": v(-62.48, -3.44) * mm, "end": v(-62.7, -3.45) * mm});
            skLineSegment(sketch, "E2328", {"start": v(-62.7, -3.45) * mm, "end": v(-62.92, -3.46) * mm});
            skLineSegment(sketch, "E2329", {"start": v(-62.92, -3.46) * mm, "end": v(-63.14, -3.48) * mm});
            skLineSegment(sketch, "E2330", {"start": v(-63.14, -3.48) * mm, "end": v(-63.38, -3.5) * mm});
            skLineSegment(sketch, "E2331", {"start": v(-63.38, -3.5) * mm, "end": v(-63.6, -3.55) * mm});
            skLineSegment(sketch, "E2332", {"start": v(-63.6, -3.55) * mm, "end": v(-63.8, -3.66) * mm});
            skLineSegment(sketch, "E2333", {"start": v(-63.8, -3.66) * mm, "end": v(-63.96, -3.82) * mm});
            skLineSegment(sketch, "E2334", {"start": v(-63.96, -3.82) * mm, "end": v(-64.07, -4.01) * mm});
            skLineSegment(sketch, "E2335", {"start": v(-64.07, -4.01) * mm, "end": v(-64.13, -4.23) * mm});
            skLineSegment(sketch, "E2336", {"start": v(-64.13, -4.23) * mm, "end": v(-64.14, -4.46) * mm});
            skLineSegment(sketch, "E2337", {"start": v(-64.14, -4.46) * mm, "end": v(-64.08, -4.68) * mm});
            skLineSegment(sketch, "E2338", {"start": v(-64.08, -4.68) * mm, "end": v(-63.97, -4.88) * mm});
            skLineSegment(sketch, "E2339", {"start": v(-63.97, -4.88) * mm, "end": v(-63.8, -5.04) * mm});
            skLineSegment(sketch, "E2340", {"start": v(-63.8, -5.04) * mm, "end": v(-63.61, -5.15) * mm});
            skLineSegment(sketch, "E2341", {"start": v(-63.61, -5.15) * mm, "end": v(-63.4, -5.21) * mm});
            skLineSegment(sketch, "E2342", {"start": v(-63.4, -5.21) * mm, "end": v(-63.17, -5.2) * mm});
            skLineSegment(sketch, "E2343", {"start": v(-63.17, -5.2) * mm, "end": v(-62.96, -5.2) * mm});
            skLineSegment(sketch, "E2344", {"start": v(-62.96, -5.2) * mm, "end": v(-62.74, -5.18) * mm});
            skLineSegment(sketch, "E2345", {"start": v(-62.74, -5.18) * mm, "end": v(-62.52, -5.16) * mm});
            skLineSegment(sketch, "E2346", {"start": v(-62.52, -5.16) * mm, "end": v(-62.3, -5.14) * mm});
            skLineSegment(sketch, "E2347", {"start": v(-62.3, -5.14) * mm, "end": v(-62.08, -5.12) * mm});
            skLineSegment(sketch, "E2348", {"start": v(-62.08, -5.12) * mm, "end": v(-61.86, -5.1) * mm});
            skLineSegment(sketch, "E2349", {"start": v(-61.86, -5.1) * mm, "end": v(-61.65, -5.09) * mm});
            skLineSegment(sketch, "E2350", {"start": v(-61.65, -5.09) * mm, "end": v(-61.42, -5.07) * mm});
            skLineSegment(sketch, "E2351", {"start": v(-61.42, -5.07) * mm, "end": v(-61.2, -5.05) * mm});
            skLineSegment(sketch, "E2352", {"start": v(-61.2, -5.05) * mm, "end": v(-61, -5.03) * mm});
            skLineSegment(sketch, "E2353", {"start": v(-61, -5.03) * mm, "end": v(-60.77, -5.01) * mm});
            skLineSegment(sketch, "E2354", {"start": v(-60.77, -5.01) * mm, "end": v(-60.55, -5) * mm});
            skLineSegment(sketch, "E2355", {"start": v(-60.55, -5) * mm, "end": v(-60.4, -4.98) * mm});
            skLineSegment(sketch, "E2356", {"start": v(-60.4, -4.98) * mm, "end": v(-60.37, -5.2) * mm});
            skLineSegment(sketch, "E2357", {"start": v(-60.37, -5.2) * mm, "end": v(-60.35, -5.41) * mm});
            skLineSegment(sketch, "E2358", {"start": v(-60.35, -5.41) * mm, "end": v(-60.32, -5.63) * mm});
            skLineSegment(sketch, "E2359", {"start": v(-60.32, -5.63) * mm, "end": v(-60.3, -5.85) * mm});
            skLineSegment(sketch, "E2360", {"start": v(-60.3, -5.85) * mm, "end": v(-60.28, -6.06) * mm});
            skLineSegment(sketch, "E2361", {"start": v(-60.28, -6.06) * mm, "end": v(-60.25, -6.28) * mm});
            skLineSegment(sketch, "E2362", {"start": v(-60.25, -6.28) * mm, "end": v(-60.23, -6.5) * mm});
            skLineSegment(sketch, "E2363", {"start": v(-60.23, -6.5) * mm, "end": v(-60.2, -6.71) * mm});
            skLineSegment(sketch, "E2364", {"start": v(-60.2, -6.71) * mm, "end": v(-60.19, -6.93) * mm});
            skLineSegment(sketch, "E2365", {"start": v(-60.19, -6.93) * mm, "end": v(-60.16, -7.15) * mm});
            skLineSegment(sketch, "E2366", {"start": v(-60.16, -7.15) * mm, "end": v(-60.14, -7.36) * mm});
            skLineSegment(sketch, "E2367", {"start": v(-60.14, -7.36) * mm, "end": v(-60.13, -7.47) * mm});
            skLineSegment(sketch, "E2368", {"start": v(-60.13, -7.47) * mm, "end": v(-60.35, -7.5) * mm});
            skLineSegment(sketch, "E2369", {"start": v(-60.35, -7.5) * mm, "end": v(-60.56, -7.52) * mm});
            skLineSegment(sketch, "E2370", {"start": v(-60.56, -7.52) * mm, "end": v(-60.78, -7.55) * mm});
            skLineSegment(sketch, "E2371", {"start": v(-60.78, -7.55) * mm, "end": v(-61, -7.58) * mm});
            skLineSegment(sketch, "E2372", {"start": v(-61, -7.58) * mm, "end": v(-61.22, -7.6) * mm});
            skLineSegment(sketch, "E2373", {"start": v(-61.22, -7.6) * mm, "end": v(-61.44, -7.63) * mm});
            skLineSegment(sketch, "E2374", {"start": v(-61.44, -7.63) * mm, "end": v(-61.65, -7.66) * mm});
            skLineSegment(sketch, "E2375", {"start": v(-61.65, -7.66) * mm, "end": v(-61.87, -7.69) * mm});
            skLineSegment(sketch, "E2376", {"start": v(-61.87, -7.69) * mm, "end": v(-62.1, -7.72) * mm});
            skLineSegment(sketch, "E2377", {"start": v(-62.1, -7.72) * mm, "end": v(-62.3, -7.74) * mm});
            skLineSegment(sketch, "E2378", {"start": v(-62.3, -7.74) * mm, "end": v(-62.53, -7.77) * mm});
            skLineSegment(sketch, "E2379", {"start": v(-62.53, -7.77) * mm, "end": v(-62.75, -7.8) * mm});
            skLineSegment(sketch, "E2380", {"start": v(-62.75, -7.8) * mm, "end": v(-62.98, -7.83) * mm});
            skLineSegment(sketch, "E2381", {"start": v(-62.98, -7.83) * mm, "end": v(-63.2, -7.9) * mm});
            skLineSegment(sketch, "E2382", {"start": v(-63.2, -7.9) * mm, "end": v(-63.39, -8.03) * mm});
            skLineSegment(sketch, "E2383", {"start": v(-63.39, -8.03) * mm, "end": v(-63.54, -8.2) * mm});
            skLineSegment(sketch, "E2384", {"start": v(-63.54, -8.2) * mm, "end": v(-63.64, -8.4) * mm});
            skLineSegment(sketch, "E2385", {"start": v(-63.64, -8.4) * mm, "end": v(-63.68, -8.62) * mm});
            skLineSegment(sketch, "E2386", {"start": v(-63.68, -8.62) * mm, "end": v(-63.67, -8.85) * mm});
            skLineSegment(sketch, "E2387", {"start": v(-63.67, -8.85) * mm, "end": v(-63.6, -9.06) * mm});
            skLineSegment(sketch, "E2388", {"start": v(-63.6, -9.06) * mm, "end": v(-63.47, -9.25) * mm});
            skLineSegment(sketch, "E2389", {"start": v(-63.47, -9.25) * mm, "end": v(-63.3, -9.4) * mm});
            skLineSegment(sketch, "E2390", {"start": v(-63.3, -9.4) * mm, "end": v(-63.1, -9.5) * mm});
            skLineSegment(sketch, "E2391", {"start": v(-63.1, -9.5) * mm, "end": v(-62.88, -9.55) * mm});
            skLineSegment(sketch, "E2392", {"start": v(-62.88, -9.55) * mm, "end": v(-62.66, -9.53) * mm});
            skLineSegment(sketch, "E2393", {"start": v(-62.66, -9.53) * mm, "end": v(-62.44, -9.5) * mm});
            skLineSegment(sketch, "E2394", {"start": v(-62.44, -9.5) * mm, "end": v(-62.23, -9.47) * mm});
            skLineSegment(sketch, "E2395", {"start": v(-62.23, -9.47) * mm, "end": v(-62.01, -9.44) * mm});
            skLineSegment(sketch, "E2396", {"start": v(-62.01, -9.44) * mm, "end": v(-61.8, -9.4) * mm});
            skLineSegment(sketch, "E2397", {"start": v(-61.8, -9.4) * mm, "end": v(-61.58, -9.37) * mm});
            skLineSegment(sketch, "E2398", {"start": v(-61.58, -9.37) * mm, "end": v(-61.36, -9.33) * mm});
            skLineSegment(sketch, "E2399", {"start": v(-61.36, -9.33) * mm, "end": v(-61.15, -9.3) * mm});
            skLineSegment(sketch, "E2400", {"start": v(-61.15, -9.3) * mm, "end": v(-60.92, -9.27) * mm});
            skLineSegment(sketch, "E2401", {"start": v(-60.92, -9.27) * mm, "end": v(-60.7, -9.23) * mm});
            skLineSegment(sketch, "E2402", {"start": v(-60.7, -9.23) * mm, "end": v(-60.5, -9.2) * mm});
            skLineSegment(sketch, "E2403", {"start": v(-60.5, -9.2) * mm, "end": v(-60.27, -9.17) * mm});
            skLineSegment(sketch, "E2404", {"start": v(-60.27, -9.17) * mm, "end": v(-60.06, -9.13) * mm});
            skLineSegment(sketch, "E2405", {"start": v(-60.06, -9.13) * mm, "end": v(-59.9, -9.1) * mm});
            skLineSegment(sketch, "E2406", {"start": v(-59.9, -9.1) * mm, "end": v(-59.86, -9.32) * mm});
            skLineSegment(sketch, "E2407", {"start": v(-59.86, -9.32) * mm, "end": v(-59.82, -9.54) * mm});
            skLineSegment(sketch, "E2408", {"start": v(-59.82, -9.54) * mm, "end": v(-59.79, -9.75) * mm});
            skLineSegment(sketch, "E2409", {"start": v(-59.79, -9.75) * mm, "end": v(-59.75, -9.97) * mm});
            skLineSegment(sketch, "E2410", {"start": v(-59.75, -9.97) * mm, "end": v(-59.7, -10.18) * mm});
            skLineSegment(sketch, "E2411", {"start": v(-59.7, -10.18) * mm, "end": v(-59.67, -10.4) * mm});
            skLineSegment(sketch, "E2412", {"start": v(-59.67, -10.4) * mm, "end": v(-59.63, -10.61) * mm});
            skLineSegment(sketch, "E2413", {"start": v(-59.63, -10.61) * mm, "end": v(-59.6, -10.82) * mm});
            skLineSegment(sketch, "E2414", {"start": v(-59.6, -10.82) * mm, "end": v(-59.56, -11.04) * mm});
            skLineSegment(sketch, "E2415", {"start": v(-59.56, -11.04) * mm, "end": v(-59.52, -11.25) * mm});
            skLineSegment(sketch, "E2416", {"start": v(-59.52, -11.25) * mm, "end": v(-59.48, -11.47) * mm});
            skLineSegment(sketch, "E2417", {"start": v(-59.48, -11.47) * mm, "end": v(-59.46, -11.57) * mm});
            skLineSegment(sketch, "E2418", {"start": v(-59.46, -11.57) * mm, "end": v(-59.68, -11.62) * mm});
            skLineSegment(sketch, "E2419", {"start": v(-59.68, -11.62) * mm, "end": v(-59.9, -11.66) * mm});
            skLineSegment(sketch, "E2420", {"start": v(-59.9, -11.66) * mm, "end": v(-60.11, -11.7) * mm});
            skLineSegment(sketch, "E2421", {"start": v(-60.11, -11.7) * mm, "end": v(-60.33, -11.74) * mm});
            skLineSegment(sketch, "E2422", {"start": v(-60.33, -11.74) * mm, "end": v(-60.54, -11.79) * mm});
            skLineSegment(sketch, "E2423", {"start": v(-60.54, -11.79) * mm, "end": v(-60.76, -11.83) * mm});
            skLineSegment(sketch, "E2424", {"start": v(-60.76, -11.83) * mm, "end": v(-60.97, -11.87) * mm});
            skLineSegment(sketch, "E2425", {"start": v(-60.97, -11.87) * mm, "end": v(-61.19, -11.91) * mm});
            skLineSegment(sketch, "E2426", {"start": v(-61.19, -11.91) * mm, "end": v(-61.4, -11.96) * mm});
            skLineSegment(sketch, "E2427", {"start": v(-61.4, -11.96) * mm, "end": v(-61.62, -12) * mm});
            skLineSegment(sketch, "E2428", {"start": v(-61.62, -12) * mm, "end": v(-61.83, -12.04) * mm});
            skLineSegment(sketch, "E2429", {"start": v(-61.83, -12.04) * mm, "end": v(-62.05, -12.09) * mm});
            skLineSegment(sketch, "E2430", {"start": v(-62.05, -12.09) * mm, "end": v(-62.28, -12.13) * mm});
            skLineSegment(sketch, "E2431", {"start": v(-62.28, -12.13) * mm, "end": v(-62.5, -12.22) * mm});
            skLineSegment(sketch, "E2432", {"start": v(-62.5, -12.22) * mm, "end": v(-62.67, -12.36) * mm});
            skLineSegment(sketch, "E2433", {"start": v(-62.67, -12.36) * mm, "end": v(-62.81, -12.54) * mm});
            skLineSegment(sketch, "E2434", {"start": v(-62.81, -12.54) * mm, "end": v(-62.9, -12.75) * mm});
            skLineSegment(sketch, "E2435", {"start": v(-62.9, -12.75) * mm, "end": v(-62.93, -12.97) * mm});
            skLineSegment(sketch, "E2436", {"start": v(-62.93, -12.97) * mm, "end": v(-62.9, -13.2) * mm});
            skLineSegment(sketch, "E2437", {"start": v(-62.9, -13.2) * mm, "end": v(-62.81, -13.4) * mm});
            skLineSegment(sketch, "E2438", {"start": v(-62.81, -13.4) * mm, "end": v(-62.68, -13.59) * mm});
            skLineSegment(sketch, "E2439", {"start": v(-62.68, -13.59) * mm, "end": v(-62.5, -13.72) * mm});
            skLineSegment(sketch, "E2440", {"start": v(-62.5, -13.72) * mm, "end": v(-62.28, -13.81) * mm});
            skLineSegment(sketch, "E2441", {"start": v(-62.28, -13.81) * mm, "end": v(-62.06, -13.84) * mm});
            skLineSegment(sketch, "E2442", {"start": v(-62.06, -13.84) * mm, "end": v(-61.84, -13.8) * mm});
            skLineSegment(sketch, "E2443", {"start": v(-61.84, -13.8) * mm, "end": v(-61.63, -13.76) * mm});
            skLineSegment(sketch, "E2444", {"start": v(-61.63, -13.76) * mm, "end": v(-61.42, -13.71) * mm});
            skLineSegment(sketch, "E2445", {"start": v(-61.42, -13.71) * mm, "end": v(-61.2, -13.67) * mm});
            skLineSegment(sketch, "E2446", {"start": v(-61.2, -13.67) * mm, "end": v(-61, -13.62) * mm});
            skLineSegment(sketch, "E2447", {"start": v(-61, -13.62) * mm, "end": v(-60.77, -13.57) * mm});
            skLineSegment(sketch, "E2448", {"start": v(-60.77, -13.57) * mm, "end": v(-60.56, -13.52) * mm});
            skLineSegment(sketch, "E2449", {"start": v(-60.56, -13.52) * mm, "end": v(-60.35, -13.47) * mm});
            skLineSegment(sketch, "E2450", {"start": v(-60.35, -13.47) * mm, "end": v(-60.13, -13.42) * mm});
            skLineSegment(sketch, "E2451", {"start": v(-60.13, -13.42) * mm, "end": v(-59.92, -13.37) * mm});
            skLineSegment(sketch, "E2452", {"start": v(-59.92, -13.37) * mm, "end": v(-59.7, -13.33) * mm});
            skLineSegment(sketch, "E2453", {"start": v(-59.7, -13.33) * mm, "end": v(-59.49, -13.28) * mm});
            skLineSegment(sketch, "E2454", {"start": v(-59.49, -13.28) * mm, "end": v(-59.28, -13.23) * mm});
            skLineSegment(sketch, "E2455", {"start": v(-59.28, -13.23) * mm, "end": v(-59.12, -13.2) * mm});
            skLineSegment(sketch, "E2456", {"start": v(-59.12, -13.2) * mm, "end": v(-59.07, -13.4) * mm});
            skLineSegment(sketch, "E2457", {"start": v(-59.07, -13.4) * mm, "end": v(-59.01, -13.62) * mm});
            skLineSegment(sketch, "E2458", {"start": v(-59.01, -13.62) * mm, "end": v(-58.96, -13.83) * mm});
            skLineSegment(sketch, "E2459", {"start": v(-58.96, -13.83) * mm, "end": v(-58.9, -14.04) * mm});
            skLineSegment(sketch, "E2460", {"start": v(-58.9, -14.04) * mm, "end": v(-58.86, -14.25) * mm});
            skLineSegment(sketch, "E2461", {"start": v(-58.86, -14.25) * mm, "end": v(-58.8, -14.46) * mm});
            skLineSegment(sketch, "E2462", {"start": v(-58.8, -14.46) * mm, "end": v(-58.75, -14.67) * mm});
            skLineSegment(sketch, "E2463", {"start": v(-58.75, -14.67) * mm, "end": v(-58.7, -14.88) * mm});
            skLineSegment(sketch, "E2464", {"start": v(-58.7, -14.88) * mm, "end": v(-58.65, -15.1) * mm});
            skLineSegment(sketch, "E2465", {"start": v(-58.65, -15.1) * mm, "end": v(-58.6, -15.3) * mm});
            skLineSegment(sketch, "E2466", {"start": v(-58.6, -15.3) * mm, "end": v(-58.54, -15.52) * mm});
            skLineSegment(sketch, "E2467", {"start": v(-58.54, -15.52) * mm, "end": v(-58.51, -15.62) * mm});
            skLineSegment(sketch, "E2468", {"start": v(-58.51, -15.62) * mm, "end": v(-58.73, -15.68) * mm});
            skLineSegment(sketch, "E2469", {"start": v(-58.73, -15.68) * mm, "end": v(-58.94, -15.74) * mm});
            skLineSegment(sketch, "E2470", {"start": v(-58.94, -15.74) * mm, "end": v(-59.15, -15.8) * mm});
            skLineSegment(sketch, "E2471", {"start": v(-59.15, -15.8) * mm, "end": v(-59.36, -15.85) * mm});
            skLineSegment(sketch, "E2472", {"start": v(-59.36, -15.85) * mm, "end": v(-59.57, -15.9) * mm});
            skLineSegment(sketch, "E2473", {"start": v(-59.57, -15.9) * mm, "end": v(-59.79, -15.97) * mm});
            skLineSegment(sketch, "E2474", {"start": v(-59.79, -15.97) * mm, "end": v(-60, -16.02) * mm});
            skLineSegment(sketch, "E2475", {"start": v(-60, -16.02) * mm, "end": v(-60.2, -16.08) * mm});
            skLineSegment(sketch, "E2476", {"start": v(-60.2, -16.08) * mm, "end": v(-60.42, -16.14) * mm});
            skLineSegment(sketch, "E2477", {"start": v(-60.42, -16.14) * mm, "end": v(-60.64, -16.2) * mm});
            skLineSegment(sketch, "E2478", {"start": v(-60.64, -16.2) * mm, "end": v(-60.85, -16.25) * mm});
            skLineSegment(sketch, "E2479", {"start": v(-60.85, -16.25) * mm, "end": v(-61.06, -16.31) * mm});
            skLineSegment(sketch, "E2480", {"start": v(-61.06, -16.31) * mm, "end": v(-61.29, -16.38) * mm});
            skLineSegment(sketch, "E2481", {"start": v(-61.29, -16.38) * mm, "end": v(-61.5, -16.48) * mm});
            skLineSegment(sketch, "E2482", {"start": v(-61.5, -16.48) * mm, "end": v(-61.66, -16.63) * mm});
            skLineSegment(sketch, "E2483", {"start": v(-61.66, -16.63) * mm, "end": v(-61.79, -16.81) * mm});
            skLineSegment(sketch, "E2484", {"start": v(-61.79, -16.81) * mm, "end": v(-61.86, -17.03) * mm});
            skLineSegment(sketch, "E2485", {"start": v(-61.86, -17.03) * mm, "end": v(-61.88, -17.26) * mm});
            skLineSegment(sketch, "E2486", {"start": v(-61.88, -17.26) * mm, "end": v(-61.83, -17.48) * mm});
            skLineSegment(sketch, "E2487", {"start": v(-61.83, -17.48) * mm, "end": v(-61.73, -17.68) * mm});
            skLineSegment(sketch, "E2488", {"start": v(-61.73, -17.68) * mm, "end": v(-61.58, -17.85) * mm});
            skLineSegment(sketch, "E2489", {"start": v(-61.58, -17.85) * mm, "end": v(-61.39, -17.98) * mm});
            skLineSegment(sketch, "E2490", {"start": v(-61.39, -17.98) * mm, "end": v(-61.17, -18.05) * mm});
            skLineSegment(sketch, "E2491", {"start": v(-61.17, -18.05) * mm, "end": v(-60.94, -18.06) * mm});
            skLineSegment(sketch, "E2492", {"start": v(-60.94, -18.06) * mm, "end": v(-60.73, -18.01) * mm});
            skLineSegment(sketch, "E2493", {"start": v(-60.73, -18.01) * mm, "end": v(-60.52, -17.96) * mm});
            skLineSegment(sketch, "E2494", {"start": v(-60.52, -17.96) * mm, "end": v(-60.31, -17.9) * mm});
            skLineSegment(sketch, "E2495", {"start": v(-60.31, -17.9) * mm, "end": v(-60.1, -17.83) * mm});
            skLineSegment(sketch, "E2496", {"start": v(-60.1, -17.83) * mm, "end": v(-59.9, -17.77) * mm});
            skLineSegment(sketch, "E2497", {"start": v(-59.9, -17.77) * mm, "end": v(-59.68, -17.7) * mm});
            skLineSegment(sketch, "E2498", {"start": v(-59.68, -17.7) * mm, "end": v(-59.47, -17.64) * mm});
            skLineSegment(sketch, "E2499", {"start": v(-59.47, -17.64) * mm, "end": v(-59.27, -17.58) * mm});
            skLineSegment(sketch, "E2500", {"start": v(-59.27, -17.58) * mm, "end": v(-59.05, -17.51) * mm});
            skLineSegment(sketch, "E2501", {"start": v(-59.05, -17.51) * mm, "end": v(-58.84, -17.45) * mm});
            skLineSegment(sketch, "E2502", {"start": v(-58.84, -17.45) * mm, "end": v(-58.63, -17.39) * mm});
            skLineSegment(sketch, "E2503", {"start": v(-58.63, -17.39) * mm, "end": v(-58.42, -17.32) * mm});
            skLineSegment(sketch, "E2504", {"start": v(-58.42, -17.32) * mm, "end": v(-58.21, -17.26) * mm});
            skLineSegment(sketch, "E2505", {"start": v(-58.21, -17.26) * mm, "end": v(-58.06, -17.21) * mm});
            skLineSegment(sketch, "E2506", {"start": v(-58.06, -17.21) * mm, "end": v(-58, -17.42) * mm});
            skLineSegment(sketch, "E2507", {"start": v(-58, -17.42) * mm, "end": v(-57.92, -17.63) * mm});
            skLineSegment(sketch, "E2508", {"start": v(-57.92, -17.63) * mm, "end": v(-57.86, -17.83) * mm});
            skLineSegment(sketch, "E2509", {"start": v(-57.86, -17.83) * mm, "end": v(-57.79, -18.04) * mm});
            skLineSegment(sketch, "E2510", {"start": v(-57.79, -18.04) * mm, "end": v(-57.72, -18.25) * mm});
            skLineSegment(sketch, "E2511", {"start": v(-57.72, -18.25) * mm, "end": v(-57.65, -18.46) * mm});
            skLineSegment(sketch, "E2512", {"start": v(-57.65, -18.46) * mm, "end": v(-57.59, -18.66) * mm});
            skLineSegment(sketch, "E2513", {"start": v(-57.59, -18.66) * mm, "end": v(-57.52, -18.87) * mm});
            skLineSegment(sketch, "E2514", {"start": v(-57.52, -18.87) * mm, "end": v(-57.45, -19.08) * mm});
            skLineSegment(sketch, "E2515", {"start": v(-57.45, -19.08) * mm, "end": v(-57.39, -19.28) * mm});
            skLineSegment(sketch, "E2516", {"start": v(-57.39, -19.28) * mm, "end": v(-57.32, -19.5) * mm});
            skLineSegment(sketch, "E2517", {"start": v(-57.32, -19.5) * mm, "end": v(-57.29, -19.6) * mm});
            skLineSegment(sketch, "E2518", {"start": v(-57.29, -19.6) * mm, "end": v(-57.5, -19.66) * mm});
            skLineSegment(sketch, "E2519", {"start": v(-57.5, -19.66) * mm, "end": v(-57.7, -19.74) * mm});
            skLineSegment(sketch, "E2520", {"start": v(-57.7, -19.74) * mm, "end": v(-57.9, -19.8) * mm});
            skLineSegment(sketch, "E2521", {"start": v(-57.9, -19.8) * mm, "end": v(-58.11, -19.88) * mm});
            skLineSegment(sketch, "E2522", {"start": v(-58.11, -19.88) * mm, "end": v(-58.32, -19.95) * mm});
            skLineSegment(sketch, "E2523", {"start": v(-58.32, -19.95) * mm, "end": v(-58.53, -20.03) * mm});
            skLineSegment(sketch, "E2524", {"start": v(-58.53, -20.03) * mm, "end": v(-58.74, -20.1) * mm});
            skLineSegment(sketch, "E2525", {"start": v(-58.74, -20.1) * mm, "end": v(-58.94, -20.17) * mm});
            skLineSegment(sketch, "E2526", {"start": v(-58.94, -20.17) * mm, "end": v(-59.15, -20.24) * mm});
            skLineSegment(sketch, "E2527", {"start": v(-59.15, -20.24) * mm, "end": v(-59.36, -20.32) * mm});
            skLineSegment(sketch, "E2528", {"start": v(-59.36, -20.32) * mm, "end": v(-59.57, -20.39) * mm});
            skLineSegment(sketch, "E2529", {"start": v(-59.57, -20.39) * mm, "end": v(-59.78, -20.46) * mm});
            skLineSegment(sketch, "E2530", {"start": v(-59.78, -20.46) * mm, "end": v(-60, -20.54) * mm});
            skLineSegment(sketch, "E2531", {"start": v(-60, -20.54) * mm, "end": v(-60.2, -20.65) * mm});
            skLineSegment(sketch, "E2532", {"start": v(-60.2, -20.65) * mm, "end": v(-60.35, -20.81) * mm});
            skLineSegment(sketch, "E2533", {"start": v(-60.35, -20.81) * mm, "end": v(-60.47, -21.01) * mm});
            skLineSegment(sketch, "E2534", {"start": v(-60.47, -21.01) * mm, "end": v(-60.52, -21.23) * mm});
            skLineSegment(sketch, "E2535", {"start": v(-60.52, -21.23) * mm, "end": v(-60.52, -21.46) * mm});
            skLineSegment(sketch, "E2536", {"start": v(-60.52, -21.46) * mm, "end": v(-60.46, -21.68) * mm});
            skLineSegment(sketch, "E2537", {"start": v(-60.46, -21.68) * mm, "end": v(-60.35, -21.87) * mm});
            skLineSegment(sketch, "E2538", {"start": v(-60.35, -21.87) * mm, "end": v(-60.18, -22.03) * mm});
            skLineSegment(sketch, "E2539", {"start": v(-60.18, -22.03) * mm, "end": v(-59.99, -22.14) * mm});
            skLineSegment(sketch, "E2540", {"start": v(-59.99, -22.14) * mm, "end": v(-59.77, -22.2) * mm});
            skLineSegment(sketch, "E2541", {"start": v(-59.77, -22.2) * mm, "end": v(-59.54, -22.2) * mm});
            skLineSegment(sketch, "E2542", {"start": v(-59.54, -22.2) * mm, "end": v(-59.33, -22.13) * mm});
            skLineSegment(sketch, "E2543", {"start": v(-59.33, -22.13) * mm, "end": v(-59.13, -22.06) * mm});
            skLineSegment(sketch, "E2544", {"start": v(-59.13, -22.06) * mm, "end": v(-58.92, -21.98) * mm});
            skLineSegment(sketch, "E2545", {"start": v(-58.92, -21.98) * mm, "end": v(-58.72, -21.9) * mm});
            skLineSegment(sketch, "E2546", {"start": v(-58.72, -21.9) * mm, "end": v(-58.51, -21.83) * mm});
            skLineSegment(sketch, "E2547", {"start": v(-58.51, -21.83) * mm, "end": v(-58.3, -21.75) * mm});
            skLineSegment(sketch, "E2548", {"start": v(-58.3, -21.75) * mm, "end": v(-58.1, -21.67) * mm});
            skLineSegment(sketch, "E2549", {"start": v(-58.1, -21.67) * mm, "end": v(-57.9, -21.6) * mm});
            skLineSegment(sketch, "E2550", {"start": v(-57.9, -21.6) * mm, "end": v(-57.69, -21.52) * mm});
            skLineSegment(sketch, "E2551", {"start": v(-57.69, -21.52) * mm, "end": v(-57.48, -21.44) * mm});
            skLineSegment(sketch, "E2552", {"start": v(-57.48, -21.44) * mm, "end": v(-57.28, -21.36) * mm});
            skLineSegment(sketch, "E2553", {"start": v(-57.28, -21.36) * mm, "end": v(-57.07, -21.28) * mm});
            skLineSegment(sketch, "E2554", {"start": v(-57.07, -21.28) * mm, "end": v(-56.87, -21.2) * mm});
            skLineSegment(sketch, "E2555", {"start": v(-56.87, -21.2) * mm, "end": v(-56.72, -21.15) * mm});
            skLineSegment(sketch, "E2556", {"start": v(-56.72, -21.15) * mm, "end": v(-56.64, -21.35) * mm});
            skLineSegment(sketch, "E2557", {"start": v(-56.64, -21.35) * mm, "end": v(-56.56, -21.55) * mm});
            skLineSegment(sketch, "E2558", {"start": v(-56.56, -21.55) * mm, "end": v(-56.47, -21.75) * mm});
            skLineSegment(sketch, "E2559", {"start": v(-56.47, -21.75) * mm, "end": v(-56.4, -21.96) * mm});
            skLineSegment(sketch, "E2560", {"start": v(-56.4, -21.96) * mm, "end": v(-56.31, -22.16) * mm});
            skLineSegment(sketch, "E2561", {"start": v(-56.31, -22.16) * mm, "end": v(-56.23, -22.36) * mm});
            skLineSegment(sketch, "E2562", {"start": v(-56.23, -22.36) * mm, "end": v(-56.15, -22.56) * mm});
            skLineSegment(sketch, "E2563", {"start": v(-56.15, -22.56) * mm, "end": v(-56.07, -22.76) * mm});
            skLineSegment(sketch, "E2564", {"start": v(-56.07, -22.76) * mm, "end": v(-55.98, -22.97) * mm});
            skLineSegment(sketch, "E2565", {"start": v(-55.98, -22.97) * mm, "end": v(-55.9, -23.17) * mm});
            skLineSegment(sketch, "E2566", {"start": v(-55.9, -23.17) * mm, "end": v(-55.82, -23.37) * mm});
            skLineSegment(sketch, "E2567", {"start": v(-55.82, -23.37) * mm, "end": v(-55.78, -23.47) * mm});
            skLineSegment(sketch, "E2568", {"start": v(-55.78, -23.47) * mm, "end": v(-55.98, -23.55) * mm});
            skLineSegment(sketch, "E2569", {"start": v(-55.98, -23.55) * mm, "end": v(-56.18, -23.64) * mm});
            skLineSegment(sketch, "E2570", {"start": v(-56.18, -23.64) * mm, "end": v(-56.39, -23.73) * mm});
            skLineSegment(sketch, "E2571", {"start": v(-56.39, -23.73) * mm, "end": v(-56.59, -23.81) * mm});
            skLineSegment(sketch, "E2572", {"start": v(-56.59, -23.81) * mm, "end": v(-56.79, -23.9) * mm});
            skLineSegment(sketch, "E2573", {"start": v(-56.79, -23.9) * mm, "end": v(-57, -23.99) * mm});
            skLineSegment(sketch, "E2574", {"start": v(-57, -23.99) * mm, "end": v(-57.2, -24.07) * mm});
            skLineSegment(sketch, "E2575", {"start": v(-57.2, -24.07) * mm, "end": v(-57.4, -24.16) * mm});
            skLineSegment(sketch, "E2576", {"start": v(-57.4, -24.16) * mm, "end": v(-57.6, -24.25) * mm});
            skLineSegment(sketch, "E2577", {"start": v(-57.6, -24.25) * mm, "end": v(-57.8, -24.33) * mm});
            skLineSegment(sketch, "E2578", {"start": v(-57.8, -24.33) * mm, "end": v(-58, -24.42) * mm});
            skLineSegment(sketch, "E2579", {"start": v(-58, -24.42) * mm, "end": v(-58.2, -24.5) * mm});
            skLineSegment(sketch, "E2580", {"start": v(-58.2, -24.5) * mm, "end": v(-58.42, -24.6) * mm});
            skLineSegment(sketch, "E2581", {"start": v(-58.42, -24.6) * mm, "end": v(-58.6, -24.73) * mm});
            skLineSegment(sketch, "E2582", {"start": v(-58.6, -24.73) * mm, "end": v(-58.76, -24.9) * mm});
            skLineSegment(sketch, "E2583", {"start": v(-58.76, -24.9) * mm, "end": v(-58.86, -25.1) * mm});
            skLineSegment(sketch, "E2584", {"start": v(-58.86, -25.1) * mm, "end": v(-58.9, -25.33) * mm});
            skLineSegment(sketch, "E2585", {"start": v(-58.9, -25.33) * mm, "end": v(-58.88, -25.56) * mm});
            skLineSegment(sketch, "E2586", {"start": v(-58.88, -25.56) * mm, "end": v(-58.8, -25.77) * mm});
            skLineSegment(sketch, "E2587", {"start": v(-58.8, -25.77) * mm, "end": v(-58.68, -25.96) * mm});
            skLineSegment(sketch, "E2588", {"start": v(-58.68, -25.96) * mm, "end": v(-58.5, -26.1) * mm});
            skLineSegment(sketch, "E2589", {"start": v(-58.5, -26.1) * mm, "end": v(-58.3, -26.2) * mm});
            skLineSegment(sketch, "E2590", {"start": v(-58.3, -26.2) * mm, "end": v(-58.07, -26.24) * mm});
            skLineSegment(sketch, "E2591", {"start": v(-58.07, -26.24) * mm, "end": v(-57.85, -26.22) * mm});
            skLineSegment(sketch, "E2592", {"start": v(-57.85, -26.22) * mm, "end": v(-57.64, -26.15) * mm});
            skLineSegment(sketch, "E2593", {"start": v(-57.64, -26.15) * mm, "end": v(-57.44, -26.06) * mm});
            skLineSegment(sketch, "E2594", {"start": v(-57.44, -26.06) * mm, "end": v(-57.25, -25.97) * mm});
            skLineSegment(sketch, "E2595", {"start": v(-57.25, -25.97) * mm, "end": v(-57.05, -25.88) * mm});
            skLineSegment(sketch, "E2596", {"start": v(-57.05, -25.88) * mm, "end": v(-56.85, -25.79) * mm});
            skLineSegment(sketch, "E2597", {"start": v(-56.85, -25.79) * mm, "end": v(-56.65, -25.7) * mm});
            skLineSegment(sketch, "E2598", {"start": v(-56.65, -25.7) * mm, "end": v(-56.45, -25.6) * mm});
            skLineSegment(sketch, "E2599", {"start": v(-56.45, -25.6) * mm, "end": v(-56.25, -25.5) * mm});
            skLineSegment(sketch, "E2600", {"start": v(-56.25, -25.5) * mm, "end": v(-56.05, -25.42) * mm});
            skLineSegment(sketch, "E2601", {"start": v(-56.05, -25.42) * mm, "end": v(-55.85, -25.32) * mm});
            skLineSegment(sketch, "E2602", {"start": v(-55.85, -25.32) * mm, "end": v(-55.65, -25.23) * mm});
            skLineSegment(sketch, "E2603", {"start": v(-55.65, -25.23) * mm, "end": v(-55.45, -25.14) * mm});
            skLineSegment(sketch, "E2604", {"start": v(-55.45, -25.14) * mm, "end": v(-55.25, -25.05) * mm});
            skLineSegment(sketch, "E2605", {"start": v(-55.25, -25.05) * mm, "end": v(-55.1, -24.98) * mm});
            skLineSegment(sketch, "E2606", {"start": v(-55.1, -24.98) * mm, "end": v(-55.01, -25.18) * mm});
            skLineSegment(sketch, "E2607", {"start": v(-55.01, -25.18) * mm, "end": v(-54.92, -25.37) * mm});
            skLineSegment(sketch, "E2608", {"start": v(-54.92, -25.37) * mm, "end": v(-54.82, -25.57) * mm});
            skLineSegment(sketch, "E2609", {"start": v(-54.82, -25.57) * mm, "end": v(-54.73, -25.76) * mm});
            skLineSegment(sketch, "E2610", {"start": v(-54.73, -25.76) * mm, "end": v(-54.63, -25.96) * mm});
            skLineSegment(sketch, "E2611", {"start": v(-54.63, -25.96) * mm, "end": v(-54.54, -26.16) * mm});
            skLineSegment(sketch, "E2612", {"start": v(-54.54, -26.16) * mm, "end": v(-54.44, -26.35) * mm});
            skLineSegment(sketch, "E2613", {"start": v(-54.44, -26.35) * mm, "end": v(-54.34, -26.55) * mm});
            skLineSegment(sketch, "E2614", {"start": v(-54.34, -26.55) * mm, "end": v(-54.25, -26.74) * mm});
            skLineSegment(sketch, "E2615", {"start": v(-54.25, -26.74) * mm, "end": v(-54.15, -26.94) * mm});
            skLineSegment(sketch, "E2616", {"start": v(-54.15, -26.94) * mm, "end": v(-54.06, -27.13) * mm});
            skLineSegment(sketch, "E2617", {"start": v(-54.06, -27.13) * mm, "end": v(-54.01, -27.23) * mm});
            skLineSegment(sketch, "E2618", {"start": v(-54.01, -27.23) * mm, "end": v(-54.2, -27.33) * mm});
            skLineSegment(sketch, "E2619", {"start": v(-54.2, -27.33) * mm, "end": v(-54.4, -27.43) * mm});
            skLineSegment(sketch, "E2620", {"start": v(-54.4, -27.43) * mm, "end": v(-54.6, -27.53) * mm});
            skLineSegment(sketch, "E2621", {"start": v(-54.6, -27.53) * mm, "end": v(-54.8, -27.63) * mm});
            skLineSegment(sketch, "E2622", {"start": v(-54.8, -27.63) * mm, "end": v(-54.99, -27.73) * mm});
            skLineSegment(sketch, "E2623", {"start": v(-54.99, -27.73) * mm, "end": v(-55.18, -27.83) * mm});
            skLineSegment(sketch, "E2624", {"start": v(-55.18, -27.83) * mm, "end": v(-55.38, -27.93) * mm});
            skLineSegment(sketch, "E2625", {"start": v(-55.38, -27.93) * mm, "end": v(-55.57, -28.03) * mm});
            skLineSegment(sketch, "E2626", {"start": v(-55.57, -28.03) * mm, "end": v(-55.77, -28.14) * mm});
            skLineSegment(sketch, "E2627", {"start": v(-55.77, -28.14) * mm, "end": v(-55.97, -28.23) * mm});
            skLineSegment(sketch, "E2628", {"start": v(-55.97, -28.23) * mm, "end": v(-56.16, -28.33) * mm});
            skLineSegment(sketch, "E2629", {"start": v(-56.16, -28.33) * mm, "end": v(-56.36, -28.44) * mm});
            skLineSegment(sketch, "E2630", {"start": v(-56.36, -28.44) * mm, "end": v(-56.57, -28.55) * mm});
            skLineSegment(sketch, "E2631", {"start": v(-56.57, -28.55) * mm, "end": v(-56.74, -28.69) * mm});
            skLineSegment(sketch, "E2632", {"start": v(-56.74, -28.69) * mm, "end": v(-56.88, -28.87) * mm});
            skLineSegment(sketch, "E2633", {"start": v(-56.88, -28.87) * mm, "end": v(-56.96, -29.08) * mm});
            skLineSegment(sketch, "E2634", {"start": v(-56.96, -29.08) * mm, "end": v(-57, -29.3) * mm});
            skLineSegment(sketch, "E2635", {"start": v(-57, -29.3) * mm, "end": v(-56.96, -29.53) * mm});
            skLineSegment(sketch, "E2636", {"start": v(-56.96, -29.53) * mm, "end": v(-56.87, -29.74) * mm});
            skLineSegment(sketch, "E2637", {"start": v(-56.87, -29.74) * mm, "end": v(-56.73, -29.92) * mm});
            skLineSegment(sketch, "E2638", {"start": v(-56.73, -29.92) * mm, "end": v(-56.54, -30.05) * mm});
            skLineSegment(sketch, "E2639", {"start": v(-56.54, -30.05) * mm, "end": v(-56.33, -30.13) * mm});
            skLineSegment(sketch, "E2640", {"start": v(-56.33, -30.13) * mm, "end": v(-56.1, -30.16) * mm});
            skLineSegment(sketch, "E2641", {"start": v(-56.1, -30.16) * mm, "end": v(-55.88, -30.12) * mm});
            skLineSegment(sketch, "E2642", {"start": v(-55.88, -30.12) * mm, "end": v(-55.68, -30.03) * mm});
            skLineSegment(sketch, "E2643", {"start": v(-55.68, -30.03) * mm, "end": v(-55.49, -29.93) * mm});
            skLineSegment(sketch, "E2644", {"start": v(-55.49, -29.93) * mm, "end": v(-55.3, -29.83) * mm});
            skLineSegment(sketch, "E2645", {"start": v(-55.3, -29.83) * mm, "end": v(-55.1, -29.72) * mm});
            skLineSegment(sketch, "E2646", {"start": v(-55.1, -29.72) * mm, "end": v(-54.92, -29.62) * mm});
            skLineSegment(sketch, "E2647", {"start": v(-54.92, -29.62) * mm, "end": v(-54.72, -29.5) * mm});
            skLineSegment(sketch, "E2648", {"start": v(-54.72, -29.5) * mm, "end": v(-54.53, -29.4) * mm});
            skLineSegment(sketch, "E2649", {"start": v(-54.53, -29.4) * mm, "end": v(-54.34, -29.3) * mm});
            skLineSegment(sketch, "E2650", {"start": v(-54.34, -29.3) * mm, "end": v(-54.14, -29.2) * mm});
            skLineSegment(sketch, "E2651", {"start": v(-54.14, -29.2) * mm, "end": v(-53.95, -29.09) * mm});
            skLineSegment(sketch, "E2652", {"start": v(-53.95, -29.09) * mm, "end": v(-53.76, -28.98) * mm});
            skLineSegment(sketch, "E2653", {"start": v(-53.76, -28.98) * mm, "end": v(-53.56, -28.87) * mm});
            skLineSegment(sketch, "E2654", {"start": v(-53.56, -28.87) * mm, "end": v(-53.37, -28.77) * mm});
            skLineSegment(sketch, "E2655", {"start": v(-53.37, -28.77) * mm, "end": v(-53.23, -28.7) * mm});
            skLineSegment(sketch, "E2656", {"start": v(-53.23, -28.7) * mm, "end": v(-53.12, -28.88) * mm});
            skLineSegment(sketch, "E2657", {"start": v(-53.12, -28.88) * mm, "end": v(-53.02, -29.07) * mm});
            skLineSegment(sketch, "E2658", {"start": v(-53.02, -29.07) * mm, "end": v(-52.9, -29.26) * mm});
            skLineSegment(sketch, "E2659", {"start": v(-52.9, -29.26) * mm, "end": v(-52.8, -29.45) * mm});
            skLineSegment(sketch, "E2660", {"start": v(-52.8, -29.45) * mm, "end": v(-52.69, -29.64) * mm});
            skLineSegment(sketch, "E2661", {"start": v(-52.69, -29.64) * mm, "end": v(-52.58, -29.82) * mm});
            skLineSegment(sketch, "E2662", {"start": v(-52.58, -29.82) * mm, "end": v(-52.47, -30.01) * mm});
            skLineSegment(sketch, "E2663", {"start": v(-52.47, -30.01) * mm, "end": v(-52.36, -30.2) * mm});
            skLineSegment(sketch, "E2664", {"start": v(-52.36, -30.2) * mm, "end": v(-52.25, -30.39) * mm});
            skLineSegment(sketch, "E2665", {"start": v(-52.25, -30.39) * mm, "end": v(-52.14, -30.58) * mm});
            skLineSegment(sketch, "E2666", {"start": v(-52.14, -30.58) * mm, "end": v(-52.04, -30.77) * mm});
            skLineSegment(sketch, "E2667", {"start": v(-52.04, -30.77) * mm, "end": v(-51.98, -30.86) * mm});
            skLineSegment(sketch, "E2668", {"start": v(-51.98, -30.86) * mm, "end": v(-52.17, -30.97) * mm});
            skLineSegment(sketch, "E2669", {"start": v(-52.17, -30.97) * mm, "end": v(-52.36, -31.08) * mm});
            skLineSegment(sketch, "E2670", {"start": v(-52.36, -31.08) * mm, "end": v(-52.55, -31.2) * mm});
            skLineSegment(sketch, "E2671", {"start": v(-52.55, -31.2) * mm, "end": v(-52.73, -31.31) * mm});
            skLineSegment(sketch, "E2672", {"start": v(-52.73, -31.31) * mm, "end": v(-52.92, -31.43) * mm});
            skLineSegment(sketch, "E2673", {"start": v(-52.92, -31.43) * mm, "end": v(-53.11, -31.54) * mm});
            skLineSegment(sketch, "E2674", {"start": v(-53.11, -31.54) * mm, "end": v(-53.3, -31.66) * mm});
            skLineSegment(sketch, "E2675", {"start": v(-53.3, -31.66) * mm, "end": v(-53.48, -31.77) * mm});
            skLineSegment(sketch, "E2676", {"start": v(-53.48, -31.77) * mm, "end": v(-53.68, -31.88) * mm});
            skLineSegment(sketch, "E2677", {"start": v(-53.68, -31.88) * mm, "end": v(-53.86, -32) * mm});
            skLineSegment(sketch, "E2678", {"start": v(-53.86, -32) * mm, "end": v(-54.05, -32.11) * mm});
            skLineSegment(sketch, "E2679", {"start": v(-54.05, -32.11) * mm, "end": v(-54.24, -32.23) * mm});
            skLineSegment(sketch, "E2680", {"start": v(-54.24, -32.23) * mm, "end": v(-54.44, -32.35) * mm});
            skLineSegment(sketch, "E2681", {"start": v(-54.44, -32.35) * mm, "end": v(-54.6, -32.5) * mm});
            skLineSegment(sketch, "E2682", {"start": v(-54.6, -32.5) * mm, "end": v(-54.73, -32.7) * mm});
            skLineSegment(sketch, "E2683", {"start": v(-54.73, -32.7) * mm, "end": v(-54.8, -32.9) * mm});
            skLineSegment(sketch, "E2684", {"start": v(-54.8, -32.9) * mm, "end": v(-54.81, -33.14) * mm});
            skLineSegment(sketch, "E2685", {"start": v(-54.81, -33.14) * mm, "end": v(-54.76, -33.36) * mm});
            skLineSegment(sketch, "E2686", {"start": v(-54.76, -33.36) * mm, "end": v(-54.66, -33.56) * mm});
            skLineSegment(sketch, "E2687", {"start": v(-54.66, -33.56) * mm, "end": v(-54.5, -33.73) * mm});
            skLineSegment(sketch, "E2688", {"start": v(-54.5, -33.73) * mm, "end": v(-54.31, -33.85) * mm});
            skLineSegment(sketch, "E2689", {"start": v(-54.31, -33.85) * mm, "end": v(-54.1, -33.92) * mm});
            skLineSegment(sketch, "E2690", {"start": v(-54.1, -33.92) * mm, "end": v(-53.87, -33.93) * mm});
            skLineSegment(sketch, "E2691", {"start": v(-53.87, -33.93) * mm, "end": v(-53.65, -33.88) * mm});
            skLineSegment(sketch, "E2692", {"start": v(-53.65, -33.88) * mm, "end": v(-53.45, -33.77) * mm});
            skLineSegment(sketch, "E2693", {"start": v(-53.45, -33.77) * mm, "end": v(-53.27, -33.66) * mm});
            skLineSegment(sketch, "E2694", {"start": v(-53.27, -33.66) * mm, "end": v(-53.09, -33.54) * mm});
            skLineSegment(sketch, "E2695", {"start": v(-53.09, -33.54) * mm, "end": v(-52.9, -33.42) * mm});
            skLineSegment(sketch, "E2696", {"start": v(-52.9, -33.42) * mm, "end": v(-52.72, -33.3) * mm});
            skLineSegment(sketch, "E2697", {"start": v(-52.72, -33.3) * mm, "end": v(-52.53, -33.18) * mm});
            skLineSegment(sketch, "E2698", {"start": v(-52.53, -33.18) * mm, "end": v(-52.35, -33.06) * mm});
            skLineSegment(sketch, "E2699", {"start": v(-52.35, -33.06) * mm, "end": v(-52.17, -32.95) * mm});
            skLineSegment(sketch, "E2700", {"start": v(-52.17, -32.95) * mm, "end": v(-51.98, -32.82) * mm});
            skLineSegment(sketch, "E2701", {"start": v(-51.98, -32.82) * mm, "end": v(-51.8, -32.7) * mm});
            skLineSegment(sketch, "E2702", {"start": v(-51.8, -32.7) * mm, "end": v(-51.61, -32.59) * mm});
            skLineSegment(sketch, "E2703", {"start": v(-51.61, -32.59) * mm, "end": v(-51.42, -32.47) * mm});
            skLineSegment(sketch, "E2704", {"start": v(-51.42, -32.47) * mm, "end": v(-51.24, -32.35) * mm});
            skLineSegment(sketch, "E2705", {"start": v(-51.24, -32.35) * mm, "end": v(-51.1, -32.26) * mm});
            skLineSegment(sketch, "E2706", {"start": v(-51.1, -32.26) * mm, "end": v(-50.98, -32.44) * mm});
            skLineSegment(sketch, "E2707", {"start": v(-50.98, -32.44) * mm, "end": v(-50.86, -32.62) * mm});
            skLineSegment(sketch, "E2708", {"start": v(-50.86, -32.62) * mm, "end": v(-50.74, -32.8) * mm});
            skLineSegment(sketch, "E2709", {"start": v(-50.74, -32.8) * mm, "end": v(-50.62, -32.99) * mm});
            skLineSegment(sketch, "E2710", {"start": v(-50.62, -32.99) * mm, "end": v(-50.5, -33.17) * mm});
            skLineSegment(sketch, "E2711", {"start": v(-50.5, -33.17) * mm, "end": v(-50.37, -33.35) * mm});
            skLineSegment(sketch, "E2712", {"start": v(-50.37, -33.35) * mm, "end": v(-50.25, -33.53) * mm});
            skLineSegment(sketch, "E2713", {"start": v(-50.25, -33.53) * mm, "end": v(-50.13, -33.7) * mm});
            skLineSegment(sketch, "E2714", {"start": v(-50.13, -33.7) * mm, "end": v(-50, -33.89) * mm});
            skLineSegment(sketch, "E2715", {"start": v(-50, -33.89) * mm, "end": v(-49.89, -34.07) * mm});
            skLineSegment(sketch, "E2716", {"start": v(-49.89, -34.07) * mm, "end": v(-49.77, -34.25) * mm});
            skLineSegment(sketch, "E2717", {"start": v(-49.77, -34.25) * mm, "end": v(-49.7, -34.34) * mm});
            skLineSegment(sketch, "E2718", {"start": v(-49.7, -34.34) * mm, "end": v(-49.88, -34.46) * mm});
            skLineSegment(sketch, "E2719", {"start": v(-49.88, -34.46) * mm, "end": v(-50.06, -34.59) * mm});
            skLineSegment(sketch, "E2720", {"start": v(-50.06, -34.59) * mm, "end": v(-50.24, -34.72) * mm});
            skLineSegment(sketch, "E2721", {"start": v(-50.24, -34.72) * mm, "end": v(-50.42, -34.84) * mm});
            skLineSegment(sketch, "E2722", {"start": v(-50.42, -34.84) * mm, "end": v(-50.6, -34.97) * mm});
            skLineSegment(sketch, "E2723", {"start": v(-50.6, -34.97) * mm, "end": v(-50.78, -35.1) * mm});
            skLineSegment(sketch, "E2724", {"start": v(-50.78, -35.1) * mm, "end": v(-50.96, -35.22) * mm});
            skLineSegment(sketch, "E2725", {"start": v(-50.96, -35.22) * mm, "end": v(-51.14, -35.35) * mm});
            skLineSegment(sketch, "E2726", {"start": v(-51.14, -35.35) * mm, "end": v(-51.32, -35.48) * mm});
            skLineSegment(sketch, "E2727", {"start": v(-51.32, -35.48) * mm, "end": v(-51.5, -35.6) * mm});
            skLineSegment(sketch, "E2728", {"start": v(-51.5, -35.6) * mm, "end": v(-51.68, -35.73) * mm});
            skLineSegment(sketch, "E2729", {"start": v(-51.68, -35.73) * mm, "end": v(-51.86, -35.86) * mm});
            skLineSegment(sketch, "E2730", {"start": v(-51.86, -35.86) * mm, "end": v(-52.05, -36) * mm});
            skLineSegment(sketch, "E2731", {"start": v(-52.05, -36) * mm, "end": v(-52.21, -36.16) * mm});
            skLineSegment(sketch, "E2732", {"start": v(-52.21, -36.16) * mm, "end": v(-52.32, -36.36) * mm});
            skLineSegment(sketch, "E2733", {"start": v(-52.32, -36.36) * mm, "end": v(-52.37, -36.58) * mm});
            skLineSegment(sketch, "E2734", {"start": v(-52.37, -36.58) * mm, "end": v(-52.37, -36.8) * mm});
            skLineSegment(sketch, "E2735", {"start": v(-52.37, -36.8) * mm, "end": v(-52.3, -37.02) * mm});
            skLineSegment(sketch, "E2736", {"start": v(-52.3, -37.02) * mm, "end": v(-52.18, -37.22) * mm});
            skLineSegment(sketch, "E2737", {"start": v(-52.18, -37.22) * mm, "end": v(-52.02, -37.37) * mm});
            skLineSegment(sketch, "E2738", {"start": v(-52.02, -37.37) * mm, "end": v(-51.82, -37.48) * mm});
            skLineSegment(sketch, "E2739", {"start": v(-51.82, -37.48) * mm, "end": v(-51.6, -37.54) * mm});
            skLineSegment(sketch, "E2740", {"start": v(-51.6, -37.54) * mm, "end": v(-51.37, -37.53) * mm});
            skLineSegment(sketch, "E2741", {"start": v(-51.37, -37.53) * mm, "end": v(-51.15, -37.46) * mm});
            skLineSegment(sketch, "E2742", {"start": v(-51.15, -37.46) * mm, "end": v(-50.97, -37.35) * mm});
            skLineSegment(sketch, "E2743", {"start": v(-50.97, -37.35) * mm, "end": v(-50.8, -37.22) * mm});
            skLineSegment(sketch, "E2744", {"start": v(-50.8, -37.22) * mm, "end": v(-50.62, -37.09) * mm});
            skLineSegment(sketch, "E2745", {"start": v(-50.62, -37.09) * mm, "end": v(-50.45, -36.96) * mm});
            skLineSegment(sketch, "E2746", {"start": v(-50.45, -36.96) * mm, "end": v(-50.27, -36.83) * mm});
            skLineSegment(sketch, "E2747", {"start": v(-50.27, -36.83) * mm, "end": v(-50.1, -36.7) * mm});
            skLineSegment(sketch, "E2748", {"start": v(-50.1, -36.7) * mm, "end": v(-49.92, -36.56) * mm});
            skLineSegment(sketch, "E2749", {"start": v(-49.92, -36.56) * mm, "end": v(-49.74, -36.43) * mm});
            skLineSegment(sketch, "E2750", {"start": v(-49.74, -36.43) * mm, "end": v(-49.56, -36.3) * mm});
            skLineSegment(sketch, "E2751", {"start": v(-49.56, -36.3) * mm, "end": v(-49.39, -36.17) * mm});
            skLineSegment(sketch, "E2752", {"start": v(-49.39, -36.17) * mm, "end": v(-49.21, -36.04) * mm});
            skLineSegment(sketch, "E2753", {"start": v(-49.21, -36.04) * mm, "end": v(-49.03, -35.9) * mm});
            skLineSegment(sketch, "E2754", {"start": v(-49.03, -35.9) * mm, "end": v(-48.86, -35.77) * mm});
            skLineSegment(sketch, "E2755", {"start": v(-48.86, -35.77) * mm, "end": v(-48.73, -35.68) * mm});
            skLineSegment(sketch, "E2756", {"start": v(-48.73, -35.68) * mm, "end": v(-48.6, -35.85) * mm});
            skLineSegment(sketch, "E2757", {"start": v(-48.6, -35.85) * mm, "end": v(-48.46, -36.02) * mm});
            skLineSegment(sketch, "E2758", {"start": v(-48.46, -36.02) * mm, "end": v(-48.33, -36.2) * mm});
            skLineSegment(sketch, "E2759", {"start": v(-48.33, -36.2) * mm, "end": v(-48.2, -36.36) * mm});
            skLineSegment(sketch, "E2760", {"start": v(-48.2, -36.36) * mm, "end": v(-48.06, -36.54) * mm});
            skLineSegment(sketch, "E2761", {"start": v(-48.06, -36.54) * mm, "end": v(-47.93, -36.7) * mm});
            skLineSegment(sketch, "E2762", {"start": v(-47.93, -36.7) * mm, "end": v(-47.8, -36.88) * mm});
            skLineSegment(sketch, "E2763", {"start": v(-47.8, -36.88) * mm, "end": v(-47.66, -37.05) * mm});
            skLineSegment(sketch, "E2764", {"start": v(-47.66, -37.05) * mm, "end": v(-47.53, -37.22) * mm});
            skLineSegment(sketch, "E2765", {"start": v(-47.53, -37.22) * mm, "end": v(-47.4, -37.4) * mm});
            skLineSegment(sketch, "E2766", {"start": v(-47.4, -37.4) * mm, "end": v(-47.26, -37.57) * mm});
            skLineSegment(sketch, "E2767", {"start": v(-47.26, -37.57) * mm, "end": v(-47.2, -37.65) * mm});
            skLineSegment(sketch, "E2768", {"start": v(-47.2, -37.65) * mm, "end": v(-47.36, -37.79) * mm});
            skLineSegment(sketch, "E2769", {"start": v(-47.36, -37.79) * mm, "end": v(-47.53, -37.92) * mm});
            skLineSegment(sketch, "E2770", {"start": v(-47.53, -37.92) * mm, "end": v(-47.7, -38.07) * mm});
            skLineSegment(sketch, "E2771", {"start": v(-47.7, -38.07) * mm, "end": v(-47.87, -38.2) * mm});
            skLineSegment(sketch, "E2772", {"start": v(-47.87, -38.2) * mm, "end": v(-48.04, -38.34) * mm});
            skLineSegment(sketch, "E2773", {"start": v(-48.04, -38.34) * mm, "end": v(-48.21, -38.48) * mm});
            skLineSegment(sketch, "E2774", {"start": v(-48.21, -38.48) * mm, "end": v(-48.38, -38.62) * mm});
            skLineSegment(sketch, "E2775", {"start": v(-48.38, -38.62) * mm, "end": v(-48.55, -38.76) * mm});
            skLineSegment(sketch, "E2776", {"start": v(-48.55, -38.76) * mm, "end": v(-48.73, -38.9) * mm});
            skLineSegment(sketch, "E2777", {"start": v(-48.73, -38.9) * mm, "end": v(-48.9, -39.04) * mm});
            skLineSegment(sketch, "E2778", {"start": v(-48.9, -39.04) * mm, "end": v(-49.06, -39.18) * mm});
            skLineSegment(sketch, "E2779", {"start": v(-49.06, -39.18) * mm, "end": v(-49.24, -39.32) * mm});
            skLineSegment(sketch, "E2780", {"start": v(-49.24, -39.32) * mm, "end": v(-49.42, -39.47) * mm});
            skLineSegment(sketch, "E2781", {"start": v(-49.42, -39.47) * mm, "end": v(-49.56, -39.64) * mm});
            skLineSegment(sketch, "E2782", {"start": v(-49.56, -39.64) * mm, "end": v(-49.66, -39.85) * mm});
            skLineSegment(sketch, "E2783", {"start": v(-49.66, -39.85) * mm, "end": v(-49.7, -40.07) * mm});
            skLineSegment(sketch, "E2784", {"start": v(-49.7, -40.07) * mm, "end": v(-49.68, -40.3) * mm});
            skLineSegment(sketch, "E2785", {"start": v(-49.68, -40.3) * mm, "end": v(-49.6, -40.51) * mm});
            skLineSegment(sketch, "E2786", {"start": v(-49.6, -40.51) * mm, "end": v(-49.46, -40.7) * mm});
            skLineSegment(sketch, "E2787", {"start": v(-49.46, -40.7) * mm, "end": v(-49.29, -40.84) * mm});
            skLineSegment(sketch, "E2788", {"start": v(-49.29, -40.84) * mm, "end": v(-49.08, -40.93) * mm});
            skLineSegment(sketch, "E2789", {"start": v(-49.08, -40.93) * mm, "end": v(-48.86, -40.97) * mm});
            skLineSegment(sketch, "E2790", {"start": v(-48.86, -40.97) * mm, "end": v(-48.63, -40.95) * mm});
            skLineSegment(sketch, "E2791", {"start": v(-48.63, -40.95) * mm, "end": v(-48.42, -40.87) * mm});
            skLineSegment(sketch, "E2792", {"start": v(-48.42, -40.87) * mm, "end": v(-48.24, -40.74) * mm});
            skLineSegment(sketch, "E2793", {"start": v(-48.24, -40.74) * mm, "end": v(-48.08, -40.6) * mm});
            skLineSegment(sketch, "E2794", {"start": v(-48.08, -40.6) * mm, "end": v(-47.91, -40.46) * mm});
            skLineSegment(sketch, "E2795", {"start": v(-47.91, -40.46) * mm, "end": v(-47.75, -40.31) * mm});
            skLineSegment(sketch, "E2796", {"start": v(-47.75, -40.31) * mm, "end": v(-47.58, -40.17) * mm});
            skLineSegment(sketch, "E2797", {"start": v(-47.58, -40.17) * mm, "end": v(-47.41, -40.03) * mm});
            skLineSegment(sketch, "E2798", {"start": v(-47.41, -40.03) * mm, "end": v(-47.25, -39.88) * mm});
            skLineSegment(sketch, "E2799", {"start": v(-47.25, -39.88) * mm, "end": v(-47.08, -39.74) * mm});
            skLineSegment(sketch, "E2800", {"start": v(-47.08, -39.74) * mm, "end": v(-46.91, -39.6) * mm});
            skLineSegment(sketch, "E2801", {"start": v(-46.91, -39.6) * mm, "end": v(-46.75, -39.45) * mm});
            skLineSegment(sketch, "E2802", {"start": v(-46.75, -39.45) * mm, "end": v(-46.58, -39.31) * mm});
            skLineSegment(sketch, "E2803", {"start": v(-46.58, -39.31) * mm, "end": v(-46.41, -39.16) * mm});
            skLineSegment(sketch, "E2804", {"start": v(-46.41, -39.16) * mm, "end": v(-46.25, -39.02) * mm});
            skLineSegment(sketch, "E2805", {"start": v(-46.25, -39.02) * mm, "end": v(-46.13, -38.92) * mm});
            skLineSegment(sketch, "E2806", {"start": v(-46.13, -38.92) * mm, "end": v(-45.98, -39.08) * mm});
            skLineSegment(sketch, "E2807", {"start": v(-45.98, -39.08) * mm, "end": v(-45.84, -39.24) * mm});
            skLineSegment(sketch, "E2808", {"start": v(-45.84, -39.24) * mm, "end": v(-45.7, -39.4) * mm});
            skLineSegment(sketch, "E2809", {"start": v(-45.7, -39.4) * mm, "end": v(-45.54, -39.57) * mm});
            skLineSegment(sketch, "E2810", {"start": v(-45.54, -39.57) * mm, "end": v(-45.4, -39.73) * mm});
            skLineSegment(sketch, "E2811", {"start": v(-45.4, -39.73) * mm, "end": v(-45.25, -39.89) * mm});
            skLineSegment(sketch, "E2812", {"start": v(-45.25, -39.89) * mm, "end": v(-45.1, -40.05) * mm});
            skLineSegment(sketch, "E2813", {"start": v(-45.1, -40.05) * mm, "end": v(-44.96, -40.21) * mm});
            skLineSegment(sketch, "E2814", {"start": v(-44.96, -40.21) * mm, "end": v(-44.82, -40.37) * mm});
            skLineSegment(sketch, "E2815", {"start": v(-44.82, -40.37) * mm, "end": v(-44.67, -40.54) * mm});
            skLineSegment(sketch, "E2816", {"start": v(-44.67, -40.54) * mm, "end": v(-44.52, -40.7) * mm});
            skLineSegment(sketch, "E2817", {"start": v(-44.52, -40.7) * mm, "end": v(-44.45, -40.78) * mm});
            skLineSegment(sketch, "E2818", {"start": v(-44.45, -40.78) * mm, "end": v(-44.61, -40.93) * mm});
            skLineSegment(sketch, "E2819", {"start": v(-44.61, -40.93) * mm, "end": v(-44.77, -41.08) * mm});
            skLineSegment(sketch, "E2820", {"start": v(-44.77, -41.08) * mm, "end": v(-44.93, -41.23) * mm});
            skLineSegment(sketch, "E2821", {"start": v(-44.93, -41.23) * mm, "end": v(-45.1, -41.38) * mm});
            skLineSegment(sketch, "E2822", {"start": v(-45.1, -41.38) * mm, "end": v(-45.25, -41.53) * mm});
            skLineSegment(sketch, "E2823", {"start": v(-45.25, -41.53) * mm, "end": v(-45.42, -41.68) * mm});
            skLineSegment(sketch, "E2824", {"start": v(-45.42, -41.68) * mm, "end": v(-45.57, -41.83) * mm});
            skLineSegment(sketch, "E2825", {"start": v(-45.57, -41.83) * mm, "end": v(-45.73, -41.98) * mm});
            skLineSegment(sketch, "E2826", {"start": v(-45.73, -41.98) * mm, "end": v(-45.9, -42.13) * mm});
            skLineSegment(sketch, "E2827", {"start": v(-45.9, -42.13) * mm, "end": v(-46.05, -42.28) * mm});
            skLineSegment(sketch, "E2828", {"start": v(-46.05, -42.28) * mm, "end": v(-46.21, -42.43) * mm});
            skLineSegment(sketch, "E2829", {"start": v(-46.21, -42.43) * mm, "end": v(-46.38, -42.58) * mm});
            skLineSegment(sketch, "E2830", {"start": v(-46.38, -42.58) * mm, "end": v(-46.55, -42.75) * mm});
            skLineSegment(sketch, "E2831", {"start": v(-46.55, -42.75) * mm, "end": v(-46.68, -42.93) * mm});
            skLineSegment(sketch, "E2832", {"start": v(-46.68, -42.93) * mm, "end": v(-46.76, -43.14) * mm});
            skLineSegment(sketch, "E2833", {"start": v(-46.76, -43.14) * mm, "end": v(-46.78, -43.37) * mm});
            skLineSegment(sketch, "E2834", {"start": v(-46.78, -43.37) * mm, "end": v(-46.75, -43.6) * mm});
            skLineSegment(sketch, "E2835", {"start": v(-46.75, -43.6) * mm, "end": v(-46.65, -43.8) * mm});
            skLineSegment(sketch, "E2836", {"start": v(-46.65, -43.8) * mm, "end": v(-46.5, -43.97) * mm});
            skLineSegment(sketch, "E2837", {"start": v(-46.5, -43.97) * mm, "end": v(-46.32, -44.1) * mm});
            skLineSegment(sketch, "E2838", {"start": v(-46.32, -44.1) * mm, "end": v(-46.1, -44.19) * mm});
            skLineSegment(sketch, "E2839", {"start": v(-46.1, -44.19) * mm, "end": v(-45.88, -44.2) * mm});
            skLineSegment(sketch, "E2840", {"start": v(-45.88, -44.2) * mm, "end": v(-45.66, -44.17) * mm});
            skLineSegment(sketch, "E2841", {"start": v(-45.66, -44.17) * mm, "end": v(-45.45, -44.07) * mm});
            skLineSegment(sketch, "E2842", {"start": v(-45.45, -44.07) * mm, "end": v(-45.29, -43.93) * mm});
            skLineSegment(sketch, "E2843", {"start": v(-45.29, -43.93) * mm, "end": v(-45.13, -43.78) * mm});
            skLineSegment(sketch, "E2844", {"start": v(-45.13, -43.78) * mm, "end": v(-44.98, -43.63) * mm});
            skLineSegment(sketch, "E2845", {"start": v(-44.98, -43.63) * mm, "end": v(-44.82, -43.47) * mm});
            skLineSegment(sketch, "E2846", {"start": v(-44.82, -43.47) * mm, "end": v(-44.67, -43.32) * mm});
            skLineSegment(sketch, "E2847", {"start": v(-44.67, -43.32) * mm, "end": v(-44.5, -43.16) * mm});
            skLineSegment(sketch, "E2848", {"start": v(-44.5, -43.16) * mm, "end": v(-44.35, -43) * mm});
            skLineSegment(sketch, "E2849", {"start": v(-44.35, -43) * mm, "end": v(-44.2, -42.86) * mm});
            skLineSegment(sketch, "E2850", {"start": v(-44.2, -42.86) * mm, "end": v(-44.04, -42.7) * mm});
            skLineSegment(sketch, "E2851", {"start": v(-44.04, -42.7) * mm, "end": v(-43.88, -42.55) * mm});
            skLineSegment(sketch, "E2852", {"start": v(-43.88, -42.55) * mm, "end": v(-43.73, -42.4) * mm});
            skLineSegment(sketch, "E2853", {"start": v(-43.73, -42.4) * mm, "end": v(-43.57, -42.23) * mm});
            skLineSegment(sketch, "E2854", {"start": v(-43.57, -42.23) * mm, "end": v(-43.42, -42.08) * mm});
            skLineSegment(sketch, "E2855", {"start": v(-43.42, -42.08) * mm, "end": v(-43.3, -41.97) * mm});
            skLineSegment(sketch, "E2856", {"start": v(-43.3, -41.97) * mm, "end": v(-43.15, -42.12) * mm});
            skLineSegment(sketch, "E2857", {"start": v(-43.15, -42.12) * mm, "end": v(-42.99, -42.27) * mm});
            skLineSegment(sketch, "E2858", {"start": v(-42.99, -42.27) * mm, "end": v(-42.83, -42.42) * mm});
            skLineSegment(sketch, "E2859", {"start": v(-42.83, -42.42) * mm, "end": v(-42.68, -42.57) * mm});
            skLineSegment(sketch, "E2860", {"start": v(-42.68, -42.57) * mm, "end": v(-42.52, -42.72) * mm});
            skLineSegment(sketch, "E2861", {"start": v(-42.52, -42.72) * mm, "end": v(-42.36, -42.88) * mm});
            skLineSegment(sketch, "E2862", {"start": v(-42.36, -42.88) * mm, "end": v(-42.2, -43.03) * mm});
            skLineSegment(sketch, "E2863", {"start": v(-42.2, -43.03) * mm, "end": v(-42.05, -43.18) * mm});
            skLineSegment(sketch, "E2864", {"start": v(-42.05, -43.18) * mm, "end": v(-41.9, -43.33) * mm});
            skLineSegment(sketch, "E2865", {"start": v(-41.9, -43.33) * mm, "end": v(-41.74, -43.48) * mm});
            skLineSegment(sketch, "E2866", {"start": v(-41.74, -43.48) * mm, "end": v(-41.58, -43.63) * mm});
            skLineSegment(sketch, "E2867", {"start": v(-41.58, -43.63) * mm, "end": v(-41.5, -43.7) * mm});
            skLineSegment(sketch, "E2868", {"start": v(-41.5, -43.7) * mm, "end": v(-41.65, -43.87) * mm});
            skLineSegment(sketch, "E2869", {"start": v(-41.65, -43.87) * mm, "end": v(-41.8, -44.03) * mm});
            skLineSegment(sketch, "E2870", {"start": v(-41.8, -44.03) * mm, "end": v(-41.95, -44.2) * mm});
            skLineSegment(sketch, "E2871", {"start": v(-41.95, -44.2) * mm, "end": v(-42.1, -44.35) * mm});
            skLineSegment(sketch, "E2872", {"start": v(-42.1, -44.35) * mm, "end": v(-42.25, -44.51) * mm});
            skLineSegment(sketch, "E2873", {"start": v(-42.25, -44.51) * mm, "end": v(-42.4, -44.67) * mm});
            skLineSegment(sketch, "E2874", {"start": v(-42.4, -44.67) * mm, "end": v(-42.55, -44.83) * mm});
            skLineSegment(sketch, "E2875", {"start": v(-42.55, -44.83) * mm, "end": v(-42.7, -45) * mm});
            skLineSegment(sketch, "E2876", {"start": v(-42.7, -45) * mm, "end": v(-42.85, -45.16) * mm});
            skLineSegment(sketch, "E2877", {"start": v(-42.85, -45.16) * mm, "end": v(-43, -45.32) * mm});
            skLineSegment(sketch, "E2878", {"start": v(-43, -45.32) * mm, "end": v(-43.14, -45.48) * mm});
            skLineSegment(sketch, "E2879", {"start": v(-43.14, -45.48) * mm, "end": v(-43.3, -45.64) * mm});
            skLineSegment(sketch, "E2880", {"start": v(-43.3, -45.64) * mm, "end": v(-43.45, -45.82) * mm});
            skLineSegment(sketch, "E2881", {"start": v(-43.45, -45.82) * mm, "end": v(-43.57, -46) * mm});
            skLineSegment(sketch, "E2882", {"start": v(-43.57, -46) * mm, "end": v(-43.64, -46.23) * mm});
            skLineSegment(sketch, "E2883", {"start": v(-43.64, -46.23) * mm, "end": v(-43.65, -46.45) * mm});
            skLineSegment(sketch, "E2884", {"start": v(-43.65, -46.45) * mm, "end": v(-43.6, -46.67) * mm});
            skLineSegment(sketch, "E2885", {"start": v(-43.6, -46.67) * mm, "end": v(-43.49, -46.87) * mm});
            skLineSegment(sketch, "E2886", {"start": v(-43.49, -46.87) * mm, "end": v(-43.33, -47.04) * mm});
            skLineSegment(sketch, "E2887", {"start": v(-43.33, -47.04) * mm, "end": v(-43.14, -47.16) * mm});
            skLineSegment(sketch, "E2888", {"start": v(-43.14, -47.16) * mm, "end": v(-42.92, -47.22) * mm});
            skLineSegment(sketch, "E2889", {"start": v(-42.92, -47.22) * mm, "end": v(-42.69, -47.23) * mm});
            skLineSegment(sketch, "E2890", {"start": v(-42.69, -47.23) * mm, "end": v(-42.47, -47.17) * mm});
            skLineSegment(sketch, "E2891", {"start": v(-42.47, -47.17) * mm, "end": v(-42.27, -47.06) * mm});
            skLineSegment(sketch, "E2892", {"start": v(-42.27, -47.06) * mm, "end": v(-42.11, -46.91) * mm});
            skLineSegment(sketch, "E2893", {"start": v(-42.11, -46.91) * mm, "end": v(-41.97, -46.75) * mm});
            skLineSegment(sketch, "E2894", {"start": v(-41.97, -46.75) * mm, "end": v(-41.83, -46.59) * mm});
            skLineSegment(sketch, "E2895", {"start": v(-41.83, -46.59) * mm, "end": v(-41.68, -46.42) * mm});
            skLineSegment(sketch, "E2896", {"start": v(-41.68, -46.42) * mm, "end": v(-41.54, -46.26) * mm});
            skLineSegment(sketch, "E2897", {"start": v(-41.54, -46.26) * mm, "end": v(-41.4, -46.1) * mm});
            skLineSegment(sketch, "E2898", {"start": v(-41.4, -46.1) * mm, "end": v(-41.25, -45.93) * mm});
            skLineSegment(sketch, "E2899", {"start": v(-41.25, -45.93) * mm, "end": v(-41.1, -45.76) * mm});
            skLineSegment(sketch, "E2900", {"start": v(-41.1, -45.76) * mm, "end": v(-40.96, -45.6) * mm});
            skLineSegment(sketch, "E2901", {"start": v(-40.96, -45.6) * mm, "end": v(-40.81, -45.43) * mm});
            skLineSegment(sketch, "E2902", {"start": v(-40.81, -45.43) * mm, "end": v(-40.67, -45.27) * mm});
            skLineSegment(sketch, "E2903", {"start": v(-40.67, -45.27) * mm, "end": v(-40.52, -45.1) * mm});
            skLineSegment(sketch, "E2904", {"start": v(-40.52, -45.1) * mm, "end": v(-40.38, -44.93) * mm});
            skLineSegment(sketch, "E2905", {"start": v(-40.38, -44.93) * mm, "end": v(-40.27, -44.81) * mm});
            skLineSegment(sketch, "E2906", {"start": v(-40.27, -44.81) * mm, "end": v(-40.1, -44.95) * mm});
            skLineSegment(sketch, "E2907", {"start": v(-40.1, -44.95) * mm, "end": v(-39.94, -45.1) * mm});
            skLineSegment(sketch, "E2908", {"start": v(-39.94, -45.1) * mm, "end": v(-39.77, -45.23) * mm});
            skLineSegment(sketch, "E2909", {"start": v(-39.77, -45.23) * mm, "end": v(-39.6, -45.37) * mm});
            skLineSegment(sketch, "E2910", {"start": v(-39.6, -45.37) * mm, "end": v(-39.44, -45.51) * mm});
            skLineSegment(sketch, "E2911", {"start": v(-39.44, -45.51) * mm, "end": v(-39.27, -45.65) * mm});
            skLineSegment(sketch, "E2912", {"start": v(-39.27, -45.65) * mm, "end": v(-39.1, -45.8) * mm});
            skLineSegment(sketch, "E2913", {"start": v(-39.1, -45.8) * mm, "end": v(-38.94, -45.93) * mm});
            skLineSegment(sketch, "E2914", {"start": v(-38.94, -45.93) * mm, "end": v(-38.77, -46.07) * mm});
            skLineSegment(sketch, "E2915", {"start": v(-38.77, -46.07) * mm, "end": v(-38.6, -46.21) * mm});
            skLineSegment(sketch, "E2916", {"start": v(-38.6, -46.21) * mm, "end": v(-38.44, -46.35) * mm});
            skLineSegment(sketch, "E2917", {"start": v(-38.44, -46.35) * mm, "end": v(-38.36, -46.42) * mm});
            skLineSegment(sketch, "E2918", {"start": v(-38.36, -46.42) * mm, "end": v(-38.5, -46.6) * mm});
            skLineSegment(sketch, "E2919", {"start": v(-38.5, -46.6) * mm, "end": v(-38.63, -46.76) * mm});
            skLineSegment(sketch, "E2920", {"start": v(-38.63, -46.76) * mm, "end": v(-38.77, -46.94) * mm});
            skLineSegment(sketch, "E2921", {"start": v(-38.77, -46.94) * mm, "end": v(-38.9, -47.1) * mm});
            skLineSegment(sketch, "E2922", {"start": v(-38.9, -47.1) * mm, "end": v(-39.04, -47.28) * mm});
            skLineSegment(sketch, "E2923", {"start": v(-39.04, -47.28) * mm, "end": v(-39.18, -47.45) * mm});
            skLineSegment(sketch, "E2924", {"start": v(-39.18, -47.45) * mm, "end": v(-39.32, -47.62) * mm});
            skLineSegment(sketch, "E2925", {"start": v(-39.32, -47.62) * mm, "end": v(-39.46, -47.8) * mm});
            skLineSegment(sketch, "E2926", {"start": v(-39.46, -47.8) * mm, "end": v(-39.6, -47.97) * mm});
            skLineSegment(sketch, "E2927", {"start": v(-39.6, -47.97) * mm, "end": v(-39.73, -48.14) * mm});
            skLineSegment(sketch, "E2928", {"start": v(-39.73, -48.14) * mm, "end": v(-39.87, -48.3) * mm});
            skLineSegment(sketch, "E2929", {"start": v(-39.87, -48.3) * mm, "end": v(-40, -48.48) * mm});
            skLineSegment(sketch, "E2930", {"start": v(-40, -48.48) * mm, "end": v(-40.15, -48.66) * mm});
            skLineSegment(sketch, "E2931", {"start": v(-40.15, -48.66) * mm, "end": v(-40.26, -48.86) * mm});
            skLineSegment(sketch, "E2932", {"start": v(-40.26, -48.86) * mm, "end": v(-40.31, -49.09) * mm});
            skLineSegment(sketch, "E2933", {"start": v(-40.31, -49.09) * mm, "end": v(-40.3, -49.31) * mm});
            skLineSegment(sketch, "E2934", {"start": v(-40.3, -49.31) * mm, "end": v(-40.23, -49.53) * mm});
            skLineSegment(sketch, "E2935", {"start": v(-40.23, -49.53) * mm, "end": v(-40.11, -49.72) * mm});
            skLineSegment(sketch, "E2936", {"start": v(-40.11, -49.72) * mm, "end": v(-39.94, -49.88) * mm});
            skLineSegment(sketch, "E2937", {"start": v(-39.94, -49.88) * mm, "end": v(-39.74, -49.98) * mm});
            skLineSegment(sketch, "E2938", {"start": v(-39.74, -49.98) * mm, "end": v(-39.52, -50.03) * mm});
            skLineSegment(sketch, "E2939", {"start": v(-39.52, -50.03) * mm, "end": v(-39.3, -50.02) * mm});
            skLineSegment(sketch, "E2940", {"start": v(-39.3, -50.02) * mm, "end": v(-39.08, -49.95) * mm});
            skLineSegment(sketch, "E2941", {"start": v(-39.08, -49.95) * mm, "end": v(-38.89, -49.83) * mm});
            skLineSegment(sketch, "E2942", {"start": v(-38.89, -49.83) * mm, "end": v(-38.74, -49.66) * mm});
            skLineSegment(sketch, "E2943", {"start": v(-38.74, -49.66) * mm, "end": v(-38.6, -49.5) * mm});
            skLineSegment(sketch, "E2944", {"start": v(-38.6, -49.5) * mm, "end": v(-38.48, -49.32) * mm});
            skLineSegment(sketch, "E2945", {"start": v(-38.48, -49.32) * mm, "end": v(-38.34, -49.15) * mm});
            skLineSegment(sketch, "E2946", {"start": v(-38.34, -49.15) * mm, "end": v(-38.21, -48.97) * mm});
            skLineSegment(sketch, "E2947", {"start": v(-38.21, -48.97) * mm, "end": v(-38.08, -48.8) * mm});
            skLineSegment(sketch, "E2948", {"start": v(-38.08, -48.8) * mm, "end": v(-37.95, -48.62) * mm});
            skLineSegment(sketch, "E2949", {"start": v(-37.95, -48.62) * mm, "end": v(-37.81, -48.45) * mm});
            skLineSegment(sketch, "E2950", {"start": v(-37.81, -48.45) * mm, "end": v(-37.68, -48.27) * mm});
            skLineSegment(sketch, "E2951", {"start": v(-37.68, -48.27) * mm, "end": v(-37.55, -48.1) * mm});
            skLineSegment(sketch, "E2952", {"start": v(-37.55, -48.1) * mm, "end": v(-37.41, -47.92) * mm});
            skLineSegment(sketch, "E2953", {"start": v(-37.41, -47.92) * mm, "end": v(-37.28, -47.74) * mm});
            skLineSegment(sketch, "E2954", {"start": v(-37.28, -47.74) * mm, "end": v(-37.15, -47.57) * mm});
            skLineSegment(sketch, "E2955", {"start": v(-37.15, -47.57) * mm, "end": v(-37.05, -47.44) * mm});
            skLineSegment(sketch, "E2956", {"start": v(-37.05, -47.44) * mm, "end": v(-36.87, -47.57) * mm});
            skLineSegment(sketch, "E2957", {"start": v(-36.87, -47.57) * mm, "end": v(-36.7, -47.7) * mm});
            skLineSegment(sketch, "E2958", {"start": v(-36.7, -47.7) * mm, "end": v(-36.52, -47.83) * mm});
            skLineSegment(sketch, "E2959", {"start": v(-36.52, -47.83) * mm, "end": v(-36.35, -47.95) * mm});
            skLineSegment(sketch, "E2960", {"start": v(-36.35, -47.95) * mm, "end": v(-36.17, -48.08) * mm});
            skLineSegment(sketch, "E2961", {"start": v(-36.17, -48.08) * mm, "end": v(-36, -48.21) * mm});
            skLineSegment(sketch, "E2962", {"start": v(-36, -48.21) * mm, "end": v(-35.82, -48.34) * mm});
            skLineSegment(sketch, "E2963", {"start": v(-35.82, -48.34) * mm, "end": v(-35.64, -48.47) * mm});
            skLineSegment(sketch, "E2964", {"start": v(-35.64, -48.47) * mm, "end": v(-35.46, -48.6) * mm});
            skLineSegment(sketch, "E2965", {"start": v(-35.46, -48.6) * mm, "end": v(-35.29, -48.72) * mm});
            skLineSegment(sketch, "E2966", {"start": v(-35.29, -48.72) * mm, "end": v(-35.11, -48.85) * mm});
            skLineSegment(sketch, "E2967", {"start": v(-35.11, -48.85) * mm, "end": v(-35.03, -48.91) * mm});
            skLineSegment(sketch, "E2968", {"start": v(-35.03, -48.91) * mm, "end": v(-35.15, -49.1) * mm});
            skLineSegment(sketch, "E2969", {"start": v(-35.15, -49.1) * mm, "end": v(-35.28, -49.27) * mm});
            skLineSegment(sketch, "E2970", {"start": v(-35.28, -49.27) * mm, "end": v(-35.4, -49.46) * mm});
            skLineSegment(sketch, "E2971", {"start": v(-35.4, -49.46) * mm, "end": v(-35.53, -49.63) * mm});
            skLineSegment(sketch, "E2972", {"start": v(-35.53, -49.63) * mm, "end": v(-35.65, -49.81) * mm});
            skLineSegment(sketch, "E2973", {"start": v(-35.65, -49.81) * mm, "end": v(-35.78, -50) * mm});
            skLineSegment(sketch, "E2974", {"start": v(-35.78, -50) * mm, "end": v(-35.9, -50.18) * mm});
            skLineSegment(sketch, "E2975", {"start": v(-35.9, -50.18) * mm, "end": v(-36.03, -50.35) * mm});
            skLineSegment(sketch, "E2976", {"start": v(-36.03, -50.35) * mm, "end": v(-36.16, -50.54) * mm});
            skLineSegment(sketch, "E2977", {"start": v(-36.16, -50.54) * mm, "end": v(-36.28, -50.72) * mm});
            skLineSegment(sketch, "E2978", {"start": v(-36.28, -50.72) * mm, "end": v(-36.4, -50.9) * mm});
            skLineSegment(sketch, "E2979", {"start": v(-36.4, -50.9) * mm, "end": v(-36.53, -51.08) * mm});
            skLineSegment(sketch, "E2980", {"start": v(-36.53, -51.08) * mm, "end": v(-36.66, -51.27) * mm});
            skLineSegment(sketch, "E2981", {"start": v(-36.66, -51.27) * mm, "end": v(-36.76, -51.48) * mm});
            skLineSegment(sketch, "E2982", {"start": v(-36.76, -51.48) * mm, "end": v(-36.8, -51.7) * mm});
            skLineSegment(sketch, "E2983", {"start": v(-36.8, -51.7) * mm, "end": v(-36.77, -51.93) * mm});
            skLineSegment(sketch, "E2984", {"start": v(-36.77, -51.93) * mm, "end": v(-36.68, -52.14) * mm});
            skLineSegment(sketch, "E2985", {"start": v(-36.68, -52.14) * mm, "end": v(-36.55, -52.33) * mm});
            skLineSegment(sketch, "E2986", {"start": v(-36.55, -52.33) * mm, "end": v(-36.37, -52.47) * mm});
            skLineSegment(sketch, "E2987", {"start": v(-36.37, -52.47) * mm, "end": v(-36.16, -52.56) * mm});
            skLineSegment(sketch, "E2988", {"start": v(-36.16, -52.56) * mm, "end": v(-35.94, -52.6) * mm});
            skLineSegment(sketch, "E2989", {"start": v(-35.94, -52.6) * mm, "end": v(-35.71, -52.57) * mm});
            skLineSegment(sketch, "E2990", {"start": v(-35.71, -52.57) * mm, "end": v(-35.5, -52.48) * mm});
            skLineSegment(sketch, "E2991", {"start": v(-35.5, -52.48) * mm, "end": v(-35.32, -52.35) * mm});
            skLineSegment(sketch, "E2992", {"start": v(-35.32, -52.35) * mm, "end": v(-35.19, -52.17) * mm});
            skLineSegment(sketch, "E2993", {"start": v(-35.19, -52.17) * mm, "end": v(-35.06, -52) * mm});
            skLineSegment(sketch, "E2994", {"start": v(-35.06, -52) * mm, "end": v(-34.94, -51.81) * mm});
            skLineSegment(sketch, "E2995", {"start": v(-34.94, -51.81) * mm, "end": v(-34.83, -51.63) * mm});
            skLineSegment(sketch, "E2996", {"start": v(-34.83, -51.63) * mm, "end": v(-34.7, -51.45) * mm});
            skLineSegment(sketch, "E2997", {"start": v(-34.7, -51.45) * mm, "end": v(-34.58, -51.26) * mm});
            skLineSegment(sketch, "E2998", {"start": v(-34.58, -51.26) * mm, "end": v(-34.46, -51.08) * mm});
            skLineSegment(sketch, "E2999", {"start": v(-34.46, -51.08) * mm, "end": v(-34.34, -50.9) * mm});
            skLineSegment(sketch, "E3000", {"start": v(-34.34, -50.9) * mm, "end": v(-34.22, -50.7) * mm});
            skLineSegment(sketch, "E3001", {"start": v(-34.22, -50.7) * mm, "end": v(-34.1, -50.52) * mm});
            skLineSegment(sketch, "E3002", {"start": v(-34.1, -50.52) * mm, "end": v(-33.98, -50.34) * mm});
            skLineSegment(sketch, "E3003", {"start": v(-33.98, -50.34) * mm, "end": v(-33.86, -50.15) * mm});
            skLineSegment(sketch, "E3004", {"start": v(-33.86, -50.15) * mm, "end": v(-33.74, -49.97) * mm});
            skLineSegment(sketch, "E3005", {"start": v(-33.74, -49.97) * mm, "end": v(-33.65, -49.84) * mm});
            skLineSegment(sketch, "E3006", {"start": v(-33.65, -49.84) * mm, "end": v(-33.47, -49.95) * mm});
            skLineSegment(sketch, "E3007", {"start": v(-33.47, -49.95) * mm, "end": v(-33.28, -50.07) * mm});
            skLineSegment(sketch, "E3008", {"start": v(-33.28, -50.07) * mm, "end": v(-33.1, -50.19) * mm});
            skLineSegment(sketch, "E3009", {"start": v(-33.1, -50.19) * mm, "end": v(-32.92, -50.3) * mm});
            skLineSegment(sketch, "E3010", {"start": v(-32.92, -50.3) * mm, "end": v(-32.73, -50.42) * mm});
            skLineSegment(sketch, "E3011", {"start": v(-32.73, -50.42) * mm, "end": v(-32.55, -50.53) * mm});
            skLineSegment(sketch, "E3012", {"start": v(-32.55, -50.53) * mm, "end": v(-32.36, -50.65) * mm});
            skLineSegment(sketch, "E3013", {"start": v(-32.36, -50.65) * mm, "end": v(-32.18, -50.76) * mm});
            skLineSegment(sketch, "E3014", {"start": v(-32.18, -50.76) * mm, "end": v(-32, -50.88) * mm});
            skLineSegment(sketch, "E3015", {"start": v(-32, -50.88) * mm, "end": v(-31.8, -51) * mm});
            skLineSegment(sketch, "E3016", {"start": v(-31.8, -51) * mm, "end": v(-31.62, -51.1) * mm});
            skLineSegment(sketch, "E3017", {"start": v(-31.62, -51.1) * mm, "end": v(-31.53, -51.17) * mm});
            skLineSegment(sketch, "E3018", {"start": v(-31.53, -51.17) * mm, "end": v(-31.64, -51.35) * mm});
            skLineSegment(sketch, "E3019", {"start": v(-31.64, -51.35) * mm, "end": v(-31.75, -51.54) * mm});
            skLineSegment(sketch, "E3020", {"start": v(-31.75, -51.54) * mm, "end": v(-31.87, -51.73) * mm});
            skLineSegment(sketch, "E3021", {"start": v(-31.87, -51.73) * mm, "end": v(-31.98, -51.92) * mm});
            skLineSegment(sketch, "E3022", {"start": v(-31.98, -51.92) * mm, "end": v(-32.1, -52.1) * mm});
            skLineSegment(sketch, "E3023", {"start": v(-32.1, -52.1) * mm, "end": v(-32.2, -52.3) * mm});
            skLineSegment(sketch, "E3024", {"start": v(-32.2, -52.3) * mm, "end": v(-32.32, -52.49) * mm});
            skLineSegment(sketch, "E3025", {"start": v(-32.32, -52.49) * mm, "end": v(-32.43, -52.67) * mm});
            skLineSegment(sketch, "E3026", {"start": v(-32.43, -52.67) * mm, "end": v(-32.54, -52.87) * mm});
            skLineSegment(sketch, "E3027", {"start": v(-32.54, -52.87) * mm, "end": v(-32.66, -53.05) * mm});
            skLineSegment(sketch, "E3028", {"start": v(-32.66, -53.05) * mm, "end": v(-32.77, -53.24) * mm});
            skLineSegment(sketch, "E3029", {"start": v(-32.77, -53.24) * mm, "end": v(-32.88, -53.43) * mm});
            skLineSegment(sketch, "E3030", {"start": v(-32.88, -53.43) * mm, "end": v(-33, -53.63) * mm});
            skLineSegment(sketch, "E3031", {"start": v(-33, -53.63) * mm, "end": v(-33.08, -53.85) * mm});
            skLineSegment(sketch, "E3032", {"start": v(-33.08, -53.85) * mm, "end": v(-33.1, -54.07) * mm});
            skLineSegment(sketch, "E3033", {"start": v(-33.1, -54.07) * mm, "end": v(-33.06, -54.3) * mm});
            skLineSegment(sketch, "E3034", {"start": v(-33.06, -54.3) * mm, "end": v(-32.96, -54.5) * mm});
            skLineSegment(sketch, "E3035", {"start": v(-32.96, -54.5) * mm, "end": v(-32.81, -54.68) * mm});
            skLineSegment(sketch, "E3036", {"start": v(-32.81, -54.68) * mm, "end": v(-32.62, -54.8) * mm});
            skLineSegment(sketch, "E3037", {"start": v(-32.62, -54.8) * mm, "end": v(-32.41, -54.88) * mm});
            skLineSegment(sketch, "E3038", {"start": v(-32.41, -54.88) * mm, "end": v(-32.18, -54.9) * mm});
            skLineSegment(sketch, "E3039", {"start": v(-32.18, -54.9) * mm, "end": v(-31.96, -54.86) * mm});
            skLineSegment(sketch, "E3040", {"start": v(-31.96, -54.86) * mm, "end": v(-31.76, -54.76) * mm});
            skLineSegment(sketch, "E3041", {"start": v(-31.76, -54.76) * mm, "end": v(-31.58, -54.6) * mm});
            skLineSegment(sketch, "E3042", {"start": v(-31.58, -54.6) * mm, "end": v(-31.46, -54.43) * mm});
            skLineSegment(sketch, "E3043", {"start": v(-31.46, -54.43) * mm, "end": v(-31.35, -54.24) * mm});
            skLineSegment(sketch, "E3044", {"start": v(-31.35, -54.24) * mm, "end": v(-31.25, -54.05) * mm});
            skLineSegment(sketch, "E3045", {"start": v(-31.25, -54.05) * mm, "end": v(-31.14, -53.86) * mm});
            skLineSegment(sketch, "E3046", {"start": v(-31.14, -53.86) * mm, "end": v(-31.04, -53.67) * mm});
            skLineSegment(sketch, "E3047", {"start": v(-31.04, -53.67) * mm, "end": v(-30.93, -53.47) * mm});
            skLineSegment(sketch, "E3048", {"start": v(-30.93, -53.47) * mm, "end": v(-30.82, -53.28) * mm});
            skLineSegment(sketch, "E3049", {"start": v(-30.82, -53.28) * mm, "end": v(-30.71, -53.1) * mm});
            skLineSegment(sketch, "E3050", {"start": v(-30.71, -53.1) * mm, "end": v(-30.6, -52.9) * mm});
            skLineSegment(sketch, "E3051", {"start": v(-30.6, -52.9) * mm, "end": v(-30.5, -52.7) * mm});
            skLineSegment(sketch, "E3052", {"start": v(-30.5, -52.7) * mm, "end": v(-30.4, -52.52) * mm});
            skLineSegment(sketch, "E3053", {"start": v(-30.4, -52.52) * mm, "end": v(-30.28, -52.32) * mm});
            skLineSegment(sketch, "E3054", {"start": v(-30.28, -52.32) * mm, "end": v(-30.18, -52.13) * mm});
            skLineSegment(sketch, "E3055", {"start": v(-30.18, -52.13) * mm, "end": v(-30.1, -52) * mm});
            skLineSegment(sketch, "E3056", {"start": v(-30.1, -52) * mm, "end": v(-29.9, -52.1) * mm});
            skLineSegment(sketch, "E3057", {"start": v(-29.9, -52.1) * mm, "end": v(-29.71, -52.2) * mm});
            skLineSegment(sketch, "E3058", {"start": v(-29.71, -52.2) * mm, "end": v(-29.52, -52.3) * mm});
            skLineSegment(sketch, "E3059", {"start": v(-29.52, -52.3) * mm, "end": v(-29.33, -52.4) * mm});
            skLineSegment(sketch, "E3060", {"start": v(-29.33, -52.4) * mm, "end": v(-29.14, -52.5) * mm});
            skLineSegment(sketch, "E3061", {"start": v(-29.14, -52.5) * mm, "end": v(-28.94, -52.6) * mm});
            skLineSegment(sketch, "E3062", {"start": v(-28.94, -52.6) * mm, "end": v(-28.75, -52.7) * mm});
            skLineSegment(sketch, "E3063", {"start": v(-28.75, -52.7) * mm, "end": v(-28.56, -52.81) * mm});
            skLineSegment(sketch, "E3064", {"start": v(-28.56, -52.81) * mm, "end": v(-28.37, -52.91) * mm});
            skLineSegment(sketch, "E3065", {"start": v(-28.37, -52.91) * mm, "end": v(-28.17, -53.02) * mm});
            skLineSegment(sketch, "E3066", {"start": v(-28.17, -53.02) * mm, "end": v(-27.98, -53.12) * mm});
            skLineSegment(sketch, "E3067", {"start": v(-27.98, -53.12) * mm, "end": v(-27.89, -53.17) * mm});
            skLineSegment(sketch, "E3068", {"start": v(-27.89, -53.17) * mm, "end": v(-27.99, -53.36) * mm});
            skLineSegment(sketch, "E3069", {"start": v(-27.99, -53.36) * mm, "end": v(-28.08, -53.56) * mm});
            skLineSegment(sketch, "E3070", {"start": v(-28.08, -53.56) * mm, "end": v(-28.19, -53.76) * mm});
            skLineSegment(sketch, "E3071", {"start": v(-28.19, -53.76) * mm, "end": v(-28.28, -53.95) * mm});
            skLineSegment(sketch, "E3072", {"start": v(-28.28, -53.95) * mm, "end": v(-28.38, -54.15) * mm});
            skLineSegment(sketch, "E3073", {"start": v(-28.38, -54.15) * mm, "end": v(-28.48, -54.35) * mm});
            skLineSegment(sketch, "E3074", {"start": v(-28.48, -54.35) * mm, "end": v(-28.58, -54.54) * mm});
            skLineSegment(sketch, "E3075", {"start": v(-28.58, -54.54) * mm, "end": v(-28.68, -54.73) * mm});
            skLineSegment(sketch, "E3076", {"start": v(-28.68, -54.73) * mm, "end": v(-28.78, -54.93) * mm});
            skLineSegment(sketch, "E3077", {"start": v(-28.78, -54.93) * mm, "end": v(-28.88, -55.13) * mm});
            skLineSegment(sketch, "E3078", {"start": v(-28.88, -55.13) * mm, "end": v(-28.98, -55.32) * mm});
            skLineSegment(sketch, "E3079", {"start": v(-28.98, -55.32) * mm, "end": v(-29.08, -55.52) * mm});
            skLineSegment(sketch, "E3080", {"start": v(-29.08, -55.52) * mm, "end": v(-29.18, -55.73) * mm});
            skLineSegment(sketch, "E3081", {"start": v(-29.18, -55.73) * mm, "end": v(-29.24, -55.95) * mm});
            skLineSegment(sketch, "E3082", {"start": v(-29.24, -55.95) * mm, "end": v(-29.25, -56.18) * mm});
            skLineSegment(sketch, "E3083", {"start": v(-29.25, -56.18) * mm, "end": v(-29.2, -56.4) * mm});
            skLineSegment(sketch, "E3084", {"start": v(-29.2, -56.4) * mm, "end": v(-29.08, -56.6) * mm});
            skLineSegment(sketch, "E3085", {"start": v(-29.08, -56.6) * mm, "end": v(-28.92, -56.76) * mm});
            skLineSegment(sketch, "E3086", {"start": v(-28.92, -56.76) * mm, "end": v(-28.72, -56.88) * mm});
            skLineSegment(sketch, "E3087", {"start": v(-28.72, -56.88) * mm, "end": v(-28.5, -56.94) * mm});
            skLineSegment(sketch, "E3088", {"start": v(-28.5, -56.94) * mm, "end": v(-28.28, -56.94) * mm});
            skLineSegment(sketch, "E3089", {"start": v(-28.28, -56.94) * mm, "end": v(-28.06, -56.88) * mm});
            skLineSegment(sketch, "E3090", {"start": v(-28.06, -56.88) * mm, "end": v(-27.86, -56.77) * mm});
            skLineSegment(sketch, "E3091", {"start": v(-27.86, -56.77) * mm, "end": v(-27.7, -56.6) * mm});
            skLineSegment(sketch, "E3092", {"start": v(-27.7, -56.6) * mm, "end": v(-27.6, -56.42) * mm});
            skLineSegment(sketch, "E3093", {"start": v(-27.6, -56.42) * mm, "end": v(-27.5, -56.22) * mm});
            skLineSegment(sketch, "E3094", {"start": v(-27.5, -56.22) * mm, "end": v(-27.4, -56.03) * mm});
            skLineSegment(sketch, "E3095", {"start": v(-27.4, -56.03) * mm, "end": v(-27.31, -55.83) * mm});
            skLineSegment(sketch, "E3096", {"start": v(-27.31, -55.83) * mm, "end": v(-27.22, -55.63) * mm});
            skLineSegment(sketch, "E3097", {"start": v(-27.22, -55.63) * mm, "end": v(-27.12, -55.43) * mm});
            skLineSegment(sketch, "E3098", {"start": v(-27.12, -55.43) * mm, "end": v(-27.03, -55.23) * mm});
            skLineSegment(sketch, "E3099", {"start": v(-27.03, -55.23) * mm, "end": v(-26.94, -55.03) * mm});
            skLineSegment(sketch, "E3100", {"start": v(-26.94, -55.03) * mm, "end": v(-26.84, -54.83) * mm});
            skLineSegment(sketch, "E3101", {"start": v(-26.84, -54.83) * mm, "end": v(-26.75, -54.63) * mm});
            skLineSegment(sketch, "E3102", {"start": v(-26.75, -54.63) * mm, "end": v(-26.66, -54.44) * mm});
            skLineSegment(sketch, "E3103", {"start": v(-26.66, -54.44) * mm, "end": v(-26.56, -54.23) * mm});
            skLineSegment(sketch, "E3104", {"start": v(-26.56, -54.23) * mm, "end": v(-26.47, -54.04) * mm});
            skLineSegment(sketch, "E3105", {"start": v(-26.47, -54.04) * mm, "end": v(-26.4, -53.9) * mm});
            skLineSegment(sketch, "E3106", {"start": v(-26.4, -53.9) * mm, "end": v(-26.2, -53.98) * mm});
            skLineSegment(sketch, "E3107", {"start": v(-26.2, -53.98) * mm, "end": v(-26, -54.07) * mm});
            skLineSegment(sketch, "E3108", {"start": v(-26, -54.07) * mm, "end": v(-25.8, -54.16) * mm});
            skLineSegment(sketch, "E3109", {"start": v(-25.8, -54.16) * mm, "end": v(-25.6, -54.25) * mm});
            skLineSegment(sketch, "E3110", {"start": v(-25.6, -54.25) * mm, "end": v(-25.4, -54.34) * mm});
            skLineSegment(sketch, "E3111", {"start": v(-25.4, -54.34) * mm, "end": v(-25.2, -54.43) * mm});
            skLineSegment(sketch, "E3112", {"start": v(-25.2, -54.43) * mm, "end": v(-25, -54.51) * mm});
            skLineSegment(sketch, "E3113", {"start": v(-25, -54.51) * mm, "end": v(-24.8, -54.6) * mm});
            skLineSegment(sketch, "E3114", {"start": v(-24.8, -54.6) * mm, "end": v(-24.6, -54.7) * mm});
            skLineSegment(sketch, "E3115", {"start": v(-24.6, -54.7) * mm, "end": v(-24.41, -54.78) * mm});
            skLineSegment(sketch, "E3116", {"start": v(-24.41, -54.78) * mm, "end": v(-24.21, -54.87) * mm});
            skLineSegment(sketch, "E3117", {"start": v(-24.21, -54.87) * mm, "end": v(-24.11, -54.91) * mm});
            skLineSegment(sketch, "E3118", {"start": v(-24.11, -54.91) * mm, "end": v(-24.2, -55.11) * mm});
            skLineSegment(sketch, "E3119", {"start": v(-24.2, -55.11) * mm, "end": v(-24.28, -55.31) * mm});
            skLineSegment(sketch, "E3120", {"start": v(-24.28, -55.31) * mm, "end": v(-24.37, -55.52) * mm});
            skLineSegment(sketch, "E3121", {"start": v(-24.37, -55.52) * mm, "end": v(-24.45, -55.72) * mm});
            skLineSegment(sketch, "E3122", {"start": v(-24.45, -55.72) * mm, "end": v(-24.54, -55.92) * mm});
            skLineSegment(sketch, "E3123", {"start": v(-24.54, -55.92) * mm, "end": v(-24.63, -56.13) * mm});
            skLineSegment(sketch, "E3124", {"start": v(-24.63, -56.13) * mm, "end": v(-24.7, -56.33) * mm});
            skLineSegment(sketch, "E3125", {"start": v(-24.7, -56.33) * mm, "end": v(-24.8, -56.53) * mm});
            skLineSegment(sketch, "E3126", {"start": v(-24.8, -56.53) * mm, "end": v(-24.88, -56.74) * mm});
            skLineSegment(sketch, "E3127", {"start": v(-24.88, -56.74) * mm, "end": v(-24.97, -56.94) * mm});
            skLineSegment(sketch, "E3128", {"start": v(-24.97, -56.94) * mm, "end": v(-25.05, -57.14) * mm});
            skLineSegment(sketch, "E3129", {"start": v(-25.05, -57.14) * mm, "end": v(-25.14, -57.34) * mm});
            skLineSegment(sketch, "E3130", {"start": v(-25.14, -57.34) * mm, "end": v(-25.23, -57.56) * mm});
            skLineSegment(sketch, "E3131", {"start": v(-25.23, -57.56) * mm, "end": v(-25.27, -57.78) * mm});
            skLineSegment(sketch, "E3132", {"start": v(-25.27, -57.78) * mm, "end": v(-25.26, -58.01) * mm});
            skLineSegment(sketch, "E3133", {"start": v(-25.26, -58.01) * mm, "end": v(-25.19, -58.23) * mm});
            skLineSegment(sketch, "E3134", {"start": v(-25.19, -58.23) * mm, "end": v(-25.06, -58.42) * mm});
            skLineSegment(sketch, "E3135", {"start": v(-25.06, -58.42) * mm, "end": v(-24.9, -58.57) * mm});
            skLineSegment(sketch, "E3136", {"start": v(-24.9, -58.57) * mm, "end": v(-24.69, -58.67) * mm});
            skLineSegment(sketch, "E3137", {"start": v(-24.69, -58.67) * mm, "end": v(-24.47, -58.71) * mm});
            skLineSegment(sketch, "E3138", {"start": v(-24.47, -58.71) * mm, "end": v(-24.24, -58.7) * mm});
            skLineSegment(sketch, "E3139", {"start": v(-24.24, -58.7) * mm, "end": v(-24.02, -58.63) * mm});
            skLineSegment(sketch, "E3140", {"start": v(-24.02, -58.63) * mm, "end": v(-23.84, -58.5) * mm});
            skLineSegment(sketch, "E3141", {"start": v(-23.84, -58.5) * mm, "end": v(-23.69, -58.33) * mm});
            skLineSegment(sketch, "E3142", {"start": v(-23.69, -58.33) * mm, "end": v(-23.6, -58.13) * mm});
            skLineSegment(sketch, "E3143", {"start": v(-23.6, -58.13) * mm, "end": v(-23.51, -57.93) * mm});
            skLineSegment(sketch, "E3144", {"start": v(-23.51, -57.93) * mm, "end": v(-23.43, -57.73) * mm});
            skLineSegment(sketch, "E3145", {"start": v(-23.43, -57.73) * mm, "end": v(-23.35, -57.53) * mm});
            skLineSegment(sketch, "E3146", {"start": v(-23.35, -57.53) * mm, "end": v(-23.27, -57.32) * mm});
            skLineSegment(sketch, "E3147", {"start": v(-23.27, -57.32) * mm, "end": v(-23.2, -57.11) * mm});
            skLineSegment(sketch, "E3148", {"start": v(-23.2, -57.11) * mm, "end": v(-23.11, -56.91) * mm});
            skLineSegment(sketch, "E3149", {"start": v(-23.11, -56.91) * mm, "end": v(-23.04, -56.7) * mm});
            skLineSegment(sketch, "E3150", {"start": v(-23.04, -56.7) * mm, "end": v(-22.95, -56.5) * mm});
            skLineSegment(sketch, "E3151", {"start": v(-22.95, -56.5) * mm, "end": v(-22.88, -56.3) * mm});
            skLineSegment(sketch, "E3152", {"start": v(-22.88, -56.3) * mm, "end": v(-22.8, -56.1) * mm});
            skLineSegment(sketch, "E3153", {"start": v(-22.8, -56.1) * mm, "end": v(-22.72, -55.88) * mm});
            skLineSegment(sketch, "E3154", {"start": v(-22.72, -55.88) * mm, "end": v(-22.64, -55.68) * mm});
            skLineSegment(sketch, "E3155", {"start": v(-22.64, -55.68) * mm, "end": v(-22.58, -55.53) * mm});
            skLineSegment(sketch, "E3156", {"start": v(-22.58, -55.53) * mm, "end": v(-22.37, -55.6) * mm});
            skLineSegment(sketch, "E3157", {"start": v(-22.37, -55.6) * mm, "end": v(-22.17, -55.68) * mm});
            skLineSegment(sketch, "E3158", {"start": v(-22.17, -55.68) * mm, "end": v(-21.96, -55.76) * mm});
            skLineSegment(sketch, "E3159", {"start": v(-21.96, -55.76) * mm, "end": v(-21.76, -55.83) * mm});
            skLineSegment(sketch, "E3160", {"start": v(-21.76, -55.83) * mm, "end": v(-21.56, -55.9) * mm});
            skLineSegment(sketch, "E3161", {"start": v(-21.56, -55.9) * mm, "end": v(-21.35, -55.98) * mm});
            skLineSegment(sketch, "E3162", {"start": v(-21.35, -55.98) * mm, "end": v(-21.15, -56.05) * mm});
            skLineSegment(sketch, "E3163", {"start": v(-21.15, -56.05) * mm, "end": v(-20.94, -56.13) * mm});
            skLineSegment(sketch, "E3164", {"start": v(-20.94, -56.13) * mm, "end": v(-20.74, -56.2) * mm});
            skLineSegment(sketch, "E3165", {"start": v(-20.74, -56.2) * mm, "end": v(-20.53, -56.28) * mm});
            skLineSegment(sketch, "E3166", {"start": v(-20.53, -56.28) * mm, "end": v(-20.33, -56.35) * mm});
            skLineSegment(sketch, "E3167", {"start": v(-20.33, -56.35) * mm, "end": v(-20.23, -56.39) * mm});
            skLineSegment(sketch, "E3168", {"start": v(-20.23, -56.39) * mm, "end": v(-20.3, -56.6) * mm});
            skLineSegment(sketch, "E3169", {"start": v(-20.3, -56.6) * mm, "end": v(-20.37, -56.8) * mm});
            skLineSegment(sketch, "E3170", {"start": v(-20.37, -56.8) * mm, "end": v(-20.44, -57.01) * mm});
            skLineSegment(sketch, "E3171", {"start": v(-20.44, -57.01) * mm, "end": v(-20.51, -57.22) * mm});
            skLineSegment(sketch, "E3172", {"start": v(-20.51, -57.22) * mm, "end": v(-20.58, -57.42) * mm});
            skLineSegment(sketch, "E3173", {"start": v(-20.58, -57.42) * mm, "end": v(-20.65, -57.64) * mm});
            skLineSegment(sketch, "E3174", {"start": v(-20.65, -57.64) * mm, "end": v(-20.72, -57.84) * mm});
            skLineSegment(sketch, "E3175", {"start": v(-20.72, -57.84) * mm, "end": v(-20.8, -58.05) * mm});
            skLineSegment(sketch, "E3176", {"start": v(-20.8, -58.05) * mm, "end": v(-20.87, -58.26) * mm});
            skLineSegment(sketch, "E3177", {"start": v(-20.87, -58.26) * mm, "end": v(-20.94, -58.47) * mm});
            skLineSegment(sketch, "E3178", {"start": v(-20.94, -58.47) * mm, "end": v(-21, -58.67) * mm});
            skLineSegment(sketch, "E3179", {"start": v(-21, -58.67) * mm, "end": v(-21.08, -58.89) * mm});
            skLineSegment(sketch, "E3180", {"start": v(-21.08, -58.89) * mm, "end": v(-21.15, -59.1) * mm});
            skLineSegment(sketch, "E3181", {"start": v(-21.15, -59.1) * mm, "end": v(-21.18, -59.33) * mm});
            skLineSegment(sketch, "E3182", {"start": v(-21.18, -59.33) * mm, "end": v(-21.15, -59.56) * mm});
            skLineSegment(sketch, "E3183", {"start": v(-21.15, -59.56) * mm, "end": v(-21.07, -59.77) * mm});
            skLineSegment(sketch, "E3184", {"start": v(-21.07, -59.77) * mm, "end": v(-20.93, -59.95) * mm});
            skLineSegment(sketch, "E3185", {"start": v(-20.93, -59.95) * mm, "end": v(-20.75, -60.09) * mm});
            skLineSegment(sketch, "E3186", {"start": v(-20.75, -60.09) * mm, "end": v(-20.54, -60.18) * mm});
            skLineSegment(sketch, "E3187", {"start": v(-20.54, -60.18) * mm, "end": v(-20.31, -60.2) * mm});
            skLineSegment(sketch, "E3188", {"start": v(-20.31, -60.2) * mm, "end": v(-20.09, -60.17) * mm});
            skLineSegment(sketch, "E3189", {"start": v(-20.09, -60.17) * mm, "end": v(-19.88, -60.09) * mm});
            skLineSegment(sketch, "E3190", {"start": v(-19.88, -60.09) * mm, "end": v(-19.7, -59.95) * mm});
            skLineSegment(sketch, "E3191", {"start": v(-19.7, -59.95) * mm, "end": v(-19.56, -59.77) * mm});
            skLineSegment(sketch, "E3192", {"start": v(-19.56, -59.77) * mm, "end": v(-19.48, -59.56) * mm});
            skLineSegment(sketch, "E3193", {"start": v(-19.48, -59.56) * mm, "end": v(-19.41, -59.36) * mm});
            skLineSegment(sketch, "E3194", {"start": v(-19.41, -59.36) * mm, "end": v(-19.35, -59.15) * mm});
            skLineSegment(sketch, "E3195", {"start": v(-19.35, -59.15) * mm, "end": v(-19.29, -58.94) * mm});
            skLineSegment(sketch, "E3196", {"start": v(-19.29, -58.94) * mm, "end": v(-19.22, -58.73) * mm});
            skLineSegment(sketch, "E3197", {"start": v(-19.22, -58.73) * mm, "end": v(-19.15, -58.52) * mm});
            skLineSegment(sketch, "E3198", {"start": v(-19.15, -58.52) * mm, "end": v(-19.1, -58.31) * mm});
            skLineSegment(sketch, "E3199", {"start": v(-19.1, -58.31) * mm, "end": v(-19.03, -58.1) * mm});
            skLineSegment(sketch, "E3200", {"start": v(-19.03, -58.1) * mm, "end": v(-18.96, -57.89) * mm});
            skLineSegment(sketch, "E3201", {"start": v(-18.96, -57.89) * mm, "end": v(-18.9, -57.68) * mm});
            skLineSegment(sketch, "E3202", {"start": v(-18.9, -57.68) * mm, "end": v(-18.83, -57.47) * mm});
            skLineSegment(sketch, "E3203", {"start": v(-18.83, -57.47) * mm, "end": v(-18.76, -57.26) * mm});
            skLineSegment(sketch, "E3204", {"start": v(-18.76, -57.26) * mm, "end": v(-18.7, -57.05) * mm});
            skLineSegment(sketch, "E3205", {"start": v(-18.7, -57.05) * mm, "end": v(-18.65, -56.9) * mm});
            skLineSegment(sketch, "E3206", {"start": v(-18.65, -56.9) * mm, "end": v(-18.44, -56.96) * mm});
            skLineSegment(sketch, "E3207", {"start": v(-18.44, -56.96) * mm, "end": v(-18.23, -57.02) * mm});
            skLineSegment(sketch, "E3208", {"start": v(-18.23, -57.02) * mm, "end": v(-18.02, -57.08) * mm});
            skLineSegment(sketch, "E3209", {"start": v(-18.02, -57.08) * mm, "end": v(-17.82, -57.14) * mm});
            skLineSegment(sketch, "E3210", {"start": v(-17.82, -57.14) * mm, "end": v(-17.6, -57.2) * mm});
            skLineSegment(sketch, "E3211", {"start": v(-17.6, -57.2) * mm, "end": v(-17.4, -57.26) * mm});
            skLineSegment(sketch, "E3212", {"start": v(-17.4, -57.26) * mm, "end": v(-17.19, -57.32) * mm});
            skLineSegment(sketch, "E3213", {"start": v(-17.19, -57.32) * mm, "end": v(-16.98, -57.38) * mm});
            skLineSegment(sketch, "E3214", {"start": v(-16.98, -57.38) * mm, "end": v(-16.77, -57.44) * mm});
            skLineSegment(sketch, "E3215", {"start": v(-16.77, -57.44) * mm, "end": v(-16.56, -57.5) * mm});
            skLineSegment(sketch, "E3216", {"start": v(-16.56, -57.5) * mm, "end": v(-16.35, -57.56) * mm});
            skLineSegment(sketch, "E3217", {"start": v(-16.35, -57.56) * mm, "end": v(-16.25, -57.59) * mm});
            skLineSegment(sketch, "E3218", {"start": v(-16.25, -57.59) * mm, "end": v(-16.3, -57.8) * mm});
            skLineSegment(sketch, "E3219", {"start": v(-16.3, -57.8) * mm, "end": v(-16.36, -58.01) * mm});
            skLineSegment(sketch, "E3220", {"start": v(-16.36, -58.01) * mm, "end": v(-16.42, -58.23) * mm});
            skLineSegment(sketch, "E3221", {"start": v(-16.42, -58.23) * mm, "end": v(-16.47, -58.44) * mm});
            skLineSegment(sketch, "E3222", {"start": v(-16.47, -58.44) * mm, "end": v(-16.53, -58.65) * mm});
            skLineSegment(sketch, "E3223", {"start": v(-16.53, -58.65) * mm, "end": v(-16.58, -58.86) * mm});
            skLineSegment(sketch, "E3224", {"start": v(-16.58, -58.86) * mm, "end": v(-16.64, -59.08) * mm});
            skLineSegment(sketch, "E3225", {"start": v(-16.64, -59.08) * mm, "end": v(-16.7, -59.29) * mm});
            skLineSegment(sketch, "E3226", {"start": v(-16.7, -59.29) * mm, "end": v(-16.75, -59.5) * mm});
            skLineSegment(sketch, "E3227", {"start": v(-16.75, -59.5) * mm, "end": v(-16.8, -59.71) * mm});
            skLineSegment(sketch, "E3228", {"start": v(-16.8, -59.71) * mm, "end": v(-16.86, -59.92) * mm});
            skLineSegment(sketch, "E3229", {"start": v(-16.86, -59.92) * mm, "end": v(-16.92, -60.14) * mm});
            skLineSegment(sketch, "E3230", {"start": v(-16.92, -60.14) * mm, "end": v(-16.98, -60.37) * mm});
            skLineSegment(sketch, "E3231", {"start": v(-16.98, -60.37) * mm, "end": v(-17, -60.6) * mm});
            skLineSegment(sketch, "E3232", {"start": v(-17, -60.6) * mm, "end": v(-16.95, -60.82) * mm});
            skLineSegment(sketch, "E3233", {"start": v(-16.95, -60.82) * mm, "end": v(-16.85, -61.02) * mm});
            skLineSegment(sketch, "E3234", {"start": v(-16.85, -61.02) * mm, "end": v(-16.7, -61.2) * mm});
            skLineSegment(sketch, "E3235", {"start": v(-16.7, -61.2) * mm, "end": v(-16.51, -61.32) * mm});
            skLineSegment(sketch, "E3236", {"start": v(-16.51, -61.32) * mm, "end": v(-16.3, -61.39) * mm});
            skLineSegment(sketch, "E3237", {"start": v(-16.3, -61.39) * mm, "end": v(-16.07, -61.4) * mm});
            skLineSegment(sketch, "E3238", {"start": v(-16.07, -61.4) * mm, "end": v(-15.85, -61.36) * mm});
            skLineSegment(sketch, "E3239", {"start": v(-15.85, -61.36) * mm, "end": v(-15.64, -61.26) * mm});
            skLineSegment(sketch, "E3240", {"start": v(-15.64, -61.26) * mm, "end": v(-15.47, -61.1) * mm});
            skLineSegment(sketch, "E3241", {"start": v(-15.47, -61.1) * mm, "end": v(-15.35, -60.91) * mm});
            skLineSegment(sketch, "E3242", {"start": v(-15.35, -60.91) * mm, "end": v(-15.28, -60.7) * mm});
            skLineSegment(sketch, "E3243", {"start": v(-15.28, -60.7) * mm, "end": v(-15.23, -60.5) * mm});
            skLineSegment(sketch, "E3244", {"start": v(-15.23, -60.5) * mm, "end": v(-15.18, -60.28) * mm});
            skLineSegment(sketch, "E3245", {"start": v(-15.18, -60.28) * mm, "end": v(-15.13, -60.07) * mm});
            skLineSegment(sketch, "E3246", {"start": v(-15.13, -60.07) * mm, "end": v(-15.08, -59.86) * mm});
            skLineSegment(sketch, "E3247", {"start": v(-15.08, -59.86) * mm, "end": v(-15.03, -59.64) * mm});
            skLineSegment(sketch, "E3248", {"start": v(-15.03, -59.64) * mm, "end": v(-14.98, -59.43) * mm});
            skLineSegment(sketch, "E3249", {"start": v(-14.98, -59.43) * mm, "end": v(-14.93, -59.22) * mm});
            skLineSegment(sketch, "E3250", {"start": v(-14.93, -59.22) * mm, "end": v(-14.88, -59) * mm});
            skLineSegment(sketch, "E3251", {"start": v(-14.88, -59) * mm, "end": v(-14.83, -58.79) * mm});
            skLineSegment(sketch, "E3252", {"start": v(-14.83, -58.79) * mm, "end": v(-14.78, -58.57) * mm});
            skLineSegment(sketch, "E3253", {"start": v(-14.78, -58.57) * mm, "end": v(-14.73, -58.36) * mm});
            skLineSegment(sketch, "E3254", {"start": v(-14.73, -58.36) * mm, "end": v(-14.68, -58.14) * mm});
            skLineSegment(sketch, "E3255", {"start": v(-14.68, -58.14) * mm, "end": v(-14.64, -57.99) * mm});
            skLineSegment(sketch, "E3256", {"start": v(-14.64, -57.99) * mm, "end": v(-14.43, -58.03) * mm});
            skLineSegment(sketch, "E3257", {"start": v(-14.43, -58.03) * mm, "end": v(-14.21, -58.08) * mm});
            skLineSegment(sketch, "E3258", {"start": v(-14.21, -58.08) * mm, "end": v(-14, -58.13) * mm});
            skLineSegment(sketch, "E3259", {"start": v(-14, -58.13) * mm, "end": v(-13.79, -58.17) * mm});
            skLineSegment(sketch, "E3260", {"start": v(-13.79, -58.17) * mm, "end": v(-13.58, -58.22) * mm});
            skLineSegment(sketch, "E3261", {"start": v(-13.58, -58.22) * mm, "end": v(-13.36, -58.26) * mm});
            skLineSegment(sketch, "E3262", {"start": v(-13.36, -58.26) * mm, "end": v(-13.15, -58.3) * mm});
            skLineSegment(sketch, "E3263", {"start": v(-13.15, -58.3) * mm, "end": v(-12.94, -58.35) * mm});
            skLineSegment(sketch, "E3264", {"start": v(-12.94, -58.35) * mm, "end": v(-12.72, -58.4) * mm});
            skLineSegment(sketch, "E3265", {"start": v(-12.72, -58.4) * mm, "end": v(-12.5, -58.44) * mm});
            skLineSegment(sketch, "E3266", {"start": v(-12.5, -58.44) * mm, "end": v(-12.3, -58.49) * mm});
            skLineSegment(sketch, "E3267", {"start": v(-12.3, -58.49) * mm, "end": v(-12.2, -58.5) * mm});
            skLineSegment(sketch, "E3268", {"start": v(-12.2, -58.5) * mm, "end": v(-12.23, -58.72) * mm});
            skLineSegment(sketch, "E3269", {"start": v(-12.23, -58.72) * mm, "end": v(-12.27, -58.94) * mm});
            skLineSegment(sketch, "E3270", {"start": v(-12.27, -58.94) * mm, "end": v(-12.32, -59.16) * mm});
            skLineSegment(sketch, "E3271", {"start": v(-12.32, -59.16) * mm, "end": v(-12.36, -59.37) * mm});
            skLineSegment(sketch, "E3272", {"start": v(-12.36, -59.37) * mm, "end": v(-12.4, -59.59) * mm});
            skLineSegment(sketch, "E3273", {"start": v(-12.4, -59.59) * mm, "end": v(-12.44, -59.8) * mm});
            skLineSegment(sketch, "E3274", {"start": v(-12.44, -59.8) * mm, "end": v(-12.48, -60.02) * mm});
            skLineSegment(sketch, "E3275", {"start": v(-12.48, -60.02) * mm, "end": v(-12.52, -60.23) * mm});
            skLineSegment(sketch, "E3276", {"start": v(-12.52, -60.23) * mm, "end": v(-12.56, -60.45) * mm});
            skLineSegment(sketch, "E3277", {"start": v(-12.56, -60.45) * mm, "end": v(-12.6, -60.67) * mm});
            skLineSegment(sketch, "E3278", {"start": v(-12.6, -60.67) * mm, "end": v(-12.65, -60.88) * mm});
            skLineSegment(sketch, "E3279", {"start": v(-12.65, -60.88) * mm, "end": v(-12.69, -61.1) * mm});
            skLineSegment(sketch, "E3280", {"start": v(-12.69, -61.1) * mm, "end": v(-12.73, -61.33) * mm});
            skLineSegment(sketch, "E3281", {"start": v(-12.73, -61.33) * mm, "end": v(-12.73, -61.56) * mm});
            skLineSegment(sketch, "E3282", {"start": v(-12.73, -61.56) * mm, "end": v(-12.67, -61.78) * mm});
            skLineSegment(sketch, "E3283", {"start": v(-12.67, -61.78) * mm, "end": v(-12.55, -61.98) * mm});
            skLineSegment(sketch, "E3284", {"start": v(-12.55, -61.98) * mm, "end": v(-12.4, -62.13) * mm});
            skLineSegment(sketch, "E3285", {"start": v(-12.4, -62.13) * mm, "end": v(-12.2, -62.25) * mm});
            skLineSegment(sketch, "E3286", {"start": v(-12.2, -62.25) * mm, "end": v(-11.98, -62.3) * mm});
            skLineSegment(sketch, "E3287", {"start": v(-11.98, -62.3) * mm, "end": v(-11.75, -62.3) * mm});
            skLineSegment(sketch, "E3288", {"start": v(-11.75, -62.3) * mm, "end": v(-11.53, -62.24) * mm});
            skLineSegment(sketch, "E3289", {"start": v(-11.53, -62.24) * mm, "end": v(-11.33, -62.12) * mm});
            skLineSegment(sketch, "E3290", {"start": v(-11.33, -62.12) * mm, "end": v(-11.17, -61.96) * mm});
            skLineSegment(sketch, "E3291", {"start": v(-11.17, -61.96) * mm, "end": v(-11.06, -61.76) * mm});
            skLineSegment(sketch, "E3292", {"start": v(-11.06, -61.76) * mm, "end": v(-11.01, -61.55) * mm});
            skLineSegment(sketch, "E3293", {"start": v(-11.01, -61.55) * mm, "end": v(-10.97, -61.34) * mm});
            skLineSegment(sketch, "E3294", {"start": v(-10.97, -61.34) * mm, "end": v(-10.94, -61.12) * mm});
            skLineSegment(sketch, "E3295", {"start": v(-10.94, -61.12) * mm, "end": v(-10.9, -60.9) * mm});
            skLineSegment(sketch, "E3296", {"start": v(-10.9, -60.9) * mm, "end": v(-10.87, -60.7) * mm});
            skLineSegment(sketch, "E3297", {"start": v(-10.87, -60.7) * mm, "end": v(-10.83, -60.47) * mm});
            skLineSegment(sketch, "E3298", {"start": v(-10.83, -60.47) * mm, "end": v(-10.8, -60.26) * mm});
            skLineSegment(sketch, "E3299", {"start": v(-10.8, -60.26) * mm, "end": v(-10.76, -60.04) * mm});
            skLineSegment(sketch, "E3300", {"start": v(-10.76, -60.04) * mm, "end": v(-10.73, -59.82) * mm});
            skLineSegment(sketch, "E3301", {"start": v(-10.73, -59.82) * mm, "end": v(-10.7, -59.6) * mm});
            skLineSegment(sketch, "E3302", {"start": v(-10.7, -59.6) * mm, "end": v(-10.66, -59.4) * mm});
            skLineSegment(sketch, "E3303", {"start": v(-10.66, -59.4) * mm, "end": v(-10.62, -59.17) * mm});
            skLineSegment(sketch, "E3304", {"start": v(-10.62, -59.17) * mm, "end": v(-10.59, -58.95) * mm});
            skLineSegment(sketch, "E3305", {"start": v(-10.59, -58.95) * mm, "end": v(-10.56, -58.8) * mm});
            skLineSegment(sketch, "E3306", {"start": v(-10.56, -58.8) * mm, "end": v(-10.35, -58.83) * mm});
            skLineSegment(sketch, "E3307", {"start": v(-10.35, -58.83) * mm, "end": v(-10.13, -58.86) * mm});
            skLineSegment(sketch, "E3308", {"start": v(-10.13, -58.86) * mm, "end": v(-9.92, -58.89) * mm});
            skLineSegment(sketch, "E3309", {"start": v(-9.92, -58.89) * mm, "end": v(-9.7, -58.92) * mm});
            skLineSegment(sketch, "E3310", {"start": v(-9.7, -58.92) * mm, "end": v(-9.48, -58.95) * mm});
            skLineSegment(sketch, "E3311", {"start": v(-9.48, -58.95) * mm, "end": v(-9.27, -58.98) * mm});
            skLineSegment(sketch, "E3312", {"start": v(-9.27, -58.98) * mm, "end": v(-9.05, -59) * mm});
            skLineSegment(sketch, "E3313", {"start": v(-9.05, -59) * mm, "end": v(-8.84, -59.04) * mm});
            skLineSegment(sketch, "E3314", {"start": v(-8.84, -59.04) * mm, "end": v(-8.62, -59.07) * mm});
            skLineSegment(sketch, "E3315", {"start": v(-8.62, -59.07) * mm, "end": v(-8.4, -59.1) * mm});
            skLineSegment(sketch, "E3316", {"start": v(-8.4, -59.1) * mm, "end": v(-8.19, -59.13) * mm});
            skLineSegment(sketch, "E3317", {"start": v(-8.19, -59.13) * mm, "end": v(-8.08, -59.15) * mm});
            skLineSegment(sketch, "E3318", {"start": v(-8.08, -59.15) * mm, "end": v(-8.11, -59.36) * mm});
            skLineSegment(sketch, "E3319", {"start": v(-8.11, -59.36) * mm, "end": v(-8.14, -59.58) * mm});
            skLineSegment(sketch, "E3320", {"start": v(-8.14, -59.58) * mm, "end": v(-8.16, -59.8) * mm});
            skLineSegment(sketch, "E3321", {"start": v(-8.16, -59.8) * mm, "end": v(-8.19, -60.02) * mm});
            skLineSegment(sketch, "E3322", {"start": v(-8.19, -60.02) * mm, "end": v(-8.21, -60.23) * mm});
            skLineSegment(sketch, "E3323", {"start": v(-8.21, -60.23) * mm, "end": v(-8.24, -60.46) * mm});
            skLineSegment(sketch, "E3324", {"start": v(-8.24, -60.46) * mm, "end": v(-8.27, -60.67) * mm});
            skLineSegment(sketch, "E3325", {"start": v(-8.27, -60.67) * mm, "end": v(-8.3, -60.89) * mm});
            skLineSegment(sketch, "E3326", {"start": v(-8.3, -60.89) * mm, "end": v(-8.32, -61.11) * mm});
            skLineSegment(sketch, "E3327", {"start": v(-8.32, -61.11) * mm, "end": v(-8.34, -61.33) * mm});
            skLineSegment(sketch, "E3328", {"start": v(-8.34, -61.33) * mm, "end": v(-8.37, -61.54) * mm});
            skLineSegment(sketch, "E3329", {"start": v(-8.37, -61.54) * mm, "end": v(-8.4, -61.77) * mm});
            skLineSegment(sketch, "E3330", {"start": v(-8.4, -61.77) * mm, "end": v(-8.42, -62) * mm});
            skLineSegment(sketch, "E3331", {"start": v(-8.42, -62) * mm, "end": v(-8.4, -62.23) * mm});
            skLineSegment(sketch, "E3332", {"start": v(-8.4, -62.23) * mm, "end": v(-8.33, -62.44) * mm});
            skLineSegment(sketch, "E3333", {"start": v(-8.33, -62.44) * mm, "end": v(-8.2, -62.63) * mm});
            skLineSegment(sketch, "E3334", {"start": v(-8.2, -62.63) * mm, "end": v(-8.03, -62.78) * mm});
            skLineSegment(sketch, "E3335", {"start": v(-8.03, -62.78) * mm, "end": v(-7.83, -62.87) * mm});
            skLineSegment(sketch, "E3336", {"start": v(-7.83, -62.87) * mm, "end": v(-7.6, -62.92) * mm});
            skLineSegment(sketch, "E3337", {"start": v(-7.6, -62.92) * mm, "end": v(-7.38, -62.9) * mm});
            skLineSegment(sketch, "E3338", {"start": v(-7.38, -62.9) * mm, "end": v(-7.16, -62.82) * mm});
            skLineSegment(sketch, "E3339", {"start": v(-7.16, -62.82) * mm, "end": v(-6.97, -62.7) * mm});
            skLineSegment(sketch, "E3340", {"start": v(-6.97, -62.7) * mm, "end": v(-6.83, -62.52) * mm});
            skLineSegment(sketch, "E3341", {"start": v(-6.83, -62.52) * mm, "end": v(-6.73, -62.31) * mm});
            skLineSegment(sketch, "E3342", {"start": v(-6.73, -62.31) * mm, "end": v(-6.7, -62.1) * mm});
            skLineSegment(sketch, "E3343", {"start": v(-6.7, -62.1) * mm, "end": v(-6.67, -61.88) * mm});
            skLineSegment(sketch, "E3344", {"start": v(-6.67, -61.88) * mm, "end": v(-6.65, -61.67) * mm});
            skLineSegment(sketch, "E3345", {"start": v(-6.65, -61.67) * mm, "end": v(-6.63, -61.45) * mm});
            skLineSegment(sketch, "E3346", {"start": v(-6.63, -61.45) * mm, "end": v(-6.61, -61.23) * mm});
            skLineSegment(sketch, "E3347", {"start": v(-6.61, -61.23) * mm, "end": v(-6.6, -61) * mm});
            skLineSegment(sketch, "E3348", {"start": v(-6.6, -61) * mm, "end": v(-6.57, -60.8) * mm});
            skLineSegment(sketch, "E3349", {"start": v(-6.57, -60.8) * mm, "end": v(-6.55, -60.57) * mm});
            skLineSegment(sketch, "E3350", {"start": v(-6.55, -60.57) * mm, "end": v(-6.53, -60.35) * mm});
            skLineSegment(sketch, "E3351", {"start": v(-6.53, -60.35) * mm, "end": v(-6.51, -60.13) * mm});
            skLineSegment(sketch, "E3352", {"start": v(-6.51, -60.13) * mm, "end": v(-6.5, -59.92) * mm});
            skLineSegment(sketch, "E3353", {"start": v(-6.5, -59.92) * mm, "end": v(-6.47, -59.7) * mm});
            skLineSegment(sketch, "E3354", {"start": v(-6.47, -59.7) * mm, "end": v(-6.45, -59.48) * mm});
            skLineSegment(sketch, "E3355", {"start": v(-6.45, -59.48) * mm, "end": v(-6.44, -59.32) * mm});
            skLineSegment(sketch, "E3356", {"start": v(-6.44, -59.32) * mm, "end": v(-6.22, -59.33) * mm});
            skLineSegment(sketch, "E3357", {"start": v(-6.22, -59.33) * mm, "end": v(-6, -59.35) * mm});
            skLineSegment(sketch, "E3358", {"start": v(-6, -59.35) * mm, "end": v(-5.79, -59.36) * mm});
            skLineSegment(sketch, "E3359", {"start": v(-5.79, -59.36) * mm, "end": v(-5.57, -59.38) * mm});
            skLineSegment(sketch, "E3360", {"start": v(-5.57, -59.38) * mm, "end": v(-5.35, -59.4) * mm});
            skLineSegment(sketch, "E3361", {"start": v(-5.35, -59.4) * mm, "end": v(-5.13, -59.4) * mm});
            skLineSegment(sketch, "E3362", {"start": v(-5.13, -59.4) * mm, "end": v(-4.92, -59.42) * mm});
            skLineSegment(sketch, "E3363", {"start": v(-4.92, -59.42) * mm, "end": v(-4.7, -59.44) * mm});
            skLineSegment(sketch, "E3364", {"start": v(-4.7, -59.44) * mm, "end": v(-4.48, -59.46) * mm});
            skLineSegment(sketch, "E3365", {"start": v(-4.48, -59.46) * mm, "end": v(-4.26, -59.47) * mm});
            skLineSegment(sketch, "E3366", {"start": v(-4.26, -59.47) * mm, "end": v(-4.05, -59.49) * mm});
            skLineSegment(sketch, "E3367", {"start": v(-4.05, -59.49) * mm, "end": v(-3.94, -59.5) * mm});
            skLineSegment(sketch, "E3368", {"start": v(-3.94, -59.5) * mm, "end": v(-3.95, -59.71) * mm});
            skLineSegment(sketch, "E3369", {"start": v(-3.95, -59.71) * mm, "end": v(-3.96, -59.93) * mm});
            skLineSegment(sketch, "E3370", {"start": v(-3.96, -59.93) * mm, "end": v(-3.97, -60.15) * mm});
            skLineSegment(sketch, "E3371", {"start": v(-3.97, -60.15) * mm, "end": v(-3.98, -60.37) * mm});
            skLineSegment(sketch, "E3372", {"start": v(-3.98, -60.37) * mm, "end": v(-4, -60.59) * mm});
            skLineSegment(sketch, "E3373", {"start": v(-4, -60.59) * mm, "end": v(-4, -60.81) * mm});
            skLineSegment(sketch, "E3374", {"start": v(-4, -60.81) * mm, "end": v(-4.02, -61.03) * mm});
            skLineSegment(sketch, "E3375", {"start": v(-4.02, -61.03) * mm, "end": v(-4.03, -61.25) * mm});
            skLineSegment(sketch, "E3376", {"start": v(-4.03, -61.25) * mm, "end": v(-4.04, -61.47) * mm});
            skLineSegment(sketch, "E3377", {"start": v(-4.04, -61.47) * mm, "end": v(-4.05, -61.69) * mm});
            skLineSegment(sketch, "E3378", {"start": v(-4.05, -61.69) * mm, "end": v(-4.06, -61.9) * mm});
            skLineSegment(sketch, "E3379", {"start": v(-4.06, -61.9) * mm, "end": v(-4.07, -62.13) * mm});
            skLineSegment(sketch, "E3380", {"start": v(-4.07, -62.13) * mm, "end": v(-4.08, -62.36) * mm});
            skLineSegment(sketch, "E3381", {"start": v(-4.08, -62.36) * mm, "end": v(-4.05, -62.59) * mm});
            skLineSegment(sketch, "E3382", {"start": v(-4.05, -62.59) * mm, "end": v(-3.96, -62.8) * mm});
            skLineSegment(sketch, "E3383", {"start": v(-3.96, -62.8) * mm, "end": v(-3.82, -62.98) * mm});
            skLineSegment(sketch, "E3384", {"start": v(-3.82, -62.98) * mm, "end": v(-3.63, -63.11) * mm});
            skLineSegment(sketch, "E3385", {"start": v(-3.63, -63.11) * mm, "end": v(-3.42, -63.2) * mm});
            skLineSegment(sketch, "E3386", {"start": v(-3.42, -63.2) * mm, "end": v(-3.2, -63.22) * mm});
            skLineSegment(sketch, "E3387", {"start": v(-3.2, -63.22) * mm, "end": v(-2.97, -63.19) * mm});
            skLineSegment(sketch, "E3388", {"start": v(-2.97, -63.19) * mm, "end": v(-2.76, -63.1) * mm});
            skLineSegment(sketch, "E3389", {"start": v(-2.76, -63.1) * mm, "end": v(-2.59, -62.95) * mm});
            skLineSegment(sketch, "E3390", {"start": v(-2.59, -62.95) * mm, "end": v(-2.45, -62.77) * mm});
            skLineSegment(sketch, "E3391", {"start": v(-2.45, -62.77) * mm, "end": v(-2.37, -62.56) * mm});
            skLineSegment(sketch, "E3392", {"start": v(-2.37, -62.56) * mm, "end": v(-2.35, -62.34) * mm});
            skLineSegment(sketch, "E3393", {"start": v(-2.35, -62.34) * mm, "end": v(-2.34, -62.12) * mm});
            skLineSegment(sketch, "E3394", {"start": v(-2.34, -62.12) * mm, "end": v(-2.34, -61.9) * mm});
            skLineSegment(sketch, "E3395", {"start": v(-2.34, -61.9) * mm, "end": v(-2.33, -61.69) * mm});
            skLineSegment(sketch, "E3396", {"start": v(-2.33, -61.69) * mm, "end": v(-2.33, -61.47) * mm});
            skLineSegment(sketch, "E3397", {"start": v(-2.33, -61.47) * mm, "end": v(-2.32, -61.25) * mm});
            skLineSegment(sketch, "E3398", {"start": v(-2.32, -61.25) * mm, "end": v(-2.32, -61.03) * mm});
            skLineSegment(sketch, "E3399", {"start": v(-2.32, -61.03) * mm, "end": v(-2.31, -60.81) * mm});
            skLineSegment(sketch, "E3400", {"start": v(-2.31, -60.81) * mm, "end": v(-2.3, -60.59) * mm});
            skLineSegment(sketch, "E3401", {"start": v(-2.3, -60.59) * mm, "end": v(-2.3, -60.37) * mm});
            skLineSegment(sketch, "E3402", {"start": v(-2.3, -60.37) * mm, "end": v(-2.3, -60.15) * mm});
            skLineSegment(sketch, "E3403", {"start": v(-2.3, -60.15) * mm, "end": v(-2.3, -59.93) * mm});
            skLineSegment(sketch, "E3404", {"start": v(-2.3, -59.93) * mm, "end": v(-2.3, -59.71) * mm});
            skLineSegment(sketch, "E3405", {"start": v(-2.3, -59.71) * mm, "end": v(-2.29, -59.55) * mm});
            skLineSegment(sketch, "E3406", {"start": v(-2.29, -59.55) * mm, "end": v(-2.07, -59.55) * mm});
            skLineSegment(sketch, "E3407", {"start": v(-2.07, -59.55) * mm, "end": v(-1.85, -59.55) * mm});
            skLineSegment(sketch, "E3408", {"start": v(-1.85, -59.55) * mm, "end": v(-1.63, -59.55) * mm});
            skLineSegment(sketch, "E3409", {"start": v(-1.63, -59.55) * mm, "end": v(-1.42, -59.55) * mm});
            skLineSegment(sketch, "E3410", {"start": v(-1.42, -59.55) * mm, "end": v(-1.2, -59.55) * mm});
            skLineSegment(sketch, "E3411", {"start": v(-1.2, -59.55) * mm, "end": v(-0.98, -59.55) * mm});
            skLineSegment(sketch, "E3412", {"start": v(-0.98, -59.55) * mm, "end": v(-0.76, -59.55) * mm});
            skLineSegment(sketch, "E3413", {"start": v(-0.76, -59.55) * mm, "end": v(-0.54, -59.55) * mm});
            skLineSegment(sketch, "E3414", {"start": v(-0.54, -59.55) * mm, "end": v(-0.33, -59.55) * mm});
            skLineSegment(sketch, "E3415", {"start": v(-0.33, -59.55) * mm, "end": v(-0.1, -59.55) * mm});
            skLineSegment(sketch, "E3416", {"start": v(-0.1, -59.55) * mm, "end": v(0.1, -59.55) * mm});
            skLineSegment(sketch, "E3417", {"start": v(0.1, -59.55) * mm, "end": v(0.22, -59.55) * mm});
            skLineSegment(sketch, "E3418", {"start": v(0.22, -59.55) * mm, "end": v(0.22, -59.77) * mm});
            skLineSegment(sketch, "E3419", {"start": v(0.22, -59.77) * mm, "end": v(0.22, -59.99) * mm});
            skLineSegment(sketch, "E3420", {"start": v(0.22, -59.99) * mm, "end": v(0.23, -60.21) * mm});
            skLineSegment(sketch, "E3421", {"start": v(0.23, -60.21) * mm, "end": v(0.23, -60.43) * mm});
            skLineSegment(sketch, "E3422", {"start": v(0.23, -60.43) * mm, "end": v(0.24, -60.65) * mm});
            skLineSegment(sketch, "E3423", {"start": v(0.24, -60.65) * mm, "end": v(0.24, -60.87) * mm});
            skLineSegment(sketch, "E3424", {"start": v(0.24, -60.87) * mm, "end": v(0.25, -61.09) * mm});
            skLineSegment(sketch, "E3425", {"start": v(0.25, -61.09) * mm, "end": v(0.25, -61.3) * mm});
            skLineSegment(sketch, "E3426", {"start": v(0.25, -61.3) * mm, "end": v(0.26, -61.53) * mm});
            skLineSegment(sketch, "E3427", {"start": v(0.26, -61.53) * mm, "end": v(0.26, -61.75) * mm});
            skLineSegment(sketch, "E3428", {"start": v(0.26, -61.75) * mm, "end": v(0.27, -61.97) * mm});
            skLineSegment(sketch, "E3429", {"start": v(0.27, -61.97) * mm, "end": v(0.27, -62.19) * mm});
            skLineSegment(sketch, "E3430", {"start": v(0.27, -62.19) * mm, "end": v(0.28, -62.42) * mm});
            skLineSegment(sketch, "E3431", {"start": v(0.28, -62.42) * mm, "end": v(0.33, -62.65) * mm});
            skLineSegment(sketch, "E3432", {"start": v(0.33, -62.65) * mm, "end": v(0.43, -62.85) * mm});
            skLineSegment(sketch, "E3433", {"start": v(0.43, -62.85) * mm, "end": v(0.58, -63.02) * mm});
            skLineSegment(sketch, "E3434", {"start": v(0.58, -63.02) * mm, "end": v(0.77, -63.14) * mm});
            skLineSegment(sketch, "E3435", {"start": v(0.77, -63.14) * mm, "end": v(1, -63.2) * mm});
            skLineSegment(sketch, "E3436", {"start": v(1, -63.2) * mm, "end": v(1.22, -63.22) * mm});
            skLineSegment(sketch, "E3437", {"start": v(1.22, -63.22) * mm, "end": v(1.44, -63.17) * mm});
            skLineSegment(sketch, "E3438", {"start": v(1.44, -63.17) * mm, "end": v(1.64, -63.06) * mm});
            skLineSegment(sketch, "E3439", {"start": v(1.64, -63.06) * mm, "end": v(1.8, -62.9) * mm});
            skLineSegment(sketch, "E3440", {"start": v(1.8, -62.9) * mm, "end": v(1.93, -62.72) * mm});
            skLineSegment(sketch, "E3441", {"start": v(1.93, -62.72) * mm, "end": v(2, -62.5) * mm});
            skLineSegment(sketch, "E3442", {"start": v(2, -62.5) * mm, "end": v(2, -62.28) * mm});
            skLineSegment(sketch, "E3443", {"start": v(2, -62.28) * mm, "end": v(2, -62.06) * mm});
            skLineSegment(sketch, "E3444", {"start": v(2, -62.06) * mm, "end": v(1.99, -61.85) * mm});
            skLineSegment(sketch, "E3445", {"start": v(1.99, -61.85) * mm, "end": v(1.97, -61.63) * mm});
            skLineSegment(sketch, "E3446", {"start": v(1.97, -61.63) * mm, "end": v(1.96, -61.41) * mm});
            skLineSegment(sketch, "E3447", {"start": v(1.96, -61.41) * mm, "end": v(1.95, -61.19) * mm});
            skLineSegment(sketch, "E3448", {"start": v(1.95, -61.19) * mm, "end": v(1.94, -60.97) * mm});
            skLineSegment(sketch, "E3449", {"start": v(1.94, -60.97) * mm, "end": v(1.93, -60.75) * mm});
            skLineSegment(sketch, "E3450", {"start": v(1.93, -60.75) * mm, "end": v(1.92, -60.53) * mm});
            skLineSegment(sketch, "E3451", {"start": v(1.92, -60.53) * mm, "end": v(1.91, -60.31) * mm});
            skLineSegment(sketch, "E3452", {"start": v(1.91, -60.31) * mm, "end": v(1.9, -60.1) * mm});
            skLineSegment(sketch, "E3453", {"start": v(1.9, -60.1) * mm, "end": v(1.89, -59.87) * mm});
            skLineSegment(sketch, "E3454", {"start": v(1.89, -59.87) * mm, "end": v(1.88, -59.65) * mm});
            skLineSegment(sketch, "E3455", {"start": v(1.88, -59.65) * mm, "end": v(1.87, -59.5) * mm});
            skLineSegment(sketch, "E3456", {"start": v(1.87, -59.5) * mm, "end": v(2.09, -59.48) * mm});
            skLineSegment(sketch, "E3457", {"start": v(2.09, -59.48) * mm, "end": v(2.3, -59.46) * mm});
            skLineSegment(sketch, "E3458", {"start": v(2.3, -59.46) * mm, "end": v(2.52, -59.45) * mm});
            skLineSegment(sketch, "E3459", {"start": v(2.52, -59.45) * mm, "end": v(2.74, -59.43) * mm});
            skLineSegment(sketch, "E3460", {"start": v(2.74, -59.43) * mm, "end": v(2.96, -59.42) * mm});
            skLineSegment(sketch, "E3461", {"start": v(2.96, -59.42) * mm, "end": v(3.17, -59.4) * mm});
            skLineSegment(sketch, "E3462", {"start": v(3.17, -59.4) * mm, "end": v(3.4, -59.39) * mm});
            skLineSegment(sketch, "E3463", {"start": v(3.4, -59.39) * mm, "end": v(3.6, -59.37) * mm});
            skLineSegment(sketch, "E3464", {"start": v(3.6, -59.37) * mm, "end": v(3.83, -59.36) * mm});
            skLineSegment(sketch, "E3465", {"start": v(3.83, -59.36) * mm, "end": v(4.04, -59.34) * mm});
            skLineSegment(sketch, "E3466", {"start": v(4.04, -59.34) * mm, "end": v(4.26, -59.33) * mm});
            skLineSegment(sketch, "E3467", {"start": v(4.26, -59.33) * mm, "end": v(4.37, -59.32) * mm});
            skLineSegment(sketch, "E3468", {"start": v(4.37, -59.32) * mm, "end": v(4.39, -59.54) * mm});
            skLineSegment(sketch, "E3469", {"start": v(4.39, -59.54) * mm, "end": v(4.4, -59.75) * mm});
            skLineSegment(sketch, "E3470", {"start": v(4.4, -59.75) * mm, "end": v(4.43, -59.98) * mm});
            skLineSegment(sketch, "E3471", {"start": v(4.43, -59.98) * mm, "end": v(4.45, -60.2) * mm});
            skLineSegment(sketch, "E3472", {"start": v(4.45, -60.2) * mm, "end": v(4.47, -60.4) * mm});
            skLineSegment(sketch, "E3473", {"start": v(4.47, -60.4) * mm, "end": v(4.49, -60.63) * mm});
            skLineSegment(sketch, "E3474", {"start": v(4.49, -60.63) * mm, "end": v(4.5, -60.85) * mm});
            skLineSegment(sketch, "E3475", {"start": v(4.5, -60.85) * mm, "end": v(4.53, -61.07) * mm});
            skLineSegment(sketch, "E3476", {"start": v(4.53, -61.07) * mm, "end": v(4.55, -61.29) * mm});
            skLineSegment(sketch, "E3477", {"start": v(4.55, -61.29) * mm, "end": v(4.57, -61.5) * mm});
            skLineSegment(sketch, "E3478", {"start": v(4.57, -61.5) * mm, "end": v(4.59, -61.72) * mm});
            skLineSegment(sketch, "E3479", {"start": v(4.59, -61.72) * mm, "end": v(4.6, -61.95) * mm});
            skLineSegment(sketch, "E3480", {"start": v(4.6, -61.95) * mm, "end": v(4.63, -62.18) * mm});
            skLineSegment(sketch, "E3481", {"start": v(4.63, -62.18) * mm, "end": v(4.7, -62.4) * mm});
            skLineSegment(sketch, "E3482", {"start": v(4.7, -62.4) * mm, "end": v(4.8, -62.6) * mm});
            skLineSegment(sketch, "E3483", {"start": v(4.8, -62.6) * mm, "end": v(4.97, -62.75) * mm});
            skLineSegment(sketch, "E3484", {"start": v(4.97, -62.75) * mm, "end": v(5.17, -62.86) * mm});
            skLineSegment(sketch, "E3485", {"start": v(5.17, -62.86) * mm, "end": v(5.4, -62.91) * mm});
            skLineSegment(sketch, "E3486", {"start": v(5.4, -62.91) * mm, "end": v(5.62, -62.9) * mm});
            skLineSegment(sketch, "E3487", {"start": v(5.62, -62.9) * mm, "end": v(5.84, -62.84) * mm});
            skLineSegment(sketch, "E3488", {"start": v(5.84, -62.84) * mm, "end": v(6.03, -62.72) * mm});
            skLineSegment(sketch, "E3489", {"start": v(6.03, -62.72) * mm, "end": v(6.19, -62.56) * mm});
            skLineSegment(sketch, "E3490", {"start": v(6.19, -62.56) * mm, "end": v(6.3, -62.36) * mm});
            skLineSegment(sketch, "E3491", {"start": v(6.3, -62.36) * mm, "end": v(6.35, -62.14) * mm});
            skLineSegment(sketch, "E3492", {"start": v(6.35, -62.14) * mm, "end": v(6.34, -61.92) * mm});
            skLineSegment(sketch, "E3493", {"start": v(6.34, -61.92) * mm, "end": v(6.32, -61.7) * mm});
            skLineSegment(sketch, "E3494", {"start": v(6.32, -61.7) * mm, "end": v(6.3, -61.49) * mm});
            skLineSegment(sketch, "E3495", {"start": v(6.3, -61.49) * mm, "end": v(6.27, -61.27) * mm});
            skLineSegment(sketch, "E3496", {"start": v(6.27, -61.27) * mm, "end": v(6.24, -61.05) * mm});
            skLineSegment(sketch, "E3497", {"start": v(6.24, -61.05) * mm, "end": v(6.21, -60.83) * mm});
            skLineSegment(sketch, "E3498", {"start": v(6.21, -60.83) * mm, "end": v(6.19, -60.61) * mm});
            skLineSegment(sketch, "E3499", {"start": v(6.19, -60.61) * mm, "end": v(6.16, -60.4) * mm});
            skLineSegment(sketch, "E3500", {"start": v(6.16, -60.4) * mm, "end": v(6.14, -60.18) * mm});
            skLineSegment(sketch, "E3501", {"start": v(6.14, -60.18) * mm, "end": v(6.1, -59.96) * mm});
            skLineSegment(sketch, "E3502", {"start": v(6.1, -59.96) * mm, "end": v(6.08, -59.74) * mm});
            skLineSegment(sketch, "E3503", {"start": v(6.08, -59.74) * mm, "end": v(6.06, -59.52) * mm});
            skLineSegment(sketch, "E3504", {"start": v(6.06, -59.52) * mm, "end": v(6.03, -59.3) * mm});
            skLineSegment(sketch, "E3505", {"start": v(6.03, -59.3) * mm, "end": v(6.01, -59.15) * mm});
            skLineSegment(sketch, "E3506", {"start": v(6.01, -59.15) * mm, "end": v(6.23, -59.12) * mm});
            skLineSegment(sketch, "E3507", {"start": v(6.23, -59.12) * mm, "end": v(6.44, -59.08) * mm});
            skLineSegment(sketch, "E3508", {"start": v(6.44, -59.08) * mm, "end": v(6.66, -59.05) * mm});
            skLineSegment(sketch, "E3509", {"start": v(6.66, -59.05) * mm, "end": v(6.88, -59.02) * mm});
            skLineSegment(sketch, "E3510", {"start": v(6.88, -59.02) * mm, "end": v(7.1, -59) * mm});
            skLineSegment(sketch, "E3511", {"start": v(7.1, -59) * mm, "end": v(7.3, -58.96) * mm});
            skLineSegment(sketch, "E3512", {"start": v(7.3, -58.96) * mm, "end": v(7.52, -58.93) * mm});
            skLineSegment(sketch, "E3513", {"start": v(7.52, -58.93) * mm, "end": v(7.74, -58.9) * mm});
            skLineSegment(sketch, "E3514", {"start": v(7.74, -58.9) * mm, "end": v(7.95, -58.87) * mm});
            skLineSegment(sketch, "E3515", {"start": v(7.95, -58.87) * mm, "end": v(8.17, -58.84) * mm});
            skLineSegment(sketch, "E3516", {"start": v(8.17, -58.84) * mm, "end": v(8.39, -58.81) * mm});
            skLineSegment(sketch, "E3517", {"start": v(8.39, -58.81) * mm, "end": v(8.5, -58.8) * mm});
            skLineSegment(sketch, "E3518", {"start": v(8.5, -58.8) * mm, "end": v(8.53, -59.01) * mm});
            skLineSegment(sketch, "E3519", {"start": v(8.53, -59.01) * mm, "end": v(8.56, -59.23) * mm});
            skLineSegment(sketch, "E3520", {"start": v(8.56, -59.23) * mm, "end": v(8.6, -59.45) * mm});
            skLineSegment(sketch, "E3521", {"start": v(8.6, -59.45) * mm, "end": v(8.63, -59.66) * mm});
            skLineSegment(sketch, "E3522", {"start": v(8.63, -59.66) * mm, "end": v(8.67, -59.88) * mm});
            skLineSegment(sketch, "E3523", {"start": v(8.67, -59.88) * mm, "end": v(8.7, -60.1) * mm});
            skLineSegment(sketch, "E3524", {"start": v(8.7, -60.1) * mm, "end": v(8.74, -60.31) * mm});
            skLineSegment(sketch, "E3525", {"start": v(8.74, -60.31) * mm, "end": v(8.77, -60.53) * mm});
            skLineSegment(sketch, "E3526", {"start": v(8.77, -60.53) * mm, "end": v(8.8, -60.75) * mm});
            skLineSegment(sketch, "E3527", {"start": v(8.8, -60.75) * mm, "end": v(8.84, -60.97) * mm});
            skLineSegment(sketch, "E3528", {"start": v(8.84, -60.97) * mm, "end": v(8.88, -61.18) * mm});
            skLineSegment(sketch, "E3529", {"start": v(8.88, -61.18) * mm, "end": v(8.91, -61.4) * mm});
            skLineSegment(sketch, "E3530", {"start": v(8.91, -61.4) * mm, "end": v(8.95, -61.63) * mm});
            skLineSegment(sketch, "E3531", {"start": v(8.95, -61.63) * mm, "end": v(9.03, -61.85) * mm});
            skLineSegment(sketch, "E3532", {"start": v(9.03, -61.85) * mm, "end": v(9.16, -62.03) * mm});
            skLineSegment(sketch, "E3533", {"start": v(9.16, -62.03) * mm, "end": v(9.34, -62.18) * mm});
            skLineSegment(sketch, "E3534", {"start": v(9.34, -62.18) * mm, "end": v(9.54, -62.27) * mm});
            skLineSegment(sketch, "E3535", {"start": v(9.54, -62.27) * mm, "end": v(9.77, -62.3) * mm});
            skLineSegment(sketch, "E3536", {"start": v(9.77, -62.3) * mm, "end": v(10, -62.29) * mm});
            skLineSegment(sketch, "E3537", {"start": v(10, -62.29) * mm, "end": v(10.2, -62.2) * mm});
            skLineSegment(sketch, "E3538", {"start": v(10.2, -62.2) * mm, "end": v(10.4, -62.08) * mm});
            skLineSegment(sketch, "E3539", {"start": v(10.4, -62.08) * mm, "end": v(10.54, -61.9) * mm});
            skLineSegment(sketch, "E3540", {"start": v(10.54, -61.9) * mm, "end": v(10.63, -61.7) * mm});
            skLineSegment(sketch, "E3541", {"start": v(10.63, -61.7) * mm, "end": v(10.67, -61.47) * mm});
            skLineSegment(sketch, "E3542", {"start": v(10.67, -61.47) * mm, "end": v(10.64, -61.25) * mm});
            skLineSegment(sketch, "E3543", {"start": v(10.64, -61.25) * mm, "end": v(10.6, -61.04) * mm});
            skLineSegment(sketch, "E3544", {"start": v(10.6, -61.04) * mm, "end": v(10.56, -60.82) * mm});
            skLineSegment(sketch, "E3545", {"start": v(10.56, -60.82) * mm, "end": v(10.52, -60.61) * mm});
            skLineSegment(sketch, "E3546", {"start": v(10.52, -60.61) * mm, "end": v(10.48, -60.4) * mm});
            skLineSegment(sketch, "E3547", {"start": v(10.48, -60.4) * mm, "end": v(10.44, -60.18) * mm});
            skLineSegment(sketch, "E3548", {"start": v(10.44, -60.18) * mm, "end": v(10.4, -59.96) * mm});
            skLineSegment(sketch, "E3549", {"start": v(10.4, -59.96) * mm, "end": v(10.36, -59.75) * mm});
            skLineSegment(sketch, "E3550", {"start": v(10.36, -59.75) * mm, "end": v(10.32, -59.53) * mm});
            skLineSegment(sketch, "E3551", {"start": v(10.32, -59.53) * mm, "end": v(10.28, -59.31) * mm});
            skLineSegment(sketch, "E3552", {"start": v(10.28, -59.31) * mm, "end": v(10.23, -59.1) * mm});
            skLineSegment(sketch, "E3553", {"start": v(10.23, -59.1) * mm, "end": v(10.2, -58.88) * mm});
            skLineSegment(sketch, "E3554", {"start": v(10.2, -58.88) * mm, "end": v(10.15, -58.67) * mm});
            skLineSegment(sketch, "E3555", {"start": v(10.15, -58.67) * mm, "end": v(10.12, -58.5) * mm});
            skLineSegment(sketch, "E3556", {"start": v(10.12, -58.5) * mm, "end": v(10.33, -58.46) * mm});
            skLineSegment(sketch, "E3557", {"start": v(10.33, -58.46) * mm, "end": v(10.55, -58.42) * mm});
            skLineSegment(sketch, "E3558", {"start": v(10.55, -58.42) * mm, "end": v(10.76, -58.37) * mm});
            skLineSegment(sketch, "E3559", {"start": v(10.76, -58.37) * mm, "end": v(10.97, -58.33) * mm});
            skLineSegment(sketch, "E3560", {"start": v(10.97, -58.33) * mm, "end": v(11.19, -58.28) * mm});
            skLineSegment(sketch, "E3561", {"start": v(11.19, -58.28) * mm, "end": v(11.4, -58.24) * mm});
            skLineSegment(sketch, "E3562", {"start": v(11.4, -58.24) * mm, "end": v(11.61, -58.2) * mm});
            skLineSegment(sketch, "E3563", {"start": v(11.61, -58.2) * mm, "end": v(11.83, -58.15) * mm});
            skLineSegment(sketch, "E3564", {"start": v(11.83, -58.15) * mm, "end": v(12.04, -58.1) * mm});
            skLineSegment(sketch, "E3565", {"start": v(12.04, -58.1) * mm, "end": v(12.25, -58.06) * mm});
            skLineSegment(sketch, "E3566", {"start": v(12.25, -58.06) * mm, "end": v(12.47, -58.01) * mm});
            skLineSegment(sketch, "E3567", {"start": v(12.47, -58.01) * mm, "end": v(12.57, -57.99) * mm});
            skLineSegment(sketch, "E3568", {"start": v(12.57, -57.99) * mm, "end": v(12.62, -58.2) * mm});
            skLineSegment(sketch, "E3569", {"start": v(12.62, -58.2) * mm, "end": v(12.67, -58.41) * mm});
            skLineSegment(sketch, "E3570", {"start": v(12.67, -58.41) * mm, "end": v(12.72, -58.63) * mm});
            skLineSegment(sketch, "E3571", {"start": v(12.72, -58.63) * mm, "end": v(12.77, -58.84) * mm});
            skLineSegment(sketch, "E3572", {"start": v(12.77, -58.84) * mm, "end": v(12.82, -59.06) * mm});
            skLineSegment(sketch, "E3573", {"start": v(12.82, -59.06) * mm, "end": v(12.87, -59.27) * mm});
            skLineSegment(sketch, "E3574", {"start": v(12.87, -59.27) * mm, "end": v(12.92, -59.49) * mm});
            skLineSegment(sketch, "E3575", {"start": v(12.92, -59.49) * mm, "end": v(12.97, -59.7) * mm});
            skLineSegment(sketch, "E3576", {"start": v(12.97, -59.7) * mm, "end": v(13.02, -59.92) * mm});
            skLineSegment(sketch, "E3577", {"start": v(13.02, -59.92) * mm, "end": v(13.07, -60.13) * mm});
            skLineSegment(sketch, "E3578", {"start": v(13.07, -60.13) * mm, "end": v(13.12, -60.34) * mm});
            skLineSegment(sketch, "E3579", {"start": v(13.12, -60.34) * mm, "end": v(13.17, -60.56) * mm});
            skLineSegment(sketch, "E3580", {"start": v(13.17, -60.56) * mm, "end": v(13.23, -60.79) * mm});
            skLineSegment(sketch, "E3581", {"start": v(13.23, -60.79) * mm, "end": v(13.32, -61) * mm});
            skLineSegment(sketch, "E3582", {"start": v(13.32, -61) * mm, "end": v(13.46, -61.17) * mm});
            skLineSegment(sketch, "E3583", {"start": v(13.46, -61.17) * mm, "end": v(13.65, -61.3) * mm});
            skLineSegment(sketch, "E3584", {"start": v(13.65, -61.3) * mm, "end": v(13.86, -61.38) * mm});
            skLineSegment(sketch, "E3585", {"start": v(13.86, -61.38) * mm, "end": v(14.09, -61.4) * mm});
            skLineSegment(sketch, "E3586", {"start": v(14.09, -61.4) * mm, "end": v(14.31, -61.37) * mm});
            skLineSegment(sketch, "E3587", {"start": v(14.31, -61.37) * mm, "end": v(14.52, -61.27) * mm});
            skLineSegment(sketch, "E3588", {"start": v(14.52, -61.27) * mm, "end": v(14.7, -61.13) * mm});
            skLineSegment(sketch, "E3589", {"start": v(14.7, -61.13) * mm, "end": v(14.83, -60.94) * mm});
            skLineSegment(sketch, "E3590", {"start": v(14.83, -60.94) * mm, "end": v(14.9, -60.73) * mm});
            skLineSegment(sketch, "E3591", {"start": v(14.9, -60.73) * mm, "end": v(14.92, -60.5) * mm});
            skLineSegment(sketch, "E3592", {"start": v(14.92, -60.5) * mm, "end": v(14.88, -60.29) * mm});
            skLineSegment(sketch, "E3593", {"start": v(14.88, -60.29) * mm, "end": v(14.83, -60.08) * mm});
            skLineSegment(sketch, "E3594", {"start": v(14.83, -60.08) * mm, "end": v(14.78, -59.87) * mm});
            skLineSegment(sketch, "E3595", {"start": v(14.78, -59.87) * mm, "end": v(14.72, -59.66) * mm});
            skLineSegment(sketch, "E3596", {"start": v(14.72, -59.66) * mm, "end": v(14.67, -59.45) * mm});
            skLineSegment(sketch, "E3597", {"start": v(14.67, -59.45) * mm, "end": v(14.6, -59.23) * mm});
            skLineSegment(sketch, "E3598", {"start": v(14.6, -59.23) * mm, "end": v(14.55, -59.02) * mm});
            skLineSegment(sketch, "E3599", {"start": v(14.55, -59.02) * mm, "end": v(14.5, -58.8) * mm});
            skLineSegment(sketch, "E3600", {"start": v(14.5, -58.8) * mm, "end": v(14.44, -58.6) * mm});
            skLineSegment(sketch, "E3601", {"start": v(14.44, -58.6) * mm, "end": v(14.39, -58.38) * mm});
            skLineSegment(sketch, "E3602", {"start": v(14.39, -58.38) * mm, "end": v(14.33, -58.17) * mm});
            skLineSegment(sketch, "E3603", {"start": v(14.33, -58.17) * mm, "end": v(14.27, -57.95) * mm});
            skLineSegment(sketch, "E3604", {"start": v(14.27, -57.95) * mm, "end": v(14.22, -57.74) * mm});
            skLineSegment(sketch, "E3605", {"start": v(14.22, -57.74) * mm, "end": v(14.18, -57.59) * mm});
            skLineSegment(sketch, "E3606", {"start": v(14.18, -57.59) * mm, "end": v(14.39, -57.53) * mm});
            skLineSegment(sketch, "E3607", {"start": v(14.39, -57.53) * mm, "end": v(14.6, -57.47) * mm});
            skLineSegment(sketch, "E3608", {"start": v(14.6, -57.47) * mm, "end": v(14.8, -57.4) * mm});
            skLineSegment(sketch, "E3609", {"start": v(14.8, -57.4) * mm, "end": v(15.01, -57.35) * mm});
            skLineSegment(sketch, "E3610", {"start": v(15.01, -57.35) * mm, "end": v(15.22, -57.29) * mm});
            skLineSegment(sketch, "E3611", {"start": v(15.22, -57.29) * mm, "end": v(15.43, -57.23) * mm});
            skLineSegment(sketch, "E3612", {"start": v(15.43, -57.23) * mm, "end": v(15.64, -57.17) * mm});
            skLineSegment(sketch, "E3613", {"start": v(15.64, -57.17) * mm, "end": v(15.85, -57.1) * mm});
            skLineSegment(sketch, "E3614", {"start": v(15.85, -57.1) * mm, "end": v(16.06, -57.05) * mm});
            skLineSegment(sketch, "E3615", {"start": v(16.06, -57.05) * mm, "end": v(16.27, -56.99) * mm});
            skLineSegment(sketch, "E3616", {"start": v(16.27, -56.99) * mm, "end": v(16.48, -56.93) * mm});
            skLineSegment(sketch, "E3617", {"start": v(16.48, -56.93) * mm, "end": v(16.58, -56.9) * mm});
            skLineSegment(sketch, "E3618", {"start": v(16.58, -56.9) * mm, "end": v(16.65, -57.1) * mm});
            skLineSegment(sketch, "E3619", {"start": v(16.65, -57.1) * mm, "end": v(16.71, -57.32) * mm});
            skLineSegment(sketch, "E3620", {"start": v(16.71, -57.32) * mm, "end": v(16.78, -57.53) * mm});
            skLineSegment(sketch, "E3621", {"start": v(16.78, -57.53) * mm, "end": v(16.84, -57.74) * mm});
            skLineSegment(sketch, "E3622", {"start": v(16.84, -57.74) * mm, "end": v(16.9, -57.95) * mm});
            skLineSegment(sketch, "E3623", {"start": v(16.9, -57.95) * mm, "end": v(16.97, -58.16) * mm});
            skLineSegment(sketch, "E3624", {"start": v(16.97, -58.16) * mm, "end": v(17.04, -58.37) * mm});
            skLineSegment(sketch, "E3625", {"start": v(17.04, -58.37) * mm, "end": v(17.1, -58.58) * mm});
            skLineSegment(sketch, "E3626", {"start": v(17.1, -58.58) * mm, "end": v(17.17, -58.79) * mm});
            skLineSegment(sketch, "E3627", {"start": v(17.17, -58.79) * mm, "end": v(17.23, -59) * mm});
            skLineSegment(sketch, "E3628", {"start": v(17.23, -59) * mm, "end": v(17.3, -59.2) * mm});
            skLineSegment(sketch, "E3629", {"start": v(17.3, -59.2) * mm, "end": v(17.36, -59.42) * mm});
            skLineSegment(sketch, "E3630", {"start": v(17.36, -59.42) * mm, "end": v(17.43, -59.64) * mm});
            skLineSegment(sketch, "E3631", {"start": v(17.43, -59.64) * mm, "end": v(17.54, -59.84) * mm});
            skLineSegment(sketch, "E3632", {"start": v(17.54, -59.84) * mm, "end": v(17.7, -60) * mm});
            skLineSegment(sketch, "E3633", {"start": v(17.7, -60) * mm, "end": v(17.89, -60.13) * mm});
            skLineSegment(sketch, "E3634", {"start": v(17.89, -60.13) * mm, "end": v(18.1, -60.2) * mm});
            skLineSegment(sketch, "E3635", {"start": v(18.1, -60.2) * mm, "end": v(18.33, -60.2) * mm});
            skLineSegment(sketch, "E3636", {"start": v(18.33, -60.2) * mm, "end": v(18.56, -60.15) * mm});
            skLineSegment(sketch, "E3637", {"start": v(18.56, -60.15) * mm, "end": v(18.75, -60.04) * mm});
            skLineSegment(sketch, "E3638", {"start": v(18.75, -60.04) * mm, "end": v(18.92, -59.88) * mm});
            skLineSegment(sketch, "E3639", {"start": v(18.92, -59.88) * mm, "end": v(19.04, -59.69) * mm});
            skLineSegment(sketch, "E3640", {"start": v(19.04, -59.69) * mm, "end": v(19.1, -59.47) * mm});
            skLineSegment(sketch, "E3641", {"start": v(19.1, -59.47) * mm, "end": v(19.1, -59.24) * mm});
            skLineSegment(sketch, "E3642", {"start": v(19.1, -59.24) * mm, "end": v(19.05, -59.03) * mm});
            skLineSegment(sketch, "E3643", {"start": v(19.05, -59.03) * mm, "end": v(18.98, -58.82) * mm});
            skLineSegment(sketch, "E3644", {"start": v(18.98, -58.82) * mm, "end": v(18.92, -58.62) * mm});
            skLineSegment(sketch, "E3645", {"start": v(18.92, -58.62) * mm, "end": v(18.85, -58.41) * mm});
            skLineSegment(sketch, "E3646", {"start": v(18.85, -58.41) * mm, "end": v(18.77, -58.2) * mm});
            skLineSegment(sketch, "E3647", {"start": v(18.77, -58.2) * mm, "end": v(18.7, -58) * mm});
            skLineSegment(sketch, "E3648", {"start": v(18.7, -58) * mm, "end": v(18.63, -57.79) * mm});
            skLineSegment(sketch, "E3649", {"start": v(18.63, -57.79) * mm, "end": v(18.56, -57.58) * mm});
            skLineSegment(sketch, "E3650", {"start": v(18.56, -57.58) * mm, "end": v(18.5, -57.37) * mm});
            skLineSegment(sketch, "E3651", {"start": v(18.5, -57.37) * mm, "end": v(18.42, -57.16) * mm});
            skLineSegment(sketch, "E3652", {"start": v(18.42, -57.16) * mm, "end": v(18.35, -56.96) * mm});
            skLineSegment(sketch, "E3653", {"start": v(18.35, -56.96) * mm, "end": v(18.28, -56.74) * mm});
            skLineSegment(sketch, "E3654", {"start": v(18.28, -56.74) * mm, "end": v(18.2, -56.54) * mm});
            skLineSegment(sketch, "E3655", {"start": v(18.2, -56.54) * mm, "end": v(18.16, -56.39) * mm});
            skLineSegment(sketch, "E3656", {"start": v(18.16, -56.39) * mm, "end": v(18.36, -56.31) * mm});
            skLineSegment(sketch, "E3657", {"start": v(18.36, -56.31) * mm, "end": v(18.57, -56.24) * mm});
            skLineSegment(sketch, "E3658", {"start": v(18.57, -56.24) * mm, "end": v(18.77, -56.16) * mm});
            skLineSegment(sketch, "E3659", {"start": v(18.77, -56.16) * mm, "end": v(18.98, -56.09) * mm});
            skLineSegment(sketch, "E3660", {"start": v(18.98, -56.09) * mm, "end": v(19.18, -56.02) * mm});
            skLineSegment(sketch, "E3661", {"start": v(19.18, -56.02) * mm, "end": v(19.38, -55.94) * mm});
            skLineSegment(sketch, "E3662", {"start": v(19.38, -55.94) * mm, "end": v(19.59, -55.87) * mm});
            skLineSegment(sketch, "E3663", {"start": v(19.59, -55.87) * mm, "end": v(19.8, -55.8) * mm});
            skLineSegment(sketch, "E3664", {"start": v(19.8, -55.8) * mm, "end": v(20, -55.72) * mm});
            skLineSegment(sketch, "E3665", {"start": v(20, -55.72) * mm, "end": v(20.2, -55.64) * mm});
            skLineSegment(sketch, "E3666", {"start": v(20.2, -55.64) * mm, "end": v(20.4, -55.57) * mm});
            skLineSegment(sketch, "E3667", {"start": v(20.4, -55.57) * mm, "end": v(20.5, -55.53) * mm});
            skLineSegment(sketch, "E3668", {"start": v(20.5, -55.53) * mm, "end": v(20.59, -55.73) * mm});
            skLineSegment(sketch, "E3669", {"start": v(20.59, -55.73) * mm, "end": v(20.67, -55.94) * mm});
            skLineSegment(sketch, "E3670", {"start": v(20.67, -55.94) * mm, "end": v(20.75, -56.15) * mm});
            skLineSegment(sketch, "E3671", {"start": v(20.75, -56.15) * mm, "end": v(20.83, -56.35) * mm});
            skLineSegment(sketch, "E3672", {"start": v(20.83, -56.35) * mm, "end": v(20.9, -56.55) * mm});
            skLineSegment(sketch, "E3673", {"start": v(20.9, -56.55) * mm, "end": v(20.99, -56.76) * mm});
            skLineSegment(sketch, "E3674", {"start": v(20.99, -56.76) * mm, "end": v(21.06, -56.96) * mm});
            skLineSegment(sketch, "E3675", {"start": v(21.06, -56.96) * mm, "end": v(21.14, -57.17) * mm});
            skLineSegment(sketch, "E3676", {"start": v(21.14, -57.17) * mm, "end": v(21.22, -57.38) * mm});
            skLineSegment(sketch, "E3677", {"start": v(21.22, -57.38) * mm, "end": v(21.3, -57.58) * mm});
            skLineSegment(sketch, "E3678", {"start": v(21.3, -57.58) * mm, "end": v(21.38, -57.78) * mm});
            skLineSegment(sketch, "E3679", {"start": v(21.38, -57.78) * mm, "end": v(21.46, -58) * mm});
            skLineSegment(sketch, "E3680", {"start": v(21.46, -58) * mm, "end": v(21.55, -58.2) * mm});
            skLineSegment(sketch, "E3681", {"start": v(21.55, -58.2) * mm, "end": v(21.67, -58.4) * mm});
            skLineSegment(sketch, "E3682", {"start": v(21.67, -58.4) * mm, "end": v(21.84, -58.56) * mm});
            skLineSegment(sketch, "E3683", {"start": v(21.84, -58.56) * mm, "end": v(22.04, -58.66) * mm});
            skLineSegment(sketch, "E3684", {"start": v(22.04, -58.66) * mm, "end": v(22.26, -58.71) * mm});
            skLineSegment(sketch, "E3685", {"start": v(22.26, -58.71) * mm, "end": v(22.49, -58.7) * mm});
            skLineSegment(sketch, "E3686", {"start": v(22.49, -58.7) * mm, "end": v(22.7, -58.63) * mm});
            skLineSegment(sketch, "E3687", {"start": v(22.7, -58.63) * mm, "end": v(22.9, -58.51) * mm});
            skLineSegment(sketch, "E3688", {"start": v(22.9, -58.51) * mm, "end": v(23.05, -58.34) * mm});
            skLineSegment(sketch, "E3689", {"start": v(23.05, -58.34) * mm, "end": v(23.15, -58.14) * mm});
            skLineSegment(sketch, "E3690", {"start": v(23.15, -58.14) * mm, "end": v(23.2, -57.92) * mm});
            skLineSegment(sketch, "E3691", {"start": v(23.2, -57.92) * mm, "end": v(23.19, -57.7) * mm});
            skLineSegment(sketch, "E3692", {"start": v(23.19, -57.7) * mm, "end": v(23.12, -57.49) * mm});
            skLineSegment(sketch, "E3693", {"start": v(23.12, -57.49) * mm, "end": v(23.04, -57.28) * mm});
            skLineSegment(sketch, "E3694", {"start": v(23.04, -57.28) * mm, "end": v(22.96, -57.08) * mm});
            skLineSegment(sketch, "E3695", {"start": v(22.96, -57.08) * mm, "end": v(22.87, -56.88) * mm});
            skLineSegment(sketch, "E3696", {"start": v(22.87, -56.88) * mm, "end": v(22.79, -56.68) * mm});
            skLineSegment(sketch, "E3697", {"start": v(22.79, -56.68) * mm, "end": v(22.7, -56.48) * mm});
            skLineSegment(sketch, "E3698", {"start": v(22.7, -56.48) * mm, "end": v(22.62, -56.27) * mm});
            skLineSegment(sketch, "E3699", {"start": v(22.62, -56.27) * mm, "end": v(22.53, -56.07) * mm});
            skLineSegment(sketch, "E3700", {"start": v(22.53, -56.07) * mm, "end": v(22.44, -55.87) * mm});
            skLineSegment(sketch, "E3701", {"start": v(22.44, -55.87) * mm, "end": v(22.36, -55.67) * mm});
            skLineSegment(sketch, "E3702", {"start": v(22.36, -55.67) * mm, "end": v(22.28, -55.47) * mm});
            skLineSegment(sketch, "E3703", {"start": v(22.28, -55.47) * mm, "end": v(22.19, -55.26) * mm});
            skLineSegment(sketch, "E3704", {"start": v(22.19, -55.26) * mm, "end": v(22.1, -55.06) * mm});
            skLineSegment(sketch, "E3705", {"start": v(22.1, -55.06) * mm, "end": v(22.04, -54.91) * mm});
            skLineSegment(sketch, "E3706", {"start": v(22.04, -54.91) * mm, "end": v(22.24, -54.82) * mm});
            skLineSegment(sketch, "E3707", {"start": v(22.24, -54.82) * mm, "end": v(22.44, -54.73) * mm});
            skLineSegment(sketch, "E3708", {"start": v(22.44, -54.73) * mm, "end": v(22.64, -54.65) * mm});
            skLineSegment(sketch, "E3709", {"start": v(22.64, -54.65) * mm, "end": v(22.84, -54.56) * mm});
            skLineSegment(sketch, "E3710", {"start": v(22.84, -54.56) * mm, "end": v(23.04, -54.47) * mm});
            skLineSegment(sketch, "E3711", {"start": v(23.04, -54.47) * mm, "end": v(23.24, -54.38) * mm});
            skLineSegment(sketch, "E3712", {"start": v(23.24, -54.38) * mm, "end": v(23.44, -54.3) * mm});
            skLineSegment(sketch, "E3713", {"start": v(23.44, -54.3) * mm, "end": v(23.63, -54.2) * mm});
            skLineSegment(sketch, "E3714", {"start": v(23.63, -54.2) * mm, "end": v(23.83, -54.11) * mm});
            skLineSegment(sketch, "E3715", {"start": v(23.83, -54.11) * mm, "end": v(24.03, -54.03) * mm});
            skLineSegment(sketch, "E3716", {"start": v(24.03, -54.03) * mm, "end": v(24.23, -53.94) * mm});
            skLineSegment(sketch, "E3717", {"start": v(24.23, -53.94) * mm, "end": v(24.33, -53.9) * mm});
            skLineSegment(sketch, "E3718", {"start": v(24.33, -53.9) * mm, "end": v(24.42, -54.1) * mm});
            skLineSegment(sketch, "E3719", {"start": v(24.42, -54.1) * mm, "end": v(24.51, -54.29) * mm});
            skLineSegment(sketch, "E3720", {"start": v(24.51, -54.29) * mm, "end": v(24.61, -54.5) * mm});
            skLineSegment(sketch, "E3721", {"start": v(24.61, -54.5) * mm, "end": v(24.7, -54.69) * mm});
            skLineSegment(sketch, "E3722", {"start": v(24.7, -54.69) * mm, "end": v(24.8, -54.88) * mm});
            skLineSegment(sketch, "E3723", {"start": v(24.8, -54.88) * mm, "end": v(24.9, -55.09) * mm});
            skLineSegment(sketch, "E3724", {"start": v(24.9, -55.09) * mm, "end": v(24.98, -55.28) * mm});
            skLineSegment(sketch, "E3725", {"start": v(24.98, -55.28) * mm, "end": v(25.08, -55.48) * mm});
            skLineSegment(sketch, "E3726", {"start": v(25.08, -55.48) * mm, "end": v(25.17, -55.68) * mm});
            skLineSegment(sketch, "E3727", {"start": v(25.17, -55.68) * mm, "end": v(25.26, -55.88) * mm});
            skLineSegment(sketch, "E3728", {"start": v(25.26, -55.88) * mm, "end": v(25.36, -56.08) * mm});
            skLineSegment(sketch, "E3729", {"start": v(25.36, -56.08) * mm, "end": v(25.45, -56.28) * mm});
            skLineSegment(sketch, "E3730", {"start": v(25.45, -56.28) * mm, "end": v(25.55, -56.5) * mm});
            skLineSegment(sketch, "E3731", {"start": v(25.55, -56.5) * mm, "end": v(25.69, -56.68) * mm});
            skLineSegment(sketch, "E3732", {"start": v(25.69, -56.68) * mm, "end": v(25.87, -56.82) * mm});
            skLineSegment(sketch, "E3733", {"start": v(25.87, -56.82) * mm, "end": v(26.07, -56.9) * mm});
            skLineSegment(sketch, "E3734", {"start": v(26.07, -56.9) * mm, "end": v(26.3, -56.94) * mm});
            skLineSegment(sketch, "E3735", {"start": v(26.3, -56.94) * mm, "end": v(26.52, -56.92) * mm});
            skLineSegment(sketch, "E3736", {"start": v(26.52, -56.92) * mm, "end": v(26.74, -56.84) * mm});
            skLineSegment(sketch, "E3737", {"start": v(26.74, -56.84) * mm, "end": v(26.92, -56.7) * mm});
            skLineSegment(sketch, "E3738", {"start": v(26.92, -56.7) * mm, "end": v(27.06, -56.52) * mm});
            skLineSegment(sketch, "E3739", {"start": v(27.06, -56.52) * mm, "end": v(27.15, -56.31) * mm});
            skLineSegment(sketch, "E3740", {"start": v(27.15, -56.31) * mm, "end": v(27.18, -56.09) * mm});
            skLineSegment(sketch, "E3741", {"start": v(27.18, -56.09) * mm, "end": v(27.16, -55.86) * mm});
            skLineSegment(sketch, "E3742", {"start": v(27.16, -55.86) * mm, "end": v(27.07, -55.66) * mm});
            skLineSegment(sketch, "E3743", {"start": v(27.07, -55.66) * mm, "end": v(26.98, -55.47) * mm});
            skLineSegment(sketch, "E3744", {"start": v(26.98, -55.47) * mm, "end": v(26.88, -55.27) * mm});
            skLineSegment(sketch, "E3745", {"start": v(26.88, -55.27) * mm, "end": v(26.78, -55.08) * mm});
            skLineSegment(sketch, "E3746", {"start": v(26.78, -55.08) * mm, "end": v(26.68, -54.88) * mm});
            skLineSegment(sketch, "E3747", {"start": v(26.68, -54.88) * mm, "end": v(26.58, -54.68) * mm});
            skLineSegment(sketch, "E3748", {"start": v(26.58, -54.68) * mm, "end": v(26.48, -54.49) * mm});
            skLineSegment(sketch, "E3749", {"start": v(26.48, -54.49) * mm, "end": v(26.39, -54.3) * mm});
            skLineSegment(sketch, "E3750", {"start": v(26.39, -54.3) * mm, "end": v(26.28, -54.1) * mm});
            skLineSegment(sketch, "E3751", {"start": v(26.28, -54.1) * mm, "end": v(26.19, -53.9) * mm});
            skLineSegment(sketch, "E3752", {"start": v(26.19, -53.9) * mm, "end": v(26.09, -53.7) * mm});
            skLineSegment(sketch, "E3753", {"start": v(26.09, -53.7) * mm, "end": v(25.99, -53.5) * mm});
            skLineSegment(sketch, "E3754", {"start": v(25.99, -53.5) * mm, "end": v(25.89, -53.3) * mm});
            skLineSegment(sketch, "E3755", {"start": v(25.89, -53.3) * mm, "end": v(25.82, -53.17) * mm});
            skLineSegment(sketch, "E3756", {"start": v(25.82, -53.17) * mm, "end": v(26, -53.07) * mm});
            skLineSegment(sketch, "E3757", {"start": v(26, -53.07) * mm, "end": v(26.2, -52.96) * mm});
            skLineSegment(sketch, "E3758", {"start": v(26.2, -52.96) * mm, "end": v(26.4, -52.86) * mm});
            skLineSegment(sketch, "E3759", {"start": v(26.4, -52.86) * mm, "end": v(26.59, -52.76) * mm});
            skLineSegment(sketch, "E3760", {"start": v(26.59, -52.76) * mm, "end": v(26.78, -52.66) * mm});
            skLineSegment(sketch, "E3761", {"start": v(26.78, -52.66) * mm, "end": v(26.97, -52.55) * mm});
            skLineSegment(sketch, "E3762", {"start": v(26.97, -52.55) * mm, "end": v(27.16, -52.45) * mm});
            skLineSegment(sketch, "E3763", {"start": v(27.16, -52.45) * mm, "end": v(27.36, -52.35) * mm});
            skLineSegment(sketch, "E3764", {"start": v(27.36, -52.35) * mm, "end": v(27.55, -52.25) * mm});
            skLineSegment(sketch, "E3765", {"start": v(27.55, -52.25) * mm, "end": v(27.74, -52.15) * mm});
            skLineSegment(sketch, "E3766", {"start": v(27.74, -52.15) * mm, "end": v(27.93, -52.04) * mm});
            skLineSegment(sketch, "E3767", {"start": v(27.93, -52.04) * mm, "end": v(28.03, -52) * mm});
            skLineSegment(sketch, "E3768", {"start": v(28.03, -52) * mm, "end": v(28.13, -52.18) * mm});
            skLineSegment(sketch, "E3769", {"start": v(28.13, -52.18) * mm, "end": v(28.24, -52.37) * mm});
            skLineSegment(sketch, "E3770", {"start": v(28.24, -52.37) * mm, "end": v(28.35, -52.57) * mm});
            skLineSegment(sketch, "E3771", {"start": v(28.35, -52.57) * mm, "end": v(28.46, -52.76) * mm});
            skLineSegment(sketch, "E3772", {"start": v(28.46, -52.76) * mm, "end": v(28.56, -52.95) * mm});
            skLineSegment(sketch, "E3773", {"start": v(28.56, -52.95) * mm, "end": v(28.67, -53.14) * mm});
            skLineSegment(sketch, "E3774", {"start": v(28.67, -53.14) * mm, "end": v(28.78, -53.33) * mm});
            skLineSegment(sketch, "E3775", {"start": v(28.78, -53.33) * mm, "end": v(28.88, -53.53) * mm});
            skLineSegment(sketch, "E3776", {"start": v(28.88, -53.53) * mm, "end": v(29, -53.72) * mm});
            skLineSegment(sketch, "E3777", {"start": v(29, -53.72) * mm, "end": v(29.1, -53.91) * mm});
            skLineSegment(sketch, "E3778", {"start": v(29.1, -53.91) * mm, "end": v(29.2, -54.1) * mm});
            skLineSegment(sketch, "E3779", {"start": v(29.2, -54.1) * mm, "end": v(29.31, -54.3) * mm});
            skLineSegment(sketch, "E3780", {"start": v(29.31, -54.3) * mm, "end": v(29.43, -54.5) * mm});
            skLineSegment(sketch, "E3781", {"start": v(29.43, -54.5) * mm, "end": v(29.58, -54.67) * mm});
            skLineSegment(sketch, "E3782", {"start": v(29.58, -54.67) * mm, "end": v(29.76, -54.8) * mm});
            skLineSegment(sketch, "E3783", {"start": v(29.76, -54.8) * mm, "end": v(29.98, -54.88) * mm});
            skLineSegment(sketch, "E3784", {"start": v(29.98, -54.88) * mm, "end": v(30.2, -54.9) * mm});
            skLineSegment(sketch, "E3785", {"start": v(30.2, -54.9) * mm, "end": v(30.43, -54.86) * mm});
            skLineSegment(sketch, "E3786", {"start": v(30.43, -54.86) * mm, "end": v(30.63, -54.76) * mm});
            skLineSegment(sketch, "E3787", {"start": v(30.63, -54.76) * mm, "end": v(30.8, -54.61) * mm});
            skLineSegment(sketch, "E3788", {"start": v(30.8, -54.61) * mm, "end": v(30.93, -54.42) * mm});
            skLineSegment(sketch, "E3789", {"start": v(30.93, -54.42) * mm, "end": v(31, -54.2) * mm});
            skLineSegment(sketch, "E3790", {"start": v(31, -54.2) * mm, "end": v(31.03, -53.98) * mm});
            skLineSegment(sketch, "E3791", {"start": v(31.03, -53.98) * mm, "end": v(30.98, -53.76) * mm});
            skLineSegment(sketch, "E3792", {"start": v(30.98, -53.76) * mm, "end": v(30.89, -53.57) * mm});
            skLineSegment(sketch, "E3793", {"start": v(30.89, -53.57) * mm, "end": v(30.78, -53.38) * mm});
            skLineSegment(sketch, "E3794", {"start": v(30.78, -53.38) * mm, "end": v(30.67, -53.19) * mm});
            skLineSegment(sketch, "E3795", {"start": v(30.67, -53.19) * mm, "end": v(30.56, -53) * mm});
            skLineSegment(sketch, "E3796", {"start": v(30.56, -53) * mm, "end": v(30.44, -52.82) * mm});
            skLineSegment(sketch, "E3797", {"start": v(30.44, -52.82) * mm, "end": v(30.33, -52.62) * mm});
            skLineSegment(sketch, "E3798", {"start": v(30.33, -52.62) * mm, "end": v(30.22, -52.44) * mm});
            skLineSegment(sketch, "E3799", {"start": v(30.22, -52.44) * mm, "end": v(30.1, -52.25) * mm});
            skLineSegment(sketch, "E3800", {"start": v(30.1, -52.25) * mm, "end": v(30, -52.06) * mm});
            skLineSegment(sketch, "E3801", {"start": v(30, -52.06) * mm, "end": v(29.88, -51.87) * mm});
            skLineSegment(sketch, "E3802", {"start": v(29.88, -51.87) * mm, "end": v(29.77, -51.68) * mm});
            skLineSegment(sketch, "E3803", {"start": v(29.77, -51.68) * mm, "end": v(29.65, -51.49) * mm});
            skLineSegment(sketch, "E3804", {"start": v(29.65, -51.49) * mm, "end": v(29.54, -51.3) * mm});
            skLineSegment(sketch, "E3805", {"start": v(29.54, -51.3) * mm, "end": v(29.46, -51.17) * mm});
            skLineSegment(sketch, "E3806", {"start": v(29.46, -51.17) * mm, "end": v(29.65, -51.05) * mm});
            skLineSegment(sketch, "E3807", {"start": v(29.65, -51.05) * mm, "end": v(29.83, -50.93) * mm});
            skLineSegment(sketch, "E3808", {"start": v(29.83, -50.93) * mm, "end": v(30.01, -50.82) * mm});
            skLineSegment(sketch, "E3809", {"start": v(30.01, -50.82) * mm, "end": v(30.2, -50.7) * mm});
            skLineSegment(sketch, "E3810", {"start": v(30.2, -50.7) * mm, "end": v(30.38, -50.59) * mm});
            skLineSegment(sketch, "E3811", {"start": v(30.38, -50.59) * mm, "end": v(30.57, -50.47) * mm});
            skLineSegment(sketch, "E3812", {"start": v(30.57, -50.47) * mm, "end": v(30.75, -50.36) * mm});
            skLineSegment(sketch, "E3813", {"start": v(30.75, -50.36) * mm, "end": v(30.94, -50.24) * mm});
            skLineSegment(sketch, "E3814", {"start": v(30.94, -50.24) * mm, "end": v(31.12, -50.13) * mm});
            skLineSegment(sketch, "E3815", {"start": v(31.12, -50.13) * mm, "end": v(31.3, -50.01) * mm});
            skLineSegment(sketch, "E3816", {"start": v(31.3, -50.01) * mm, "end": v(31.5, -49.9) * mm});
            skLineSegment(sketch, "E3817", {"start": v(31.5, -49.9) * mm, "end": v(31.58, -49.84) * mm});
            skLineSegment(sketch, "E3818", {"start": v(31.58, -49.84) * mm, "end": v(31.7, -50.02) * mm});
            skLineSegment(sketch, "E3819", {"start": v(31.7, -50.02) * mm, "end": v(31.82, -50.2) * mm});
            skLineSegment(sketch, "E3820", {"start": v(31.82, -50.2) * mm, "end": v(31.94, -50.4) * mm});
            skLineSegment(sketch, "E3821", {"start": v(31.94, -50.4) * mm, "end": v(32.06, -50.57) * mm});
            skLineSegment(sketch, "E3822", {"start": v(32.06, -50.57) * mm, "end": v(32.18, -50.76) * mm});
            skLineSegment(sketch, "E3823", {"start": v(32.18, -50.76) * mm, "end": v(32.3, -50.94) * mm});
            skLineSegment(sketch, "E3824", {"start": v(32.3, -50.94) * mm, "end": v(32.42, -51.13) * mm});
            skLineSegment(sketch, "E3825", {"start": v(32.42, -51.13) * mm, "end": v(32.54, -51.3) * mm});
            skLineSegment(sketch, "E3826", {"start": v(32.54, -51.3) * mm, "end": v(32.67, -51.5) * mm});
            skLineSegment(sketch, "E3827", {"start": v(32.67, -51.5) * mm, "end": v(32.79, -51.68) * mm});
            skLineSegment(sketch, "E3828", {"start": v(32.79, -51.68) * mm, "end": v(32.9, -51.86) * mm});
            skLineSegment(sketch, "E3829", {"start": v(32.9, -51.86) * mm, "end": v(33.03, -52.05) * mm});
            skLineSegment(sketch, "E3830", {"start": v(33.03, -52.05) * mm, "end": v(33.16, -52.24) * mm});
            skLineSegment(sketch, "E3831", {"start": v(33.16, -52.24) * mm, "end": v(33.32, -52.4) * mm});
            skLineSegment(sketch, "E3832", {"start": v(33.32, -52.4) * mm, "end": v(33.51, -52.52) * mm});
            skLineSegment(sketch, "E3833", {"start": v(33.51, -52.52) * mm, "end": v(33.73, -52.58) * mm});
            skLineSegment(sketch, "E3834", {"start": v(33.73, -52.58) * mm, "end": v(33.96, -52.59) * mm});
            skLineSegment(sketch, "E3835", {"start": v(33.96, -52.59) * mm, "end": v(34.18, -52.53) * mm});
            skLineSegment(sketch, "E3836", {"start": v(34.18, -52.53) * mm, "end": v(34.38, -52.42) * mm});
            skLineSegment(sketch, "E3837", {"start": v(34.38, -52.42) * mm, "end": v(34.54, -52.26) * mm});
            skLineSegment(sketch, "E3838", {"start": v(34.54, -52.26) * mm, "end": v(34.65, -52.06) * mm});
            skLineSegment(sketch, "E3839", {"start": v(34.65, -52.06) * mm, "end": v(34.71, -51.84) * mm});
            skLineSegment(sketch, "E3840", {"start": v(34.71, -51.84) * mm, "end": v(34.71, -51.62) * mm});
            skLineSegment(sketch, "E3841", {"start": v(34.71, -51.62) * mm, "end": v(34.66, -51.4) * mm});
            skLineSegment(sketch, "E3842", {"start": v(34.66, -51.4) * mm, "end": v(34.54, -51.2) * mm});
            skLineSegment(sketch, "E3843", {"start": v(34.54, -51.2) * mm, "end": v(34.42, -51.03) * mm});
            skLineSegment(sketch, "E3844", {"start": v(34.42, -51.03) * mm, "end": v(34.3, -50.85) * mm});
            skLineSegment(sketch, "E3845", {"start": v(34.3, -50.85) * mm, "end": v(34.18, -50.67) * mm});
            skLineSegment(sketch, "E3846", {"start": v(34.18, -50.67) * mm, "end": v(34.05, -50.5) * mm});
            skLineSegment(sketch, "E3847", {"start": v(34.05, -50.5) * mm, "end": v(33.92, -50.3) * mm});
            skLineSegment(sketch, "E3848", {"start": v(33.92, -50.3) * mm, "end": v(33.8, -50.13) * mm});
            skLineSegment(sketch, "E3849", {"start": v(33.8, -50.13) * mm, "end": v(33.67, -49.95) * mm});
            skLineSegment(sketch, "E3850", {"start": v(33.67, -49.95) * mm, "end": v(33.55, -49.76) * mm});
            skLineSegment(sketch, "E3851", {"start": v(33.55, -49.76) * mm, "end": v(33.42, -49.59) * mm});
            skLineSegment(sketch, "E3852", {"start": v(33.42, -49.59) * mm, "end": v(33.3, -49.4) * mm});
            skLineSegment(sketch, "E3853", {"start": v(33.3, -49.4) * mm, "end": v(33.17, -49.22) * mm});
            skLineSegment(sketch, "E3854", {"start": v(33.17, -49.22) * mm, "end": v(33.05, -49.04) * mm});
            skLineSegment(sketch, "E3855", {"start": v(33.05, -49.04) * mm, "end": v(32.96, -48.91) * mm});
            skLineSegment(sketch, "E3856", {"start": v(32.96, -48.91) * mm, "end": v(33.13, -48.79) * mm});
            skLineSegment(sketch, "E3857", {"start": v(33.13, -48.79) * mm, "end": v(33.3, -48.66) * mm});
            skLineSegment(sketch, "E3858", {"start": v(33.3, -48.66) * mm, "end": v(33.48, -48.53) * mm});
            skLineSegment(sketch, "E3859", {"start": v(33.48, -48.53) * mm, "end": v(33.66, -48.4) * mm});
            skLineSegment(sketch, "E3860", {"start": v(33.66, -48.4) * mm, "end": v(33.84, -48.27) * mm});
            skLineSegment(sketch, "E3861", {"start": v(33.84, -48.27) * mm, "end": v(34.01, -48.14) * mm});
            skLineSegment(sketch, "E3862", {"start": v(34.01, -48.14) * mm, "end": v(34.19, -48.02) * mm});
            skLineSegment(sketch, "E3863", {"start": v(34.19, -48.02) * mm, "end": v(34.37, -47.89) * mm});
            skLineSegment(sketch, "E3864", {"start": v(34.37, -47.89) * mm, "end": v(34.54, -47.76) * mm});
            skLineSegment(sketch, "E3865", {"start": v(34.54, -47.76) * mm, "end": v(34.72, -47.63) * mm});
            skLineSegment(sketch, "E3866", {"start": v(34.72, -47.63) * mm, "end": v(34.9, -47.5) * mm});
            skLineSegment(sketch, "E3867", {"start": v(34.9, -47.5) * mm, "end": v(34.98, -47.44) * mm});
            skLineSegment(sketch, "E3868", {"start": v(34.98, -47.44) * mm, "end": v(35.11, -47.62) * mm});
            skLineSegment(sketch, "E3869", {"start": v(35.11, -47.62) * mm, "end": v(35.24, -47.79) * mm});
            skLineSegment(sketch, "E3870", {"start": v(35.24, -47.79) * mm, "end": v(35.38, -47.97) * mm});
            skLineSegment(sketch, "E3871", {"start": v(35.38, -47.97) * mm, "end": v(35.51, -48.14) * mm});
            skLineSegment(sketch, "E3872", {"start": v(35.51, -48.14) * mm, "end": v(35.64, -48.31) * mm});
            skLineSegment(sketch, "E3873", {"start": v(35.64, -48.31) * mm, "end": v(35.78, -48.5) * mm});
            skLineSegment(sketch, "E3874", {"start": v(35.78, -48.5) * mm, "end": v(35.9, -48.67) * mm});
            skLineSegment(sketch, "E3875", {"start": v(35.9, -48.67) * mm, "end": v(36.04, -48.84) * mm});
            skLineSegment(sketch, "E3876", {"start": v(36.04, -48.84) * mm, "end": v(36.18, -49.02) * mm});
            skLineSegment(sketch, "E3877", {"start": v(36.18, -49.02) * mm, "end": v(36.3, -49.2) * mm});
            skLineSegment(sketch, "E3878", {"start": v(36.3, -49.2) * mm, "end": v(36.44, -49.37) * mm});
            skLineSegment(sketch, "E3879", {"start": v(36.44, -49.37) * mm, "end": v(36.58, -49.54) * mm});
            skLineSegment(sketch, "E3880", {"start": v(36.58, -49.54) * mm, "end": v(36.72, -49.73) * mm});
            skLineSegment(sketch, "E3881", {"start": v(36.72, -49.73) * mm, "end": v(36.89, -49.88) * mm});
            skLineSegment(sketch, "E3882", {"start": v(36.89, -49.88) * mm, "end": v(37.1, -49.98) * mm});
            skLineSegment(sketch, "E3883", {"start": v(37.1, -49.98) * mm, "end": v(37.31, -50.03) * mm});
            skLineSegment(sketch, "E3884", {"start": v(37.31, -50.03) * mm, "end": v(37.54, -50.02) * mm});
            skLineSegment(sketch, "E3885", {"start": v(37.54, -50.02) * mm, "end": v(37.76, -49.94) * mm});
            skLineSegment(sketch, "E3886", {"start": v(37.76, -49.94) * mm, "end": v(37.95, -49.82) * mm});
            skLineSegment(sketch, "E3887", {"start": v(37.95, -49.82) * mm, "end": v(38.1, -49.65) * mm});
            skLineSegment(sketch, "E3888", {"start": v(38.1, -49.65) * mm, "end": v(38.2, -49.45) * mm});
            skLineSegment(sketch, "E3889", {"start": v(38.2, -49.45) * mm, "end": v(38.24, -49.22) * mm});
            skLineSegment(sketch, "E3890", {"start": v(38.24, -49.22) * mm, "end": v(38.23, -49) * mm});
            skLineSegment(sketch, "E3891", {"start": v(38.23, -49) * mm, "end": v(38.15, -48.78) * mm});
            skLineSegment(sketch, "E3892", {"start": v(38.15, -48.78) * mm, "end": v(38.03, -48.6) * mm});
            skLineSegment(sketch, "E3893", {"start": v(38.03, -48.6) * mm, "end": v(37.9, -48.43) * mm});
            skLineSegment(sketch, "E3894", {"start": v(37.9, -48.43) * mm, "end": v(37.76, -48.26) * mm});
            skLineSegment(sketch, "E3895", {"start": v(37.76, -48.26) * mm, "end": v(37.62, -48.09) * mm});
            skLineSegment(sketch, "E3896", {"start": v(37.62, -48.09) * mm, "end": v(37.49, -47.92) * mm});
            skLineSegment(sketch, "E3897", {"start": v(37.49, -47.92) * mm, "end": v(37.35, -47.75) * mm});
            skLineSegment(sketch, "E3898", {"start": v(37.35, -47.75) * mm, "end": v(37.21, -47.58) * mm});
            skLineSegment(sketch, "E3899", {"start": v(37.21, -47.58) * mm, "end": v(37.07, -47.4) * mm});
            skLineSegment(sketch, "E3900", {"start": v(37.07, -47.4) * mm, "end": v(36.93, -47.23) * mm});
            skLineSegment(sketch, "E3901", {"start": v(36.93, -47.23) * mm, "end": v(36.8, -47.06) * mm});
            skLineSegment(sketch, "E3902", {"start": v(36.8, -47.06) * mm, "end": v(36.66, -46.9) * mm});
            skLineSegment(sketch, "E3903", {"start": v(36.66, -46.9) * mm, "end": v(36.52, -46.72) * mm});
            skLineSegment(sketch, "E3904", {"start": v(36.52, -46.72) * mm, "end": v(36.38, -46.55) * mm});
            skLineSegment(sketch, "E3905", {"start": v(36.38, -46.55) * mm, "end": v(36.28, -46.42) * mm});
            skLineSegment(sketch, "E3906", {"start": v(36.28, -46.42) * mm, "end": v(36.45, -46.28) * mm});
            skLineSegment(sketch, "E3907", {"start": v(36.45, -46.28) * mm, "end": v(36.62, -46.14) * mm});
            skLineSegment(sketch, "E3908", {"start": v(36.62, -46.14) * mm, "end": v(36.79, -46) * mm});
            skLineSegment(sketch, "E3909", {"start": v(36.79, -46) * mm, "end": v(36.95, -45.86) * mm});
            skLineSegment(sketch, "E3910", {"start": v(36.95, -45.86) * mm, "end": v(37.12, -45.72) * mm});
            skLineSegment(sketch, "E3911", {"start": v(37.12, -45.72) * mm, "end": v(37.29, -45.58) * mm});
            skLineSegment(sketch, "E3912", {"start": v(37.29, -45.58) * mm, "end": v(37.45, -45.44) * mm});
            skLineSegment(sketch, "E3913", {"start": v(37.45, -45.44) * mm, "end": v(37.62, -45.3) * mm});
            skLineSegment(sketch, "E3914", {"start": v(37.62, -45.3) * mm, "end": v(37.79, -45.16) * mm});
            skLineSegment(sketch, "E3915", {"start": v(37.79, -45.16) * mm, "end": v(37.95, -45.02) * mm});
            skLineSegment(sketch, "E3916", {"start": v(37.95, -45.02) * mm, "end": v(38.12, -44.88) * mm});
            skLineSegment(sketch, "E3917", {"start": v(38.12, -44.88) * mm, "end": v(38.2, -44.81) * mm});
            skLineSegment(sketch, "E3918", {"start": v(38.2, -44.81) * mm, "end": v(38.35, -44.98) * mm});
            skLineSegment(sketch, "E3919", {"start": v(38.35, -44.98) * mm, "end": v(38.49, -45.14) * mm});
            skLineSegment(sketch, "E3920", {"start": v(38.49, -45.14) * mm, "end": v(38.64, -45.31) * mm});
            skLineSegment(sketch, "E3921", {"start": v(38.64, -45.31) * mm, "end": v(38.78, -45.47) * mm});
            skLineSegment(sketch, "E3922", {"start": v(38.78, -45.47) * mm, "end": v(38.92, -45.64) * mm});
            skLineSegment(sketch, "E3923", {"start": v(38.92, -45.64) * mm, "end": v(39.07, -45.8) * mm});
            skLineSegment(sketch, "E3924", {"start": v(39.07, -45.8) * mm, "end": v(39.21, -45.97) * mm});
            skLineSegment(sketch, "E3925", {"start": v(39.21, -45.97) * mm, "end": v(39.36, -46.13) * mm});
            skLineSegment(sketch, "E3926", {"start": v(39.36, -46.13) * mm, "end": v(39.5, -46.3) * mm});
            skLineSegment(sketch, "E3927", {"start": v(39.5, -46.3) * mm, "end": v(39.65, -46.47) * mm});
            skLineSegment(sketch, "E3928", {"start": v(39.65, -46.47) * mm, "end": v(39.8, -46.63) * mm});
            skLineSegment(sketch, "E3929", {"start": v(39.8, -46.63) * mm, "end": v(39.94, -46.8) * mm});
            skLineSegment(sketch, "E3930", {"start": v(39.94, -46.8) * mm, "end": v(40.1, -46.98) * mm});
            skLineSegment(sketch, "E3931", {"start": v(40.1, -46.98) * mm, "end": v(40.27, -47.11) * mm});
            skLineSegment(sketch, "E3932", {"start": v(40.27, -47.11) * mm, "end": v(40.48, -47.2) * mm});
            skLineSegment(sketch, "E3933", {"start": v(40.48, -47.2) * mm, "end": v(40.7, -47.23) * mm});
            skLineSegment(sketch, "E3934", {"start": v(40.7, -47.23) * mm, "end": v(40.94, -47.2) * mm});
            skLineSegment(sketch, "E3935", {"start": v(40.94, -47.2) * mm, "end": v(41.15, -47.12) * mm});
            skLineSegment(sketch, "E3936", {"start": v(41.15, -47.12) * mm, "end": v(41.33, -46.98) * mm});
            skLineSegment(sketch, "E3937", {"start": v(41.33, -46.98) * mm, "end": v(41.46, -46.8) * mm});
            skLineSegment(sketch, "E3938", {"start": v(41.46, -46.8) * mm, "end": v(41.55, -46.59) * mm});
            skLineSegment(sketch, "E3939", {"start": v(41.55, -46.59) * mm, "end": v(41.58, -46.36) * mm});
            skLineSegment(sketch, "E3940", {"start": v(41.58, -46.36) * mm, "end": v(41.55, -46.14) * mm});
            skLineSegment(sketch, "E3941", {"start": v(41.55, -46.14) * mm, "end": v(41.46, -45.93) * mm});
            skLineSegment(sketch, "E3942", {"start": v(41.46, -45.93) * mm, "end": v(41.33, -45.76) * mm});
            skLineSegment(sketch, "E3943", {"start": v(41.33, -45.76) * mm, "end": v(41.18, -45.6) * mm});
            skLineSegment(sketch, "E3944", {"start": v(41.18, -45.6) * mm, "end": v(41.03, -45.44) * mm});
            skLineSegment(sketch, "E3945", {"start": v(41.03, -45.44) * mm, "end": v(40.88, -45.28) * mm});
            skLineSegment(sketch, "E3946", {"start": v(40.88, -45.28) * mm, "end": v(40.74, -45.12) * mm});
            skLineSegment(sketch, "E3947", {"start": v(40.74, -45.12) * mm, "end": v(40.58, -44.95) * mm});
            skLineSegment(sketch, "E3948", {"start": v(40.58, -44.95) * mm, "end": v(40.44, -44.8) * mm});
            skLineSegment(sketch, "E3949", {"start": v(40.44, -44.8) * mm, "end": v(40.29, -44.63) * mm});
            skLineSegment(sketch, "E3950", {"start": v(40.29, -44.63) * mm, "end": v(40.14, -44.47) * mm});
            skLineSegment(sketch, "E3951", {"start": v(40.14, -44.47) * mm, "end": v(39.99, -44.3) * mm});
            skLineSegment(sketch, "E3952", {"start": v(39.99, -44.3) * mm, "end": v(39.84, -44.15) * mm});
            skLineSegment(sketch, "E3953", {"start": v(39.84, -44.15) * mm, "end": v(39.69, -43.98) * mm});
            skLineSegment(sketch, "E3954", {"start": v(39.69, -43.98) * mm, "end": v(39.54, -43.82) * mm});
            skLineSegment(sketch, "E3955", {"start": v(39.54, -43.82) * mm, "end": v(39.43, -43.7) * mm});
            skLineSegment(sketch, "E3956", {"start": v(39.43, -43.7) * mm, "end": v(39.59, -43.56) * mm});
            skLineSegment(sketch, "E3957", {"start": v(39.59, -43.56) * mm, "end": v(39.75, -43.4) * mm});
            skLineSegment(sketch, "E3958", {"start": v(39.75, -43.4) * mm, "end": v(39.9, -43.25) * mm});
            skLineSegment(sketch, "E3959", {"start": v(39.9, -43.25) * mm, "end": v(40.06, -43.1) * mm});
            skLineSegment(sketch, "E3960", {"start": v(40.06, -43.1) * mm, "end": v(40.22, -42.95) * mm});
            skLineSegment(sketch, "E3961", {"start": v(40.22, -42.95) * mm, "end": v(40.37, -42.8) * mm});
            skLineSegment(sketch, "E3962", {"start": v(40.37, -42.8) * mm, "end": v(40.53, -42.65) * mm});
            skLineSegment(sketch, "E3963", {"start": v(40.53, -42.65) * mm, "end": v(40.69, -42.5) * mm});
            skLineSegment(sketch, "E3964", {"start": v(40.69, -42.5) * mm, "end": v(40.84, -42.34) * mm});
            skLineSegment(sketch, "E3965", {"start": v(40.84, -42.34) * mm, "end": v(41, -42.2) * mm});
            skLineSegment(sketch, "E3966", {"start": v(41, -42.2) * mm, "end": v(41.16, -42.04) * mm});
            skLineSegment(sketch, "E3967", {"start": v(41.16, -42.04) * mm, "end": v(41.23, -41.97) * mm});
            skLineSegment(sketch, "E3968", {"start": v(41.23, -41.97) * mm, "end": v(41.39, -42.12) * mm});
            skLineSegment(sketch, "E3969", {"start": v(41.39, -42.12) * mm, "end": v(41.54, -42.28) * mm});
            skLineSegment(sketch, "E3970", {"start": v(41.54, -42.28) * mm, "end": v(41.7, -42.43) * mm});
            skLineSegment(sketch, "E3971", {"start": v(41.7, -42.43) * mm, "end": v(41.85, -42.59) * mm});
            skLineSegment(sketch, "E3972", {"start": v(41.85, -42.59) * mm, "end": v(42, -42.74) * mm});
            skLineSegment(sketch, "E3973", {"start": v(42, -42.74) * mm, "end": v(42.17, -42.9) * mm});
            skLineSegment(sketch, "E3974", {"start": v(42.17, -42.9) * mm, "end": v(42.32, -43.05) * mm});
            skLineSegment(sketch, "E3975", {"start": v(42.32, -43.05) * mm, "end": v(42.48, -43.2) * mm});
            skLineSegment(sketch, "E3976", {"start": v(42.48, -43.2) * mm, "end": v(42.64, -43.36) * mm});
            skLineSegment(sketch, "E3977", {"start": v(42.64, -43.36) * mm, "end": v(42.8, -43.52) * mm});
            skLineSegment(sketch, "E3978", {"start": v(42.8, -43.52) * mm, "end": v(42.95, -43.67) * mm});
            skLineSegment(sketch, "E3979", {"start": v(42.95, -43.67) * mm, "end": v(43.1, -43.83) * mm});
            skLineSegment(sketch, "E3980", {"start": v(43.1, -43.83) * mm, "end": v(43.27, -44) * mm});
            skLineSegment(sketch, "E3981", {"start": v(43.27, -44) * mm, "end": v(43.46, -44.12) * mm});
            skLineSegment(sketch, "E3982", {"start": v(43.46, -44.12) * mm, "end": v(43.68, -44.2) * mm});
            skLineSegment(sketch, "E3983", {"start": v(43.68, -44.2) * mm, "end": v(43.9, -44.2) * mm});
            skLineSegment(sketch, "E3984", {"start": v(43.9, -44.2) * mm, "end": v(44.13, -44.16) * mm});
            skLineSegment(sketch, "E3985", {"start": v(44.13, -44.16) * mm, "end": v(44.33, -44.06) * mm});
            skLineSegment(sketch, "E3986", {"start": v(44.33, -44.06) * mm, "end": v(44.5, -43.9) * mm});
            skLineSegment(sketch, "E3987", {"start": v(44.5, -43.9) * mm, "end": v(44.62, -43.72) * mm});
            skLineSegment(sketch, "E3988", {"start": v(44.62, -43.72) * mm, "end": v(44.7, -43.5) * mm});
            skLineSegment(sketch, "E3989", {"start": v(44.7, -43.5) * mm, "end": v(44.7, -43.28) * mm});
            skLineSegment(sketch, "E3990", {"start": v(44.7, -43.28) * mm, "end": v(44.66, -43.05) * mm});
            skLineSegment(sketch, "E3991", {"start": v(44.66, -43.05) * mm, "end": v(44.56, -42.85) * mm});
            skLineSegment(sketch, "E3992", {"start": v(44.56, -42.85) * mm, "end": v(44.41, -42.7) * mm});
            skLineSegment(sketch, "E3993", {"start": v(44.41, -42.7) * mm, "end": v(44.26, -42.54) * mm});
            skLineSegment(sketch, "E3994", {"start": v(44.26, -42.54) * mm, "end": v(44.1, -42.4) * mm});
            skLineSegment(sketch, "E3995", {"start": v(44.1, -42.4) * mm, "end": v(43.94, -42.24) * mm});
            skLineSegment(sketch, "E3996", {"start": v(43.94, -42.24) * mm, "end": v(43.78, -42.1) * mm});
            skLineSegment(sketch, "E3997", {"start": v(43.78, -42.1) * mm, "end": v(43.62, -41.94) * mm});
            skLineSegment(sketch, "E3998", {"start": v(43.62, -41.94) * mm, "end": v(43.46, -41.79) * mm});
            skLineSegment(sketch, "E3999", {"start": v(43.46, -41.79) * mm, "end": v(43.3, -41.64) * mm});
            skLineSegment(sketch, "E4000", {"start": v(43.3, -41.64) * mm, "end": v(43.14, -41.49) * mm});
            skLineSegment(sketch, "E4001", {"start": v(43.14, -41.49) * mm, "end": v(42.98, -41.34) * mm});
            skLineSegment(sketch, "E4002", {"start": v(42.98, -41.34) * mm, "end": v(42.82, -41.19) * mm});
            skLineSegment(sketch, "E4003", {"start": v(42.82, -41.19) * mm, "end": v(42.66, -41.04) * mm});
            skLineSegment(sketch, "E4004", {"start": v(42.66, -41.04) * mm, "end": v(42.5, -40.89) * mm});
            skLineSegment(sketch, "E4005", {"start": v(42.5, -40.89) * mm, "end": v(42.38, -40.78) * mm});
            skLineSegment(sketch, "E4006", {"start": v(42.38, -40.78) * mm, "end": v(42.53, -40.62) * mm});
            skLineSegment(sketch, "E4007", {"start": v(42.53, -40.62) * mm, "end": v(42.67, -40.45) * mm});
            skLineSegment(sketch, "E4008", {"start": v(42.67, -40.45) * mm, "end": v(42.82, -40.3) * mm});
            skLineSegment(sketch, "E4009", {"start": v(42.82, -40.3) * mm, "end": v(42.97, -40.13) * mm});
            skLineSegment(sketch, "E4010", {"start": v(42.97, -40.13) * mm, "end": v(43.11, -39.97) * mm});
            skLineSegment(sketch, "E4011", {"start": v(43.11, -39.97) * mm, "end": v(43.26, -39.8) * mm});
            skLineSegment(sketch, "E4012", {"start": v(43.26, -39.8) * mm, "end": v(43.4, -39.64) * mm});
            skLineSegment(sketch, "E4013", {"start": v(43.4, -39.64) * mm, "end": v(43.55, -39.48) * mm});
            skLineSegment(sketch, "E4014", {"start": v(43.55, -39.48) * mm, "end": v(43.7, -39.32) * mm});
            skLineSegment(sketch, "E4015", {"start": v(43.7, -39.32) * mm, "end": v(43.84, -39.16) * mm});
            skLineSegment(sketch, "E4016", {"start": v(43.84, -39.16) * mm, "end": v(43.99, -39) * mm});
            skLineSegment(sketch, "E4017", {"start": v(43.99, -39) * mm, "end": v(44.06, -38.92) * mm});
            skLineSegment(sketch, "E4018", {"start": v(44.06, -38.92) * mm, "end": v(44.22, -39.06) * mm});
            skLineSegment(sketch, "E4019", {"start": v(44.22, -39.06) * mm, "end": v(44.39, -39.2) * mm});
            skLineSegment(sketch, "E4020", {"start": v(44.39, -39.2) * mm, "end": v(44.56, -39.35) * mm});
            skLineSegment(sketch, "E4021", {"start": v(44.56, -39.35) * mm, "end": v(44.72, -39.5) * mm});
            skLineSegment(sketch, "E4022", {"start": v(44.72, -39.5) * mm, "end": v(44.89, -39.63) * mm});
            skLineSegment(sketch, "E4023", {"start": v(44.89, -39.63) * mm, "end": v(45.06, -39.78) * mm});
            skLineSegment(sketch, "E4024", {"start": v(45.06, -39.78) * mm, "end": v(45.22, -39.92) * mm});
            skLineSegment(sketch, "E4025", {"start": v(45.22, -39.92) * mm, "end": v(45.39, -40.06) * mm});
            skLineSegment(sketch, "E4026", {"start": v(45.39, -40.06) * mm, "end": v(45.56, -40.21) * mm});
            skLineSegment(sketch, "E4027", {"start": v(45.56, -40.21) * mm, "end": v(45.72, -40.35) * mm});
            skLineSegment(sketch, "E4028", {"start": v(45.72, -40.35) * mm, "end": v(45.89, -40.5) * mm});
            skLineSegment(sketch, "E4029", {"start": v(45.89, -40.5) * mm, "end": v(46.05, -40.64) * mm});
            skLineSegment(sketch, "E4030", {"start": v(46.05, -40.64) * mm, "end": v(46.23, -40.8) * mm});
            skLineSegment(sketch, "E4031", {"start": v(46.23, -40.8) * mm, "end": v(46.43, -40.9) * mm});
            skLineSegment(sketch, "E4032", {"start": v(46.43, -40.9) * mm, "end": v(46.65, -40.96) * mm});
            skLineSegment(sketch, "E4033", {"start": v(46.65, -40.96) * mm, "end": v(46.88, -40.96) * mm});
            skLineSegment(sketch, "E4034", {"start": v(46.88, -40.96) * mm, "end": v(47.1, -40.9) * mm});
            skLineSegment(sketch, "E4035", {"start": v(47.1, -40.9) * mm, "end": v(47.3, -40.79) * mm});
            skLineSegment(sketch, "E4036", {"start": v(47.3, -40.79) * mm, "end": v(47.45, -40.63) * mm});
            skLineSegment(sketch, "E4037", {"start": v(47.45, -40.63) * mm, "end": v(47.56, -40.43) * mm});
            skLineSegment(sketch, "E4038", {"start": v(47.56, -40.43) * mm, "end": v(47.62, -40.2) * mm});
            skLineSegment(sketch, "E4039", {"start": v(47.62, -40.2) * mm, "end": v(47.62, -39.98) * mm});
            skLineSegment(sketch, "E4040", {"start": v(47.62, -39.98) * mm, "end": v(47.56, -39.76) * mm});
            skLineSegment(sketch, "E4041", {"start": v(47.56, -39.76) * mm, "end": v(47.44, -39.57) * mm});
            skLineSegment(sketch, "E4042", {"start": v(47.44, -39.57) * mm, "end": v(47.28, -39.42) * mm});
            skLineSegment(sketch, "E4043", {"start": v(47.28, -39.42) * mm, "end": v(47.11, -39.28) * mm});
            skLineSegment(sketch, "E4044", {"start": v(47.11, -39.28) * mm, "end": v(46.95, -39.14) * mm});
            skLineSegment(sketch, "E4045", {"start": v(46.95, -39.14) * mm, "end": v(46.78, -39) * mm});
            skLineSegment(sketch, "E4046", {"start": v(46.78, -39) * mm, "end": v(46.6, -38.86) * mm});
            skLineSegment(sketch, "E4047", {"start": v(46.6, -38.86) * mm, "end": v(46.44, -38.72) * mm});
            skLineSegment(sketch, "E4048", {"start": v(46.44, -38.72) * mm, "end": v(46.27, -38.58) * mm});
            skLineSegment(sketch, "E4049", {"start": v(46.27, -38.58) * mm, "end": v(46.1, -38.45) * mm});
            skLineSegment(sketch, "E4050", {"start": v(46.1, -38.45) * mm, "end": v(45.92, -38.3) * mm});
            skLineSegment(sketch, "E4051", {"start": v(45.92, -38.3) * mm, "end": v(45.76, -38.17) * mm});
            skLineSegment(sketch, "E4052", {"start": v(45.76, -38.17) * mm, "end": v(45.59, -38.03) * mm});
            skLineSegment(sketch, "E4053", {"start": v(45.59, -38.03) * mm, "end": v(45.41, -37.89) * mm});
            skLineSegment(sketch, "E4054", {"start": v(45.41, -37.89) * mm, "end": v(45.24, -37.75) * mm});
            skLineSegment(sketch, "E4055", {"start": v(45.24, -37.75) * mm, "end": v(45.12, -37.65) * mm});
            skLineSegment(sketch, "E4056", {"start": v(45.12, -37.65) * mm, "end": v(45.25, -37.48) * mm});
            skLineSegment(sketch, "E4057", {"start": v(45.25, -37.48) * mm, "end": v(45.39, -37.3) * mm});
            skLineSegment(sketch, "E4058", {"start": v(45.39, -37.3) * mm, "end": v(45.52, -37.13) * mm});
            skLineSegment(sketch, "E4059", {"start": v(45.52, -37.13) * mm, "end": v(45.66, -36.96) * mm});
            skLineSegment(sketch, "E4060", {"start": v(45.66, -36.96) * mm, "end": v(45.8, -36.8) * mm});
            skLineSegment(sketch, "E4061", {"start": v(45.8, -36.8) * mm, "end": v(45.93, -36.62) * mm});
            skLineSegment(sketch, "E4062", {"start": v(45.93, -36.62) * mm, "end": v(46.06, -36.45) * mm});
            skLineSegment(sketch, "E4063", {"start": v(46.06, -36.45) * mm, "end": v(46.2, -36.28) * mm});
            skLineSegment(sketch, "E4064", {"start": v(46.2, -36.28) * mm, "end": v(46.33, -36.1) * mm});
            skLineSegment(sketch, "E4065", {"start": v(46.33, -36.1) * mm, "end": v(46.46, -35.93) * mm});
            skLineSegment(sketch, "E4066", {"start": v(46.46, -35.93) * mm, "end": v(46.6, -35.76) * mm});
            skLineSegment(sketch, "E4067", {"start": v(46.6, -35.76) * mm, "end": v(46.66, -35.68) * mm});
            skLineSegment(sketch, "E4068", {"start": v(46.66, -35.68) * mm, "end": v(46.84, -35.8) * mm});
            skLineSegment(sketch, "E4069", {"start": v(46.84, -35.8) * mm, "end": v(47.01, -35.94) * mm});
            skLineSegment(sketch, "E4070", {"start": v(47.01, -35.94) * mm, "end": v(47.19, -36.07) * mm});
            skLineSegment(sketch, "E4071", {"start": v(47.19, -36.07) * mm, "end": v(47.36, -36.2) * mm});
            skLineSegment(sketch, "E4072", {"start": v(47.36, -36.2) * mm, "end": v(47.54, -36.33) * mm});
            skLineSegment(sketch, "E4073", {"start": v(47.54, -36.33) * mm, "end": v(47.72, -36.47) * mm});
            skLineSegment(sketch, "E4074", {"start": v(47.72, -36.47) * mm, "end": v(47.9, -36.6) * mm});
            skLineSegment(sketch, "E4075", {"start": v(47.9, -36.6) * mm, "end": v(48.07, -36.73) * mm});
            skLineSegment(sketch, "E4076", {"start": v(48.07, -36.73) * mm, "end": v(48.25, -36.86) * mm});
            skLineSegment(sketch, "E4077", {"start": v(48.25, -36.86) * mm, "end": v(48.42, -37) * mm});
            skLineSegment(sketch, "E4078", {"start": v(48.42, -37) * mm, "end": v(48.6, -37.12) * mm});
            skLineSegment(sketch, "E4079", {"start": v(48.6, -37.12) * mm, "end": v(48.77, -37.26) * mm});
            skLineSegment(sketch, "E4080", {"start": v(48.77, -37.26) * mm, "end": v(48.96, -37.4) * mm});
            skLineSegment(sketch, "E4081", {"start": v(48.96, -37.4) * mm, "end": v(49.17, -37.5) * mm});
            skLineSegment(sketch, "E4082", {"start": v(49.17, -37.5) * mm, "end": v(49.4, -37.54) * mm});
            skLineSegment(sketch, "E4083", {"start": v(49.4, -37.54) * mm, "end": v(49.62, -37.52) * mm});
            skLineSegment(sketch, "E4084", {"start": v(49.62, -37.52) * mm, "end": v(49.83, -37.45) * mm});
            skLineSegment(sketch, "E4085", {"start": v(49.83, -37.45) * mm, "end": v(50.02, -37.32) * mm});
            skLineSegment(sketch, "E4086", {"start": v(50.02, -37.32) * mm, "end": v(50.17, -37.14) * mm});
            skLineSegment(sketch, "E4087", {"start": v(50.17, -37.14) * mm, "end": v(50.27, -36.94) * mm});
            skLineSegment(sketch, "E4088", {"start": v(50.27, -36.94) * mm, "end": v(50.3, -36.72) * mm});
            skLineSegment(sketch, "E4089", {"start": v(50.3, -36.72) * mm, "end": v(50.29, -36.49) * mm});
            skLineSegment(sketch, "E4090", {"start": v(50.29, -36.49) * mm, "end": v(50.21, -36.28) * mm});
            skLineSegment(sketch, "E4091", {"start": v(50.21, -36.28) * mm, "end": v(50.08, -36.09) * mm});
            skLineSegment(sketch, "E4092", {"start": v(50.08, -36.09) * mm, "end": v(49.91, -35.95) * mm});
            skLineSegment(sketch, "E4093", {"start": v(49.91, -35.95) * mm, "end": v(49.74, -35.82) * mm});
            skLineSegment(sketch, "E4094", {"start": v(49.74, -35.82) * mm, "end": v(49.56, -35.7) * mm});
            skLineSegment(sketch, "E4095", {"start": v(49.56, -35.7) * mm, "end": v(49.38, -35.57) * mm});
            skLineSegment(sketch, "E4096", {"start": v(49.38, -35.57) * mm, "end": v(49.2, -35.45) * mm});
            skLineSegment(sketch, "E4097", {"start": v(49.2, -35.45) * mm, "end": v(49.02, -35.32) * mm});
            skLineSegment(sketch, "E4098", {"start": v(49.02, -35.32) * mm, "end": v(48.84, -35.2) * mm});
            skLineSegment(sketch, "E4099", {"start": v(48.84, -35.2) * mm, "end": v(48.66, -35.06) * mm});
            skLineSegment(sketch, "E4100", {"start": v(48.66, -35.06) * mm, "end": v(48.48, -34.94) * mm});
            skLineSegment(sketch, "E4101", {"start": v(48.48, -34.94) * mm, "end": v(48.3, -34.81) * mm});
            skLineSegment(sketch, "E4102", {"start": v(48.3, -34.81) * mm, "end": v(48.13, -34.68) * mm});
            skLineSegment(sketch, "E4103", {"start": v(48.13, -34.68) * mm, "end": v(47.94, -34.56) * mm});
            skLineSegment(sketch, "E4104", {"start": v(47.94, -34.56) * mm, "end": v(47.76, -34.43) * mm});
            skLineSegment(sketch, "E4105", {"start": v(47.76, -34.43) * mm, "end": v(47.63, -34.34) * mm});
            skLineSegment(sketch, "E4106", {"start": v(47.63, -34.34) * mm, "end": v(47.76, -34.16) * mm});
            skLineSegment(sketch, "E4107", {"start": v(47.76, -34.16) * mm, "end": v(47.88, -33.98) * mm});
            skLineSegment(sketch, "E4108", {"start": v(47.88, -33.98) * mm, "end": v(48, -33.8) * mm});
            skLineSegment(sketch, "E4109", {"start": v(48, -33.8) * mm, "end": v(48.12, -33.62) * mm});
            skLineSegment(sketch, "E4110", {"start": v(48.12, -33.62) * mm, "end": v(48.24, -33.43) * mm});
            skLineSegment(sketch, "E4111", {"start": v(48.24, -33.43) * mm, "end": v(48.37, -33.25) * mm});
            skLineSegment(sketch, "E4112", {"start": v(48.37, -33.25) * mm, "end": v(48.49, -33.07) * mm});
            skLineSegment(sketch, "E4113", {"start": v(48.49, -33.07) * mm, "end": v(48.6, -32.9) * mm});
            skLineSegment(sketch, "E4114", {"start": v(48.6, -32.9) * mm, "end": v(48.73, -32.71) * mm});
            skLineSegment(sketch, "E4115", {"start": v(48.73, -32.71) * mm, "end": v(48.85, -32.53) * mm});
            skLineSegment(sketch, "E4116", {"start": v(48.85, -32.53) * mm, "end": v(48.97, -32.35) * mm});
            skLineSegment(sketch, "E4117", {"start": v(48.97, -32.35) * mm, "end": v(49.03, -32.26) * mm});
            skLineSegment(sketch, "E4118", {"start": v(49.03, -32.26) * mm, "end": v(49.22, -32.38) * mm});
            skLineSegment(sketch, "E4119", {"start": v(49.22, -32.38) * mm, "end": v(49.4, -32.5) * mm});
            skLineSegment(sketch, "E4120", {"start": v(49.4, -32.5) * mm, "end": v(49.59, -32.62) * mm});
            skLineSegment(sketch, "E4121", {"start": v(49.59, -32.62) * mm, "end": v(49.77, -32.74) * mm});
            skLineSegment(sketch, "E4122", {"start": v(49.77, -32.74) * mm, "end": v(49.96, -32.86) * mm});
            skLineSegment(sketch, "E4123", {"start": v(49.96, -32.86) * mm, "end": v(50.14, -32.98) * mm});
            skLineSegment(sketch, "E4124", {"start": v(50.14, -32.98) * mm, "end": v(50.33, -33.1) * mm});
            skLineSegment(sketch, "E4125", {"start": v(50.33, -33.1) * mm, "end": v(50.5, -33.21) * mm});
            skLineSegment(sketch, "E4126", {"start": v(50.5, -33.21) * mm, "end": v(50.7, -33.34) * mm});
            skLineSegment(sketch, "E4127", {"start": v(50.7, -33.34) * mm, "end": v(50.88, -33.45) * mm});
            skLineSegment(sketch, "E4128", {"start": v(50.88, -33.45) * mm, "end": v(51.06, -33.57) * mm});
            skLineSegment(sketch, "E4129", {"start": v(51.06, -33.57) * mm, "end": v(51.25, -33.7) * mm});
            skLineSegment(sketch, "E4130", {"start": v(51.25, -33.7) * mm, "end": v(51.45, -33.82) * mm});
            skLineSegment(sketch, "E4131", {"start": v(51.45, -33.82) * mm, "end": v(51.66, -33.9) * mm});
            skLineSegment(sketch, "E4132", {"start": v(51.66, -33.9) * mm, "end": v(51.89, -33.93) * mm});
            skLineSegment(sketch, "E4133", {"start": v(51.89, -33.93) * mm, "end": v(52.11, -33.9) * mm});
            skLineSegment(sketch, "E4134", {"start": v(52.11, -33.9) * mm, "end": v(52.32, -33.8) * mm});
            skLineSegment(sketch, "E4135", {"start": v(52.32, -33.8) * mm, "end": v(52.5, -33.67) * mm});
            skLineSegment(sketch, "E4136", {"start": v(52.5, -33.67) * mm, "end": v(52.63, -33.48) * mm});
            skLineSegment(sketch, "E4137", {"start": v(52.63, -33.48) * mm, "end": v(52.72, -33.27) * mm});
            skLineSegment(sketch, "E4138", {"start": v(52.72, -33.27) * mm, "end": v(52.74, -33.05) * mm});
            skLineSegment(sketch, "E4139", {"start": v(52.74, -33.05) * mm, "end": v(52.7, -32.82) * mm});
            skLineSegment(sketch, "E4140", {"start": v(52.7, -32.82) * mm, "end": v(52.62, -32.61) * mm});
            skLineSegment(sketch, "E4141", {"start": v(52.62, -32.61) * mm, "end": v(52.47, -32.44) * mm});
            skLineSegment(sketch, "E4142", {"start": v(52.47, -32.44) * mm, "end": v(52.3, -32.3) * mm});
            skLineSegment(sketch, "E4143", {"start": v(52.3, -32.3) * mm, "end": v(52.11, -32.2) * mm});
            skLineSegment(sketch, "E4144", {"start": v(52.11, -32.2) * mm, "end": v(51.93, -32.08) * mm});
            skLineSegment(sketch, "E4145", {"start": v(51.93, -32.08) * mm, "end": v(51.74, -31.97) * mm});
            skLineSegment(sketch, "E4146", {"start": v(51.74, -31.97) * mm, "end": v(51.55, -31.85) * mm});
            skLineSegment(sketch, "E4147", {"start": v(51.55, -31.85) * mm, "end": v(51.36, -31.74) * mm});
            skLineSegment(sketch, "E4148", {"start": v(51.36, -31.74) * mm, "end": v(51.18, -31.63) * mm});
            skLineSegment(sketch, "E4149", {"start": v(51.18, -31.63) * mm, "end": v(50.99, -31.51) * mm});
            skLineSegment(sketch, "E4150", {"start": v(50.99, -31.51) * mm, "end": v(50.8, -31.4) * mm});
            skLineSegment(sketch, "E4151", {"start": v(50.8, -31.4) * mm, "end": v(50.61, -31.28) * mm});
            skLineSegment(sketch, "E4152", {"start": v(50.61, -31.28) * mm, "end": v(50.43, -31.17) * mm});
            skLineSegment(sketch, "E4153", {"start": v(50.43, -31.17) * mm, "end": v(50.23, -31.05) * mm});
            skLineSegment(sketch, "E4154", {"start": v(50.23, -31.05) * mm, "end": v(50.05, -30.94) * mm});
            skLineSegment(sketch, "E4155", {"start": v(50.05, -30.94) * mm, "end": v(49.91, -30.86) * mm});
            skLineSegment(sketch, "E4156", {"start": v(49.91, -30.86) * mm, "end": v(50.02, -30.67) * mm});
            skLineSegment(sketch, "E4157", {"start": v(50.02, -30.67) * mm, "end": v(50.13, -30.48) * mm});
            skLineSegment(sketch, "E4158", {"start": v(50.13, -30.48) * mm, "end": v(50.24, -30.3) * mm});
            skLineSegment(sketch, "E4159", {"start": v(50.24, -30.3) * mm, "end": v(50.35, -30.1) * mm});
            skLineSegment(sketch, "E4160", {"start": v(50.35, -30.1) * mm, "end": v(50.46, -29.92) * mm});
            skLineSegment(sketch, "E4161", {"start": v(50.46, -29.92) * mm, "end": v(50.56, -29.73) * mm});
            skLineSegment(sketch, "E4162", {"start": v(50.56, -29.73) * mm, "end": v(50.67, -29.54) * mm});
            skLineSegment(sketch, "E4163", {"start": v(50.67, -29.54) * mm, "end": v(50.78, -29.35) * mm});
            skLineSegment(sketch, "E4164", {"start": v(50.78, -29.35) * mm, "end": v(50.9, -29.16) * mm});
            skLineSegment(sketch, "E4165", {"start": v(50.9, -29.16) * mm, "end": v(51, -28.97) * mm});
            skLineSegment(sketch, "E4166", {"start": v(51, -28.97) * mm, "end": v(51.1, -28.78) * mm});
            skLineSegment(sketch, "E4167", {"start": v(51.1, -28.78) * mm, "end": v(51.16, -28.7) * mm});
            skLineSegment(sketch, "E4168", {"start": v(51.16, -28.7) * mm, "end": v(51.35, -28.8) * mm});
            skLineSegment(sketch, "E4169", {"start": v(51.35, -28.8) * mm, "end": v(51.54, -28.9) * mm});
            skLineSegment(sketch, "E4170", {"start": v(51.54, -28.9) * mm, "end": v(51.74, -29) * mm});
            skLineSegment(sketch, "E4171", {"start": v(51.74, -29) * mm, "end": v(51.93, -29.11) * mm});
            skLineSegment(sketch, "E4172", {"start": v(51.93, -29.11) * mm, "end": v(52.12, -29.22) * mm});
            skLineSegment(sketch, "E4173", {"start": v(52.12, -29.22) * mm, "end": v(52.32, -29.33) * mm});
            skLineSegment(sketch, "E4174", {"start": v(52.32, -29.33) * mm, "end": v(52.51, -29.43) * mm});
            skLineSegment(sketch, "E4175", {"start": v(52.51, -29.43) * mm, "end": v(52.7, -29.54) * mm});
            skLineSegment(sketch, "E4176", {"start": v(52.7, -29.54) * mm, "end": v(52.9, -29.65) * mm});
            skLineSegment(sketch, "E4177", {"start": v(52.9, -29.65) * mm, "end": v(53.09, -29.75) * mm});
            skLineSegment(sketch, "E4178", {"start": v(53.09, -29.75) * mm, "end": v(53.28, -29.86) * mm});
            skLineSegment(sketch, "E4179", {"start": v(53.28, -29.86) * mm, "end": v(53.48, -29.96) * mm});
            skLineSegment(sketch, "E4180", {"start": v(53.48, -29.96) * mm, "end": v(53.68, -30.07) * mm});
            skLineSegment(sketch, "E4181", {"start": v(53.68, -30.07) * mm, "end": v(53.9, -30.14) * mm});
            skLineSegment(sketch, "E4182", {"start": v(53.9, -30.14) * mm, "end": v(54.12, -30.16) * mm});
            skLineSegment(sketch, "E4183", {"start": v(54.12, -30.16) * mm, "end": v(54.35, -30.1) * mm});
            skLineSegment(sketch, "E4184", {"start": v(54.35, -30.1) * mm, "end": v(54.55, -30) * mm});
            skLineSegment(sketch, "E4185", {"start": v(54.55, -30) * mm, "end": v(54.72, -29.85) * mm});
            skLineSegment(sketch, "E4186", {"start": v(54.72, -29.85) * mm, "end": v(54.84, -29.66) * mm});
            skLineSegment(sketch, "E4187", {"start": v(54.84, -29.66) * mm, "end": v(54.9, -29.44) * mm});
            skLineSegment(sketch, "E4188", {"start": v(54.9, -29.44) * mm, "end": v(54.92, -29.21) * mm});
            skLineSegment(sketch, "E4189", {"start": v(54.92, -29.21) * mm, "end": v(54.87, -29) * mm});
            skLineSegment(sketch, "E4190", {"start": v(54.87, -29) * mm, "end": v(54.76, -28.8) * mm});
            skLineSegment(sketch, "E4191", {"start": v(54.76, -28.8) * mm, "end": v(54.6, -28.62) * mm});
            skLineSegment(sketch, "E4192", {"start": v(54.6, -28.62) * mm, "end": v(54.42, -28.51) * mm});
            skLineSegment(sketch, "E4193", {"start": v(54.42, -28.51) * mm, "end": v(54.23, -28.4) * mm});
            skLineSegment(sketch, "E4194", {"start": v(54.23, -28.4) * mm, "end": v(54.04, -28.3) * mm});
            skLineSegment(sketch, "E4195", {"start": v(54.04, -28.3) * mm, "end": v(53.84, -28.2) * mm});
            skLineSegment(sketch, "E4196", {"start": v(53.84, -28.2) * mm, "end": v(53.65, -28.1) * mm});
            skLineSegment(sketch, "E4197", {"start": v(53.65, -28.1) * mm, "end": v(53.45, -28) * mm});
            skLineSegment(sketch, "E4198", {"start": v(53.45, -28) * mm, "end": v(53.26, -27.9) * mm});
            skLineSegment(sketch, "E4199", {"start": v(53.26, -27.9) * mm, "end": v(53.06, -27.8) * mm});
            skLineSegment(sketch, "E4200", {"start": v(53.06, -27.8) * mm, "end": v(52.86, -27.7) * mm});
            skLineSegment(sketch, "E4201", {"start": v(52.86, -27.7) * mm, "end": v(52.67, -27.6) * mm});
            skLineSegment(sketch, "E4202", {"start": v(52.67, -27.6) * mm, "end": v(52.47, -27.5) * mm});
            skLineSegment(sketch, "E4203", {"start": v(52.47, -27.5) * mm, "end": v(52.28, -27.4) * mm});
            skLineSegment(sketch, "E4204", {"start": v(52.28, -27.4) * mm, "end": v(52.08, -27.3) * mm});
            skLineSegment(sketch, "E4205", {"start": v(52.08, -27.3) * mm, "end": v(51.94, -27.23) * mm});
            skLineSegment(sketch, "E4206", {"start": v(51.94, -27.23) * mm, "end": v(52.04, -27.03) * mm});
            skLineSegment(sketch, "E4207", {"start": v(52.04, -27.03) * mm, "end": v(52.13, -26.84) * mm});
            skLineSegment(sketch, "E4208", {"start": v(52.13, -26.84) * mm, "end": v(52.23, -26.64) * mm});
            skLineSegment(sketch, "E4209", {"start": v(52.23, -26.64) * mm, "end": v(52.32, -26.45) * mm});
            skLineSegment(sketch, "E4210", {"start": v(52.32, -26.45) * mm, "end": v(52.42, -26.25) * mm});
            skLineSegment(sketch, "E4211", {"start": v(52.42, -26.25) * mm, "end": v(52.51, -26.06) * mm});
            skLineSegment(sketch, "E4212", {"start": v(52.51, -26.06) * mm, "end": v(52.6, -25.86) * mm});
            skLineSegment(sketch, "E4213", {"start": v(52.6, -25.86) * mm, "end": v(52.7, -25.66) * mm});
            skLineSegment(sketch, "E4214", {"start": v(52.7, -25.66) * mm, "end": v(52.8, -25.47) * mm});
            skLineSegment(sketch, "E4215", {"start": v(52.8, -25.47) * mm, "end": v(52.9, -25.27) * mm});
            skLineSegment(sketch, "E4216", {"start": v(52.9, -25.27) * mm, "end": v(53, -25.08) * mm});
            skLineSegment(sketch, "E4217", {"start": v(53, -25.08) * mm, "end": v(53.04, -24.98) * mm});
            skLineSegment(sketch, "E4218", {"start": v(53.04, -24.98) * mm, "end": v(53.23, -25.07) * mm});
            skLineSegment(sketch, "E4219", {"start": v(53.23, -25.07) * mm, "end": v(53.43, -25.16) * mm});
            skLineSegment(sketch, "E4220", {"start": v(53.43, -25.16) * mm, "end": v(53.64, -25.26) * mm});
            skLineSegment(sketch, "E4221", {"start": v(53.64, -25.26) * mm, "end": v(53.83, -25.35) * mm});
            skLineSegment(sketch, "E4222", {"start": v(53.83, -25.35) * mm, "end": v(54.03, -25.44) * mm});
            skLineSegment(sketch, "E4223", {"start": v(54.03, -25.44) * mm, "end": v(54.23, -25.53) * mm});
            skLineSegment(sketch, "E4224", {"start": v(54.23, -25.53) * mm, "end": v(54.43, -25.63) * mm});
            skLineSegment(sketch, "E4225", {"start": v(54.43, -25.63) * mm, "end": v(54.63, -25.72) * mm});
            skLineSegment(sketch, "E4226", {"start": v(54.63, -25.72) * mm, "end": v(54.83, -25.81) * mm});
            skLineSegment(sketch, "E4227", {"start": v(54.83, -25.81) * mm, "end": v(55.03, -25.9) * mm});
            skLineSegment(sketch, "E4228", {"start": v(55.03, -25.9) * mm, "end": v(55.23, -26) * mm});
            skLineSegment(sketch, "E4229", {"start": v(55.23, -26) * mm, "end": v(55.43, -26.09) * mm});
            skLineSegment(sketch, "E4230", {"start": v(55.43, -26.09) * mm, "end": v(55.65, -26.18) * mm});
            skLineSegment(sketch, "E4231", {"start": v(55.65, -26.18) * mm, "end": v(55.87, -26.24) * mm});
            skLineSegment(sketch, "E4232", {"start": v(55.87, -26.24) * mm, "end": v(56.1, -26.23) * mm});
            skLineSegment(sketch, "E4233", {"start": v(56.1, -26.23) * mm, "end": v(56.31, -26.17) * mm});
            skLineSegment(sketch, "E4234", {"start": v(56.31, -26.17) * mm, "end": v(56.5, -26.05) * mm});
            skLineSegment(sketch, "E4235", {"start": v(56.5, -26.05) * mm, "end": v(56.66, -25.89) * mm});
            skLineSegment(sketch, "E4236", {"start": v(56.66, -25.89) * mm, "end": v(56.77, -25.69) * mm});
            skLineSegment(sketch, "E4237", {"start": v(56.77, -25.69) * mm, "end": v(56.82, -25.47) * mm});
            skLineSegment(sketch, "E4238", {"start": v(56.82, -25.47) * mm, "end": v(56.82, -25.24) * mm});
            skLineSegment(sketch, "E4239", {"start": v(56.82, -25.24) * mm, "end": v(56.75, -25.02) * mm});
            skLineSegment(sketch, "E4240", {"start": v(56.75, -25.02) * mm, "end": v(56.63, -24.83) * mm});
            skLineSegment(sketch, "E4241", {"start": v(56.63, -24.83) * mm, "end": v(56.47, -24.67) * mm});
            skLineSegment(sketch, "E4242", {"start": v(56.47, -24.67) * mm, "end": v(56.27, -24.57) * mm});
            skLineSegment(sketch, "E4243", {"start": v(56.27, -24.57) * mm, "end": v(56.08, -24.48) * mm});
            skLineSegment(sketch, "E4244", {"start": v(56.08, -24.48) * mm, "end": v(55.88, -24.4) * mm});
            skLineSegment(sketch, "E4245", {"start": v(55.88, -24.4) * mm, "end": v(55.68, -24.31) * mm});
            skLineSegment(sketch, "E4246", {"start": v(55.68, -24.31) * mm, "end": v(55.48, -24.23) * mm});
            skLineSegment(sketch, "E4247", {"start": v(55.48, -24.23) * mm, "end": v(55.27, -24.14) * mm});
            skLineSegment(sketch, "E4248", {"start": v(55.27, -24.14) * mm, "end": v(55.07, -24.05) * mm});
            skLineSegment(sketch, "E4249", {"start": v(55.07, -24.05) * mm, "end": v(54.87, -23.97) * mm});
            skLineSegment(sketch, "E4250", {"start": v(54.87, -23.97) * mm, "end": v(54.66, -23.88) * mm});
            skLineSegment(sketch, "E4251", {"start": v(54.66, -23.88) * mm, "end": v(54.46, -23.8) * mm});
            skLineSegment(sketch, "E4252", {"start": v(54.46, -23.8) * mm, "end": v(54.26, -23.7) * mm});
            skLineSegment(sketch, "E4253", {"start": v(54.26, -23.7) * mm, "end": v(54.06, -23.62) * mm});
            skLineSegment(sketch, "E4254", {"start": v(54.06, -23.62) * mm, "end": v(53.86, -23.53) * mm});
            skLineSegment(sketch, "E4255", {"start": v(53.86, -23.53) * mm, "end": v(53.71, -23.47) * mm});
            skLineSegment(sketch, "E4256", {"start": v(53.71, -23.47) * mm, "end": v(53.8, -23.27) * mm});
            skLineSegment(sketch, "E4257", {"start": v(53.8, -23.27) * mm, "end": v(53.87, -23.06) * mm});
            skLineSegment(sketch, "E4258", {"start": v(53.87, -23.06) * mm, "end": v(53.96, -22.86) * mm});
            skLineSegment(sketch, "E4259", {"start": v(53.96, -22.86) * mm, "end": v(54.04, -22.66) * mm});
            skLineSegment(sketch, "E4260", {"start": v(54.04, -22.66) * mm, "end": v(54.12, -22.46) * mm});
            skLineSegment(sketch, "E4261", {"start": v(54.12, -22.46) * mm, "end": v(54.2, -22.26) * mm});
            skLineSegment(sketch, "E4262", {"start": v(54.2, -22.26) * mm, "end": v(54.28, -22.05) * mm});
            skLineSegment(sketch, "E4263", {"start": v(54.28, -22.05) * mm, "end": v(54.36, -21.85) * mm});
            skLineSegment(sketch, "E4264", {"start": v(54.36, -21.85) * mm, "end": v(54.44, -21.65) * mm});
            skLineSegment(sketch, "E4265", {"start": v(54.44, -21.65) * mm, "end": v(54.53, -21.45) * mm});
            skLineSegment(sketch, "E4266", {"start": v(54.53, -21.45) * mm, "end": v(54.6, -21.25) * mm});
            skLineSegment(sketch, "E4267", {"start": v(54.6, -21.25) * mm, "end": v(54.65, -21.15) * mm});
            skLineSegment(sketch, "E4268", {"start": v(54.65, -21.15) * mm, "end": v(54.85, -21.23) * mm});
            skLineSegment(sketch, "E4269", {"start": v(54.85, -21.23) * mm, "end": v(55.06, -21.3) * mm});
            skLineSegment(sketch, "E4270", {"start": v(55.06, -21.3) * mm, "end": v(55.26, -21.38) * mm});
            skLineSegment(sketch, "E4271", {"start": v(55.26, -21.38) * mm, "end": v(55.47, -21.46) * mm});
            skLineSegment(sketch, "E4272", {"start": v(55.47, -21.46) * mm, "end": v(55.67, -21.54) * mm});
            skLineSegment(sketch, "E4273", {"start": v(55.67, -21.54) * mm, "end": v(55.88, -21.62) * mm});
            skLineSegment(sketch, "E4274", {"start": v(55.88, -21.62) * mm, "end": v(56.09, -21.7) * mm});
            skLineSegment(sketch, "E4275", {"start": v(56.09, -21.7) * mm, "end": v(56.29, -21.77) * mm});
            skLineSegment(sketch, "E4276", {"start": v(56.29, -21.77) * mm, "end": v(56.5, -21.85) * mm});
            skLineSegment(sketch, "E4277", {"start": v(56.5, -21.85) * mm, "end": v(56.7, -21.93) * mm});
            skLineSegment(sketch, "E4278", {"start": v(56.7, -21.93) * mm, "end": v(56.9, -22) * mm});
            skLineSegment(sketch, "E4279", {"start": v(56.9, -22) * mm, "end": v(57.12, -22.08) * mm});
            skLineSegment(sketch, "E4280", {"start": v(57.12, -22.08) * mm, "end": v(57.33, -22.17) * mm});
            skLineSegment(sketch, "E4281", {"start": v(57.33, -22.17) * mm, "end": v(57.56, -22.2) * mm});
            skLineSegment(sketch, "E4282", {"start": v(57.56, -22.2) * mm, "end": v(57.78, -22.18) * mm});
            skLineSegment(sketch, "E4283", {"start": v(57.78, -22.18) * mm, "end": v(58, -22.1) * mm});
            skLineSegment(sketch, "E4284", {"start": v(58, -22.1) * mm, "end": v(58.18, -21.97) * mm});
            skLineSegment(sketch, "E4285", {"start": v(58.18, -21.97) * mm, "end": v(58.33, -21.8) * mm});
            skLineSegment(sketch, "E4286", {"start": v(58.33, -21.8) * mm, "end": v(58.42, -21.6) * mm});
            skLineSegment(sketch, "E4287", {"start": v(58.42, -21.6) * mm, "end": v(58.46, -21.37) * mm});
            skLineSegment(sketch, "E4288", {"start": v(58.46, -21.37) * mm, "end": v(58.44, -21.14) * mm});
            skLineSegment(sketch, "E4289", {"start": v(58.44, -21.14) * mm, "end": v(58.36, -20.93) * mm});
            skLineSegment(sketch, "E4290", {"start": v(58.36, -20.93) * mm, "end": v(58.22, -20.74) * mm});
            skLineSegment(sketch, "E4291", {"start": v(58.22, -20.74) * mm, "end": v(58.05, -20.6) * mm});
            skLineSegment(sketch, "E4292", {"start": v(58.05, -20.6) * mm, "end": v(57.85, -20.51) * mm});
            skLineSegment(sketch, "E4293", {"start": v(57.85, -20.51) * mm, "end": v(57.64, -20.44) * mm});
            skLineSegment(sketch, "E4294", {"start": v(57.64, -20.44) * mm, "end": v(57.44, -20.37) * mm});
            skLineSegment(sketch, "E4295", {"start": v(57.44, -20.37) * mm, "end": v(57.23, -20.3) * mm});
            skLineSegment(sketch, "E4296", {"start": v(57.23, -20.3) * mm, "end": v(57.03, -20.22) * mm});
            skLineSegment(sketch, "E4297", {"start": v(57.03, -20.22) * mm, "end": v(56.82, -20.15) * mm});
            skLineSegment(sketch, "E4298", {"start": v(56.82, -20.15) * mm, "end": v(56.61, -20.08) * mm});
            skLineSegment(sketch, "E4299", {"start": v(56.61, -20.08) * mm, "end": v(56.4, -20) * mm});
            skLineSegment(sketch, "E4300", {"start": v(56.4, -20) * mm, "end": v(56.2, -19.93) * mm});
            skLineSegment(sketch, "E4301", {"start": v(56.2, -19.93) * mm, "end": v(55.99, -19.86) * mm});
            skLineSegment(sketch, "E4302", {"start": v(55.99, -19.86) * mm, "end": v(55.78, -19.8) * mm});
            skLineSegment(sketch, "E4303", {"start": v(55.78, -19.8) * mm, "end": v(55.57, -19.72) * mm});
            skLineSegment(sketch, "E4304", {"start": v(55.57, -19.72) * mm, "end": v(55.36, -19.64) * mm});
            skLineSegment(sketch, "E4305", {"start": v(55.36, -19.64) * mm, "end": v(55.21, -19.6) * mm});
            skLineSegment(sketch, "E4306", {"start": v(55.21, -19.6) * mm, "end": v(55.28, -19.39) * mm});
            skLineSegment(sketch, "E4307", {"start": v(55.28, -19.39) * mm, "end": v(55.35, -19.18) * mm});
            skLineSegment(sketch, "E4308", {"start": v(55.35, -19.18) * mm, "end": v(55.42, -18.97) * mm});
            skLineSegment(sketch, "E4309", {"start": v(55.42, -18.97) * mm, "end": v(55.48, -18.76) * mm});
            skLineSegment(sketch, "E4310", {"start": v(55.48, -18.76) * mm, "end": v(55.55, -18.56) * mm});
            skLineSegment(sketch, "E4311", {"start": v(55.55, -18.56) * mm, "end": v(55.62, -18.35) * mm});
            skLineSegment(sketch, "E4312", {"start": v(55.62, -18.35) * mm, "end": v(55.69, -18.14) * mm});
            skLineSegment(sketch, "E4313", {"start": v(55.69, -18.14) * mm, "end": v(55.75, -17.93) * mm});
            skLineSegment(sketch, "E4314", {"start": v(55.75, -17.93) * mm, "end": v(55.82, -17.73) * mm});
            skLineSegment(sketch, "E4315", {"start": v(55.82, -17.73) * mm, "end": v(55.89, -17.52) * mm});
            skLineSegment(sketch, "E4316", {"start": v(55.89, -17.52) * mm, "end": v(55.95, -17.31) * mm});
            skLineSegment(sketch, "E4317", {"start": v(55.95, -17.31) * mm, "end": v(55.99, -17.21) * mm});
            skLineSegment(sketch, "E4318", {"start": v(55.99, -17.21) * mm, "end": v(56.2, -17.28) * mm});
            skLineSegment(sketch, "E4319", {"start": v(56.2, -17.28) * mm, "end": v(56.4, -17.34) * mm});
            skLineSegment(sketch, "E4320", {"start": v(56.4, -17.34) * mm, "end": v(56.62, -17.4) * mm});
            skLineSegment(sketch, "E4321", {"start": v(56.62, -17.4) * mm, "end": v(56.83, -17.47) * mm});
            skLineSegment(sketch, "E4322", {"start": v(56.83, -17.47) * mm, "end": v(57.04, -17.53) * mm});
            skLineSegment(sketch, "E4323", {"start": v(57.04, -17.53) * mm, "end": v(57.25, -17.6) * mm});
            skLineSegment(sketch, "E4324", {"start": v(57.25, -17.6) * mm, "end": v(57.46, -17.66) * mm});
            skLineSegment(sketch, "E4325", {"start": v(57.46, -17.66) * mm, "end": v(57.67, -17.72) * mm});
            skLineSegment(sketch, "E4326", {"start": v(57.67, -17.72) * mm, "end": v(57.88, -17.78) * mm});
            skLineSegment(sketch, "E4327", {"start": v(57.88, -17.78) * mm, "end": v(58.1, -17.85) * mm});
            skLineSegment(sketch, "E4328", {"start": v(58.1, -17.85) * mm, "end": v(58.3, -17.91) * mm});
            skLineSegment(sketch, "E4329", {"start": v(58.3, -17.91) * mm, "end": v(58.51, -17.97) * mm});
            skLineSegment(sketch, "E4330", {"start": v(58.51, -17.97) * mm, "end": v(58.74, -18.04) * mm});
            skLineSegment(sketch, "E4331", {"start": v(58.74, -18.04) * mm, "end": v(58.96, -18.06) * mm});
            skLineSegment(sketch, "E4332", {"start": v(58.96, -18.06) * mm, "end": v(59.19, -18.03) * mm});
            skLineSegment(sketch, "E4333", {"start": v(59.19, -18.03) * mm, "end": v(59.4, -17.93) * mm});
            skLineSegment(sketch, "E4334", {"start": v(59.4, -17.93) * mm, "end": v(59.57, -17.8) * mm});
            skLineSegment(sketch, "E4335", {"start": v(59.57, -17.8) * mm, "end": v(59.7, -17.6) * mm});
            skLineSegment(sketch, "E4336", {"start": v(59.7, -17.6) * mm, "end": v(59.78, -17.4) * mm});
            skLineSegment(sketch, "E4337", {"start": v(59.78, -17.4) * mm, "end": v(59.8, -17.17) * mm});
            skLineSegment(sketch, "E4338", {"start": v(59.8, -17.17) * mm, "end": v(59.77, -16.94) * mm});
            skLineSegment(sketch, "E4339", {"start": v(59.77, -16.94) * mm, "end": v(59.67, -16.74) * mm});
            skLineSegment(sketch, "E4340", {"start": v(59.67, -16.74) * mm, "end": v(59.53, -16.56) * mm});
            skLineSegment(sketch, "E4341", {"start": v(59.53, -16.56) * mm, "end": v(59.34, -16.43) * mm});
            skLineSegment(sketch, "E4342", {"start": v(59.34, -16.43) * mm, "end": v(59.14, -16.36) * mm});
            skLineSegment(sketch, "E4343", {"start": v(59.14, -16.36) * mm, "end": v(58.93, -16.3) * mm});
            skLineSegment(sketch, "E4344", {"start": v(58.93, -16.3) * mm, "end": v(58.72, -16.24) * mm});
            skLineSegment(sketch, "E4345", {"start": v(58.72, -16.24) * mm, "end": v(58.5, -16.18) * mm});
            skLineSegment(sketch, "E4346", {"start": v(58.5, -16.18) * mm, "end": v(58.3, -16.12) * mm});
            skLineSegment(sketch, "E4347", {"start": v(58.3, -16.12) * mm, "end": v(58.08, -16.07) * mm});
            skLineSegment(sketch, "E4348", {"start": v(58.08, -16.07) * mm, "end": v(57.87, -16) * mm});
            skLineSegment(sketch, "E4349", {"start": v(57.87, -16) * mm, "end": v(57.66, -15.95) * mm});
            skLineSegment(sketch, "E4350", {"start": v(57.66, -15.95) * mm, "end": v(57.44, -15.9) * mm});
            skLineSegment(sketch, "E4351", {"start": v(57.44, -15.9) * mm, "end": v(57.23, -15.84) * mm});
            skLineSegment(sketch, "E4352", {"start": v(57.23, -15.84) * mm, "end": v(57.02, -15.78) * mm});
            skLineSegment(sketch, "E4353", {"start": v(57.02, -15.78) * mm, "end": v(56.8, -15.72) * mm});
            skLineSegment(sketch, "E4354", {"start": v(56.8, -15.72) * mm, "end": v(56.6, -15.66) * mm});
            skLineSegment(sketch, "E4355", {"start": v(56.6, -15.66) * mm, "end": v(56.44, -15.62) * mm});
            skLineSegment(sketch, "E4356", {"start": v(56.44, -15.62) * mm, "end": v(56.5, -15.4) * mm});
            skLineSegment(sketch, "E4357", {"start": v(56.5, -15.4) * mm, "end": v(56.55, -15.2) * mm});
            skLineSegment(sketch, "E4358", {"start": v(56.55, -15.2) * mm, "end": v(56.6, -14.99) * mm});
            skLineSegment(sketch, "E4359", {"start": v(56.6, -14.99) * mm, "end": v(56.65, -14.78) * mm});
            skLineSegment(sketch, "E4360", {"start": v(56.65, -14.78) * mm, "end": v(56.7, -14.56) * mm});
            skLineSegment(sketch, "E4361", {"start": v(56.7, -14.56) * mm, "end": v(56.76, -14.35) * mm});
            skLineSegment(sketch, "E4362", {"start": v(56.76, -14.35) * mm, "end": v(56.81, -14.14) * mm});
            skLineSegment(sketch, "E4363", {"start": v(56.81, -14.14) * mm, "end": v(56.87, -13.93) * mm});
            skLineSegment(sketch, "E4364", {"start": v(56.87, -13.93) * mm, "end": v(56.92, -13.72) * mm});
            skLineSegment(sketch, "E4365", {"start": v(56.92, -13.72) * mm, "end": v(56.97, -13.5) * mm});
            skLineSegment(sketch, "E4366", {"start": v(56.97, -13.5) * mm, "end": v(57.02, -13.3) * mm});
            skLineSegment(sketch, "E4367", {"start": v(57.02, -13.3) * mm, "end": v(57.05, -13.2) * mm});
            skLineSegment(sketch, "E4368", {"start": v(57.05, -13.2) * mm, "end": v(57.26, -13.24) * mm});
            skLineSegment(sketch, "E4369", {"start": v(57.26, -13.24) * mm, "end": v(57.47, -13.29) * mm});
            skLineSegment(sketch, "E4370", {"start": v(57.47, -13.29) * mm, "end": v(57.7, -13.34) * mm});
            skLineSegment(sketch, "E4371", {"start": v(57.7, -13.34) * mm, "end": v(57.9, -13.39) * mm});
            skLineSegment(sketch, "E4372", {"start": v(57.9, -13.39) * mm, "end": v(58.12, -13.44) * mm});
            skLineSegment(sketch, "E4373", {"start": v(58.12, -13.44) * mm, "end": v(58.34, -13.48) * mm});
            skLineSegment(sketch, "E4374", {"start": v(58.34, -13.48) * mm, "end": v(58.55, -13.53) * mm});
            skLineSegment(sketch, "E4375", {"start": v(58.55, -13.53) * mm, "end": v(58.76, -13.58) * mm});
            skLineSegment(sketch, "E4376", {"start": v(58.76, -13.58) * mm, "end": v(58.98, -13.63) * mm});
            skLineSegment(sketch, "E4377", {"start": v(58.98, -13.63) * mm, "end": v(59.2, -13.68) * mm});
            skLineSegment(sketch, "E4378", {"start": v(59.2, -13.68) * mm, "end": v(59.4, -13.73) * mm});
            skLineSegment(sketch, "E4379", {"start": v(59.4, -13.73) * mm, "end": v(59.62, -13.78) * mm});
            skLineSegment(sketch, "E4380", {"start": v(59.62, -13.78) * mm, "end": v(59.85, -13.83) * mm});
            skLineSegment(sketch, "E4381", {"start": v(59.85, -13.83) * mm, "end": v(60.08, -13.83) * mm});
            skLineSegment(sketch, "E4382", {"start": v(60.08, -13.83) * mm, "end": v(60.3, -13.78) * mm});
            skLineSegment(sketch, "E4383", {"start": v(60.3, -13.78) * mm, "end": v(60.5, -13.67) * mm});
            skLineSegment(sketch, "E4384", {"start": v(60.5, -13.67) * mm, "end": v(60.67, -13.52) * mm});
            skLineSegment(sketch, "E4385", {"start": v(60.67, -13.52) * mm, "end": v(60.78, -13.33) * mm});
            skLineSegment(sketch, "E4386", {"start": v(60.78, -13.33) * mm, "end": v(60.85, -13.1) * mm});
            skLineSegment(sketch, "E4387", {"start": v(60.85, -13.1) * mm, "end": v(60.85, -12.88) * mm});
            skLineSegment(sketch, "E4388", {"start": v(60.85, -12.88) * mm, "end": v(60.8, -12.66) * mm});
            skLineSegment(sketch, "E4389", {"start": v(60.8, -12.66) * mm, "end": v(60.7, -12.46) * mm});
            skLineSegment(sketch, "E4390", {"start": v(60.7, -12.46) * mm, "end": v(60.54, -12.3) * mm});
            skLineSegment(sketch, "E4391", {"start": v(60.54, -12.3) * mm, "end": v(60.34, -12.18) * mm});
            skLineSegment(sketch, "E4392", {"start": v(60.34, -12.18) * mm, "end": v(60.13, -12.12) * mm});
            skLineSegment(sketch, "E4393", {"start": v(60.13, -12.12) * mm, "end": v(59.92, -12.07) * mm});
            skLineSegment(sketch, "E4394", {"start": v(59.92, -12.07) * mm, "end": v(59.7, -12.03) * mm});
            skLineSegment(sketch, "E4395", {"start": v(59.7, -12.03) * mm, "end": v(59.5, -11.99) * mm});
            skLineSegment(sketch, "E4396", {"start": v(59.5, -11.99) * mm, "end": v(59.28, -11.95) * mm});
            skLineSegment(sketch, "E4397", {"start": v(59.28, -11.95) * mm, "end": v(59.06, -11.9) * mm});
            skLineSegment(sketch, "E4398", {"start": v(59.06, -11.9) * mm, "end": v(58.84, -11.86) * mm});
            skLineSegment(sketch, "E4399", {"start": v(58.84, -11.86) * mm, "end": v(58.63, -11.82) * mm});
            skLineSegment(sketch, "E4400", {"start": v(58.63, -11.82) * mm, "end": v(58.41, -11.77) * mm});
            skLineSegment(sketch, "E4401", {"start": v(58.41, -11.77) * mm, "end": v(58.2, -11.73) * mm});
            skLineSegment(sketch, "E4402", {"start": v(58.2, -11.73) * mm, "end": v(57.98, -11.7) * mm});
            skLineSegment(sketch, "E4403", {"start": v(57.98, -11.7) * mm, "end": v(57.76, -11.65) * mm});
            skLineSegment(sketch, "E4404", {"start": v(57.76, -11.65) * mm, "end": v(57.55, -11.6) * mm});
            skLineSegment(sketch, "E4405", {"start": v(57.55, -11.6) * mm, "end": v(57.4, -11.57) * mm});
            skLineSegment(sketch, "E4406", {"start": v(57.4, -11.57) * mm, "end": v(57.43, -11.36) * mm});
            skLineSegment(sketch, "E4407", {"start": v(57.43, -11.36) * mm, "end": v(57.47, -11.14) * mm});
            skLineSegment(sketch, "E4408", {"start": v(57.47, -11.14) * mm, "end": v(57.5, -10.93) * mm});
            skLineSegment(sketch, "E4409", {"start": v(57.5, -10.93) * mm, "end": v(57.54, -10.72) * mm});
            skLineSegment(sketch, "E4410", {"start": v(57.54, -10.72) * mm, "end": v(57.58, -10.5) * mm});
            skLineSegment(sketch, "E4411", {"start": v(57.58, -10.5) * mm, "end": v(57.62, -10.29) * mm});
            skLineSegment(sketch, "E4412", {"start": v(57.62, -10.29) * mm, "end": v(57.66, -10.07) * mm});
            skLineSegment(sketch, "E4413", {"start": v(57.66, -10.07) * mm, "end": v(57.7, -9.86) * mm});
            skLineSegment(sketch, "E4414", {"start": v(57.7, -9.86) * mm, "end": v(57.73, -9.64) * mm});
            skLineSegment(sketch, "E4415", {"start": v(57.73, -9.64) * mm, "end": v(57.77, -9.43) * mm});
            skLineSegment(sketch, "E4416", {"start": v(57.77, -9.43) * mm, "end": v(57.8, -9.21) * mm});
            skLineSegment(sketch, "E4417", {"start": v(57.8, -9.21) * mm, "end": v(57.83, -9.1) * mm});
            skLineSegment(sketch, "E4418", {"start": v(57.83, -9.1) * mm, "end": v(58.04, -9.14) * mm});
            skLineSegment(sketch, "E4419", {"start": v(58.04, -9.14) * mm, "end": v(58.26, -9.18) * mm});
            skLineSegment(sketch, "E4420", {"start": v(58.26, -9.18) * mm, "end": v(58.48, -9.2) * mm});
            skLineSegment(sketch, "E4421", {"start": v(58.48, -9.2) * mm, "end": v(58.7, -9.24) * mm});
            skLineSegment(sketch, "E4422", {"start": v(58.7, -9.24) * mm, "end": v(58.91, -9.28) * mm});
            skLineSegment(sketch, "E4423", {"start": v(58.91, -9.28) * mm, "end": v(59.13, -9.31) * mm});
            skLineSegment(sketch, "E4424", {"start": v(59.13, -9.31) * mm, "end": v(59.35, -9.34) * mm});
            skLineSegment(sketch, "E4425", {"start": v(59.35, -9.34) * mm, "end": v(59.56, -9.38) * mm});
            skLineSegment(sketch, "E4426", {"start": v(59.56, -9.38) * mm, "end": v(59.78, -9.41) * mm});
            skLineSegment(sketch, "E4427", {"start": v(59.78, -9.41) * mm, "end": v(60, -9.44) * mm});
            skLineSegment(sketch, "E4428", {"start": v(60, -9.44) * mm, "end": v(60.21, -9.48) * mm});
            skLineSegment(sketch, "E4429", {"start": v(60.21, -9.48) * mm, "end": v(60.44, -9.51) * mm});
            skLineSegment(sketch, "E4430", {"start": v(60.44, -9.51) * mm, "end": v(60.67, -9.55) * mm});
            skLineSegment(sketch, "E4431", {"start": v(60.67, -9.55) * mm, "end": v(60.9, -9.54) * mm});
            skLineSegment(sketch, "E4432", {"start": v(60.9, -9.54) * mm, "end": v(61.11, -9.47) * mm});
            skLineSegment(sketch, "E4433", {"start": v(61.11, -9.47) * mm, "end": v(61.3, -9.35) * mm});
            skLineSegment(sketch, "E4434", {"start": v(61.3, -9.35) * mm, "end": v(61.46, -9.18) * mm});
            skLineSegment(sketch, "E4435", {"start": v(61.46, -9.18) * mm, "end": v(61.56, -8.98) * mm});
            skLineSegment(sketch, "E4436", {"start": v(61.56, -8.98) * mm, "end": v(61.61, -8.76) * mm});
            skLineSegment(sketch, "E4437", {"start": v(61.61, -8.76) * mm, "end": v(61.6, -8.53) * mm});
            skLineSegment(sketch, "E4438", {"start": v(61.6, -8.53) * mm, "end": v(61.53, -8.31) * mm});
            skLineSegment(sketch, "E4439", {"start": v(61.53, -8.31) * mm, "end": v(61.41, -8.12) * mm});
            skLineSegment(sketch, "E4440", {"start": v(61.41, -8.12) * mm, "end": v(61.24, -7.97) * mm});
            skLineSegment(sketch, "E4441", {"start": v(61.24, -7.97) * mm, "end": v(61.04, -7.87) * mm});
            skLineSegment(sketch, "E4442", {"start": v(61.04, -7.87) * mm, "end": v(60.83, -7.82) * mm});
            skLineSegment(sketch, "E4443", {"start": v(60.83, -7.82) * mm, "end": v(60.61, -7.8) * mm});
            skLineSegment(sketch, "E4444", {"start": v(60.61, -7.8) * mm, "end": v(60.4, -7.76) * mm});
            skLineSegment(sketch, "E4445", {"start": v(60.4, -7.76) * mm, "end": v(60.18, -7.74) * mm});
            skLineSegment(sketch, "E4446", {"start": v(60.18, -7.74) * mm, "end": v(59.96, -7.71) * mm});
            skLineSegment(sketch, "E4447", {"start": v(59.96, -7.71) * mm, "end": v(59.74, -7.68) * mm});
            skLineSegment(sketch, "E4448", {"start": v(59.74, -7.68) * mm, "end": v(59.53, -7.65) * mm});
            skLineSegment(sketch, "E4449", {"start": v(59.53, -7.65) * mm, "end": v(59.3, -7.63) * mm});
            skLineSegment(sketch, "E4450", {"start": v(59.3, -7.63) * mm, "end": v(59.09, -7.6) * mm});
            skLineSegment(sketch, "E4451", {"start": v(59.09, -7.6) * mm, "end": v(58.87, -7.57) * mm});
            skLineSegment(sketch, "E4452", {"start": v(58.87, -7.57) * mm, "end": v(58.65, -7.54) * mm});
            skLineSegment(sketch, "E4453", {"start": v(58.65, -7.54) * mm, "end": v(58.43, -7.52) * mm});
            skLineSegment(sketch, "E4454", {"start": v(58.43, -7.52) * mm, "end": v(58.22, -7.49) * mm});
            skLineSegment(sketch, "E4455", {"start": v(58.22, -7.49) * mm, "end": v(58.06, -7.47) * mm});
            skLineSegment(sketch, "E4456", {"start": v(58.06, -7.47) * mm, "end": v(58.08, -7.25) * mm});
            skLineSegment(sketch, "E4457", {"start": v(58.08, -7.25) * mm, "end": v(58.1, -7.04) * mm});
            skLineSegment(sketch, "E4458", {"start": v(58.1, -7.04) * mm, "end": v(58.13, -6.82) * mm});
            skLineSegment(sketch, "E4459", {"start": v(58.13, -6.82) * mm, "end": v(58.15, -6.6) * mm});
            skLineSegment(sketch, "E4460", {"start": v(58.15, -6.6) * mm, "end": v(58.17, -6.39) * mm});
            skLineSegment(sketch, "E4461", {"start": v(58.17, -6.39) * mm, "end": v(58.2, -6.17) * mm});
            skLineSegment(sketch, "E4462", {"start": v(58.2, -6.17) * mm, "end": v(58.22, -5.95) * mm});
            skLineSegment(sketch, "E4463", {"start": v(58.22, -5.95) * mm, "end": v(58.24, -5.74) * mm});
            skLineSegment(sketch, "E4464", {"start": v(58.24, -5.74) * mm, "end": v(58.26, -5.52) * mm});
            skLineSegment(sketch, "E4465", {"start": v(58.26, -5.52) * mm, "end": v(58.29, -5.3) * mm});
            skLineSegment(sketch, "E4466", {"start": v(58.29, -5.3) * mm, "end": v(58.3, -5.09) * mm});
            skLineSegment(sketch, "E4467", {"start": v(58.3, -5.09) * mm, "end": v(58.32, -4.98) * mm});
            skLineSegment(sketch, "E4468", {"start": v(58.32, -4.98) * mm, "end": v(58.54, -5) * mm});
            skLineSegment(sketch, "E4469", {"start": v(58.54, -5) * mm, "end": v(58.75, -5.02) * mm});
            skLineSegment(sketch, "E4470", {"start": v(58.75, -5.02) * mm, "end": v(58.98, -5.04) * mm});
            skLineSegment(sketch, "E4471", {"start": v(58.98, -5.04) * mm, "end": v(59.2, -5.05) * mm});
            skLineSegment(sketch, "E4472", {"start": v(59.2, -5.05) * mm, "end": v(59.41, -5.07) * mm});
            skLineSegment(sketch, "E4473", {"start": v(59.41, -5.07) * mm, "end": v(59.63, -5.1) * mm});
            skLineSegment(sketch, "E4474", {"start": v(59.63, -5.1) * mm, "end": v(59.85, -5.1) * mm});
            skLineSegment(sketch, "E4475", {"start": v(59.85, -5.1) * mm, "end": v(60.07, -5.13) * mm});
            skLineSegment(sketch, "E4476", {"start": v(60.07, -5.13) * mm, "end": v(60.3, -5.15) * mm});
            skLineSegment(sketch, "E4477", {"start": v(60.3, -5.15) * mm, "end": v(60.5, -5.16) * mm});
            skLineSegment(sketch, "E4478", {"start": v(60.5, -5.16) * mm, "end": v(60.73, -5.18) * mm});
            skLineSegment(sketch, "E4479", {"start": v(60.73, -5.18) * mm, "end": v(60.95, -5.2) * mm});
            skLineSegment(sketch, "E4480", {"start": v(60.95, -5.2) * mm, "end": v(61.18, -5.22) * mm});
            skLineSegment(sketch, "E4481", {"start": v(61.18, -5.22) * mm, "end": v(61.4, -5.2) * mm});
            skLineSegment(sketch, "E4482", {"start": v(61.4, -5.2) * mm, "end": v(61.62, -5.11) * mm});
            skLineSegment(sketch, "E4483", {"start": v(61.62, -5.11) * mm, "end": v(61.8, -4.98) * mm});
            skLineSegment(sketch, "E4484", {"start": v(61.8, -4.98) * mm, "end": v(61.95, -4.8) * mm});
            skLineSegment(sketch, "E4485", {"start": v(61.95, -4.8) * mm, "end": v(62.04, -4.6) * mm});
            skLineSegment(sketch, "E4486", {"start": v(62.04, -4.6) * mm, "end": v(62.07, -4.37) * mm});
            skLineSegment(sketch, "E4487", {"start": v(62.07, -4.37) * mm, "end": v(62.04, -4.14) * mm});
            skLineSegment(sketch, "E4488", {"start": v(62.04, -4.14) * mm, "end": v(61.96, -3.93) * mm});
            skLineSegment(sketch, "E4489", {"start": v(61.96, -3.93) * mm, "end": v(61.83, -3.75) * mm});
            skLineSegment(sketch, "E4490", {"start": v(61.83, -3.75) * mm, "end": v(61.65, -3.6) * mm});
            skLineSegment(sketch, "E4491", {"start": v(61.65, -3.6) * mm, "end": v(61.44, -3.52) * mm});
            skLineSegment(sketch, "E4492", {"start": v(61.44, -3.52) * mm, "end": v(61.22, -3.49) * mm});
            skLineSegment(sketch, "E4493", {"start": v(61.22, -3.49) * mm, "end": v(61, -3.47) * mm});
            skLineSegment(sketch, "E4494", {"start": v(61, -3.47) * mm, "end": v(60.79, -3.46) * mm});
            skLineSegment(sketch, "E4495", {"start": v(60.79, -3.46) * mm, "end": v(60.57, -3.45) * mm});
            skLineSegment(sketch, "E4496", {"start": v(60.57, -3.45) * mm, "end": v(60.35, -3.44) * mm});
            skLineSegment(sketch, "E4497", {"start": v(60.35, -3.44) * mm, "end": v(60.13, -3.42) * mm});
            skLineSegment(sketch, "E4498", {"start": v(60.13, -3.42) * mm, "end": v(59.91, -3.41) * mm});
            skLineSegment(sketch, "E4499", {"start": v(59.91, -3.41) * mm, "end": v(59.7, -3.4) * mm});
            skLineSegment(sketch, "E4500", {"start": v(59.7, -3.4) * mm, "end": v(59.47, -3.39) * mm});
            skLineSegment(sketch, "E4501", {"start": v(59.47, -3.39) * mm, "end": v(59.25, -3.37) * mm});
            skLineSegment(sketch, "E4502", {"start": v(59.25, -3.37) * mm, "end": v(59.04, -3.36) * mm});
            skLineSegment(sketch, "E4503", {"start": v(59.04, -3.36) * mm, "end": v(58.81, -3.35) * mm});
            skLineSegment(sketch, "E4504", {"start": v(58.81, -3.35) * mm, "end": v(58.6, -3.34) * mm});
            skLineSegment(sketch, "E4505", {"start": v(58.6, -3.34) * mm, "end": v(58.44, -3.33) * mm});
            skLineSegment(sketch, "E4506", {"start": v(58.44, -3.33) * mm, "end": v(58.44, -3.11) * mm});
            skLineSegment(sketch, "E4507", {"start": v(58.44, -3.11) * mm, "end": v(58.45, -2.9) * mm});
            skLineSegment(sketch, "E4508", {"start": v(58.45, -2.9) * mm, "end": v(58.46, -2.68) * mm});
            skLineSegment(sketch, "E4509", {"start": v(58.46, -2.68) * mm, "end": v(58.47, -2.46) * mm});
            skLineSegment(sketch, "E4510", {"start": v(58.47, -2.46) * mm, "end": v(58.47, -2.24) * mm});
            skLineSegment(sketch, "E4511", {"start": v(58.47, -2.24) * mm, "end": v(58.48, -2.02) * mm});
            skLineSegment(sketch, "E4512", {"start": v(58.48, -2.02) * mm, "end": v(58.49, -1.8) * mm});
            skLineSegment(sketch, "E4513", {"start": v(58.49, -1.8) * mm, "end": v(58.5, -1.59) * mm});
            skLineSegment(sketch, "E4514", {"start": v(58.5, -1.59) * mm, "end": v(58.5, -1.37) * mm});
            skLineSegment(sketch, "E4515", {"start": v(58.5, -1.37) * mm, "end": v(58.51, -1.15) * mm});
            skLineSegment(sketch, "E4516", {"start": v(58.51, -1.15) * mm, "end": v(58.52, -0.93) * mm});
            skLineSegment(sketch, "E4517", {"start": v(58.52, -0.93) * mm, "end": v(58.52, -0.83) * mm});
            skLineSegment(sketch, "E4518", {"start": v(-9.92, 3.52) * mm, "end": v(-9.68, 4.07) * mm});
            skLineSegment(sketch, "E4519", {"start": v(-9.68, 4.07) * mm, "end": v(-9.4, 4.6) * mm});
            skLineSegment(sketch, "E4520", {"start": v(-9.4, 4.6) * mm, "end": v(-9.1, 5.12) * mm});
            skLineSegment(sketch, "E4521", {"start": v(-9.1, 5.12) * mm, "end": v(-8.77, 5.62) * mm});
            skLineSegment(sketch, "E4522", {"start": v(-8.77, 5.62) * mm, "end": v(-8.4, 6.1) * mm});
            skLineSegment(sketch, "E4523", {"start": v(-8.4, 6.1) * mm, "end": v(-8, 6.54) * mm});
            skLineSegment(sketch, "E4524", {"start": v(-8, 6.54) * mm, "end": v(-7.58, 6.97) * mm});
            skLineSegment(sketch, "E4525", {"start": v(-7.58, 6.97) * mm, "end": v(-7.13, 7.36) * mm});
            skLineSegment(sketch, "E4526", {"start": v(-7.13, 7.36) * mm, "end": v(-6.65, 7.73) * mm});
            skLineSegment(sketch, "E4527", {"start": v(-6.65, 7.73) * mm, "end": v(-6.16, 8.07) * mm});
            skLineSegment(sketch, "E4528", {"start": v(-6.16, 8.07) * mm, "end": v(-5.64, 8.37) * mm});
            skLineSegment(sketch, "E4529", {"start": v(-5.64, 8.37) * mm, "end": v(-5.1, 8.65) * mm});
            skLineSegment(sketch, "E4530", {"start": v(-5.1, 8.65) * mm, "end": v(-4.55, 8.89) * mm});
            skLineSegment(sketch, "E4531", {"start": v(-4.55, 8.89) * mm, "end": v(-4.04, 9.07) * mm});
            skLineSegment(sketch, "E4532", {"start": v(-4.04, 9.07) * mm, "end": v(-4.17, 53.5) * mm});
            skLineSegment(sketch, "E4533", {"start": v(-4.17, 53.5) * mm, "end": v(-4.4, 53.5) * mm});
            skLineSegment(sketch, "E4534", {"start": v(-4.4, 53.5) * mm, "end": v(-7.75, 53.18) * mm});
            skLineSegment(sketch, "E4535", {"start": v(-7.75, 53.18) * mm, "end": v(-11.08, 52.66) * mm});
            skLineSegment(sketch, "E4536", {"start": v(-11.08, 52.66) * mm, "end": v(-14.37, 51.92) * mm});
            skLineSegment(sketch, "E4537", {"start": v(-14.37, 51.92) * mm, "end": v(-17.6, 50.98) * mm});
            skLineSegment(sketch, "E4538", {"start": v(-17.6, 50.98) * mm, "end": v(-20.77, 49.84) * mm});
            skLineSegment(sketch, "E4539", {"start": v(-20.77, 49.84) * mm, "end": v(-23.86, 48.5) * mm});
            skLineSegment(sketch, "E4540", {"start": v(-23.86, 48.5) * mm, "end": v(-26.86, 46.97) * mm});
            skLineSegment(sketch, "E4541", {"start": v(-26.86, 46.97) * mm, "end": v(-29.76, 45.26) * mm});
            skLineSegment(sketch, "E4542", {"start": v(-29.76, 45.26) * mm, "end": v(-32.54, 43.37) * mm});
            skLineSegment(sketch, "E4543", {"start": v(-32.54, 43.37) * mm, "end": v(-35.2, 41.3) * mm});
            skLineSegment(sketch, "E4544", {"start": v(-35.2, 41.3) * mm, "end": v(-37.73, 39.08) * mm});
            skLineSegment(sketch, "E4545", {"start": v(-37.73, 39.08) * mm, "end": v(-40.11, 36.7) * mm});
            skLineSegment(sketch, "E4546", {"start": v(-40.11, 36.7) * mm, "end": v(-42.34, 34.17) * mm});
            skLineSegment(sketch, "E4547", {"start": v(-42.34, 34.17) * mm, "end": v(-44.4, 31.5) * mm});
            skLineSegment(sketch, "E4548", {"start": v(-44.4, 31.5) * mm, "end": v(-46.3, 28.72) * mm});
            skLineSegment(sketch, "E4549", {"start": v(-46.3, 28.72) * mm, "end": v(-48, 25.82) * mm});
            skLineSegment(sketch, "E4550", {"start": v(-48, 25.82) * mm, "end": v(-49.54, 22.82) * mm});
            skLineSegment(sketch, "E4551", {"start": v(-49.54, 22.82) * mm, "end": v(-50.88, 19.73) * mm});
            skLineSegment(sketch, "E4552", {"start": v(-50.88, 19.73) * mm, "end": v(-52.02, 16.57) * mm});
            skLineSegment(sketch, "E4553", {"start": v(-52.02, 16.57) * mm, "end": v(-52.96, 13.33) * mm});
            skLineSegment(sketch, "E4554", {"start": v(-52.96, 13.33) * mm, "end": v(-53.7, 10.04) * mm});
            skLineSegment(sketch, "E4555", {"start": v(-53.7, 10.04) * mm, "end": v(-54.22, 6.72) * mm});
            skLineSegment(sketch, "E4556", {"start": v(-54.22, 6.72) * mm, "end": v(-54.53, 3.37) * mm});
            skLineSegment(sketch, "E4557", {"start": v(-54.53, 3.37) * mm, "end": v(-54.54, 3.13) * mm});
            skLineSegment(sketch, "E4558", {"start": v(-54.54, 3.13) * mm, "end": v(-10.1, 3) * mm});
            skLineSegment(sketch, "E4559", {"start": v(-10.1, 3) * mm, "end": v(-9.92, 3.52) * mm});
            skLineSegment(sketch, "E4560", {"start": v(52.47, 3.13) * mm, "end": v(52.46, 3.37) * mm});
            skLineSegment(sketch, "E4561", {"start": v(52.46, 3.37) * mm, "end": v(52.15, 6.72) * mm});
            skLineSegment(sketch, "E4562", {"start": v(52.15, 6.72) * mm, "end": v(51.62, 10.04) * mm});
            skLineSegment(sketch, "E4563", {"start": v(51.62, 10.04) * mm, "end": v(50.89, 13.33) * mm});
            skLineSegment(sketch, "E4564", {"start": v(50.89, 13.33) * mm, "end": v(49.95, 16.57) * mm});
            skLineSegment(sketch, "E4565", {"start": v(49.95, 16.57) * mm, "end": v(48.8, 19.73) * mm});
            skLineSegment(sketch, "E4566", {"start": v(48.8, 19.73) * mm, "end": v(47.47, 22.82) * mm});
            skLineSegment(sketch, "E4567", {"start": v(47.47, 22.82) * mm, "end": v(45.94, 25.82) * mm});
            skLineSegment(sketch, "E4568", {"start": v(45.94, 25.82) * mm, "end": v(44.22, 28.72) * mm});
            skLineSegment(sketch, "E4569", {"start": v(44.22, 28.72) * mm, "end": v(42.33, 31.5) * mm});
            skLineSegment(sketch, "E4570", {"start": v(42.33, 31.5) * mm, "end": v(40.27, 34.17) * mm});
            skLineSegment(sketch, "E4571", {"start": v(40.27, 34.17) * mm, "end": v(38.04, 36.7) * mm});
            skLineSegment(sketch, "E4572", {"start": v(38.04, 36.7) * mm, "end": v(35.66, 39.08) * mm});
            skLineSegment(sketch, "E4573", {"start": v(35.66, 39.08) * mm, "end": v(33.13, 41.3) * mm});
            skLineSegment(sketch, "E4574", {"start": v(33.13, 41.3) * mm, "end": v(30.47, 43.37) * mm});
            skLineSegment(sketch, "E4575", {"start": v(30.47, 43.37) * mm, "end": v(27.69, 45.26) * mm});
            skLineSegment(sketch, "E4576", {"start": v(27.69, 45.26) * mm, "end": v(24.79, 46.97) * mm});
            skLineSegment(sketch, "E4577", {"start": v(24.79, 46.97) * mm, "end": v(21.79, 48.5) * mm});
            skLineSegment(sketch, "E4578", {"start": v(21.79, 48.5) * mm, "end": v(18.7, 49.84) * mm});
            skLineSegment(sketch, "E4579", {"start": v(18.7, 49.84) * mm, "end": v(15.53, 50.98) * mm});
            skLineSegment(sketch, "E4580", {"start": v(15.53, 50.98) * mm, "end": v(12.3, 51.92) * mm});
            skLineSegment(sketch, "E4581", {"start": v(12.3, 51.92) * mm, "end": v(9, 52.66) * mm});
            skLineSegment(sketch, "E4582", {"start": v(9, 52.66) * mm, "end": v(5.68, 53.18) * mm});
            skLineSegment(sketch, "E4583", {"start": v(5.68, 53.18) * mm, "end": v(2.33, 53.5) * mm});
            skLineSegment(sketch, "E4584", {"start": v(2.33, 53.5) * mm, "end": v(2.1, 53.5) * mm});
            skLineSegment(sketch, "E4585", {"start": v(2.1, 53.5) * mm, "end": v(1.97, 9.07) * mm});
            skLineSegment(sketch, "E4586", {"start": v(1.97, 9.07) * mm, "end": v(2.48, 8.89) * mm});
            skLineSegment(sketch, "E4587", {"start": v(2.48, 8.89) * mm, "end": v(3.03, 8.65) * mm});
            skLineSegment(sketch, "E4588", {"start": v(3.03, 8.65) * mm, "end": v(3.57, 8.37) * mm});
            skLineSegment(sketch, "E4589", {"start": v(3.57, 8.37) * mm, "end": v(4.08, 8.07) * mm});
            skLineSegment(sketch, "E4590", {"start": v(4.08, 8.07) * mm, "end": v(4.58, 7.73) * mm});
            skLineSegment(sketch, "E4591", {"start": v(4.58, 7.73) * mm, "end": v(5.06, 7.36) * mm});
            skLineSegment(sketch, "E4592", {"start": v(5.06, 7.36) * mm, "end": v(5.5, 6.97) * mm});
            skLineSegment(sketch, "E4593", {"start": v(5.5, 6.97) * mm, "end": v(5.93, 6.54) * mm});
            skLineSegment(sketch, "E4594", {"start": v(5.93, 6.54) * mm, "end": v(6.33, 6.1) * mm});
            skLineSegment(sketch, "E4595", {"start": v(6.33, 6.1) * mm, "end": v(6.7, 5.62) * mm});
            skLineSegment(sketch, "E4596", {"start": v(6.7, 5.62) * mm, "end": v(7.03, 5.12) * mm});
            skLineSegment(sketch, "E4597", {"start": v(7.03, 5.12) * mm, "end": v(7.34, 4.6) * mm});
            skLineSegment(sketch, "E4598", {"start": v(7.34, 4.6) * mm, "end": v(7.61, 4.07) * mm});
            skLineSegment(sketch, "E4599", {"start": v(7.61, 4.07) * mm, "end": v(7.85, 3.52) * mm});
            skLineSegment(sketch, "E4600", {"start": v(7.85, 3.52) * mm, "end": v(8.03, 3) * mm});
            skLineSegment(sketch, "E4601", {"start": v(8.03, 3) * mm, "end": v(52.47, 3.13) * mm});
            skLineSegment(sketch, "E4602", {"start": v(2.33, -53.5) * mm, "end": v(5.68, -53.18) * mm});
            skLineSegment(sketch, "E4603", {"start": v(5.68, -53.18) * mm, "end": v(9, -52.66) * mm});
            skLineSegment(sketch, "E4604", {"start": v(9, -52.66) * mm, "end": v(12.3, -51.92) * mm});
            skLineSegment(sketch, "E4605", {"start": v(12.3, -51.92) * mm, "end": v(15.53, -50.98) * mm});
            skLineSegment(sketch, "E4606", {"start": v(15.53, -50.98) * mm, "end": v(18.7, -49.84) * mm});
            skLineSegment(sketch, "E4607", {"start": v(18.7, -49.84) * mm, "end": v(21.79, -48.5) * mm});
            skLineSegment(sketch, "E4608", {"start": v(21.79, -48.5) * mm, "end": v(24.79, -46.97) * mm});
            skLineSegment(sketch, "E4609", {"start": v(24.79, -46.97) * mm, "end": v(27.69, -45.26) * mm});
            skLineSegment(sketch, "E4610", {"start": v(27.69, -45.26) * mm, "end": v(30.47, -43.37) * mm});
            skLineSegment(sketch, "E4611", {"start": v(30.47, -43.37) * mm, "end": v(33.13, -41.3) * mm});
            skLineSegment(sketch, "E4612", {"start": v(33.13, -41.3) * mm, "end": v(35.66, -39.08) * mm});
            skLineSegment(sketch, "E4613", {"start": v(35.66, -39.08) * mm, "end": v(38.04, -36.7) * mm});
            skLineSegment(sketch, "E4614", {"start": v(38.04, -36.7) * mm, "end": v(40.27, -34.17) * mm});
            skLineSegment(sketch, "E4615", {"start": v(40.27, -34.17) * mm, "end": v(42.33, -31.5) * mm});
            skLineSegment(sketch, "E4616", {"start": v(42.33, -31.5) * mm, "end": v(44.22, -28.72) * mm});
            skLineSegment(sketch, "E4617", {"start": v(44.22, -28.72) * mm, "end": v(45.94, -25.82) * mm});
            skLineSegment(sketch, "E4618", {"start": v(45.94, -25.82) * mm, "end": v(47.47, -22.82) * mm});
            skLineSegment(sketch, "E4619", {"start": v(47.47, -22.82) * mm, "end": v(48.8, -19.73) * mm});
            skLineSegment(sketch, "E4620", {"start": v(48.8, -19.73) * mm, "end": v(49.95, -16.57) * mm});
            skLineSegment(sketch, "E4621", {"start": v(49.95, -16.57) * mm, "end": v(50.89, -13.33) * mm});
            skLineSegment(sketch, "E4622", {"start": v(50.89, -13.33) * mm, "end": v(51.62, -10.04) * mm});
            skLineSegment(sketch, "E4623", {"start": v(51.62, -10.04) * mm, "end": v(52.15, -6.72) * mm});
            skLineSegment(sketch, "E4624", {"start": v(52.15, -6.72) * mm, "end": v(52.46, -3.37) * mm});
            skLineSegment(sketch, "E4625", {"start": v(52.46, -3.37) * mm, "end": v(52.47, -3.13) * mm});
            skLineSegment(sketch, "E4626", {"start": v(52.47, -3.13) * mm, "end": v(8.03, -3) * mm});
            skLineSegment(sketch, "E4627", {"start": v(8.03, -3) * mm, "end": v(7.85, -3.52) * mm});
            skLineSegment(sketch, "E4628", {"start": v(7.85, -3.52) * mm, "end": v(7.61, -4.07) * mm});
            skLineSegment(sketch, "E4629", {"start": v(7.61, -4.07) * mm, "end": v(7.34, -4.6) * mm});
            skLineSegment(sketch, "E4630", {"start": v(7.34, -4.6) * mm, "end": v(7.03, -5.12) * mm});
            skLineSegment(sketch, "E4631", {"start": v(7.03, -5.12) * mm, "end": v(6.7, -5.62) * mm});
            skLineSegment(sketch, "E4632", {"start": v(6.7, -5.62) * mm, "end": v(6.33, -6.1) * mm});
            skLineSegment(sketch, "E4633", {"start": v(6.33, -6.1) * mm, "end": v(5.93, -6.54) * mm});
            skLineSegment(sketch, "E4634", {"start": v(5.93, -6.54) * mm, "end": v(5.5, -6.97) * mm});
            skLineSegment(sketch, "E4635", {"start": v(5.5, -6.97) * mm, "end": v(5.06, -7.36) * mm});
            skLineSegment(sketch, "E4636", {"start": v(5.06, -7.36) * mm, "end": v(4.58, -7.73) * mm});
            skLineSegment(sketch, "E4637", {"start": v(4.58, -7.73) * mm, "end": v(4.08, -8.07) * mm});
            skLineSegment(sketch, "E4638", {"start": v(4.08, -8.07) * mm, "end": v(3.57, -8.37) * mm});
            skLineSegment(sketch, "E4639", {"start": v(3.57, -8.37) * mm, "end": v(3.03, -8.65) * mm});
            skLineSegment(sketch, "E4640", {"start": v(3.03, -8.65) * mm, "end": v(2.48, -8.89) * mm});
            skLineSegment(sketch, "E4641", {"start": v(2.48, -8.89) * mm, "end": v(1.97, -9.07) * mm});
            skLineSegment(sketch, "E4642", {"start": v(1.97, -9.07) * mm, "end": v(2.1, -53.5) * mm});
            skLineSegment(sketch, "E4643", {"start": v(2.1, -53.5) * mm, "end": v(2.33, -53.5) * mm});
            skLineSegment(sketch, "E4644", {"start": v(-4.04, -9.07) * mm, "end": v(-4.55, -8.89) * mm});
            skLineSegment(sketch, "E4645", {"start": v(-4.55, -8.89) * mm, "end": v(-5.1, -8.65) * mm});
            skLineSegment(sketch, "E4646", {"start": v(-5.1, -8.65) * mm, "end": v(-5.64, -8.37) * mm});
            skLineSegment(sketch, "E4647", {"start": v(-5.64, -8.37) * mm, "end": v(-6.16, -8.07) * mm});
            skLineSegment(sketch, "E4648", {"start": v(-6.16, -8.07) * mm, "end": v(-6.65, -7.73) * mm});
            skLineSegment(sketch, "E4649", {"start": v(-6.65, -7.73) * mm, "end": v(-7.13, -7.36) * mm});
            skLineSegment(sketch, "E4650", {"start": v(-7.13, -7.36) * mm, "end": v(-7.58, -6.97) * mm});
            skLineSegment(sketch, "E4651", {"start": v(-7.58, -6.97) * mm, "end": v(-8, -6.54) * mm});
            skLineSegment(sketch, "E4652", {"start": v(-8, -6.54) * mm, "end": v(-8.4, -6.1) * mm});
            skLineSegment(sketch, "E4653", {"start": v(-8.4, -6.1) * mm, "end": v(-8.77, -5.62) * mm});
            skLineSegment(sketch, "E4654", {"start": v(-8.77, -5.62) * mm, "end": v(-9.1, -5.12) * mm});
            skLineSegment(sketch, "E4655", {"start": v(-9.1, -5.12) * mm, "end": v(-9.4, -4.6) * mm});
            skLineSegment(sketch, "E4656", {"start": v(-9.4, -4.6) * mm, "end": v(-9.68, -4.07) * mm});
            skLineSegment(sketch, "E4657", {"start": v(-9.68, -4.07) * mm, "end": v(-9.92, -3.52) * mm});
            skLineSegment(sketch, "E4658", {"start": v(-9.92, -3.52) * mm, "end": v(-10.1, -3) * mm});
            skLineSegment(sketch, "E4659", {"start": v(-10.1, -3) * mm, "end": v(-54.54, -3.13) * mm});
            skLineSegment(sketch, "E4660", {"start": v(-54.54, -3.13) * mm, "end": v(-54.53, -3.37) * mm});
            skLineSegment(sketch, "E4661", {"start": v(-54.53, -3.37) * mm, "end": v(-54.22, -6.72) * mm});
            skLineSegment(sketch, "E4662", {"start": v(-54.22, -6.72) * mm, "end": v(-53.7, -10.04) * mm});
            skLineSegment(sketch, "E4663", {"start": v(-53.7, -10.04) * mm, "end": v(-52.96, -13.33) * mm});
            skLineSegment(sketch, "E4664", {"start": v(-52.96, -13.33) * mm, "end": v(-52.02, -16.57) * mm});
            skLineSegment(sketch, "E4665", {"start": v(-52.02, -16.57) * mm, "end": v(-50.88, -19.73) * mm});
            skLineSegment(sketch, "E4666", {"start": v(-50.88, -19.73) * mm, "end": v(-49.54, -22.82) * mm});
            skLineSegment(sketch, "E4667", {"start": v(-49.54, -22.82) * mm, "end": v(-48, -25.82) * mm});
            skLineSegment(sketch, "E4668", {"start": v(-48, -25.82) * mm, "end": v(-46.3, -28.72) * mm});
            skLineSegment(sketch, "E4669", {"start": v(-46.3, -28.72) * mm, "end": v(-44.4, -31.5) * mm});
            skLineSegment(sketch, "E4670", {"start": v(-44.4, -31.5) * mm, "end": v(-42.34, -34.17) * mm});
            skLineSegment(sketch, "E4671", {"start": v(-42.34, -34.17) * mm, "end": v(-40.11, -36.7) * mm});
            skLineSegment(sketch, "E4672", {"start": v(-40.11, -36.7) * mm, "end": v(-37.73, -39.08) * mm});
            skLineSegment(sketch, "E4673", {"start": v(-37.73, -39.08) * mm, "end": v(-35.2, -41.3) * mm});
            skLineSegment(sketch, "E4674", {"start": v(-35.2, -41.3) * mm, "end": v(-32.54, -43.37) * mm});
            skLineSegment(sketch, "E4675", {"start": v(-32.54, -43.37) * mm, "end": v(-29.76, -45.26) * mm});
            skLineSegment(sketch, "E4676", {"start": v(-29.76, -45.26) * mm, "end": v(-26.86, -46.97) * mm});
            skLineSegment(sketch, "E4677", {"start": v(-26.86, -46.97) * mm, "end": v(-23.86, -48.5) * mm});
            skLineSegment(sketch, "E4678", {"start": v(-23.86, -48.5) * mm, "end": v(-20.77, -49.84) * mm});
            skLineSegment(sketch, "E4679", {"start": v(-20.77, -49.84) * mm, "end": v(-17.6, -50.98) * mm});
            skLineSegment(sketch, "E4680", {"start": v(-17.6, -50.98) * mm, "end": v(-14.37, -51.92) * mm});
            skLineSegment(sketch, "E4681", {"start": v(-14.37, -51.92) * mm, "end": v(-11.08, -52.66) * mm});
            skLineSegment(sketch, "E4682", {"start": v(-11.08, -52.66) * mm, "end": v(-7.75, -53.18) * mm});
            skLineSegment(sketch, "E4683", {"start": v(-7.75, -53.18) * mm, "end": v(-4.4, -53.5) * mm});
            skLineSegment(sketch, "E4684", {"start": v(-4.4, -53.5) * mm, "end": v(-4.17, -53.5) * mm});
            skLineSegment(sketch, "E4685", {"start": v(-4.17, -53.5) * mm, "end": v(-4.04, -9.07) * mm});
            skCircle(sketch, "E4686", {"center": v(-1.04, 0) * mm, "radius": 3 * mm});
            skCircle(sketch, "E4687", {"center": v(-1.04, 0) * mm, "radius": 18.5 * mm});
            skSolve(sketch);
        }
        {
            var Q0;
            Q0=makeQuery(id+"F0.imprint","IMPRINT",FACE,{"disambiguationData":[TD([[makeQuery(id+"F0.imprint","IMPRINT",EDGE,{"derivedFrom":sQuery(id+"F0.wireOp",EDGE,"E0")}),1.0]])]});
            var Q1;
            Q1=makeQuery(id+"F0.imprint","IMPRINT",FACE,{"disambiguationData":[TD([[makeQuery(id+"F0.imprint","IMPRINT",EDGE,{"derivedFrom":sQuery(id+"F0.wireOp",EDGE,"E4518")}),-1.0]])]});
            var Q2;
            Q2=makeQuery(id+"F0.imprint","IMPRINT",FACE,{"disambiguationData":[TD([[makeQuery(id+"F0.imprint","IMPRINT",EDGE,{"derivedFrom":sQuery(id+"F0.wireOp",EDGE,"E4518")}),1.0]])]});
            var Q3;
            {var subQ0=sQuery(id+"F0.wireOp",EDGE,"E4586");Q3=makeQuery(id+"F0.imprint","IMPRINT",FACE,{"disambiguationData":[TD([[makeQuery(id+"F0.imprint","IMPRINT",EDGE,{"derivedFrom":subQ0}),1.0]])]});}
            var Q4;
            {var subQ0=sQuery(id+"F0.wireOp",EDGE,"E4627");Q4=makeQuery(id+"F0.imprint","IMPRINT",FACE,{"disambiguationData":[TD([[makeQuery(id+"F0.imprint","IMPRINT",EDGE,{"derivedFrom":subQ0}),1.0]])]});}
            var Q5;
            {var subQ1=sQuery(id+"F0.wireOp",EDGE,"E4644");Q5=makeQuery(id+"F0.imprint","IMPRINT",FACE,{"disambiguationData":[TD([[makeQuery(id+"F0.imprint","IMPRINT",EDGE,{"derivedFrom":subQ1}),1.0]])]});}
            extrude(context, id + "F1", {"entities" : qUnion([Q0, Q1, Q2, Q3, Q4, Q5]), "depth" : 5 * mm});
        }
    });
